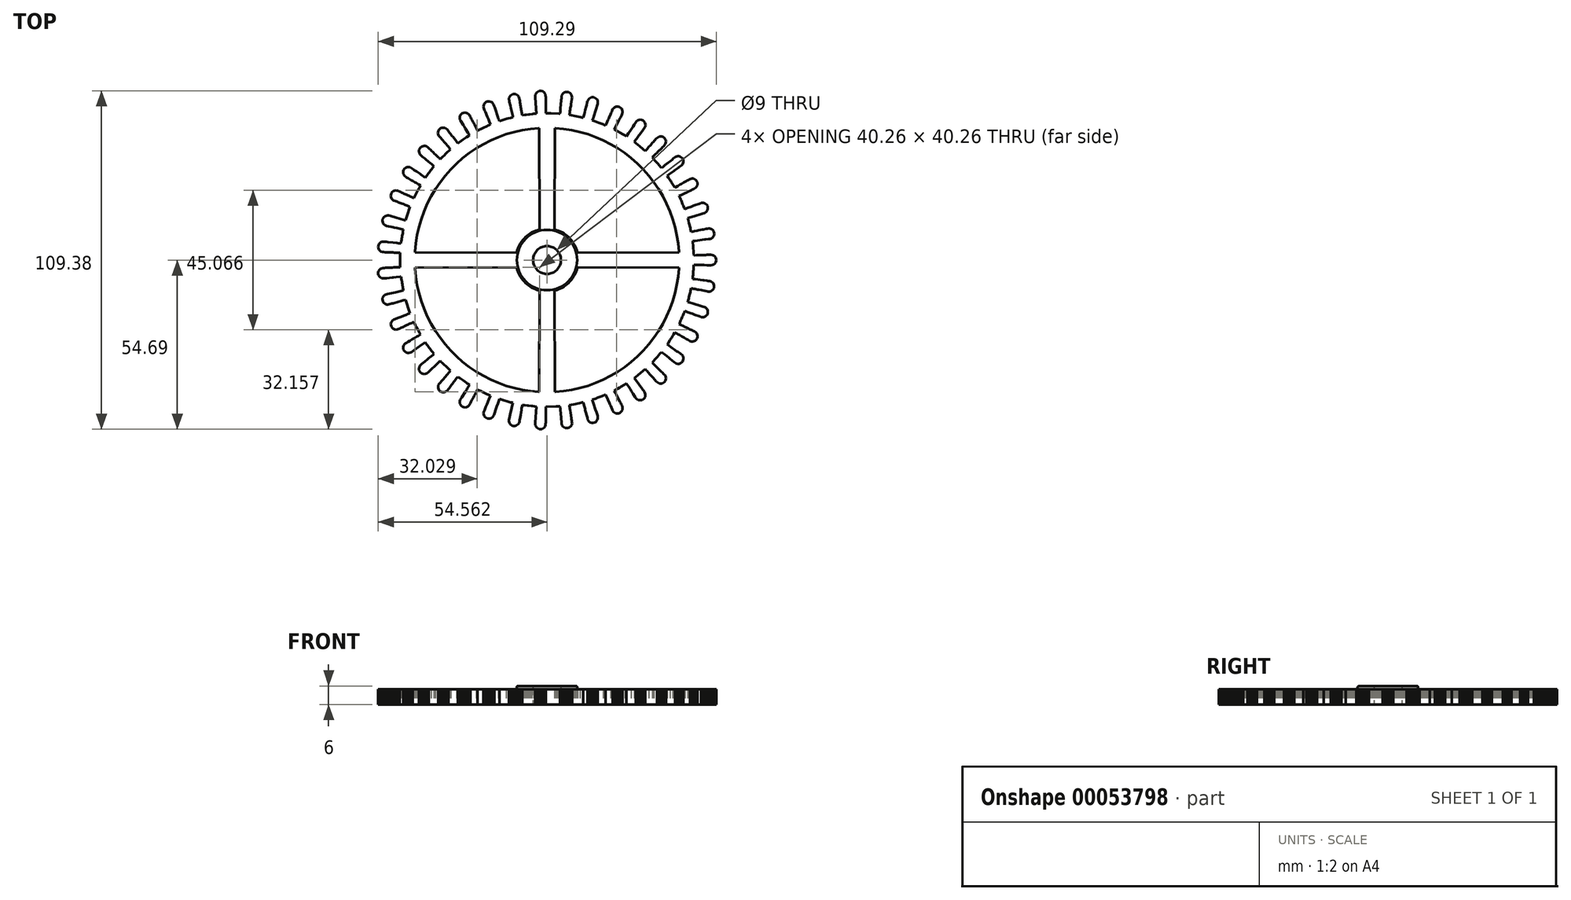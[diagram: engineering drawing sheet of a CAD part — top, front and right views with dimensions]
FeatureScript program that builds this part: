
annotation { "Feature Type Name" : "Feature", "Feature Type Description" : "" }
export const myFeature = defineFeature(function(context is Context, id is Id, definition is map)
    precondition{}
    {
        {
            var Q0;
            Q0=qCreatedBy(makeId("Top.planeOp"),FACE);
            var sketch = newSketch(context, id + "F0", { "sketchPlane" : qUnion([Q0])});
            skLineSegment(sketch, "E0", {"start": v(45.27, -1.52) * mm, "end": v(45.64, -1.53) * mm});
            skLineSegment(sketch, "E1", {"start": v(45.64, -1.53) * mm, "end": v(46.06, -1.55) * mm});
            skLineSegment(sketch, "E2", {"start": v(46.06, -1.55) * mm, "end": v(46.48, -1.56) * mm});
            skLineSegment(sketch, "E3", {"start": v(46.48, -1.56) * mm, "end": v(46.93, -1.58) * mm});
            skLineSegment(sketch, "E4", {"start": v(46.93, -1.58) * mm, "end": v(47.35, -1.59) * mm});
            skLineSegment(sketch, "E5", {"start": v(47.35, -1.59) * mm, "end": v(47.77, -1.6) * mm});
            skLineSegment(sketch, "E6", {"start": v(47.77, -1.6) * mm, "end": v(48.22, -1.62) * mm});
            skLineSegment(sketch, "E7", {"start": v(48.22, -1.62) * mm, "end": v(48.64, -1.63) * mm});
            skLineSegment(sketch, "E8", {"start": v(48.64, -1.63) * mm, "end": v(49.07, -1.64) * mm});
            skLineSegment(sketch, "E9", {"start": v(49.07, -1.64) * mm, "end": v(49.52, -1.66) * mm});
            skLineSegment(sketch, "E10", {"start": v(49.52, -1.66) * mm, "end": v(49.94, -1.67) * mm});
            skLineSegment(sketch, "E11", {"start": v(49.94, -1.67) * mm, "end": v(50.36, -1.69) * mm});
            skLineSegment(sketch, "E12", {"start": v(50.36, -1.69) * mm, "end": v(50.8, -1.7) * mm});
            skLineSegment(sketch, "E13", {"start": v(50.8, -1.7) * mm, "end": v(51.25, -1.65) * mm});
            skLineSegment(sketch, "E14", {"start": v(51.25, -1.65) * mm, "end": v(51.67, -1.48) * mm});
            skLineSegment(sketch, "E15", {"start": v(51.67, -1.48) * mm, "end": v(52.03, -1.21) * mm});
            skLineSegment(sketch, "E16", {"start": v(52.03, -1.21) * mm, "end": v(52.3, -0.86) * mm});
            skLineSegment(sketch, "E17", {"start": v(52.3, -0.86) * mm, "end": v(52.48, -0.44) * mm});
            skLineSegment(sketch, "E18", {"start": v(52.48, -0.44) * mm, "end": v(52.53, 0) * mm});
            skLineSegment(sketch, "E19", {"start": v(52.53, 0) * mm, "end": v(52.48, 0.44) * mm});
            skLineSegment(sketch, "E20", {"start": v(52.48, 0.44) * mm, "end": v(52.3, 0.86) * mm});
            skLineSegment(sketch, "E21", {"start": v(52.3, 0.86) * mm, "end": v(52.03, 1.21) * mm});
            skLineSegment(sketch, "E22", {"start": v(52.03, 1.21) * mm, "end": v(51.67, 1.48) * mm});
            skLineSegment(sketch, "E23", {"start": v(51.67, 1.48) * mm, "end": v(51.25, 1.65) * mm});
            skLineSegment(sketch, "E24", {"start": v(51.25, 1.65) * mm, "end": v(50.8, 1.7) * mm});
            skLineSegment(sketch, "E25", {"start": v(50.8, 1.7) * mm, "end": v(50.39, 1.69) * mm});
            skLineSegment(sketch, "E26", {"start": v(50.39, 1.69) * mm, "end": v(49.96, 1.67) * mm});
            skLineSegment(sketch, "E27", {"start": v(49.96, 1.67) * mm, "end": v(49.52, 1.66) * mm});
            skLineSegment(sketch, "E28", {"start": v(49.52, 1.66) * mm, "end": v(49.1, 1.65) * mm});
            skLineSegment(sketch, "E29", {"start": v(49.1, 1.65) * mm, "end": v(48.67, 1.63) * mm});
            skLineSegment(sketch, "E30", {"start": v(48.67, 1.63) * mm, "end": v(48.22, 1.62) * mm});
            skLineSegment(sketch, "E31", {"start": v(48.22, 1.62) * mm, "end": v(47.8, 1.6) * mm});
            skLineSegment(sketch, "E32", {"start": v(47.8, 1.6) * mm, "end": v(47.38, 1.6) * mm});
            skLineSegment(sketch, "E33", {"start": v(47.38, 1.6) * mm, "end": v(46.93, 1.58) * mm});
            skLineSegment(sketch, "E34", {"start": v(46.93, 1.58) * mm, "end": v(46.51, 1.56) * mm});
            skLineSegment(sketch, "E35", {"start": v(46.51, 1.56) * mm, "end": v(46.09, 1.55) * mm});
            skLineSegment(sketch, "E36", {"start": v(46.09, 1.55) * mm, "end": v(45.64, 1.53) * mm});
            skLineSegment(sketch, "E37", {"start": v(45.64, 1.53) * mm, "end": v(45.27, 1.52) * mm});
            skLineSegment(sketch, "E38", {"start": v(45.27, 1.52) * mm, "end": v(45.24, 1.94) * mm});
            skLineSegment(sketch, "E39", {"start": v(45.24, 1.94) * mm, "end": v(45.2, 2.36) * mm});
            skLineSegment(sketch, "E40", {"start": v(45.2, 2.36) * mm, "end": v(45.17, 2.78) * mm});
            skLineSegment(sketch, "E41", {"start": v(45.17, 2.78) * mm, "end": v(45.13, 3.2) * mm});
            skLineSegment(sketch, "E42", {"start": v(45.13, 3.2) * mm, "end": v(45.1, 3.62) * mm});
            skLineSegment(sketch, "E43", {"start": v(45.1, 3.62) * mm, "end": v(45.07, 4.04) * mm});
            skLineSegment(sketch, "E44", {"start": v(45.07, 4.04) * mm, "end": v(45.03, 4.46) * mm});
            skLineSegment(sketch, "E45", {"start": v(45.03, 4.46) * mm, "end": v(45, 4.88) * mm});
            skLineSegment(sketch, "E46", {"start": v(45, 4.88) * mm, "end": v(44.97, 5.3) * mm});
            skLineSegment(sketch, "E47", {"start": v(44.97, 5.3) * mm, "end": v(44.93, 5.72) * mm});
            skLineSegment(sketch, "E48", {"start": v(44.93, 5.72) * mm, "end": v(44.9, 6.11) * mm});
            skLineSegment(sketch, "E49", {"start": v(44.9, 6.11) * mm, "end": v(45.32, 6.17) * mm});
            skLineSegment(sketch, "E50", {"start": v(45.32, 6.17) * mm, "end": v(45.74, 6.22) * mm});
            skLineSegment(sketch, "E51", {"start": v(45.74, 6.22) * mm, "end": v(46.18, 6.28) * mm});
            skLineSegment(sketch, "E52", {"start": v(46.18, 6.28) * mm, "end": v(46.6, 6.33) * mm});
            skLineSegment(sketch, "E53", {"start": v(46.6, 6.33) * mm, "end": v(47.02, 6.39) * mm});
            skLineSegment(sketch, "E54", {"start": v(47.02, 6.39) * mm, "end": v(47.46, 6.44) * mm});
            skLineSegment(sketch, "E55", {"start": v(47.46, 6.44) * mm, "end": v(47.88, 6.5) * mm});
            skLineSegment(sketch, "E56", {"start": v(47.88, 6.5) * mm, "end": v(48.3, 6.55) * mm});
            skLineSegment(sketch, "E57", {"start": v(48.3, 6.55) * mm, "end": v(48.75, 6.61) * mm});
            skLineSegment(sketch, "E58", {"start": v(48.75, 6.61) * mm, "end": v(49.16, 6.66) * mm});
            skLineSegment(sketch, "E59", {"start": v(49.16, 6.66) * mm, "end": v(49.58, 6.72) * mm});
            skLineSegment(sketch, "E60", {"start": v(49.58, 6.72) * mm, "end": v(50.03, 6.78) * mm});
            skLineSegment(sketch, "E61", {"start": v(50.03, 6.78) * mm, "end": v(50.48, 6.84) * mm});
            skLineSegment(sketch, "E62", {"start": v(50.48, 6.84) * mm, "end": v(50.9, 6.99) * mm});
            skLineSegment(sketch, "E63", {"start": v(50.9, 6.99) * mm, "end": v(51.28, 7.24) * mm});
            skLineSegment(sketch, "E64", {"start": v(51.28, 7.24) * mm, "end": v(51.57, 7.58) * mm});
            skLineSegment(sketch, "E65", {"start": v(51.57, 7.58) * mm, "end": v(51.76, 7.98) * mm});
            skLineSegment(sketch, "E66", {"start": v(51.76, 7.98) * mm, "end": v(51.85, 8.42) * mm});
            skLineSegment(sketch, "E67", {"start": v(51.85, 8.42) * mm, "end": v(51.8, 8.87) * mm});
            skLineSegment(sketch, "E68", {"start": v(51.8, 8.87) * mm, "end": v(51.66, 9.29) * mm});
            skLineSegment(sketch, "E69", {"start": v(51.66, 9.29) * mm, "end": v(51.4, 9.66) * mm});
            skLineSegment(sketch, "E70", {"start": v(51.4, 9.66) * mm, "end": v(51.06, 9.94) * mm});
            skLineSegment(sketch, "E71", {"start": v(51.06, 9.94) * mm, "end": v(50.65, 10.13) * mm});
            skLineSegment(sketch, "E72", {"start": v(50.65, 10.13) * mm, "end": v(50.2, 10.2) * mm});
            skLineSegment(sketch, "E73", {"start": v(50.2, 10.2) * mm, "end": v(50.12, 10.2) * mm});
            skLineSegment(sketch, "E74", {"start": v(50.12, 10.2) * mm, "end": v(49.67, 10.15) * mm});
            skLineSegment(sketch, "E75", {"start": v(49.67, 10.15) * mm, "end": v(49.25, 10.06) * mm});
            skLineSegment(sketch, "E76", {"start": v(49.25, 10.06) * mm, "end": v(48.84, 9.98) * mm});
            skLineSegment(sketch, "E77", {"start": v(48.84, 9.98) * mm, "end": v(48.4, 9.9) * mm});
            skLineSegment(sketch, "E78", {"start": v(48.4, 9.9) * mm, "end": v(47.98, 9.82) * mm});
            skLineSegment(sketch, "E79", {"start": v(47.98, 9.82) * mm, "end": v(47.57, 9.74) * mm});
            skLineSegment(sketch, "E80", {"start": v(47.57, 9.74) * mm, "end": v(47.13, 9.65) * mm});
            skLineSegment(sketch, "E81", {"start": v(47.13, 9.65) * mm, "end": v(46.72, 9.57) * mm});
            skLineSegment(sketch, "E82", {"start": v(46.72, 9.57) * mm, "end": v(46.3, 9.49) * mm});
            skLineSegment(sketch, "E83", {"start": v(46.3, 9.49) * mm, "end": v(45.86, 9.4) * mm});
            skLineSegment(sketch, "E84", {"start": v(45.86, 9.4) * mm, "end": v(45.45, 9.32) * mm});
            skLineSegment(sketch, "E85", {"start": v(45.45, 9.32) * mm, "end": v(45.03, 9.24) * mm});
            skLineSegment(sketch, "E86", {"start": v(45.03, 9.24) * mm, "end": v(44.6, 9.15) * mm});
            skLineSegment(sketch, "E87", {"start": v(44.6, 9.15) * mm, "end": v(44.41, 9.12) * mm});
            skLineSegment(sketch, "E88", {"start": v(44.41, 9.12) * mm, "end": v(44.31, 9.53) * mm});
            skLineSegment(sketch, "E89", {"start": v(44.31, 9.53) * mm, "end": v(44.2, 9.94) * mm});
            skLineSegment(sketch, "E90", {"start": v(44.2, 9.94) * mm, "end": v(44.1, 10.35) * mm});
            skLineSegment(sketch, "E91", {"start": v(44.1, 10.35) * mm, "end": v(44, 10.75) * mm});
            skLineSegment(sketch, "E92", {"start": v(44, 10.75) * mm, "end": v(43.9, 11.16) * mm});
            skLineSegment(sketch, "E93", {"start": v(43.9, 11.16) * mm, "end": v(43.8, 11.57) * mm});
            skLineSegment(sketch, "E94", {"start": v(43.8, 11.57) * mm, "end": v(43.7, 11.98) * mm});
            skLineSegment(sketch, "E95", {"start": v(43.7, 11.98) * mm, "end": v(43.6, 12.4) * mm});
            skLineSegment(sketch, "E96", {"start": v(43.6, 12.4) * mm, "end": v(43.5, 12.8) * mm});
            skLineSegment(sketch, "E97", {"start": v(43.5, 12.8) * mm, "end": v(43.4, 13.21) * mm});
            skLineSegment(sketch, "E98", {"start": v(43.4, 13.21) * mm, "end": v(43.3, 13.59) * mm});
            skLineSegment(sketch, "E99", {"start": v(43.3, 13.59) * mm, "end": v(43.71, 13.7) * mm});
            skLineSegment(sketch, "E100", {"start": v(43.71, 13.7) * mm, "end": v(44.12, 13.83) * mm});
            skLineSegment(sketch, "E101", {"start": v(44.12, 13.83) * mm, "end": v(44.55, 13.96) * mm});
            skLineSegment(sketch, "E102", {"start": v(44.55, 13.96) * mm, "end": v(44.95, 14.08) * mm});
            skLineSegment(sketch, "E103", {"start": v(44.95, 14.08) * mm, "end": v(45.36, 14.2) * mm});
            skLineSegment(sketch, "E104", {"start": v(45.36, 14.2) * mm, "end": v(45.79, 14.33) * mm});
            skLineSegment(sketch, "E105", {"start": v(45.79, 14.33) * mm, "end": v(46.2, 14.45) * mm});
            skLineSegment(sketch, "E106", {"start": v(46.2, 14.45) * mm, "end": v(46.6, 14.57) * mm});
            skLineSegment(sketch, "E107", {"start": v(46.6, 14.57) * mm, "end": v(47.03, 14.7) * mm});
            skLineSegment(sketch, "E108", {"start": v(47.03, 14.7) * mm, "end": v(47.43, 14.82) * mm});
            skLineSegment(sketch, "E109", {"start": v(47.43, 14.82) * mm, "end": v(47.83, 14.94) * mm});
            skLineSegment(sketch, "E110", {"start": v(47.83, 14.94) * mm, "end": v(48.26, 15.07) * mm});
            skLineSegment(sketch, "E111", {"start": v(48.26, 15.07) * mm, "end": v(48.7, 15.2) * mm});
            skLineSegment(sketch, "E112", {"start": v(48.7, 15.2) * mm, "end": v(49.1, 15.41) * mm});
            skLineSegment(sketch, "E113", {"start": v(49.1, 15.41) * mm, "end": v(49.42, 15.72) * mm});
            skLineSegment(sketch, "E114", {"start": v(49.42, 15.72) * mm, "end": v(49.66, 16.1) * mm});
            skLineSegment(sketch, "E115", {"start": v(49.66, 16.1) * mm, "end": v(49.79, 16.53) * mm});
            skLineSegment(sketch, "E116", {"start": v(49.79, 16.53) * mm, "end": v(49.8, 16.98) * mm});
            skLineSegment(sketch, "E117", {"start": v(49.8, 16.98) * mm, "end": v(49.69, 17.42) * mm});
            skLineSegment(sketch, "E118", {"start": v(49.69, 17.42) * mm, "end": v(49.47, 17.8) * mm});
            skLineSegment(sketch, "E119", {"start": v(49.47, 17.8) * mm, "end": v(49.16, 18.13) * mm});
            skLineSegment(sketch, "E120", {"start": v(49.16, 18.13) * mm, "end": v(48.77, 18.36) * mm});
            skLineSegment(sketch, "E121", {"start": v(48.77, 18.36) * mm, "end": v(48.34, 18.48) * mm});
            skLineSegment(sketch, "E122", {"start": v(48.34, 18.48) * mm, "end": v(48.07, 18.5) * mm});
            skLineSegment(sketch, "E123", {"start": v(48.07, 18.5) * mm, "end": v(47.63, 18.43) * mm});
            skLineSegment(sketch, "E124", {"start": v(47.63, 18.43) * mm, "end": v(47.2, 18.27) * mm});
            skLineSegment(sketch, "E125", {"start": v(47.2, 18.27) * mm, "end": v(46.8, 18.12) * mm});
            skLineSegment(sketch, "E126", {"start": v(46.8, 18.12) * mm, "end": v(46.4, 17.98) * mm});
            skLineSegment(sketch, "E127", {"start": v(46.4, 17.98) * mm, "end": v(45.98, 17.82) * mm});
            skLineSegment(sketch, "E128", {"start": v(45.98, 17.82) * mm, "end": v(45.59, 17.68) * mm});
            skLineSegment(sketch, "E129", {"start": v(45.59, 17.68) * mm, "end": v(45.2, 17.53) * mm});
            skLineSegment(sketch, "E130", {"start": v(45.2, 17.53) * mm, "end": v(44.77, 17.37) * mm});
            skLineSegment(sketch, "E131", {"start": v(44.77, 17.37) * mm, "end": v(44.37, 17.23) * mm});
            skLineSegment(sketch, "E132", {"start": v(44.37, 17.23) * mm, "end": v(43.98, 17.08) * mm});
            skLineSegment(sketch, "E133", {"start": v(43.98, 17.08) * mm, "end": v(43.56, 16.92) * mm});
            skLineSegment(sketch, "E134", {"start": v(43.56, 16.92) * mm, "end": v(43.16, 16.78) * mm});
            skLineSegment(sketch, "E135", {"start": v(43.16, 16.78) * mm, "end": v(42.77, 16.63) * mm});
            skLineSegment(sketch, "E136", {"start": v(42.77, 16.63) * mm, "end": v(42.35, 16.48) * mm});
            skLineSegment(sketch, "E137", {"start": v(42.35, 16.48) * mm, "end": v(42.18, 16.86) * mm});
            skLineSegment(sketch, "E138", {"start": v(42.18, 16.86) * mm, "end": v(42.01, 17.25) * mm});
            skLineSegment(sketch, "E139", {"start": v(42.01, 17.25) * mm, "end": v(41.85, 17.64) * mm});
            skLineSegment(sketch, "E140", {"start": v(41.85, 17.64) * mm, "end": v(41.68, 18.03) * mm});
            skLineSegment(sketch, "E141", {"start": v(41.68, 18.03) * mm, "end": v(41.52, 18.42) * mm});
            skLineSegment(sketch, "E142", {"start": v(41.52, 18.42) * mm, "end": v(41.35, 18.8) * mm});
            skLineSegment(sketch, "E143", {"start": v(41.35, 18.8) * mm, "end": v(41.19, 19.2) * mm});
            skLineSegment(sketch, "E144", {"start": v(41.19, 19.2) * mm, "end": v(41.02, 19.58) * mm});
            skLineSegment(sketch, "E145", {"start": v(41.02, 19.58) * mm, "end": v(40.86, 19.97) * mm});
            skLineSegment(sketch, "E146", {"start": v(40.86, 19.97) * mm, "end": v(40.7, 20.35) * mm});
            skLineSegment(sketch, "E147", {"start": v(40.7, 20.35) * mm, "end": v(40.54, 20.71) * mm});
            skLineSegment(sketch, "E148", {"start": v(40.54, 20.71) * mm, "end": v(40.92, 20.9) * mm});
            skLineSegment(sketch, "E149", {"start": v(40.92, 20.9) * mm, "end": v(41.3, 21.08) * mm});
            skLineSegment(sketch, "E150", {"start": v(41.3, 21.08) * mm, "end": v(41.7, 21.28) * mm});
            skLineSegment(sketch, "E151", {"start": v(41.7, 21.28) * mm, "end": v(42.08, 21.46) * mm});
            skLineSegment(sketch, "E152", {"start": v(42.08, 21.46) * mm, "end": v(42.46, 21.64) * mm});
            skLineSegment(sketch, "E153", {"start": v(42.46, 21.64) * mm, "end": v(42.87, 21.84) * mm});
            skLineSegment(sketch, "E154", {"start": v(42.87, 21.84) * mm, "end": v(43.25, 22.02) * mm});
            skLineSegment(sketch, "E155", {"start": v(43.25, 22.02) * mm, "end": v(43.63, 22.2) * mm});
            skLineSegment(sketch, "E156", {"start": v(43.63, 22.2) * mm, "end": v(44.03, 22.4) * mm});
            skLineSegment(sketch, "E157", {"start": v(44.03, 22.4) * mm, "end": v(44.4, 22.59) * mm});
            skLineSegment(sketch, "E158", {"start": v(44.4, 22.59) * mm, "end": v(44.79, 22.77) * mm});
            skLineSegment(sketch, "E159", {"start": v(44.79, 22.77) * mm, "end": v(45.2, 22.97) * mm});
            skLineSegment(sketch, "E160", {"start": v(45.2, 22.97) * mm, "end": v(45.6, 23.17) * mm});
            skLineSegment(sketch, "E161", {"start": v(45.6, 23.17) * mm, "end": v(45.96, 23.44) * mm});
            skLineSegment(sketch, "E162", {"start": v(45.96, 23.44) * mm, "end": v(46.23, 23.8) * mm});
            skLineSegment(sketch, "E163", {"start": v(46.23, 23.8) * mm, "end": v(46.4, 24.21) * mm});
            skLineSegment(sketch, "E164", {"start": v(46.4, 24.21) * mm, "end": v(46.46, 24.66) * mm});
            skLineSegment(sketch, "E165", {"start": v(46.46, 24.66) * mm, "end": v(46.4, 25.1) * mm});
            skLineSegment(sketch, "E166", {"start": v(46.4, 25.1) * mm, "end": v(46.22, 25.51) * mm});
            skLineSegment(sketch, "E167", {"start": v(46.22, 25.51) * mm, "end": v(45.94, 25.87) * mm});
            skLineSegment(sketch, "E168", {"start": v(45.94, 25.87) * mm, "end": v(45.58, 26.13) * mm});
            skLineSegment(sketch, "E169", {"start": v(45.58, 26.13) * mm, "end": v(45.17, 26.3) * mm});
            skLineSegment(sketch, "E170", {"start": v(45.17, 26.3) * mm, "end": v(44.72, 26.35) * mm});
            skLineSegment(sketch, "E171", {"start": v(44.72, 26.35) * mm, "end": v(44.28, 26.28) * mm});
            skLineSegment(sketch, "E172", {"start": v(44.28, 26.28) * mm, "end": v(43.9, 26.1) * mm});
            skLineSegment(sketch, "E173", {"start": v(43.9, 26.1) * mm, "end": v(43.52, 25.9) * mm});
            skLineSegment(sketch, "E174", {"start": v(43.52, 25.9) * mm, "end": v(43.14, 25.68) * mm});
            skLineSegment(sketch, "E175", {"start": v(43.14, 25.68) * mm, "end": v(42.78, 25.48) * mm});
            skLineSegment(sketch, "E176", {"start": v(42.78, 25.48) * mm, "end": v(42.4, 25.27) * mm});
            skLineSegment(sketch, "E177", {"start": v(42.4, 25.27) * mm, "end": v(42.02, 25.05) * mm});
            skLineSegment(sketch, "E178", {"start": v(42.02, 25.05) * mm, "end": v(41.65, 24.84) * mm});
            skLineSegment(sketch, "E179", {"start": v(41.65, 24.84) * mm, "end": v(41.28, 24.63) * mm});
            skLineSegment(sketch, "E180", {"start": v(41.28, 24.63) * mm, "end": v(40.9, 24.4) * mm});
            skLineSegment(sketch, "E181", {"start": v(40.9, 24.4) * mm, "end": v(40.53, 24.2) * mm});
            skLineSegment(sketch, "E182", {"start": v(40.53, 24.2) * mm, "end": v(40.16, 24) * mm});
            skLineSegment(sketch, "E183", {"start": v(40.16, 24) * mm, "end": v(39.77, 23.77) * mm});
            skLineSegment(sketch, "E184", {"start": v(39.77, 23.77) * mm, "end": v(39.4, 23.56) * mm});
            skLineSegment(sketch, "E185", {"start": v(39.4, 23.56) * mm, "end": v(39.13, 23.4) * mm});
            skLineSegment(sketch, "E186", {"start": v(39.13, 23.4) * mm, "end": v(38.9, 23.76) * mm});
            skLineSegment(sketch, "E187", {"start": v(38.9, 23.76) * mm, "end": v(38.67, 24.12) * mm});
            skLineSegment(sketch, "E188", {"start": v(38.67, 24.12) * mm, "end": v(38.45, 24.48) * mm});
            skLineSegment(sketch, "E189", {"start": v(38.45, 24.48) * mm, "end": v(38.22, 24.83) * mm});
            skLineSegment(sketch, "E190", {"start": v(38.22, 24.83) * mm, "end": v(38, 25.19) * mm});
            skLineSegment(sketch, "E191", {"start": v(38, 25.19) * mm, "end": v(37.77, 25.55) * mm});
            skLineSegment(sketch, "E192", {"start": v(37.77, 25.55) * mm, "end": v(37.55, 25.9) * mm});
            skLineSegment(sketch, "E193", {"start": v(37.55, 25.9) * mm, "end": v(37.32, 26.26) * mm});
            skLineSegment(sketch, "E194", {"start": v(37.32, 26.26) * mm, "end": v(37.1, 26.61) * mm});
            skLineSegment(sketch, "E195", {"start": v(37.1, 26.61) * mm, "end": v(36.87, 26.97) * mm});
            skLineSegment(sketch, "E196", {"start": v(36.87, 26.97) * mm, "end": v(36.66, 27.3) * mm});
            skLineSegment(sketch, "E197", {"start": v(36.66, 27.3) * mm, "end": v(37, 27.54) * mm});
            skLineSegment(sketch, "E198", {"start": v(37, 27.54) * mm, "end": v(37.35, 27.78) * mm});
            skLineSegment(sketch, "E199", {"start": v(37.35, 27.78) * mm, "end": v(37.72, 28.04) * mm});
            skLineSegment(sketch, "E200", {"start": v(37.72, 28.04) * mm, "end": v(38.07, 28.28) * mm});
            skLineSegment(sketch, "E201", {"start": v(38.07, 28.28) * mm, "end": v(38.41, 28.53) * mm});
            skLineSegment(sketch, "E202", {"start": v(38.41, 28.53) * mm, "end": v(38.78, 28.79) * mm});
            skLineSegment(sketch, "E203", {"start": v(38.78, 28.79) * mm, "end": v(39.13, 29.03) * mm});
            skLineSegment(sketch, "E204", {"start": v(39.13, 29.03) * mm, "end": v(39.47, 29.27) * mm});
            skLineSegment(sketch, "E205", {"start": v(39.47, 29.27) * mm, "end": v(39.84, 29.53) * mm});
            skLineSegment(sketch, "E206", {"start": v(39.84, 29.53) * mm, "end": v(40.18, 29.77) * mm});
            skLineSegment(sketch, "E207", {"start": v(40.18, 29.77) * mm, "end": v(40.53, 30.01) * mm});
            skLineSegment(sketch, "E208", {"start": v(40.53, 30.01) * mm, "end": v(40.9, 30.27) * mm});
            skLineSegment(sketch, "E209", {"start": v(40.9, 30.27) * mm, "end": v(41.27, 30.54) * mm});
            skLineSegment(sketch, "E210", {"start": v(41.27, 30.54) * mm, "end": v(41.58, 30.86) * mm});
            skLineSegment(sketch, "E211", {"start": v(41.58, 30.86) * mm, "end": v(41.79, 31.26) * mm});
            skLineSegment(sketch, "E212", {"start": v(41.79, 31.26) * mm, "end": v(41.9, 31.7) * mm});
            skLineSegment(sketch, "E213", {"start": v(41.9, 31.7) * mm, "end": v(41.87, 32.14) * mm});
            skLineSegment(sketch, "E214", {"start": v(41.87, 32.14) * mm, "end": v(41.74, 32.57) * mm});
            skLineSegment(sketch, "E215", {"start": v(41.74, 32.57) * mm, "end": v(41.5, 32.95) * mm});
            skLineSegment(sketch, "E216", {"start": v(41.5, 32.95) * mm, "end": v(41.17, 33.25) * mm});
            skLineSegment(sketch, "E217", {"start": v(41.17, 33.25) * mm, "end": v(40.77, 33.46) * mm});
            skLineSegment(sketch, "E218", {"start": v(40.77, 33.46) * mm, "end": v(40.33, 33.55) * mm});
            skLineSegment(sketch, "E219", {"start": v(40.33, 33.55) * mm, "end": v(40.15, 33.56) * mm});
            skLineSegment(sketch, "E220", {"start": v(40.15, 33.56) * mm, "end": v(39.71, 33.49) * mm});
            skLineSegment(sketch, "E221", {"start": v(39.71, 33.49) * mm, "end": v(39.3, 33.3) * mm});
            skLineSegment(sketch, "E222", {"start": v(39.3, 33.3) * mm, "end": v(38.97, 33.05) * mm});
            skLineSegment(sketch, "E223", {"start": v(38.97, 33.05) * mm, "end": v(38.64, 32.79) * mm});
            skLineSegment(sketch, "E224", {"start": v(38.64, 32.79) * mm, "end": v(38.3, 32.5) * mm});
            skLineSegment(sketch, "E225", {"start": v(38.3, 32.5) * mm, "end": v(37.96, 32.24) * mm});
            skLineSegment(sketch, "E226", {"start": v(37.96, 32.24) * mm, "end": v(37.63, 31.98) * mm});
            skLineSegment(sketch, "E227", {"start": v(37.63, 31.98) * mm, "end": v(37.28, 31.7) * mm});
            skLineSegment(sketch, "E228", {"start": v(37.28, 31.7) * mm, "end": v(36.95, 31.44) * mm});
            skLineSegment(sketch, "E229", {"start": v(36.95, 31.44) * mm, "end": v(36.63, 31.17) * mm});
            skLineSegment(sketch, "E230", {"start": v(36.63, 31.17) * mm, "end": v(36.28, 30.89) * mm});
            skLineSegment(sketch, "E231", {"start": v(36.28, 30.89) * mm, "end": v(35.95, 30.63) * mm});
            skLineSegment(sketch, "E232", {"start": v(35.95, 30.63) * mm, "end": v(35.62, 30.36) * mm});
            skLineSegment(sketch, "E233", {"start": v(35.62, 30.36) * mm, "end": v(35.27, 30.08) * mm});
            skLineSegment(sketch, "E234", {"start": v(35.27, 30.08) * mm, "end": v(34.94, 29.82) * mm});
            skLineSegment(sketch, "E235", {"start": v(34.94, 29.82) * mm, "end": v(34.84, 29.73) * mm});
            skLineSegment(sketch, "E236", {"start": v(34.84, 29.73) * mm, "end": v(34.56, 30.05) * mm});
            skLineSegment(sketch, "E237", {"start": v(34.56, 30.05) * mm, "end": v(34.28, 30.36) * mm});
            skLineSegment(sketch, "E238", {"start": v(34.28, 30.36) * mm, "end": v(34, 30.68) * mm});
            skLineSegment(sketch, "E239", {"start": v(34, 30.68) * mm, "end": v(33.72, 31) * mm});
            skLineSegment(sketch, "E240", {"start": v(33.72, 31) * mm, "end": v(33.44, 31.31) * mm});
            skLineSegment(sketch, "E241", {"start": v(33.44, 31.31) * mm, "end": v(33.16, 31.63) * mm});
            skLineSegment(sketch, "E242", {"start": v(33.16, 31.63) * mm, "end": v(32.88, 31.94) * mm});
            skLineSegment(sketch, "E243", {"start": v(32.88, 31.94) * mm, "end": v(32.6, 32.26) * mm});
            skLineSegment(sketch, "E244", {"start": v(32.6, 32.26) * mm, "end": v(32.32, 32.57) * mm});
            skLineSegment(sketch, "E245", {"start": v(32.32, 32.57) * mm, "end": v(32.04, 32.89) * mm});
            skLineSegment(sketch, "E246", {"start": v(32.04, 32.89) * mm, "end": v(31.78, 33.18) * mm});
            skLineSegment(sketch, "E247", {"start": v(31.78, 33.18) * mm, "end": v(32.08, 33.47) * mm});
            skLineSegment(sketch, "E248", {"start": v(32.08, 33.47) * mm, "end": v(32.39, 33.77) * mm});
            skLineSegment(sketch, "E249", {"start": v(32.39, 33.77) * mm, "end": v(32.7, 34.08) * mm});
            skLineSegment(sketch, "E250", {"start": v(32.7, 34.08) * mm, "end": v(33, 34.38) * mm});
            skLineSegment(sketch, "E251", {"start": v(33, 34.38) * mm, "end": v(33.31, 34.67) * mm});
            skLineSegment(sketch, "E252", {"start": v(33.31, 34.67) * mm, "end": v(33.63, 34.99) * mm});
            skLineSegment(sketch, "E253", {"start": v(33.63, 34.99) * mm, "end": v(33.93, 35.28) * mm});
            skLineSegment(sketch, "E254", {"start": v(33.93, 35.28) * mm, "end": v(34.24, 35.57) * mm});
            skLineSegment(sketch, "E255", {"start": v(34.24, 35.57) * mm, "end": v(34.56, 35.89) * mm});
            skLineSegment(sketch, "E256", {"start": v(34.56, 35.89) * mm, "end": v(34.86, 36.18) * mm});
            skLineSegment(sketch, "E257", {"start": v(34.86, 36.18) * mm, "end": v(35.16, 36.48) * mm});
            skLineSegment(sketch, "E258", {"start": v(35.16, 36.48) * mm, "end": v(35.48, 36.8) * mm});
            skLineSegment(sketch, "E259", {"start": v(35.48, 36.8) * mm, "end": v(35.8, 37.12) * mm});
            skLineSegment(sketch, "E260", {"start": v(35.8, 37.12) * mm, "end": v(36.06, 37.49) * mm});
            skLineSegment(sketch, "E261", {"start": v(36.06, 37.49) * mm, "end": v(36.2, 37.91) * mm});
            skLineSegment(sketch, "E262", {"start": v(36.2, 37.91) * mm, "end": v(36.24, 38.36) * mm});
            skLineSegment(sketch, "E263", {"start": v(36.24, 38.36) * mm, "end": v(36.15, 38.8) * mm});
            skLineSegment(sketch, "E264", {"start": v(36.15, 38.8) * mm, "end": v(35.95, 39.2) * mm});
            skLineSegment(sketch, "E265", {"start": v(35.95, 39.2) * mm, "end": v(35.65, 39.53) * mm});
            skLineSegment(sketch, "E266", {"start": v(35.65, 39.53) * mm, "end": v(35.27, 39.78) * mm});
            skLineSegment(sketch, "E267", {"start": v(35.27, 39.78) * mm, "end": v(34.85, 39.92) * mm});
            skLineSegment(sketch, "E268", {"start": v(34.85, 39.92) * mm, "end": v(34.58, 39.95) * mm});
            skLineSegment(sketch, "E269", {"start": v(34.58, 39.95) * mm, "end": v(34.13, 39.9) * mm});
            skLineSegment(sketch, "E270", {"start": v(34.13, 39.9) * mm, "end": v(33.72, 39.74) * mm});
            skLineSegment(sketch, "E271", {"start": v(33.72, 39.74) * mm, "end": v(33.36, 39.47) * mm});
            skLineSegment(sketch, "E272", {"start": v(33.36, 39.47) * mm, "end": v(33.05, 39.13) * mm});
            skLineSegment(sketch, "E273", {"start": v(33.05, 39.13) * mm, "end": v(32.76, 38.82) * mm});
            skLineSegment(sketch, "E274", {"start": v(32.76, 38.82) * mm, "end": v(32.48, 38.5) * mm});
            skLineSegment(sketch, "E275", {"start": v(32.48, 38.5) * mm, "end": v(32.18, 38.17) * mm});
            skLineSegment(sketch, "E276", {"start": v(32.18, 38.17) * mm, "end": v(31.9, 37.86) * mm});
            skLineSegment(sketch, "E277", {"start": v(31.9, 37.86) * mm, "end": v(31.62, 37.54) * mm});
            skLineSegment(sketch, "E278", {"start": v(31.62, 37.54) * mm, "end": v(31.32, 37.21) * mm});
            skLineSegment(sketch, "E279", {"start": v(31.32, 37.21) * mm, "end": v(31.03, 36.9) * mm});
            skLineSegment(sketch, "E280", {"start": v(31.03, 36.9) * mm, "end": v(30.75, 36.58) * mm});
            skLineSegment(sketch, "E281", {"start": v(30.75, 36.58) * mm, "end": v(30.45, 36.25) * mm});
            skLineSegment(sketch, "E282", {"start": v(30.45, 36.25) * mm, "end": v(30.17, 35.94) * mm});
            skLineSegment(sketch, "E283", {"start": v(30.17, 35.94) * mm, "end": v(29.89, 35.62) * mm});
            skLineSegment(sketch, "E284", {"start": v(29.89, 35.62) * mm, "end": v(29.59, 35.29) * mm});
            skLineSegment(sketch, "E285", {"start": v(29.59, 35.29) * mm, "end": v(29.26, 35.56) * mm});
            skLineSegment(sketch, "E286", {"start": v(29.26, 35.56) * mm, "end": v(28.93, 35.82) * mm});
            skLineSegment(sketch, "E287", {"start": v(28.93, 35.82) * mm, "end": v(28.6, 36.09) * mm});
            skLineSegment(sketch, "E288", {"start": v(28.6, 36.09) * mm, "end": v(28.28, 36.36) * mm});
            skLineSegment(sketch, "E289", {"start": v(28.28, 36.36) * mm, "end": v(27.95, 36.62) * mm});
            skLineSegment(sketch, "E290", {"start": v(27.95, 36.62) * mm, "end": v(27.63, 36.89) * mm});
            skLineSegment(sketch, "E291", {"start": v(27.63, 36.89) * mm, "end": v(27.3, 37.16) * mm});
            skLineSegment(sketch, "E292", {"start": v(27.3, 37.16) * mm, "end": v(26.97, 37.42) * mm});
            skLineSegment(sketch, "E293", {"start": v(26.97, 37.42) * mm, "end": v(26.65, 37.69) * mm});
            skLineSegment(sketch, "E294", {"start": v(26.65, 37.69) * mm, "end": v(26.32, 37.96) * mm});
            skLineSegment(sketch, "E295", {"start": v(26.32, 37.96) * mm, "end": v(26.02, 38.2) * mm});
            skLineSegment(sketch, "E296", {"start": v(26.02, 38.2) * mm, "end": v(26.27, 38.54) * mm});
            skLineSegment(sketch, "E297", {"start": v(26.27, 38.54) * mm, "end": v(26.52, 38.88) * mm});
            skLineSegment(sketch, "E298", {"start": v(26.52, 38.88) * mm, "end": v(26.79, 39.24) * mm});
            skLineSegment(sketch, "E299", {"start": v(26.79, 39.24) * mm, "end": v(27.04, 39.58) * mm});
            skLineSegment(sketch, "E300", {"start": v(27.04, 39.58) * mm, "end": v(27.29, 39.92) * mm});
            skLineSegment(sketch, "E301", {"start": v(27.29, 39.92) * mm, "end": v(27.56, 40.28) * mm});
            skLineSegment(sketch, "E302", {"start": v(27.56, 40.28) * mm, "end": v(27.8, 40.62) * mm});
            skLineSegment(sketch, "E303", {"start": v(27.8, 40.62) * mm, "end": v(28.06, 40.96) * mm});
            skLineSegment(sketch, "E304", {"start": v(28.06, 40.96) * mm, "end": v(28.32, 41.32) * mm});
            skLineSegment(sketch, "E305", {"start": v(28.32, 41.32) * mm, "end": v(28.57, 41.66) * mm});
            skLineSegment(sketch, "E306", {"start": v(28.57, 41.66) * mm, "end": v(28.83, 42) * mm});
            skLineSegment(sketch, "E307", {"start": v(28.83, 42) * mm, "end": v(29.1, 42.36) * mm});
            skLineSegment(sketch, "E308", {"start": v(29.1, 42.36) * mm, "end": v(29.36, 42.73) * mm});
            skLineSegment(sketch, "E309", {"start": v(29.36, 42.73) * mm, "end": v(29.55, 43.14) * mm});
            skLineSegment(sketch, "E310", {"start": v(29.55, 43.14) * mm, "end": v(29.63, 43.58) * mm});
            skLineSegment(sketch, "E311", {"start": v(29.63, 43.58) * mm, "end": v(29.58, 44.03) * mm});
            skLineSegment(sketch, "E312", {"start": v(29.58, 44.03) * mm, "end": v(29.43, 44.45) * mm});
            skLineSegment(sketch, "E313", {"start": v(29.43, 44.45) * mm, "end": v(29.17, 44.81) * mm});
            skLineSegment(sketch, "E314", {"start": v(29.17, 44.81) * mm, "end": v(28.82, 45.1) * mm});
            skLineSegment(sketch, "E315", {"start": v(28.82, 45.1) * mm, "end": v(28.4, 45.28) * mm});
            skLineSegment(sketch, "E316", {"start": v(28.4, 45.28) * mm, "end": v(27.97, 45.35) * mm});
            skLineSegment(sketch, "E317", {"start": v(27.97, 45.35) * mm, "end": v(27.52, 45.3) * mm});
            skLineSegment(sketch, "E318", {"start": v(27.52, 45.3) * mm, "end": v(27.1, 45.13) * mm});
            skLineSegment(sketch, "E319", {"start": v(27.1, 45.13) * mm, "end": v(26.74, 44.86) * mm});
            skLineSegment(sketch, "E320", {"start": v(26.74, 44.86) * mm, "end": v(26.49, 44.53) * mm});
            skLineSegment(sketch, "E321", {"start": v(26.49, 44.53) * mm, "end": v(26.25, 44.18) * mm});
            skLineSegment(sketch, "E322", {"start": v(26.25, 44.18) * mm, "end": v(26.01, 43.81) * mm});
            skLineSegment(sketch, "E323", {"start": v(26.01, 43.81) * mm, "end": v(25.78, 43.46) * mm});
            skLineSegment(sketch, "E324", {"start": v(25.78, 43.46) * mm, "end": v(25.56, 43.1) * mm});
            skLineSegment(sketch, "E325", {"start": v(25.56, 43.1) * mm, "end": v(25.31, 42.73) * mm});
            skLineSegment(sketch, "E326", {"start": v(25.31, 42.73) * mm, "end": v(25.08, 42.37) * mm});
            skLineSegment(sketch, "E327", {"start": v(25.08, 42.37) * mm, "end": v(24.86, 42.02) * mm});
            skLineSegment(sketch, "E328", {"start": v(24.86, 42.02) * mm, "end": v(24.61, 41.64) * mm});
            skLineSegment(sketch, "E329", {"start": v(24.61, 41.64) * mm, "end": v(24.39, 41.28) * mm});
            skLineSegment(sketch, "E330", {"start": v(24.39, 41.28) * mm, "end": v(24.16, 40.93) * mm});
            skLineSegment(sketch, "E331", {"start": v(24.16, 40.93) * mm, "end": v(23.91, 40.55) * mm});
            skLineSegment(sketch, "E332", {"start": v(23.91, 40.55) * mm, "end": v(23.69, 40.2) * mm});
            skLineSegment(sketch, "E333", {"start": v(23.69, 40.2) * mm, "end": v(23.51, 39.93) * mm});
            skLineSegment(sketch, "E334", {"start": v(23.51, 39.93) * mm, "end": v(23.15, 40.14) * mm});
            skLineSegment(sketch, "E335", {"start": v(23.15, 40.14) * mm, "end": v(22.78, 40.35) * mm});
            skLineSegment(sketch, "E336", {"start": v(22.78, 40.35) * mm, "end": v(22.42, 40.56) * mm});
            skLineSegment(sketch, "E337", {"start": v(22.42, 40.56) * mm, "end": v(22.05, 40.77) * mm});
            skLineSegment(sketch, "E338", {"start": v(22.05, 40.77) * mm, "end": v(21.69, 40.99) * mm});
            skLineSegment(sketch, "E339", {"start": v(21.69, 40.99) * mm, "end": v(21.32, 41.2) * mm});
            skLineSegment(sketch, "E340", {"start": v(21.32, 41.2) * mm, "end": v(20.96, 41.4) * mm});
            skLineSegment(sketch, "E341", {"start": v(20.96, 41.4) * mm, "end": v(20.6, 41.62) * mm});
            skLineSegment(sketch, "E342", {"start": v(20.6, 41.62) * mm, "end": v(20.23, 41.83) * mm});
            skLineSegment(sketch, "E343", {"start": v(20.23, 41.83) * mm, "end": v(19.86, 42.04) * mm});
            skLineSegment(sketch, "E344", {"start": v(19.86, 42.04) * mm, "end": v(19.53, 42.23) * mm});
            skLineSegment(sketch, "E345", {"start": v(19.53, 42.23) * mm, "end": v(19.72, 42.6) * mm});
            skLineSegment(sketch, "E346", {"start": v(19.72, 42.6) * mm, "end": v(19.91, 42.98) * mm});
            skLineSegment(sketch, "E347", {"start": v(19.91, 42.98) * mm, "end": v(20.12, 43.38) * mm});
            skLineSegment(sketch, "E348", {"start": v(20.12, 43.38) * mm, "end": v(20.31, 43.76) * mm});
            skLineSegment(sketch, "E349", {"start": v(20.31, 43.76) * mm, "end": v(20.5, 44.13) * mm});
            skLineSegment(sketch, "E350", {"start": v(20.5, 44.13) * mm, "end": v(20.7, 44.53) * mm});
            skLineSegment(sketch, "E351", {"start": v(20.7, 44.53) * mm, "end": v(20.9, 44.9) * mm});
            skLineSegment(sketch, "E352", {"start": v(20.9, 44.9) * mm, "end": v(21.1, 45.28) * mm});
            skLineSegment(sketch, "E353", {"start": v(21.1, 45.28) * mm, "end": v(21.3, 45.68) * mm});
            skLineSegment(sketch, "E354", {"start": v(21.3, 45.68) * mm, "end": v(21.5, 46.06) * mm});
            skLineSegment(sketch, "E355", {"start": v(21.5, 46.06) * mm, "end": v(21.69, 46.43) * mm});
            skLineSegment(sketch, "E356", {"start": v(21.69, 46.43) * mm, "end": v(21.9, 46.83) * mm});
            skLineSegment(sketch, "E357", {"start": v(21.9, 46.83) * mm, "end": v(22.1, 47.24) * mm});
            skLineSegment(sketch, "E358", {"start": v(22.1, 47.24) * mm, "end": v(22.22, 47.67) * mm});
            skLineSegment(sketch, "E359", {"start": v(22.22, 47.67) * mm, "end": v(22.22, 48.12) * mm});
            skLineSegment(sketch, "E360", {"start": v(22.22, 48.12) * mm, "end": v(22.11, 48.55) * mm});
            skLineSegment(sketch, "E361", {"start": v(22.11, 48.55) * mm, "end": v(21.89, 48.94) * mm});
            skLineSegment(sketch, "E362", {"start": v(21.89, 48.94) * mm, "end": v(21.57, 49.26) * mm});
            skLineSegment(sketch, "E363", {"start": v(21.57, 49.26) * mm, "end": v(21.18, 49.48) * mm});
            skLineSegment(sketch, "E364", {"start": v(21.18, 49.48) * mm, "end": v(20.75, 49.6) * mm});
            skLineSegment(sketch, "E365", {"start": v(20.75, 49.6) * mm, "end": v(20.57, 49.61) * mm});
            skLineSegment(sketch, "E366", {"start": v(20.57, 49.61) * mm, "end": v(20.12, 49.56) * mm});
            skLineSegment(sketch, "E367", {"start": v(20.12, 49.56) * mm, "end": v(19.7, 49.4) * mm});
            skLineSegment(sketch, "E368", {"start": v(19.7, 49.4) * mm, "end": v(19.35, 49.13) * mm});
            skLineSegment(sketch, "E369", {"start": v(19.35, 49.13) * mm, "end": v(19.07, 48.78) * mm});
            skLineSegment(sketch, "E370", {"start": v(19.07, 48.78) * mm, "end": v(18.9, 48.4) * mm});
            skLineSegment(sketch, "E371", {"start": v(18.9, 48.4) * mm, "end": v(18.72, 48) * mm});
            skLineSegment(sketch, "E372", {"start": v(18.72, 48) * mm, "end": v(18.55, 47.6) * mm});
            skLineSegment(sketch, "E373", {"start": v(18.55, 47.6) * mm, "end": v(18.38, 47.21) * mm});
            skLineSegment(sketch, "E374", {"start": v(18.38, 47.21) * mm, "end": v(18.2, 46.83) * mm});
            skLineSegment(sketch, "E375", {"start": v(18.2, 46.83) * mm, "end": v(18.03, 46.42) * mm});
            skLineSegment(sketch, "E376", {"start": v(18.03, 46.42) * mm, "end": v(17.86, 46.03) * mm});
            skLineSegment(sketch, "E377", {"start": v(17.86, 46.03) * mm, "end": v(17.7, 45.64) * mm});
            skLineSegment(sketch, "E378", {"start": v(17.7, 45.64) * mm, "end": v(17.51, 45.23) * mm});
            skLineSegment(sketch, "E379", {"start": v(17.51, 45.23) * mm, "end": v(17.34, 44.84) * mm});
            skLineSegment(sketch, "E380", {"start": v(17.34, 44.84) * mm, "end": v(17.18, 44.46) * mm});
            skLineSegment(sketch, "E381", {"start": v(17.18, 44.46) * mm, "end": v(17, 44.05) * mm});
            skLineSegment(sketch, "E382", {"start": v(17, 44.05) * mm, "end": v(16.83, 43.66) * mm});
            skLineSegment(sketch, "E383", {"start": v(16.83, 43.66) * mm, "end": v(16.78, 43.54) * mm});
            skLineSegment(sketch, "E384", {"start": v(16.78, 43.54) * mm, "end": v(16.38, 43.69) * mm});
            skLineSegment(sketch, "E385", {"start": v(16.38, 43.69) * mm, "end": v(15.99, 43.84) * mm});
            skLineSegment(sketch, "E386", {"start": v(15.99, 43.84) * mm, "end": v(15.6, 43.99) * mm});
            skLineSegment(sketch, "E387", {"start": v(15.6, 43.99) * mm, "end": v(15.2, 44.14) * mm});
            skLineSegment(sketch, "E388", {"start": v(15.2, 44.14) * mm, "end": v(14.8, 44.29) * mm});
            skLineSegment(sketch, "E389", {"start": v(14.8, 44.29) * mm, "end": v(14.41, 44.44) * mm});
            skLineSegment(sketch, "E390", {"start": v(14.41, 44.44) * mm, "end": v(14.02, 44.58) * mm});
            skLineSegment(sketch, "E391", {"start": v(14.02, 44.58) * mm, "end": v(13.62, 44.73) * mm});
            skLineSegment(sketch, "E392", {"start": v(13.62, 44.73) * mm, "end": v(13.23, 44.88) * mm});
            skLineSegment(sketch, "E393", {"start": v(13.23, 44.88) * mm, "end": v(12.83, 45.03) * mm});
            skLineSegment(sketch, "E394", {"start": v(12.83, 45.03) * mm, "end": v(12.47, 45.17) * mm});
            skLineSegment(sketch, "E395", {"start": v(12.47, 45.17) * mm, "end": v(12.6, 45.57) * mm});
            skLineSegment(sketch, "E396", {"start": v(12.6, 45.57) * mm, "end": v(12.73, 45.97) * mm});
            skLineSegment(sketch, "E397", {"start": v(12.73, 45.97) * mm, "end": v(12.87, 46.4) * mm});
            skLineSegment(sketch, "E398", {"start": v(12.87, 46.4) * mm, "end": v(13, 46.8) * mm});
            skLineSegment(sketch, "E399", {"start": v(13, 46.8) * mm, "end": v(13.13, 47.2) * mm});
            skLineSegment(sketch, "E400", {"start": v(13.13, 47.2) * mm, "end": v(13.27, 47.63) * mm});
            skLineSegment(sketch, "E401", {"start": v(13.27, 47.63) * mm, "end": v(13.4, 48.03) * mm});
            skLineSegment(sketch, "E402", {"start": v(13.4, 48.03) * mm, "end": v(13.53, 48.43) * mm});
            skLineSegment(sketch, "E403", {"start": v(13.53, 48.43) * mm, "end": v(13.67, 48.86) * mm});
            skLineSegment(sketch, "E404", {"start": v(13.67, 48.86) * mm, "end": v(13.8, 49.26) * mm});
            skLineSegment(sketch, "E405", {"start": v(13.8, 49.26) * mm, "end": v(13.93, 49.66) * mm});
            skLineSegment(sketch, "E406", {"start": v(13.93, 49.66) * mm, "end": v(14.07, 50.09) * mm});
            skLineSegment(sketch, "E407", {"start": v(14.07, 50.09) * mm, "end": v(14.2, 50.53) * mm});
            skLineSegment(sketch, "E408", {"start": v(14.2, 50.53) * mm, "end": v(14.26, 50.97) * mm});
            skLineSegment(sketch, "E409", {"start": v(14.26, 50.97) * mm, "end": v(14.19, 51.42) * mm});
            skLineSegment(sketch, "E410", {"start": v(14.19, 51.42) * mm, "end": v(14, 51.83) * mm});
            skLineSegment(sketch, "E411", {"start": v(14, 51.83) * mm, "end": v(13.73, 52.17) * mm});
            skLineSegment(sketch, "E412", {"start": v(13.73, 52.17) * mm, "end": v(13.36, 52.44) * mm});
            skLineSegment(sketch, "E413", {"start": v(13.36, 52.44) * mm, "end": v(12.94, 52.6) * mm});
            skLineSegment(sketch, "E414", {"start": v(12.94, 52.6) * mm, "end": v(12.59, 52.64) * mm});
            skLineSegment(sketch, "E415", {"start": v(12.59, 52.64) * mm, "end": v(12.14, 52.59) * mm});
            skLineSegment(sketch, "E416", {"start": v(12.14, 52.59) * mm, "end": v(11.72, 52.42) * mm});
            skLineSegment(sketch, "E417", {"start": v(11.72, 52.42) * mm, "end": v(11.37, 52.15) * mm});
            skLineSegment(sketch, "E418", {"start": v(11.37, 52.15) * mm, "end": v(11.09, 51.8) * mm});
            skLineSegment(sketch, "E419", {"start": v(11.09, 51.8) * mm, "end": v(10.92, 51.39) * mm});
            skLineSegment(sketch, "E420", {"start": v(10.92, 51.39) * mm, "end": v(10.81, 50.98) * mm});
            skLineSegment(sketch, "E421", {"start": v(10.81, 50.98) * mm, "end": v(10.7, 50.57) * mm});
            skLineSegment(sketch, "E422", {"start": v(10.7, 50.57) * mm, "end": v(10.6, 50.13) * mm});
            skLineSegment(sketch, "E423", {"start": v(10.6, 50.13) * mm, "end": v(10.5, 49.73) * mm});
            skLineSegment(sketch, "E424", {"start": v(10.5, 49.73) * mm, "end": v(10.39, 49.32) * mm});
            skLineSegment(sketch, "E425", {"start": v(10.39, 49.32) * mm, "end": v(10.28, 48.88) * mm});
            skLineSegment(sketch, "E426", {"start": v(10.28, 48.88) * mm, "end": v(10.17, 48.47) * mm});
            skLineSegment(sketch, "E427", {"start": v(10.17, 48.47) * mm, "end": v(10.07, 48.06) * mm});
            skLineSegment(sketch, "E428", {"start": v(10.07, 48.06) * mm, "end": v(9.96, 47.63) * mm});
            skLineSegment(sketch, "E429", {"start": v(9.96, 47.63) * mm, "end": v(9.85, 47.22) * mm});
            skLineSegment(sketch, "E430", {"start": v(9.85, 47.22) * mm, "end": v(9.75, 46.81) * mm});
            skLineSegment(sketch, "E431", {"start": v(9.75, 46.81) * mm, "end": v(9.64, 46.38) * mm});
            skLineSegment(sketch, "E432", {"start": v(9.64, 46.38) * mm, "end": v(9.55, 46.02) * mm});
            skLineSegment(sketch, "E433", {"start": v(9.55, 46.02) * mm, "end": v(9.13, 46.1) * mm});
            skLineSegment(sketch, "E434", {"start": v(9.13, 46.1) * mm, "end": v(8.72, 46.19) * mm});
            skLineSegment(sketch, "E435", {"start": v(8.72, 46.19) * mm, "end": v(8.3, 46.27) * mm});
            skLineSegment(sketch, "E436", {"start": v(8.3, 46.27) * mm, "end": v(7.9, 46.36) * mm});
            skLineSegment(sketch, "E437", {"start": v(7.9, 46.36) * mm, "end": v(7.48, 46.44) * mm});
            skLineSegment(sketch, "E438", {"start": v(7.48, 46.44) * mm, "end": v(7.07, 46.52) * mm});
            skLineSegment(sketch, "E439", {"start": v(7.07, 46.52) * mm, "end": v(6.65, 46.6) * mm});
            skLineSegment(sketch, "E440", {"start": v(6.65, 46.6) * mm, "end": v(6.24, 46.7) * mm});
            skLineSegment(sketch, "E441", {"start": v(6.24, 46.7) * mm, "end": v(5.83, 46.78) * mm});
            skLineSegment(sketch, "E442", {"start": v(5.83, 46.78) * mm, "end": v(5.42, 46.86) * mm});
            skLineSegment(sketch, "E443", {"start": v(5.42, 46.86) * mm, "end": v(5.03, 46.94) * mm});
            skLineSegment(sketch, "E444", {"start": v(5.03, 46.94) * mm, "end": v(5.1, 47.36) * mm});
            skLineSegment(sketch, "E445", {"start": v(5.1, 47.36) * mm, "end": v(5.16, 47.77) * mm});
            skLineSegment(sketch, "E446", {"start": v(5.16, 47.77) * mm, "end": v(5.23, 48.22) * mm});
            skLineSegment(sketch, "E447", {"start": v(5.23, 48.22) * mm, "end": v(5.3, 48.63) * mm});
            skLineSegment(sketch, "E448", {"start": v(5.3, 48.63) * mm, "end": v(5.36, 49.05) * mm});
            skLineSegment(sketch, "E449", {"start": v(5.36, 49.05) * mm, "end": v(5.43, 49.5) * mm});
            skLineSegment(sketch, "E450", {"start": v(5.43, 49.5) * mm, "end": v(5.5, 49.91) * mm});
            skLineSegment(sketch, "E451", {"start": v(5.5, 49.91) * mm, "end": v(5.56, 50.33) * mm});
            skLineSegment(sketch, "E452", {"start": v(5.56, 50.33) * mm, "end": v(5.63, 50.77) * mm});
            skLineSegment(sketch, "E453", {"start": v(5.63, 50.77) * mm, "end": v(5.69, 51.19) * mm});
            skLineSegment(sketch, "E454", {"start": v(5.69, 51.19) * mm, "end": v(5.75, 51.6) * mm});
            skLineSegment(sketch, "E455", {"start": v(5.75, 51.6) * mm, "end": v(5.82, 52.05) * mm});
            skLineSegment(sketch, "E456", {"start": v(5.82, 52.05) * mm, "end": v(5.89, 52.5) * mm});
            skLineSegment(sketch, "E457", {"start": v(5.89, 52.5) * mm, "end": v(5.87, 52.95) * mm});
            skLineSegment(sketch, "E458", {"start": v(5.87, 52.95) * mm, "end": v(5.73, 53.38) * mm});
            skLineSegment(sketch, "E459", {"start": v(5.73, 53.38) * mm, "end": v(5.48, 53.75) * mm});
            skLineSegment(sketch, "E460", {"start": v(5.48, 53.75) * mm, "end": v(5.15, 54.05) * mm});
            skLineSegment(sketch, "E461", {"start": v(5.15, 54.05) * mm, "end": v(4.75, 54.25) * mm});
            skLineSegment(sketch, "E462", {"start": v(4.75, 54.25) * mm, "end": v(4.3, 54.34) * mm});
            skLineSegment(sketch, "E463", {"start": v(4.3, 54.34) * mm, "end": v(4.22, 54.35) * mm});
            skLineSegment(sketch, "E464", {"start": v(4.22, 54.35) * mm, "end": v(3.77, 54.3) * mm});
            skLineSegment(sketch, "E465", {"start": v(3.77, 54.3) * mm, "end": v(3.36, 54.13) * mm});
            skLineSegment(sketch, "E466", {"start": v(3.36, 54.13) * mm, "end": v(3, 53.86) * mm});
            skLineSegment(sketch, "E467", {"start": v(3, 53.86) * mm, "end": v(2.72, 53.5) * mm});
            skLineSegment(sketch, "E468", {"start": v(2.72, 53.5) * mm, "end": v(2.55, 53.09) * mm});
            skLineSegment(sketch, "E469", {"start": v(2.55, 53.09) * mm, "end": v(2.49, 52.64) * mm});
            skLineSegment(sketch, "E470", {"start": v(2.49, 52.64) * mm, "end": v(2.45, 52.22) * mm});
            skLineSegment(sketch, "E471", {"start": v(2.45, 52.22) * mm, "end": v(2.41, 51.8) * mm});
            skLineSegment(sketch, "E472", {"start": v(2.41, 51.8) * mm, "end": v(2.37, 51.35) * mm});
            skLineSegment(sketch, "E473", {"start": v(2.37, 51.35) * mm, "end": v(2.33, 50.93) * mm});
            skLineSegment(sketch, "E474", {"start": v(2.33, 50.93) * mm, "end": v(2.3, 50.51) * mm});
            skLineSegment(sketch, "E475", {"start": v(2.3, 50.51) * mm, "end": v(2.26, 50.07) * mm});
            skLineSegment(sketch, "E476", {"start": v(2.26, 50.07) * mm, "end": v(2.22, 49.65) * mm});
            skLineSegment(sketch, "E477", {"start": v(2.22, 49.65) * mm, "end": v(2.18, 49.23) * mm});
            skLineSegment(sketch, "E478", {"start": v(2.18, 49.23) * mm, "end": v(2.14, 48.78) * mm});
            skLineSegment(sketch, "E479", {"start": v(2.14, 48.78) * mm, "end": v(2.1, 48.36) * mm});
            skLineSegment(sketch, "E480", {"start": v(2.1, 48.36) * mm, "end": v(2.07, 47.94) * mm});
            skLineSegment(sketch, "E481", {"start": v(2.07, 47.94) * mm, "end": v(2.03, 47.5) * mm});
            skLineSegment(sketch, "E482", {"start": v(2.03, 47.5) * mm, "end": v(2.01, 47.3) * mm});
            skLineSegment(sketch, "E483", {"start": v(2.01, 47.3) * mm, "end": v(1.6, 47.32) * mm});
            skLineSegment(sketch, "E484", {"start": v(1.6, 47.32) * mm, "end": v(1.17, 47.34) * mm});
            skLineSegment(sketch, "E485", {"start": v(1.17, 47.34) * mm, "end": v(0.75, 47.36) * mm});
            skLineSegment(sketch, "E486", {"start": v(0.75, 47.36) * mm, "end": v(0.33, 47.37) * mm});
            skLineSegment(sketch, "E487", {"start": v(0.33, 47.37) * mm, "end": v(-0.1, 47.4) * mm});
            skLineSegment(sketch, "E488", {"start": v(-0.1, 47.4) * mm, "end": v(-0.52, 47.4) * mm});
            skLineSegment(sketch, "E489", {"start": v(-0.52, 47.4) * mm, "end": v(-0.94, 47.43) * mm});
            skLineSegment(sketch, "E490", {"start": v(-0.94, 47.43) * mm, "end": v(-1.36, 47.44) * mm});
            skLineSegment(sketch, "E491", {"start": v(-1.36, 47.44) * mm, "end": v(-1.78, 47.46) * mm});
            skLineSegment(sketch, "E492", {"start": v(-1.78, 47.46) * mm, "end": v(-2.2, 47.48) * mm});
            skLineSegment(sketch, "E493", {"start": v(-2.2, 47.48) * mm, "end": v(-2.59, 47.5) * mm});
            skLineSegment(sketch, "E494", {"start": v(-2.59, 47.5) * mm, "end": v(-2.6, 47.91) * mm});
            skLineSegment(sketch, "E495", {"start": v(-2.6, 47.91) * mm, "end": v(-2.6, 48.33) * mm});
            skLineSegment(sketch, "E496", {"start": v(-2.6, 48.33) * mm, "end": v(-2.6, 48.78) * mm});
            skLineSegment(sketch, "E497", {"start": v(-2.6, 48.78) * mm, "end": v(-2.6, 49.2) * mm});
            skLineSegment(sketch, "E498", {"start": v(-2.6, 49.2) * mm, "end": v(-2.6, 49.63) * mm});
            skLineSegment(sketch, "E499", {"start": v(-2.6, 49.63) * mm, "end": v(-2.6, 50.08) * mm});
            skLineSegment(sketch, "E500", {"start": v(-2.6, 50.08) * mm, "end": v(-2.61, 50.5) * mm});
            skLineSegment(sketch, "E501", {"start": v(-2.61, 50.5) * mm, "end": v(-2.62, 50.92) * mm});
            skLineSegment(sketch, "E502", {"start": v(-2.62, 50.92) * mm, "end": v(-2.62, 51.37) * mm});
            skLineSegment(sketch, "E503", {"start": v(-2.62, 51.37) * mm, "end": v(-2.62, 51.8) * mm});
            skLineSegment(sketch, "E504", {"start": v(-2.62, 51.8) * mm, "end": v(-2.63, 52.21) * mm});
            skLineSegment(sketch, "E505", {"start": v(-2.63, 52.21) * mm, "end": v(-2.63, 52.66) * mm});
            skLineSegment(sketch, "E506", {"start": v(-2.63, 52.66) * mm, "end": v(-2.64, 53.12) * mm});
            skLineSegment(sketch, "E507", {"start": v(-2.64, 53.12) * mm, "end": v(-2.73, 53.56) * mm});
            skLineSegment(sketch, "E508", {"start": v(-2.73, 53.56) * mm, "end": v(-2.94, 53.96) * mm});
            skLineSegment(sketch, "E509", {"start": v(-2.94, 53.96) * mm, "end": v(-3.24, 54.3) * mm});
            skLineSegment(sketch, "E510", {"start": v(-3.24, 54.3) * mm, "end": v(-3.62, 54.53) * mm});
            skLineSegment(sketch, "E511", {"start": v(-3.62, 54.53) * mm, "end": v(-4.04, 54.67) * mm});
            skLineSegment(sketch, "E512", {"start": v(-4.04, 54.67) * mm, "end": v(-4.31, 54.69) * mm});
            skLineSegment(sketch, "E513", {"start": v(-4.31, 54.69) * mm, "end": v(-4.76, 54.64) * mm});
            skLineSegment(sketch, "E514", {"start": v(-4.76, 54.64) * mm, "end": v(-5.17, 54.47) * mm});
            skLineSegment(sketch, "E515", {"start": v(-5.17, 54.47) * mm, "end": v(-5.53, 54.2) * mm});
            skLineSegment(sketch, "E516", {"start": v(-5.53, 54.2) * mm, "end": v(-5.8, 53.84) * mm});
            skLineSegment(sketch, "E517", {"start": v(-5.8, 53.84) * mm, "end": v(-5.98, 53.43) * mm});
            skLineSegment(sketch, "E518", {"start": v(-5.98, 53.43) * mm, "end": v(-6.03, 52.98) * mm});
            skLineSegment(sketch, "E519", {"start": v(-6.03, 52.98) * mm, "end": v(-6, 52.53) * mm});
            skLineSegment(sketch, "E520", {"start": v(-6, 52.53) * mm, "end": v(-5.97, 52.1) * mm});
            skLineSegment(sketch, "E521", {"start": v(-5.97, 52.1) * mm, "end": v(-5.94, 51.68) * mm});
            skLineSegment(sketch, "E522", {"start": v(-5.94, 51.68) * mm, "end": v(-5.91, 51.24) * mm});
            skLineSegment(sketch, "E523", {"start": v(-5.91, 51.24) * mm, "end": v(-5.88, 50.82) * mm});
            skLineSegment(sketch, "E524", {"start": v(-5.88, 50.82) * mm, "end": v(-5.85, 50.4) * mm});
            skLineSegment(sketch, "E525", {"start": v(-5.85, 50.4) * mm, "end": v(-5.82, 49.95) * mm});
            skLineSegment(sketch, "E526", {"start": v(-5.82, 49.95) * mm, "end": v(-5.79, 49.53) * mm});
            skLineSegment(sketch, "E527", {"start": v(-5.79, 49.53) * mm, "end": v(-5.76, 49.1) * mm});
            skLineSegment(sketch, "E528", {"start": v(-5.76, 49.1) * mm, "end": v(-5.72, 48.66) * mm});
            skLineSegment(sketch, "E529", {"start": v(-5.72, 48.66) * mm, "end": v(-5.7, 48.24) * mm});
            skLineSegment(sketch, "E530", {"start": v(-5.7, 48.24) * mm, "end": v(-5.66, 47.82) * mm});
            skLineSegment(sketch, "E531", {"start": v(-5.66, 47.82) * mm, "end": v(-5.63, 47.37) * mm});
            skLineSegment(sketch, "E532", {"start": v(-5.63, 47.37) * mm, "end": v(-6.05, 47.32) * mm});
            skLineSegment(sketch, "E533", {"start": v(-6.05, 47.32) * mm, "end": v(-6.47, 47.27) * mm});
            skLineSegment(sketch, "E534", {"start": v(-6.47, 47.27) * mm, "end": v(-6.89, 47.22) * mm});
            skLineSegment(sketch, "E535", {"start": v(-6.89, 47.22) * mm, "end": v(-7.3, 47.17) * mm});
            skLineSegment(sketch, "E536", {"start": v(-7.3, 47.17) * mm, "end": v(-7.72, 47.11) * mm});
            skLineSegment(sketch, "E537", {"start": v(-7.72, 47.11) * mm, "end": v(-8.14, 47.06) * mm});
            skLineSegment(sketch, "E538", {"start": v(-8.14, 47.06) * mm, "end": v(-8.56, 47.01) * mm});
            skLineSegment(sketch, "E539", {"start": v(-8.56, 47.01) * mm, "end": v(-8.98, 46.96) * mm});
            skLineSegment(sketch, "E540", {"start": v(-8.98, 46.96) * mm, "end": v(-9.4, 46.91) * mm});
            skLineSegment(sketch, "E541", {"start": v(-9.4, 46.91) * mm, "end": v(-9.82, 46.86) * mm});
            skLineSegment(sketch, "E542", {"start": v(-9.82, 46.86) * mm, "end": v(-10.2, 46.81) * mm});
            skLineSegment(sketch, "E543", {"start": v(-10.2, 46.81) * mm, "end": v(-10.27, 47.23) * mm});
            skLineSegment(sketch, "E544", {"start": v(-10.27, 47.23) * mm, "end": v(-10.34, 47.65) * mm});
            skLineSegment(sketch, "E545", {"start": v(-10.34, 47.65) * mm, "end": v(-10.42, 48.09) * mm});
            skLineSegment(sketch, "E546", {"start": v(-10.42, 48.09) * mm, "end": v(-10.5, 48.5) * mm});
            skLineSegment(sketch, "E547", {"start": v(-10.5, 48.5) * mm, "end": v(-10.56, 48.92) * mm});
            skLineSegment(sketch, "E548", {"start": v(-10.56, 48.92) * mm, "end": v(-10.64, 49.36) * mm});
            skLineSegment(sketch, "E549", {"start": v(-10.64, 49.36) * mm, "end": v(-10.7, 49.78) * mm});
            skLineSegment(sketch, "E550", {"start": v(-10.7, 49.78) * mm, "end": v(-10.78, 50.2) * mm});
            skLineSegment(sketch, "E551", {"start": v(-10.78, 50.2) * mm, "end": v(-10.85, 50.64) * mm});
            skLineSegment(sketch, "E552", {"start": v(-10.85, 50.64) * mm, "end": v(-10.93, 51.05) * mm});
            skLineSegment(sketch, "E553", {"start": v(-10.93, 51.05) * mm, "end": v(-11, 51.47) * mm});
            skLineSegment(sketch, "E554", {"start": v(-11, 51.47) * mm, "end": v(-11.07, 51.91) * mm});
            skLineSegment(sketch, "E555", {"start": v(-11.07, 51.91) * mm, "end": v(-11.15, 52.36) * mm});
            skLineSegment(sketch, "E556", {"start": v(-11.15, 52.36) * mm, "end": v(-11.32, 52.78) * mm});
            skLineSegment(sketch, "E557", {"start": v(-11.32, 52.78) * mm, "end": v(-11.58, 53.14) * mm});
            skLineSegment(sketch, "E558", {"start": v(-11.58, 53.14) * mm, "end": v(-11.93, 53.42) * mm});
            skLineSegment(sketch, "E559", {"start": v(-11.93, 53.42) * mm, "end": v(-12.35, 53.6) * mm});
            skLineSegment(sketch, "E560", {"start": v(-12.35, 53.6) * mm, "end": v(-12.79, 53.66) * mm});
            skLineSegment(sketch, "E561", {"start": v(-12.79, 53.66) * mm, "end": v(-13.23, 53.6) * mm});
            skLineSegment(sketch, "E562", {"start": v(-13.23, 53.6) * mm, "end": v(-13.65, 53.44) * mm});
            skLineSegment(sketch, "E563", {"start": v(-13.65, 53.44) * mm, "end": v(-14, 53.17) * mm});
            skLineSegment(sketch, "E564", {"start": v(-14, 53.17) * mm, "end": v(-14.28, 52.81) * mm});
            skLineSegment(sketch, "E565", {"start": v(-14.28, 52.81) * mm, "end": v(-14.45, 52.4) * mm});
            skLineSegment(sketch, "E566", {"start": v(-14.45, 52.4) * mm, "end": v(-14.5, 51.95) * mm});
            skLineSegment(sketch, "E567", {"start": v(-14.5, 51.95) * mm, "end": v(-14.44, 51.53) * mm});
            skLineSegment(sketch, "E568", {"start": v(-14.44, 51.53) * mm, "end": v(-14.35, 51.12) * mm});
            skLineSegment(sketch, "E569", {"start": v(-14.35, 51.12) * mm, "end": v(-14.25, 50.7) * mm});
            skLineSegment(sketch, "E570", {"start": v(-14.25, 50.7) * mm, "end": v(-14.16, 50.29) * mm});
            skLineSegment(sketch, "E571", {"start": v(-14.16, 50.29) * mm, "end": v(-14.06, 49.88) * mm});
            skLineSegment(sketch, "E572", {"start": v(-14.06, 49.88) * mm, "end": v(-13.95, 49.44) * mm});
            skLineSegment(sketch, "E573", {"start": v(-13.95, 49.44) * mm, "end": v(-13.86, 49.03) * mm});
            skLineSegment(sketch, "E574", {"start": v(-13.86, 49.03) * mm, "end": v(-13.76, 48.62) * mm});
            skLineSegment(sketch, "E575", {"start": v(-13.76, 48.62) * mm, "end": v(-13.66, 48.18) * mm});
            skLineSegment(sketch, "E576", {"start": v(-13.66, 48.18) * mm, "end": v(-13.56, 47.77) * mm});
            skLineSegment(sketch, "E577", {"start": v(-13.56, 47.77) * mm, "end": v(-13.46, 47.36) * mm});
            skLineSegment(sketch, "E578", {"start": v(-13.46, 47.36) * mm, "end": v(-13.36, 46.92) * mm});
            skLineSegment(sketch, "E579", {"start": v(-13.36, 46.92) * mm, "end": v(-13.26, 46.51) * mm});
            skLineSegment(sketch, "E580", {"start": v(-13.26, 46.51) * mm, "end": v(-13.19, 46.2) * mm});
            skLineSegment(sketch, "E581", {"start": v(-13.19, 46.2) * mm, "end": v(-13.6, 46.09) * mm});
            skLineSegment(sketch, "E582", {"start": v(-13.6, 46.09) * mm, "end": v(-14, 45.97) * mm});
            skLineSegment(sketch, "E583", {"start": v(-14, 45.97) * mm, "end": v(-14.4, 45.85) * mm});
            skLineSegment(sketch, "E584", {"start": v(-14.4, 45.85) * mm, "end": v(-14.8, 45.74) * mm});
            skLineSegment(sketch, "E585", {"start": v(-14.8, 45.74) * mm, "end": v(-15.21, 45.62) * mm});
            skLineSegment(sketch, "E586", {"start": v(-15.21, 45.62) * mm, "end": v(-15.61, 45.5) * mm});
            skLineSegment(sketch, "E587", {"start": v(-15.61, 45.5) * mm, "end": v(-16.02, 45.38) * mm});
            skLineSegment(sketch, "E588", {"start": v(-16.02, 45.38) * mm, "end": v(-16.42, 45.27) * mm});
            skLineSegment(sketch, "E589", {"start": v(-16.42, 45.27) * mm, "end": v(-16.83, 45.15) * mm});
            skLineSegment(sketch, "E590", {"start": v(-16.83, 45.15) * mm, "end": v(-17.23, 45.03) * mm});
            skLineSegment(sketch, "E591", {"start": v(-17.23, 45.03) * mm, "end": v(-17.6, 44.92) * mm});
            skLineSegment(sketch, "E592", {"start": v(-17.6, 44.92) * mm, "end": v(-17.74, 45.32) * mm});
            skLineSegment(sketch, "E593", {"start": v(-17.74, 45.32) * mm, "end": v(-17.88, 45.72) * mm});
            skLineSegment(sketch, "E594", {"start": v(-17.88, 45.72) * mm, "end": v(-18.03, 46.15) * mm});
            skLineSegment(sketch, "E595", {"start": v(-18.03, 46.15) * mm, "end": v(-18.16, 46.55) * mm});
            skLineSegment(sketch, "E596", {"start": v(-18.16, 46.55) * mm, "end": v(-18.3, 46.94) * mm});
            skLineSegment(sketch, "E597", {"start": v(-18.3, 46.94) * mm, "end": v(-18.45, 47.37) * mm});
            skLineSegment(sketch, "E598", {"start": v(-18.45, 47.37) * mm, "end": v(-18.58, 47.77) * mm});
            skLineSegment(sketch, "E599", {"start": v(-18.58, 47.77) * mm, "end": v(-18.72, 48.17) * mm});
            skLineSegment(sketch, "E600", {"start": v(-18.72, 48.17) * mm, "end": v(-18.87, 48.6) * mm});
            skLineSegment(sketch, "E601", {"start": v(-18.87, 48.6) * mm, "end": v(-19, 49) * mm});
            skLineSegment(sketch, "E602", {"start": v(-19, 49) * mm, "end": v(-19.14, 49.39) * mm});
            skLineSegment(sketch, "E603", {"start": v(-19.14, 49.39) * mm, "end": v(-19.28, 49.81) * mm});
            skLineSegment(sketch, "E604", {"start": v(-19.28, 49.81) * mm, "end": v(-19.44, 50.25) * mm});
            skLineSegment(sketch, "E605", {"start": v(-19.44, 50.25) * mm, "end": v(-19.66, 50.63) * mm});
            skLineSegment(sketch, "E606", {"start": v(-19.66, 50.63) * mm, "end": v(-19.99, 50.95) * mm});
            skLineSegment(sketch, "E607", {"start": v(-19.99, 50.95) * mm, "end": v(-20.38, 51.17) * mm});
            skLineSegment(sketch, "E608", {"start": v(-20.38, 51.17) * mm, "end": v(-20.81, 51.28) * mm});
            skLineSegment(sketch, "E609", {"start": v(-20.81, 51.28) * mm, "end": v(-21, 51.29) * mm});
            skLineSegment(sketch, "E610", {"start": v(-21, 51.29) * mm, "end": v(-21.44, 51.23) * mm});
            skLineSegment(sketch, "E611", {"start": v(-21.44, 51.23) * mm, "end": v(-21.85, 51.06) * mm});
            skLineSegment(sketch, "E612", {"start": v(-21.85, 51.06) * mm, "end": v(-22.2, 50.79) * mm});
            skLineSegment(sketch, "E613", {"start": v(-22.2, 50.79) * mm, "end": v(-22.48, 50.43) * mm});
            skLineSegment(sketch, "E614", {"start": v(-22.48, 50.43) * mm, "end": v(-22.65, 50.02) * mm});
            skLineSegment(sketch, "E615", {"start": v(-22.65, 50.02) * mm, "end": v(-22.7, 49.57) * mm});
            skLineSegment(sketch, "E616", {"start": v(-22.7, 49.57) * mm, "end": v(-22.64, 49.13) * mm});
            skLineSegment(sketch, "E617", {"start": v(-22.64, 49.13) * mm, "end": v(-22.49, 48.74) * mm});
            skLineSegment(sketch, "E618", {"start": v(-22.49, 48.74) * mm, "end": v(-22.33, 48.35) * mm});
            skLineSegment(sketch, "E619", {"start": v(-22.33, 48.35) * mm, "end": v(-22.16, 47.94) * mm});
            skLineSegment(sketch, "E620", {"start": v(-22.16, 47.94) * mm, "end": v(-22, 47.55) * mm});
            skLineSegment(sketch, "E621", {"start": v(-22, 47.55) * mm, "end": v(-21.83, 47.16) * mm});
            skLineSegment(sketch, "E622", {"start": v(-21.83, 47.16) * mm, "end": v(-21.66, 46.74) * mm});
            skLineSegment(sketch, "E623", {"start": v(-21.66, 46.74) * mm, "end": v(-21.5, 46.35) * mm});
            skLineSegment(sketch, "E624", {"start": v(-21.5, 46.35) * mm, "end": v(-21.34, 45.96) * mm});
            skLineSegment(sketch, "E625", {"start": v(-21.34, 45.96) * mm, "end": v(-21.16, 45.55) * mm});
            skLineSegment(sketch, "E626", {"start": v(-21.16, 45.55) * mm, "end": v(-21, 45.16) * mm});
            skLineSegment(sketch, "E627", {"start": v(-21, 45.16) * mm, "end": v(-20.84, 44.77) * mm});
            skLineSegment(sketch, "E628", {"start": v(-20.84, 44.77) * mm, "end": v(-20.67, 44.36) * mm});
            skLineSegment(sketch, "E629", {"start": v(-20.67, 44.36) * mm, "end": v(-20.5, 43.97) * mm});
            skLineSegment(sketch, "E630", {"start": v(-20.5, 43.97) * mm, "end": v(-20.45, 43.84) * mm});
            skLineSegment(sketch, "E631", {"start": v(-20.45, 43.84) * mm, "end": v(-20.84, 43.66) * mm});
            skLineSegment(sketch, "E632", {"start": v(-20.84, 43.66) * mm, "end": v(-21.22, 43.48) * mm});
            skLineSegment(sketch, "E633", {"start": v(-21.22, 43.48) * mm, "end": v(-21.6, 43.3) * mm});
            skLineSegment(sketch, "E634", {"start": v(-21.6, 43.3) * mm, "end": v(-21.98, 43.12) * mm});
            skLineSegment(sketch, "E635", {"start": v(-21.98, 43.12) * mm, "end": v(-22.36, 42.94) * mm});
            skLineSegment(sketch, "E636", {"start": v(-22.36, 42.94) * mm, "end": v(-22.74, 42.76) * mm});
            skLineSegment(sketch, "E637", {"start": v(-22.74, 42.76) * mm, "end": v(-23.12, 42.58) * mm});
            skLineSegment(sketch, "E638", {"start": v(-23.12, 42.58) * mm, "end": v(-23.5, 42.4) * mm});
            skLineSegment(sketch, "E639", {"start": v(-23.5, 42.4) * mm, "end": v(-23.88, 42.22) * mm});
            skLineSegment(sketch, "E640", {"start": v(-23.88, 42.22) * mm, "end": v(-24.26, 42.04) * mm});
            skLineSegment(sketch, "E641", {"start": v(-24.26, 42.04) * mm, "end": v(-24.61, 41.87) * mm});
            skLineSegment(sketch, "E642", {"start": v(-24.61, 41.87) * mm, "end": v(-24.81, 42.24) * mm});
            skLineSegment(sketch, "E643", {"start": v(-24.81, 42.24) * mm, "end": v(-25.01, 42.61) * mm});
            skLineSegment(sketch, "E644", {"start": v(-25.01, 42.61) * mm, "end": v(-25.22, 43.01) * mm});
            skLineSegment(sketch, "E645", {"start": v(-25.22, 43.01) * mm, "end": v(-25.42, 43.38) * mm});
            skLineSegment(sketch, "E646", {"start": v(-25.42, 43.38) * mm, "end": v(-25.62, 43.75) * mm});
            skLineSegment(sketch, "E647", {"start": v(-25.62, 43.75) * mm, "end": v(-25.83, 44.15) * mm});
            skLineSegment(sketch, "E648", {"start": v(-25.83, 44.15) * mm, "end": v(-26.03, 44.52) * mm});
            skLineSegment(sketch, "E649", {"start": v(-26.03, 44.52) * mm, "end": v(-26.23, 44.9) * mm});
            skLineSegment(sketch, "E650", {"start": v(-26.23, 44.9) * mm, "end": v(-26.44, 45.29) * mm});
            skLineSegment(sketch, "E651", {"start": v(-26.44, 45.29) * mm, "end": v(-26.64, 45.66) * mm});
            skLineSegment(sketch, "E652", {"start": v(-26.64, 45.66) * mm, "end": v(-26.84, 46.03) * mm});
            skLineSegment(sketch, "E653", {"start": v(-26.84, 46.03) * mm, "end": v(-27.05, 46.43) * mm});
            skLineSegment(sketch, "E654", {"start": v(-27.05, 46.43) * mm, "end": v(-27.27, 46.83) * mm});
            skLineSegment(sketch, "E655", {"start": v(-27.27, 46.83) * mm, "end": v(-27.56, 47.18) * mm});
            skLineSegment(sketch, "E656", {"start": v(-27.56, 47.18) * mm, "end": v(-27.93, 47.44) * mm});
            skLineSegment(sketch, "E657", {"start": v(-27.93, 47.44) * mm, "end": v(-28.35, 47.59) * mm});
            skLineSegment(sketch, "E658", {"start": v(-28.35, 47.59) * mm, "end": v(-28.7, 47.63) * mm});
            skLineSegment(sketch, "E659", {"start": v(-28.7, 47.63) * mm, "end": v(-29.15, 47.57) * mm});
            skLineSegment(sketch, "E660", {"start": v(-29.15, 47.57) * mm, "end": v(-29.56, 47.4) * mm});
            skLineSegment(sketch, "E661", {"start": v(-29.56, 47.4) * mm, "end": v(-29.92, 47.13) * mm});
            skLineSegment(sketch, "E662", {"start": v(-29.92, 47.13) * mm, "end": v(-30.2, 46.77) * mm});
            skLineSegment(sketch, "E663", {"start": v(-30.2, 46.77) * mm, "end": v(-30.36, 46.35) * mm});
            skLineSegment(sketch, "E664", {"start": v(-30.36, 46.35) * mm, "end": v(-30.42, 45.9) * mm});
            skLineSegment(sketch, "E665", {"start": v(-30.42, 45.9) * mm, "end": v(-30.35, 45.47) * mm});
            skLineSegment(sketch, "E666", {"start": v(-30.35, 45.47) * mm, "end": v(-30.17, 45.05) * mm});
            skLineSegment(sketch, "E667", {"start": v(-30.17, 45.05) * mm, "end": v(-29.95, 44.7) * mm});
            skLineSegment(sketch, "E668", {"start": v(-29.95, 44.7) * mm, "end": v(-29.73, 44.34) * mm});
            skLineSegment(sketch, "E669", {"start": v(-29.73, 44.34) * mm, "end": v(-29.5, 43.96) * mm});
            skLineSegment(sketch, "E670", {"start": v(-29.5, 43.96) * mm, "end": v(-29.27, 43.6) * mm});
            skLineSegment(sketch, "E671", {"start": v(-29.27, 43.6) * mm, "end": v(-29.05, 43.24) * mm});
            skLineSegment(sketch, "E672", {"start": v(-29.05, 43.24) * mm, "end": v(-28.81, 42.86) * mm});
            skLineSegment(sketch, "E673", {"start": v(-28.81, 42.86) * mm, "end": v(-28.59, 42.5) * mm});
            skLineSegment(sketch, "E674", {"start": v(-28.59, 42.5) * mm, "end": v(-28.37, 42.14) * mm});
            skLineSegment(sketch, "E675", {"start": v(-28.37, 42.14) * mm, "end": v(-28.13, 41.76) * mm});
            skLineSegment(sketch, "E676", {"start": v(-28.13, 41.76) * mm, "end": v(-27.9, 41.4) * mm});
            skLineSegment(sketch, "E677", {"start": v(-27.9, 41.4) * mm, "end": v(-27.68, 41.04) * mm});
            skLineSegment(sketch, "E678", {"start": v(-27.68, 41.04) * mm, "end": v(-27.45, 40.66) * mm});
            skLineSegment(sketch, "E679", {"start": v(-27.45, 40.66) * mm, "end": v(-27.25, 40.35) * mm});
            skLineSegment(sketch, "E680", {"start": v(-27.25, 40.35) * mm, "end": v(-27.6, 40.1) * mm});
            skLineSegment(sketch, "E681", {"start": v(-27.6, 40.1) * mm, "end": v(-27.95, 39.87) * mm});
            skLineSegment(sketch, "E682", {"start": v(-27.95, 39.87) * mm, "end": v(-28.3, 39.63) * mm});
            skLineSegment(sketch, "E683", {"start": v(-28.3, 39.63) * mm, "end": v(-28.64, 39.39) * mm});
            skLineSegment(sketch, "E684", {"start": v(-28.64, 39.39) * mm, "end": v(-28.99, 39.15) * mm});
            skLineSegment(sketch, "E685", {"start": v(-28.99, 39.15) * mm, "end": v(-29.33, 38.91) * mm});
            skLineSegment(sketch, "E686", {"start": v(-29.33, 38.91) * mm, "end": v(-29.68, 38.67) * mm});
            skLineSegment(sketch, "E687", {"start": v(-29.68, 38.67) * mm, "end": v(-30.03, 38.43) * mm});
            skLineSegment(sketch, "E688", {"start": v(-30.03, 38.43) * mm, "end": v(-30.37, 38.2) * mm});
            skLineSegment(sketch, "E689", {"start": v(-30.37, 38.2) * mm, "end": v(-30.72, 37.95) * mm});
            skLineSegment(sketch, "E690", {"start": v(-30.72, 37.95) * mm, "end": v(-31.04, 37.73) * mm});
            skLineSegment(sketch, "E691", {"start": v(-31.04, 37.73) * mm, "end": v(-31.3, 38.07) * mm});
            skLineSegment(sketch, "E692", {"start": v(-31.3, 38.07) * mm, "end": v(-31.55, 38.4) * mm});
            skLineSegment(sketch, "E693", {"start": v(-31.55, 38.4) * mm, "end": v(-31.83, 38.76) * mm});
            skLineSegment(sketch, "E694", {"start": v(-31.83, 38.76) * mm, "end": v(-32.08, 39.1) * mm});
            skLineSegment(sketch, "E695", {"start": v(-32.08, 39.1) * mm, "end": v(-32.34, 39.43) * mm});
            skLineSegment(sketch, "E696", {"start": v(-32.34, 39.43) * mm, "end": v(-32.61, 39.79) * mm});
            skLineSegment(sketch, "E697", {"start": v(-32.61, 39.79) * mm, "end": v(-32.87, 40.12) * mm});
            skLineSegment(sketch, "E698", {"start": v(-32.87, 40.12) * mm, "end": v(-33.12, 40.46) * mm});
            skLineSegment(sketch, "E699", {"start": v(-33.12, 40.46) * mm, "end": v(-33.4, 40.81) * mm});
            skLineSegment(sketch, "E700", {"start": v(-33.4, 40.81) * mm, "end": v(-33.65, 41.15) * mm});
            skLineSegment(sketch, "E701", {"start": v(-33.65, 41.15) * mm, "end": v(-33.9, 41.48) * mm});
            skLineSegment(sketch, "E702", {"start": v(-33.9, 41.48) * mm, "end": v(-34.18, 41.84) * mm});
            skLineSegment(sketch, "E703", {"start": v(-34.18, 41.84) * mm, "end": v(-34.46, 42.2) * mm});
            skLineSegment(sketch, "E704", {"start": v(-34.46, 42.2) * mm, "end": v(-34.8, 42.5) * mm});
            skLineSegment(sketch, "E705", {"start": v(-34.8, 42.5) * mm, "end": v(-35.2, 42.7) * mm});
            skLineSegment(sketch, "E706", {"start": v(-35.2, 42.7) * mm, "end": v(-35.64, 42.78) * mm});
            skLineSegment(sketch, "E707", {"start": v(-35.64, 42.78) * mm, "end": v(-35.73, 42.78) * mm});
            skLineSegment(sketch, "E708", {"start": v(-35.73, 42.78) * mm, "end": v(-36.18, 42.72) * mm});
            skLineSegment(sketch, "E709", {"start": v(-36.18, 42.72) * mm, "end": v(-36.6, 42.55) * mm});
            skLineSegment(sketch, "E710", {"start": v(-36.6, 42.55) * mm, "end": v(-36.95, 42.28) * mm});
            skLineSegment(sketch, "E711", {"start": v(-36.95, 42.28) * mm, "end": v(-37.22, 41.92) * mm});
            skLineSegment(sketch, "E712", {"start": v(-37.22, 41.92) * mm, "end": v(-37.39, 41.5) * mm});
            skLineSegment(sketch, "E713", {"start": v(-37.39, 41.5) * mm, "end": v(-37.44, 41.06) * mm});
            skLineSegment(sketch, "E714", {"start": v(-37.44, 41.06) * mm, "end": v(-37.37, 40.61) * mm});
            skLineSegment(sketch, "E715", {"start": v(-37.37, 40.61) * mm, "end": v(-37.2, 40.2) * mm});
            skLineSegment(sketch, "E716", {"start": v(-37.2, 40.2) * mm, "end": v(-36.92, 39.84) * mm});
            skLineSegment(sketch, "E717", {"start": v(-36.92, 39.84) * mm, "end": v(-36.64, 39.53) * mm});
            skLineSegment(sketch, "E718", {"start": v(-36.64, 39.53) * mm, "end": v(-36.36, 39.2) * mm});
            skLineSegment(sketch, "E719", {"start": v(-36.36, 39.2) * mm, "end": v(-36.07, 38.87) * mm});
            skLineSegment(sketch, "E720", {"start": v(-36.07, 38.87) * mm, "end": v(-35.8, 38.55) * mm});
            skLineSegment(sketch, "E721", {"start": v(-35.8, 38.55) * mm, "end": v(-35.51, 38.23) * mm});
            skLineSegment(sketch, "E722", {"start": v(-35.51, 38.23) * mm, "end": v(-35.22, 37.9) * mm});
            skLineSegment(sketch, "E723", {"start": v(-35.22, 37.9) * mm, "end": v(-34.94, 37.58) * mm});
            skLineSegment(sketch, "E724", {"start": v(-34.94, 37.58) * mm, "end": v(-34.67, 37.26) * mm});
            skLineSegment(sketch, "E725", {"start": v(-34.67, 37.26) * mm, "end": v(-34.37, 36.92) * mm});
            skLineSegment(sketch, "E726", {"start": v(-34.37, 36.92) * mm, "end": v(-34.1, 36.6) * mm});
            skLineSegment(sketch, "E727", {"start": v(-34.1, 36.6) * mm, "end": v(-33.82, 36.28) * mm});
            skLineSegment(sketch, "E728", {"start": v(-33.82, 36.28) * mm, "end": v(-33.52, 35.95) * mm});
            skLineSegment(sketch, "E729", {"start": v(-33.52, 35.95) * mm, "end": v(-33.4, 35.8) * mm});
            skLineSegment(sketch, "E730", {"start": v(-33.4, 35.8) * mm, "end": v(-33.7, 35.51) * mm});
            skLineSegment(sketch, "E731", {"start": v(-33.7, 35.51) * mm, "end": v(-34, 35.22) * mm});
            skLineSegment(sketch, "E732", {"start": v(-34, 35.22) * mm, "end": v(-34.31, 34.93) * mm});
            skLineSegment(sketch, "E733", {"start": v(-34.31, 34.93) * mm, "end": v(-34.62, 34.64) * mm});
            skLineSegment(sketch, "E734", {"start": v(-34.62, 34.64) * mm, "end": v(-34.92, 34.35) * mm});
            skLineSegment(sketch, "E735", {"start": v(-34.92, 34.35) * mm, "end": v(-35.22, 34.05) * mm});
            skLineSegment(sketch, "E736", {"start": v(-35.22, 34.05) * mm, "end": v(-35.53, 33.76) * mm});
            skLineSegment(sketch, "E737", {"start": v(-35.53, 33.76) * mm, "end": v(-35.83, 33.47) * mm});
            skLineSegment(sketch, "E738", {"start": v(-35.83, 33.47) * mm, "end": v(-36.14, 33.18) * mm});
            skLineSegment(sketch, "E739", {"start": v(-36.14, 33.18) * mm, "end": v(-36.44, 32.89) * mm});
            skLineSegment(sketch, "E740", {"start": v(-36.44, 32.89) * mm, "end": v(-36.72, 32.62) * mm});
            skLineSegment(sketch, "E741", {"start": v(-36.72, 32.62) * mm, "end": v(-37.03, 32.9) * mm});
            skLineSegment(sketch, "E742", {"start": v(-37.03, 32.9) * mm, "end": v(-37.33, 33.2) * mm});
            skLineSegment(sketch, "E743", {"start": v(-37.33, 33.2) * mm, "end": v(-37.66, 33.5) * mm});
            skLineSegment(sketch, "E744", {"start": v(-37.66, 33.5) * mm, "end": v(-37.97, 33.8) * mm});
            skLineSegment(sketch, "E745", {"start": v(-37.97, 33.8) * mm, "end": v(-38.27, 34.08) * mm});
            skLineSegment(sketch, "E746", {"start": v(-38.27, 34.08) * mm, "end": v(-38.6, 34.4) * mm});
            skLineSegment(sketch, "E747", {"start": v(-38.6, 34.4) * mm, "end": v(-38.9, 34.68) * mm});
            skLineSegment(sketch, "E748", {"start": v(-38.9, 34.68) * mm, "end": v(-39.21, 34.97) * mm});
            skLineSegment(sketch, "E749", {"start": v(-39.21, 34.97) * mm, "end": v(-39.54, 35.28) * mm});
            skLineSegment(sketch, "E750", {"start": v(-39.54, 35.28) * mm, "end": v(-39.84, 35.57) * mm});
            skLineSegment(sketch, "E751", {"start": v(-39.84, 35.57) * mm, "end": v(-40.15, 35.86) * mm});
            skLineSegment(sketch, "E752", {"start": v(-40.15, 35.86) * mm, "end": v(-40.48, 36.17) * mm});
            skLineSegment(sketch, "E753", {"start": v(-40.48, 36.17) * mm, "end": v(-40.81, 36.48) * mm});
            skLineSegment(sketch, "E754", {"start": v(-40.81, 36.48) * mm, "end": v(-41.2, 36.72) * mm});
            skLineSegment(sketch, "E755", {"start": v(-41.2, 36.72) * mm, "end": v(-41.62, 36.85) * mm});
            skLineSegment(sketch, "E756", {"start": v(-41.62, 36.85) * mm, "end": v(-41.9, 36.87) * mm});
            skLineSegment(sketch, "E757", {"start": v(-41.9, 36.87) * mm, "end": v(-42.34, 36.8) * mm});
            skLineSegment(sketch, "E758", {"start": v(-42.34, 36.8) * mm, "end": v(-42.75, 36.64) * mm});
            skLineSegment(sketch, "E759", {"start": v(-42.75, 36.64) * mm, "end": v(-43.1, 36.36) * mm});
            skLineSegment(sketch, "E760", {"start": v(-43.1, 36.36) * mm, "end": v(-43.38, 36) * mm});
            skLineSegment(sketch, "E761", {"start": v(-43.38, 36) * mm, "end": v(-43.54, 35.59) * mm});
            skLineSegment(sketch, "E762", {"start": v(-43.54, 35.59) * mm, "end": v(-43.6, 35.14) * mm});
            skLineSegment(sketch, "E763", {"start": v(-43.6, 35.14) * mm, "end": v(-43.53, 34.7) * mm});
            skLineSegment(sketch, "E764", {"start": v(-43.53, 34.7) * mm, "end": v(-43.35, 34.29) * mm});
            skLineSegment(sketch, "E765", {"start": v(-43.35, 34.29) * mm, "end": v(-43.07, 33.94) * mm});
            skLineSegment(sketch, "E766", {"start": v(-43.07, 33.94) * mm, "end": v(-42.72, 33.64) * mm});
            skLineSegment(sketch, "E767", {"start": v(-42.72, 33.64) * mm, "end": v(-42.4, 33.37) * mm});
            skLineSegment(sketch, "E768", {"start": v(-42.4, 33.37) * mm, "end": v(-42.07, 33.1) * mm});
            skLineSegment(sketch, "E769", {"start": v(-42.07, 33.1) * mm, "end": v(-41.72, 32.81) * mm});
            skLineSegment(sketch, "E770", {"start": v(-41.72, 32.81) * mm, "end": v(-41.4, 32.55) * mm});
            skLineSegment(sketch, "E771", {"start": v(-41.4, 32.55) * mm, "end": v(-41.07, 32.28) * mm});
            skLineSegment(sketch, "E772", {"start": v(-41.07, 32.28) * mm, "end": v(-40.73, 31.99) * mm});
            skLineSegment(sketch, "E773", {"start": v(-40.73, 31.99) * mm, "end": v(-40.4, 31.72) * mm});
            skLineSegment(sketch, "E774", {"start": v(-40.4, 31.72) * mm, "end": v(-40.08, 31.45) * mm});
            skLineSegment(sketch, "E775", {"start": v(-40.08, 31.45) * mm, "end": v(-39.73, 31.16) * mm});
            skLineSegment(sketch, "E776", {"start": v(-39.73, 31.16) * mm, "end": v(-39.4, 30.9) * mm});
            skLineSegment(sketch, "E777", {"start": v(-39.4, 30.9) * mm, "end": v(-39.08, 30.62) * mm});
            skLineSegment(sketch, "E778", {"start": v(-39.08, 30.62) * mm, "end": v(-38.74, 30.34) * mm});
            skLineSegment(sketch, "E779", {"start": v(-38.74, 30.34) * mm, "end": v(-39, 30) * mm});
            skLineSegment(sketch, "E780", {"start": v(-39, 30) * mm, "end": v(-39.25, 29.66) * mm});
            skLineSegment(sketch, "E781", {"start": v(-39.25, 29.66) * mm, "end": v(-39.5, 29.33) * mm});
            skLineSegment(sketch, "E782", {"start": v(-39.5, 29.33) * mm, "end": v(-39.75, 28.99) * mm});
            skLineSegment(sketch, "E783", {"start": v(-39.75, 28.99) * mm, "end": v(-40, 28.65) * mm});
            skLineSegment(sketch, "E784", {"start": v(-40, 28.65) * mm, "end": v(-40.26, 28.32) * mm});
            skLineSegment(sketch, "E785", {"start": v(-40.26, 28.32) * mm, "end": v(-40.51, 27.98) * mm});
            skLineSegment(sketch, "E786", {"start": v(-40.51, 27.98) * mm, "end": v(-40.77, 27.64) * mm});
            skLineSegment(sketch, "E787", {"start": v(-40.77, 27.64) * mm, "end": v(-41.02, 27.3) * mm});
            skLineSegment(sketch, "E788", {"start": v(-41.02, 27.3) * mm, "end": v(-41.27, 26.97) * mm});
            skLineSegment(sketch, "E789", {"start": v(-41.27, 26.97) * mm, "end": v(-41.5, 26.66) * mm});
            skLineSegment(sketch, "E790", {"start": v(-41.5, 26.66) * mm, "end": v(-41.85, 26.9) * mm});
            skLineSegment(sketch, "E791", {"start": v(-41.85, 26.9) * mm, "end": v(-42.2, 27.13) * mm});
            skLineSegment(sketch, "E792", {"start": v(-42.2, 27.13) * mm, "end": v(-42.57, 27.38) * mm});
            skLineSegment(sketch, "E793", {"start": v(-42.57, 27.38) * mm, "end": v(-42.92, 27.62) * mm});
            skLineSegment(sketch, "E794", {"start": v(-42.92, 27.62) * mm, "end": v(-43.27, 27.86) * mm});
            skLineSegment(sketch, "E795", {"start": v(-43.27, 27.86) * mm, "end": v(-43.64, 28.1) * mm});
            skLineSegment(sketch, "E796", {"start": v(-43.64, 28.1) * mm, "end": v(-44, 28.35) * mm});
            skLineSegment(sketch, "E797", {"start": v(-44, 28.35) * mm, "end": v(-44.34, 28.58) * mm});
            skLineSegment(sketch, "E798", {"start": v(-44.34, 28.58) * mm, "end": v(-44.71, 28.83) * mm});
            skLineSegment(sketch, "E799", {"start": v(-44.71, 28.83) * mm, "end": v(-45.06, 29.07) * mm});
            skLineSegment(sketch, "E800", {"start": v(-45.06, 29.07) * mm, "end": v(-45.41, 29.3) * mm});
            skLineSegment(sketch, "E801", {"start": v(-45.41, 29.3) * mm, "end": v(-45.78, 29.56) * mm});
            skLineSegment(sketch, "E802", {"start": v(-45.78, 29.56) * mm, "end": v(-46.17, 29.81) * mm});
            skLineSegment(sketch, "E803", {"start": v(-46.17, 29.81) * mm, "end": v(-46.58, 29.99) * mm});
            skLineSegment(sketch, "E804", {"start": v(-46.58, 29.99) * mm, "end": v(-47.02, 30.04) * mm});
            skLineSegment(sketch, "E805", {"start": v(-47.02, 30.04) * mm, "end": v(-47.47, 29.98) * mm});
            skLineSegment(sketch, "E806", {"start": v(-47.47, 29.98) * mm, "end": v(-47.88, 29.81) * mm});
            skLineSegment(sketch, "E807", {"start": v(-47.88, 29.81) * mm, "end": v(-48.24, 29.53) * mm});
            skLineSegment(sketch, "E808", {"start": v(-48.24, 29.53) * mm, "end": v(-48.5, 29.18) * mm});
            skLineSegment(sketch, "E809", {"start": v(-48.5, 29.18) * mm, "end": v(-48.67, 28.76) * mm});
            skLineSegment(sketch, "E810", {"start": v(-48.67, 28.76) * mm, "end": v(-48.72, 28.31) * mm});
            skLineSegment(sketch, "E811", {"start": v(-48.72, 28.31) * mm, "end": v(-48.65, 27.87) * mm});
            skLineSegment(sketch, "E812", {"start": v(-48.65, 27.87) * mm, "end": v(-48.47, 27.46) * mm});
            skLineSegment(sketch, "E813", {"start": v(-48.47, 27.46) * mm, "end": v(-48.2, 27.11) * mm});
            skLineSegment(sketch, "E814", {"start": v(-48.2, 27.11) * mm, "end": v(-47.85, 26.87) * mm});
            skLineSegment(sketch, "E815", {"start": v(-47.85, 26.87) * mm, "end": v(-47.49, 26.65) * mm});
            skLineSegment(sketch, "E816", {"start": v(-47.49, 26.65) * mm, "end": v(-47.11, 26.42) * mm});
            skLineSegment(sketch, "E817", {"start": v(-47.11, 26.42) * mm, "end": v(-46.75, 26.21) * mm});
            skLineSegment(sketch, "E818", {"start": v(-46.75, 26.21) * mm, "end": v(-46.38, 26) * mm});
            skLineSegment(sketch, "E819", {"start": v(-46.38, 26) * mm, "end": v(-46, 25.77) * mm});
            skLineSegment(sketch, "E820", {"start": v(-46, 25.77) * mm, "end": v(-45.63, 25.56) * mm});
            skLineSegment(sketch, "E821", {"start": v(-45.63, 25.56) * mm, "end": v(-45.27, 25.34) * mm});
            skLineSegment(sketch, "E822", {"start": v(-45.27, 25.34) * mm, "end": v(-44.88, 25.11) * mm});
            skLineSegment(sketch, "E823", {"start": v(-44.88, 25.11) * mm, "end": v(-44.52, 24.9) * mm});
            skLineSegment(sketch, "E824", {"start": v(-44.52, 24.9) * mm, "end": v(-44.16, 24.69) * mm});
            skLineSegment(sketch, "E825", {"start": v(-44.16, 24.69) * mm, "end": v(-43.77, 24.46) * mm});
            skLineSegment(sketch, "E826", {"start": v(-43.77, 24.46) * mm, "end": v(-43.4, 24.24) * mm});
            skLineSegment(sketch, "E827", {"start": v(-43.4, 24.24) * mm, "end": v(-43.13, 24.08) * mm});
            skLineSegment(sketch, "E828", {"start": v(-43.13, 24.08) * mm, "end": v(-43.33, 23.71) * mm});
            skLineSegment(sketch, "E829", {"start": v(-43.33, 23.71) * mm, "end": v(-43.52, 23.34) * mm});
            skLineSegment(sketch, "E830", {"start": v(-43.52, 23.34) * mm, "end": v(-43.72, 22.96) * mm});
            skLineSegment(sketch, "E831", {"start": v(-43.72, 22.96) * mm, "end": v(-43.92, 22.6) * mm});
            skLineSegment(sketch, "E832", {"start": v(-43.92, 22.6) * mm, "end": v(-44.11, 22.22) * mm});
            skLineSegment(sketch, "E833", {"start": v(-44.11, 22.22) * mm, "end": v(-44.3, 21.84) * mm});
            skLineSegment(sketch, "E834", {"start": v(-44.3, 21.84) * mm, "end": v(-44.5, 21.47) * mm});
            skLineSegment(sketch, "E835", {"start": v(-44.5, 21.47) * mm, "end": v(-44.7, 21.1) * mm});
            skLineSegment(sketch, "E836", {"start": v(-44.7, 21.1) * mm, "end": v(-44.9, 20.72) * mm});
            skLineSegment(sketch, "E837", {"start": v(-44.9, 20.72) * mm, "end": v(-45.1, 20.35) * mm});
            skLineSegment(sketch, "E838", {"start": v(-45.1, 20.35) * mm, "end": v(-45.27, 20) * mm});
            skLineSegment(sketch, "E839", {"start": v(-45.27, 20) * mm, "end": v(-45.65, 20.18) * mm});
            skLineSegment(sketch, "E840", {"start": v(-45.65, 20.18) * mm, "end": v(-46.04, 20.36) * mm});
            skLineSegment(sketch, "E841", {"start": v(-46.04, 20.36) * mm, "end": v(-46.44, 20.55) * mm});
            skLineSegment(sketch, "E842", {"start": v(-46.44, 20.55) * mm, "end": v(-46.83, 20.73) * mm});
            skLineSegment(sketch, "E843", {"start": v(-46.83, 20.73) * mm, "end": v(-47.2, 20.9) * mm});
            skLineSegment(sketch, "E844", {"start": v(-47.2, 20.9) * mm, "end": v(-47.62, 21.1) * mm});
            skLineSegment(sketch, "E845", {"start": v(-47.62, 21.1) * mm, "end": v(-48, 21.27) * mm});
            skLineSegment(sketch, "E846", {"start": v(-48, 21.27) * mm, "end": v(-48.38, 21.45) * mm});
            skLineSegment(sketch, "E847", {"start": v(-48.38, 21.45) * mm, "end": v(-48.79, 21.64) * mm});
            skLineSegment(sketch, "E848", {"start": v(-48.79, 21.64) * mm, "end": v(-49.17, 21.82) * mm});
            skLineSegment(sketch, "E849", {"start": v(-49.17, 21.82) * mm, "end": v(-49.55, 22) * mm});
            skLineSegment(sketch, "E850", {"start": v(-49.55, 22) * mm, "end": v(-49.96, 22.19) * mm});
            skLineSegment(sketch, "E851", {"start": v(-49.96, 22.19) * mm, "end": v(-50.38, 22.38) * mm});
            skLineSegment(sketch, "E852", {"start": v(-50.38, 22.38) * mm, "end": v(-50.82, 22.48) * mm});
            skLineSegment(sketch, "E853", {"start": v(-50.82, 22.48) * mm, "end": v(-51, 22.49) * mm});
            skLineSegment(sketch, "E854", {"start": v(-51, 22.49) * mm, "end": v(-51.44, 22.43) * mm});
            skLineSegment(sketch, "E855", {"start": v(-51.44, 22.43) * mm, "end": v(-51.85, 22.25) * mm});
            skLineSegment(sketch, "E856", {"start": v(-51.85, 22.25) * mm, "end": v(-52.2, 21.97) * mm});
            skLineSegment(sketch, "E857", {"start": v(-52.2, 21.97) * mm, "end": v(-52.47, 21.61) * mm});
            skLineSegment(sketch, "E858", {"start": v(-52.47, 21.61) * mm, "end": v(-52.64, 21.2) * mm});
            skLineSegment(sketch, "E859", {"start": v(-52.64, 21.2) * mm, "end": v(-52.69, 20.75) * mm});
            skLineSegment(sketch, "E860", {"start": v(-52.69, 20.75) * mm, "end": v(-52.62, 20.3) * mm});
            skLineSegment(sketch, "E861", {"start": v(-52.62, 20.3) * mm, "end": v(-52.44, 19.9) * mm});
            skLineSegment(sketch, "E862", {"start": v(-52.44, 19.9) * mm, "end": v(-52.16, 19.55) * mm});
            skLineSegment(sketch, "E863", {"start": v(-52.16, 19.55) * mm, "end": v(-51.8, 19.29) * mm});
            skLineSegment(sketch, "E864", {"start": v(-51.8, 19.29) * mm, "end": v(-51.4, 19.13) * mm});
            skLineSegment(sketch, "E865", {"start": v(-51.4, 19.13) * mm, "end": v(-51.01, 18.97) * mm});
            skLineSegment(sketch, "E866", {"start": v(-51.01, 18.97) * mm, "end": v(-50.6, 18.81) * mm});
            skLineSegment(sketch, "E867", {"start": v(-50.6, 18.81) * mm, "end": v(-50.2, 18.66) * mm});
            skLineSegment(sketch, "E868", {"start": v(-50.2, 18.66) * mm, "end": v(-49.81, 18.5) * mm});
            skLineSegment(sketch, "E869", {"start": v(-49.81, 18.5) * mm, "end": v(-49.4, 18.34) * mm});
            skLineSegment(sketch, "E870", {"start": v(-49.4, 18.34) * mm, "end": v(-49, 18.19) * mm});
            skLineSegment(sketch, "E871", {"start": v(-49, 18.19) * mm, "end": v(-48.6, 18.04) * mm});
            skLineSegment(sketch, "E872", {"start": v(-48.6, 18.04) * mm, "end": v(-48.19, 17.87) * mm});
            skLineSegment(sketch, "E873", {"start": v(-48.19, 17.87) * mm, "end": v(-47.8, 17.72) * mm});
            skLineSegment(sketch, "E874", {"start": v(-47.8, 17.72) * mm, "end": v(-47.4, 17.57) * mm});
            skLineSegment(sketch, "E875", {"start": v(-47.4, 17.57) * mm, "end": v(-46.98, 17.4) * mm});
            skLineSegment(sketch, "E876", {"start": v(-46.98, 17.4) * mm, "end": v(-46.59, 17.25) * mm});
            skLineSegment(sketch, "E877", {"start": v(-46.59, 17.25) * mm, "end": v(-46.47, 17.2) * mm});
            skLineSegment(sketch, "E878", {"start": v(-46.47, 17.2) * mm, "end": v(-46.6, 16.8) * mm});
            skLineSegment(sketch, "E879", {"start": v(-46.6, 16.8) * mm, "end": v(-46.73, 16.4) * mm});
            skLineSegment(sketch, "E880", {"start": v(-46.73, 16.4) * mm, "end": v(-46.87, 16) * mm});
            skLineSegment(sketch, "E881", {"start": v(-46.87, 16) * mm, "end": v(-47, 15.6) * mm});
            skLineSegment(sketch, "E882", {"start": v(-47, 15.6) * mm, "end": v(-47.13, 15.2) * mm});
            skLineSegment(sketch, "E883", {"start": v(-47.13, 15.2) * mm, "end": v(-47.27, 14.8) * mm});
            skLineSegment(sketch, "E884", {"start": v(-47.27, 14.8) * mm, "end": v(-47.4, 14.4) * mm});
            skLineSegment(sketch, "E885", {"start": v(-47.4, 14.4) * mm, "end": v(-47.53, 14) * mm});
            skLineSegment(sketch, "E886", {"start": v(-47.53, 14) * mm, "end": v(-47.67, 13.6) * mm});
            skLineSegment(sketch, "E887", {"start": v(-47.67, 13.6) * mm, "end": v(-47.8, 13.2) * mm});
            skLineSegment(sketch, "E888", {"start": v(-47.8, 13.2) * mm, "end": v(-47.92, 12.84) * mm});
            skLineSegment(sketch, "E889", {"start": v(-47.92, 12.84) * mm, "end": v(-48.33, 12.95) * mm});
            skLineSegment(sketch, "E890", {"start": v(-48.33, 12.95) * mm, "end": v(-48.74, 13.07) * mm});
            skLineSegment(sketch, "E891", {"start": v(-48.74, 13.07) * mm, "end": v(-49.17, 13.19) * mm});
            skLineSegment(sketch, "E892", {"start": v(-49.17, 13.19) * mm, "end": v(-49.57, 13.3) * mm});
            skLineSegment(sketch, "E893", {"start": v(-49.57, 13.3) * mm, "end": v(-49.98, 13.42) * mm});
            skLineSegment(sketch, "E894", {"start": v(-49.98, 13.42) * mm, "end": v(-50.41, 13.54) * mm});
            skLineSegment(sketch, "E895", {"start": v(-50.41, 13.54) * mm, "end": v(-50.82, 13.65) * mm});
            skLineSegment(sketch, "E896", {"start": v(-50.82, 13.65) * mm, "end": v(-51.22, 13.77) * mm});
            skLineSegment(sketch, "E897", {"start": v(-51.22, 13.77) * mm, "end": v(-51.66, 13.89) * mm});
            skLineSegment(sketch, "E898", {"start": v(-51.66, 13.89) * mm, "end": v(-52.06, 14) * mm});
            skLineSegment(sketch, "E899", {"start": v(-52.06, 14) * mm, "end": v(-52.47, 14.11) * mm});
            skLineSegment(sketch, "E900", {"start": v(-52.47, 14.11) * mm, "end": v(-52.9, 14.24) * mm});
            skLineSegment(sketch, "E901", {"start": v(-52.9, 14.24) * mm, "end": v(-53.34, 14.36) * mm});
            skLineSegment(sketch, "E902", {"start": v(-53.34, 14.36) * mm, "end": v(-53.7, 14.4) * mm});
            skLineSegment(sketch, "E903", {"start": v(-53.7, 14.4) * mm, "end": v(-54.15, 14.33) * mm});
            skLineSegment(sketch, "E904", {"start": v(-54.15, 14.33) * mm, "end": v(-54.56, 14.15) * mm});
            skLineSegment(sketch, "E905", {"start": v(-54.56, 14.15) * mm, "end": v(-54.91, 13.88) * mm});
            skLineSegment(sketch, "E906", {"start": v(-54.91, 13.88) * mm, "end": v(-55.18, 13.52) * mm});
            skLineSegment(sketch, "E907", {"start": v(-55.18, 13.52) * mm, "end": v(-55.34, 13.1) * mm});
            skLineSegment(sketch, "E908", {"start": v(-55.34, 13.1) * mm, "end": v(-55.39, 12.65) * mm});
            skLineSegment(sketch, "E909", {"start": v(-55.39, 12.65) * mm, "end": v(-55.32, 12.2) * mm});
            skLineSegment(sketch, "E910", {"start": v(-55.32, 12.2) * mm, "end": v(-55.14, 11.8) * mm});
            skLineSegment(sketch, "E911", {"start": v(-55.14, 11.8) * mm, "end": v(-54.86, 11.45) * mm});
            skLineSegment(sketch, "E912", {"start": v(-54.86, 11.45) * mm, "end": v(-54.5, 11.2) * mm});
            skLineSegment(sketch, "E913", {"start": v(-54.5, 11.2) * mm, "end": v(-54.07, 11.03) * mm});
            skLineSegment(sketch, "E914", {"start": v(-54.07, 11.03) * mm, "end": v(-53.66, 10.95) * mm});
            skLineSegment(sketch, "E915", {"start": v(-53.66, 10.95) * mm, "end": v(-53.25, 10.86) * mm});
            skLineSegment(sketch, "E916", {"start": v(-53.25, 10.86) * mm, "end": v(-52.8, 10.77) * mm});
            skLineSegment(sketch, "E917", {"start": v(-52.8, 10.77) * mm, "end": v(-52.4, 10.68) * mm});
            skLineSegment(sketch, "E918", {"start": v(-52.4, 10.68) * mm, "end": v(-51.98, 10.59) * mm});
            skLineSegment(sketch, "E919", {"start": v(-51.98, 10.59) * mm, "end": v(-51.54, 10.5) * mm});
            skLineSegment(sketch, "E920", {"start": v(-51.54, 10.5) * mm, "end": v(-51.13, 10.4) * mm});
            skLineSegment(sketch, "E921", {"start": v(-51.13, 10.4) * mm, "end": v(-50.72, 10.32) * mm});
            skLineSegment(sketch, "E922", {"start": v(-50.72, 10.32) * mm, "end": v(-50.28, 10.23) * mm});
            skLineSegment(sketch, "E923", {"start": v(-50.28, 10.23) * mm, "end": v(-49.87, 10.14) * mm});
            skLineSegment(sketch, "E924", {"start": v(-49.87, 10.14) * mm, "end": v(-49.45, 10.05) * mm});
            skLineSegment(sketch, "E925", {"start": v(-49.45, 10.05) * mm, "end": v(-49.01, 9.96) * mm});
            skLineSegment(sketch, "E926", {"start": v(-49.01, 9.96) * mm, "end": v(-48.65, 9.88) * mm});
            skLineSegment(sketch, "E927", {"start": v(-48.65, 9.88) * mm, "end": v(-48.72, 9.47) * mm});
            skLineSegment(sketch, "E928", {"start": v(-48.72, 9.47) * mm, "end": v(-48.79, 9.05) * mm});
            skLineSegment(sketch, "E929", {"start": v(-48.79, 9.05) * mm, "end": v(-48.86, 8.63) * mm});
            skLineSegment(sketch, "E930", {"start": v(-48.86, 8.63) * mm, "end": v(-48.92, 8.22) * mm});
            skLineSegment(sketch, "E931", {"start": v(-48.92, 8.22) * mm, "end": v(-49, 7.8) * mm});
            skLineSegment(sketch, "E932", {"start": v(-49, 7.8) * mm, "end": v(-49.06, 7.38) * mm});
            skLineSegment(sketch, "E933", {"start": v(-49.06, 7.38) * mm, "end": v(-49.13, 6.97) * mm});
            skLineSegment(sketch, "E934", {"start": v(-49.13, 6.97) * mm, "end": v(-49.2, 6.55) * mm});
            skLineSegment(sketch, "E935", {"start": v(-49.2, 6.55) * mm, "end": v(-49.26, 6.14) * mm});
            skLineSegment(sketch, "E936", {"start": v(-49.26, 6.14) * mm, "end": v(-49.33, 5.72) * mm});
            skLineSegment(sketch, "E937", {"start": v(-49.33, 5.72) * mm, "end": v(-49.4, 5.34) * mm});
            skLineSegment(sketch, "E938", {"start": v(-49.4, 5.34) * mm, "end": v(-49.8, 5.38) * mm});
            skLineSegment(sketch, "E939", {"start": v(-49.8, 5.38) * mm, "end": v(-50.23, 5.43) * mm});
            skLineSegment(sketch, "E940", {"start": v(-50.23, 5.43) * mm, "end": v(-50.68, 5.48) * mm});
            skLineSegment(sketch, "E941", {"start": v(-50.68, 5.48) * mm, "end": v(-51.1, 5.53) * mm});
            skLineSegment(sketch, "E942", {"start": v(-51.1, 5.53) * mm, "end": v(-51.51, 5.58) * mm});
            skLineSegment(sketch, "E943", {"start": v(-51.51, 5.58) * mm, "end": v(-51.96, 5.63) * mm});
            skLineSegment(sketch, "E944", {"start": v(-51.96, 5.63) * mm, "end": v(-52.38, 5.68) * mm});
            skLineSegment(sketch, "E945", {"start": v(-52.38, 5.68) * mm, "end": v(-52.8, 5.72) * mm});
            skLineSegment(sketch, "E946", {"start": v(-52.8, 5.72) * mm, "end": v(-53.24, 5.77) * mm});
            skLineSegment(sketch, "E947", {"start": v(-53.24, 5.77) * mm, "end": v(-53.66, 5.82) * mm});
            skLineSegment(sketch, "E948", {"start": v(-53.66, 5.82) * mm, "end": v(-54.08, 5.87) * mm});
            skLineSegment(sketch, "E949", {"start": v(-54.08, 5.87) * mm, "end": v(-54.53, 5.92) * mm});
            skLineSegment(sketch, "E950", {"start": v(-54.53, 5.92) * mm, "end": v(-54.99, 5.97) * mm});
            skLineSegment(sketch, "E951", {"start": v(-54.99, 5.97) * mm, "end": v(-55.08, 5.97) * mm});
            skLineSegment(sketch, "E952", {"start": v(-55.08, 5.97) * mm, "end": v(-55.52, 5.9) * mm});
            skLineSegment(sketch, "E953", {"start": v(-55.52, 5.9) * mm, "end": v(-55.93, 5.73) * mm});
            skLineSegment(sketch, "E954", {"start": v(-55.93, 5.73) * mm, "end": v(-56.28, 5.45) * mm});
            skLineSegment(sketch, "E955", {"start": v(-56.28, 5.45) * mm, "end": v(-56.55, 5.09) * mm});
            skLineSegment(sketch, "E956", {"start": v(-56.55, 5.09) * mm, "end": v(-56.71, 4.67) * mm});
            skLineSegment(sketch, "E957", {"start": v(-56.71, 4.67) * mm, "end": v(-56.76, 4.22) * mm});
            skLineSegment(sketch, "E958", {"start": v(-56.76, 4.22) * mm, "end": v(-56.69, 3.78) * mm});
            skLineSegment(sketch, "E959", {"start": v(-56.69, 3.78) * mm, "end": v(-56.5, 3.37) * mm});
            skLineSegment(sketch, "E960", {"start": v(-56.5, 3.37) * mm, "end": v(-56.22, 3.03) * mm});
            skLineSegment(sketch, "E961", {"start": v(-56.22, 3.03) * mm, "end": v(-55.86, 2.77) * mm});
            skLineSegment(sketch, "E962", {"start": v(-55.86, 2.77) * mm, "end": v(-55.44, 2.6) * mm});
            skLineSegment(sketch, "E963", {"start": v(-55.44, 2.6) * mm, "end": v(-54.98, 2.56) * mm});
            skLineSegment(sketch, "E964", {"start": v(-54.98, 2.56) * mm, "end": v(-54.56, 2.54) * mm});
            skLineSegment(sketch, "E965", {"start": v(-54.56, 2.54) * mm, "end": v(-54.14, 2.52) * mm});
            skLineSegment(sketch, "E966", {"start": v(-54.14, 2.52) * mm, "end": v(-53.7, 2.5) * mm});
            skLineSegment(sketch, "E967", {"start": v(-53.7, 2.5) * mm, "end": v(-53.27, 2.48) * mm});
            skLineSegment(sketch, "E968", {"start": v(-53.27, 2.48) * mm, "end": v(-52.85, 2.46) * mm});
            skLineSegment(sketch, "E969", {"start": v(-52.85, 2.46) * mm, "end": v(-52.4, 2.44) * mm});
            skLineSegment(sketch, "E970", {"start": v(-52.4, 2.44) * mm, "end": v(-51.98, 2.42) * mm});
            skLineSegment(sketch, "E971", {"start": v(-51.98, 2.42) * mm, "end": v(-51.56, 2.4) * mm});
            skLineSegment(sketch, "E972", {"start": v(-51.56, 2.4) * mm, "end": v(-51.11, 2.37) * mm});
            skLineSegment(sketch, "E973", {"start": v(-51.11, 2.37) * mm, "end": v(-50.7, 2.35) * mm});
            skLineSegment(sketch, "E974", {"start": v(-50.7, 2.35) * mm, "end": v(-50.27, 2.33) * mm});
            skLineSegment(sketch, "E975", {"start": v(-50.27, 2.33) * mm, "end": v(-49.82, 2.31) * mm});
            skLineSegment(sketch, "E976", {"start": v(-49.82, 2.31) * mm, "end": v(-49.64, 2.3) * mm});
            skLineSegment(sketch, "E977", {"start": v(-49.64, 2.3) * mm, "end": v(-49.64, 1.88) * mm});
            skLineSegment(sketch, "E978", {"start": v(-49.64, 1.88) * mm, "end": v(-49.64, 1.46) * mm});
            skLineSegment(sketch, "E979", {"start": v(-49.64, 1.46) * mm, "end": v(-49.64, 1.04) * mm});
            skLineSegment(sketch, "E980", {"start": v(-49.64, 1.04) * mm, "end": v(-49.64, 0.62) * mm});
            skLineSegment(sketch, "E981", {"start": v(-49.64, 0.62) * mm, "end": v(-49.64, 0.2) * mm});
            skLineSegment(sketch, "E982", {"start": v(-49.64, 0.2) * mm, "end": v(-49.64, -0.23) * mm});
            skLineSegment(sketch, "E983", {"start": v(-49.64, -0.23) * mm, "end": v(-49.64, -0.65) * mm});
            skLineSegment(sketch, "E984", {"start": v(-49.64, -0.65) * mm, "end": v(-49.64, -1.07) * mm});
            skLineSegment(sketch, "E985", {"start": v(-49.64, -1.07) * mm, "end": v(-49.64, -1.5) * mm});
            skLineSegment(sketch, "E986", {"start": v(-49.64, -1.5) * mm, "end": v(-49.64, -1.91) * mm});
            skLineSegment(sketch, "E987", {"start": v(-49.64, -1.91) * mm, "end": v(-49.64, -2.3) * mm});
            skLineSegment(sketch, "E988", {"start": v(-49.64, -2.3) * mm, "end": v(-50.06, -2.32) * mm});
            skLineSegment(sketch, "E989", {"start": v(-50.06, -2.32) * mm, "end": v(-50.48, -2.34) * mm});
            skLineSegment(sketch, "E990", {"start": v(-50.48, -2.34) * mm, "end": v(-50.93, -2.36) * mm});
            skLineSegment(sketch, "E991", {"start": v(-50.93, -2.36) * mm, "end": v(-51.35, -2.38) * mm});
            skLineSegment(sketch, "E992", {"start": v(-51.35, -2.38) * mm, "end": v(-51.77, -2.4) * mm});
            skLineSegment(sketch, "E993", {"start": v(-51.77, -2.4) * mm, "end": v(-52.22, -2.43) * mm});
            skLineSegment(sketch, "E994", {"start": v(-52.22, -2.43) * mm, "end": v(-52.64, -2.45) * mm});
            skLineSegment(sketch, "E995", {"start": v(-52.64, -2.45) * mm, "end": v(-53.06, -2.47) * mm});
            skLineSegment(sketch, "E996", {"start": v(-53.06, -2.47) * mm, "end": v(-53.5, -2.49) * mm});
            skLineSegment(sketch, "E997", {"start": v(-53.5, -2.49) * mm, "end": v(-53.93, -2.51) * mm});
            skLineSegment(sketch, "E998", {"start": v(-53.93, -2.51) * mm, "end": v(-54.35, -2.53) * mm});
            skLineSegment(sketch, "E999", {"start": v(-54.35, -2.53) * mm, "end": v(-54.8, -2.55) * mm});
            skLineSegment(sketch, "E1000", {"start": v(-54.8, -2.55) * mm, "end": v(-55.26, -2.58) * mm});
            skLineSegment(sketch, "E1001", {"start": v(-55.26, -2.58) * mm, "end": v(-55.7, -2.69) * mm});
            skLineSegment(sketch, "E1002", {"start": v(-55.7, -2.69) * mm, "end": v(-56.08, -2.9) * mm});
            skLineSegment(sketch, "E1003", {"start": v(-56.08, -2.9) * mm, "end": v(-56.4, -3.22) * mm});
            skLineSegment(sketch, "E1004", {"start": v(-56.4, -3.22) * mm, "end": v(-56.63, -3.61) * mm});
            skLineSegment(sketch, "E1005", {"start": v(-56.63, -3.61) * mm, "end": v(-56.74, -4.05) * mm});
            skLineSegment(sketch, "E1006", {"start": v(-56.74, -4.05) * mm, "end": v(-56.74, -4.5) * mm});
            skLineSegment(sketch, "E1007", {"start": v(-56.74, -4.5) * mm, "end": v(-56.63, -4.93) * mm});
            skLineSegment(sketch, "E1008", {"start": v(-56.63, -4.93) * mm, "end": v(-56.4, -5.31) * mm});
            skLineSegment(sketch, "E1009", {"start": v(-56.4, -5.31) * mm, "end": v(-56.08, -5.63) * mm});
            skLineSegment(sketch, "E1010", {"start": v(-56.08, -5.63) * mm, "end": v(-55.69, -5.85) * mm});
            skLineSegment(sketch, "E1011", {"start": v(-55.69, -5.85) * mm, "end": v(-55.25, -5.96) * mm});
            skLineSegment(sketch, "E1012", {"start": v(-55.25, -5.96) * mm, "end": v(-54.83, -5.94) * mm});
            skLineSegment(sketch, "E1013", {"start": v(-54.83, -5.94) * mm, "end": v(-54.41, -5.9) * mm});
            skLineSegment(sketch, "E1014", {"start": v(-54.41, -5.9) * mm, "end": v(-53.98, -5.86) * mm});
            skLineSegment(sketch, "E1015", {"start": v(-53.98, -5.86) * mm, "end": v(-53.56, -5.8) * mm});
            skLineSegment(sketch, "E1016", {"start": v(-53.56, -5.8) * mm, "end": v(-53.14, -5.76) * mm});
            skLineSegment(sketch, "E1017", {"start": v(-53.14, -5.76) * mm, "end": v(-52.7, -5.71) * mm});
            skLineSegment(sketch, "E1018", {"start": v(-52.7, -5.71) * mm, "end": v(-52.27, -5.66) * mm});
            skLineSegment(sketch, "E1019", {"start": v(-52.27, -5.66) * mm, "end": v(-51.86, -5.62) * mm});
            skLineSegment(sketch, "E1020", {"start": v(-51.86, -5.62) * mm, "end": v(-51.4, -5.57) * mm});
            skLineSegment(sketch, "E1021", {"start": v(-51.4, -5.57) * mm, "end": v(-51, -5.52) * mm});
            skLineSegment(sketch, "E1022", {"start": v(-51, -5.52) * mm, "end": v(-50.57, -5.47) * mm});
            skLineSegment(sketch, "E1023", {"start": v(-50.57, -5.47) * mm, "end": v(-50.12, -5.42) * mm});
            skLineSegment(sketch, "E1024", {"start": v(-50.12, -5.42) * mm, "end": v(-49.7, -5.37) * mm});
            skLineSegment(sketch, "E1025", {"start": v(-49.7, -5.37) * mm, "end": v(-49.4, -5.34) * mm});
            skLineSegment(sketch, "E1026", {"start": v(-49.4, -5.34) * mm, "end": v(-49.32, -5.75) * mm});
            skLineSegment(sketch, "E1027", {"start": v(-49.32, -5.75) * mm, "end": v(-49.26, -6.17) * mm});
            skLineSegment(sketch, "E1028", {"start": v(-49.26, -6.17) * mm, "end": v(-49.19, -6.59) * mm});
            skLineSegment(sketch, "E1029", {"start": v(-49.19, -6.59) * mm, "end": v(-49.12, -7) * mm});
            skLineSegment(sketch, "E1030", {"start": v(-49.12, -7) * mm, "end": v(-49.05, -7.42) * mm});
            skLineSegment(sketch, "E1031", {"start": v(-49.05, -7.42) * mm, "end": v(-48.99, -7.83) * mm});
            skLineSegment(sketch, "E1032", {"start": v(-48.99, -7.83) * mm, "end": v(-48.92, -8.25) * mm});
            skLineSegment(sketch, "E1033", {"start": v(-48.92, -8.25) * mm, "end": v(-48.85, -8.67) * mm});
            skLineSegment(sketch, "E1034", {"start": v(-48.85, -8.67) * mm, "end": v(-48.78, -9.08) * mm});
            skLineSegment(sketch, "E1035", {"start": v(-48.78, -9.08) * mm, "end": v(-48.71, -9.5) * mm});
            skLineSegment(sketch, "E1036", {"start": v(-48.71, -9.5) * mm, "end": v(-48.65, -9.88) * mm});
            skLineSegment(sketch, "E1037", {"start": v(-48.65, -9.88) * mm, "end": v(-49.06, -9.97) * mm});
            skLineSegment(sketch, "E1038", {"start": v(-49.06, -9.97) * mm, "end": v(-49.48, -10.06) * mm});
            skLineSegment(sketch, "E1039", {"start": v(-49.48, -10.06) * mm, "end": v(-49.92, -10.15) * mm});
            skLineSegment(sketch, "E1040", {"start": v(-49.92, -10.15) * mm, "end": v(-50.33, -10.24) * mm});
            skLineSegment(sketch, "E1041", {"start": v(-50.33, -10.24) * mm, "end": v(-50.74, -10.33) * mm});
            skLineSegment(sketch, "E1042", {"start": v(-50.74, -10.33) * mm, "end": v(-51.18, -10.42) * mm});
            skLineSegment(sketch, "E1043", {"start": v(-51.18, -10.42) * mm, "end": v(-51.6, -10.5) * mm});
            skLineSegment(sketch, "E1044", {"start": v(-51.6, -10.5) * mm, "end": v(-52, -10.6) * mm});
            skLineSegment(sketch, "E1045", {"start": v(-52, -10.6) * mm, "end": v(-52.45, -10.69) * mm});
            skLineSegment(sketch, "E1046", {"start": v(-52.45, -10.69) * mm, "end": v(-52.86, -10.78) * mm});
            skLineSegment(sketch, "E1047", {"start": v(-52.86, -10.78) * mm, "end": v(-53.27, -10.86) * mm});
            skLineSegment(sketch, "E1048", {"start": v(-53.27, -10.86) * mm, "end": v(-53.7, -10.96) * mm});
            skLineSegment(sketch, "E1049", {"start": v(-53.7, -10.96) * mm, "end": v(-54.16, -11.06) * mm});
            skLineSegment(sketch, "E1050", {"start": v(-54.16, -11.06) * mm, "end": v(-54.57, -11.24) * mm});
            skLineSegment(sketch, "E1051", {"start": v(-54.57, -11.24) * mm, "end": v(-54.92, -11.52) * mm});
            skLineSegment(sketch, "E1052", {"start": v(-54.92, -11.52) * mm, "end": v(-55.18, -11.88) * mm});
            skLineSegment(sketch, "E1053", {"start": v(-55.18, -11.88) * mm, "end": v(-55.34, -12.3) * mm});
            skLineSegment(sketch, "E1054", {"start": v(-55.34, -12.3) * mm, "end": v(-55.39, -12.74) * mm});
            skLineSegment(sketch, "E1055", {"start": v(-55.39, -12.74) * mm, "end": v(-55.32, -13.19) * mm});
            skLineSegment(sketch, "E1056", {"start": v(-55.32, -13.19) * mm, "end": v(-55.13, -13.6) * mm});
            skLineSegment(sketch, "E1057", {"start": v(-55.13, -13.6) * mm, "end": v(-54.85, -13.94) * mm});
            skLineSegment(sketch, "E1058", {"start": v(-54.85, -13.94) * mm, "end": v(-54.48, -14.2) * mm});
            skLineSegment(sketch, "E1059", {"start": v(-54.48, -14.2) * mm, "end": v(-54.06, -14.35) * mm});
            skLineSegment(sketch, "E1060", {"start": v(-54.06, -14.35) * mm, "end": v(-53.61, -14.4) * mm});
            skLineSegment(sketch, "E1061", {"start": v(-53.61, -14.4) * mm, "end": v(-53.2, -14.3) * mm});
            skLineSegment(sketch, "E1062", {"start": v(-53.2, -14.3) * mm, "end": v(-52.8, -14.2) * mm});
            skLineSegment(sketch, "E1063", {"start": v(-52.8, -14.2) * mm, "end": v(-52.37, -14.09) * mm});
            skLineSegment(sketch, "E1064", {"start": v(-52.37, -14.09) * mm, "end": v(-51.96, -13.97) * mm});
            skLineSegment(sketch, "E1065", {"start": v(-51.96, -13.97) * mm, "end": v(-51.56, -13.86) * mm});
            skLineSegment(sketch, "E1066", {"start": v(-51.56, -13.86) * mm, "end": v(-51.12, -13.74) * mm});
            skLineSegment(sketch, "E1067", {"start": v(-51.12, -13.74) * mm, "end": v(-50.72, -13.62) * mm});
            skLineSegment(sketch, "E1068", {"start": v(-50.72, -13.62) * mm, "end": v(-50.31, -13.5) * mm});
            skLineSegment(sketch, "E1069", {"start": v(-50.31, -13.5) * mm, "end": v(-49.88, -13.39) * mm});
            skLineSegment(sketch, "E1070", {"start": v(-49.88, -13.39) * mm, "end": v(-49.47, -13.27) * mm});
            skLineSegment(sketch, "E1071", {"start": v(-49.47, -13.27) * mm, "end": v(-49.07, -13.16) * mm});
            skLineSegment(sketch, "E1072", {"start": v(-49.07, -13.16) * mm, "end": v(-48.63, -13.04) * mm});
            skLineSegment(sketch, "E1073", {"start": v(-48.63, -13.04) * mm, "end": v(-48.23, -12.92) * mm});
            skLineSegment(sketch, "E1074", {"start": v(-48.23, -12.92) * mm, "end": v(-47.92, -12.84) * mm});
            skLineSegment(sketch, "E1075", {"start": v(-47.92, -12.84) * mm, "end": v(-47.79, -13.24) * mm});
            skLineSegment(sketch, "E1076", {"start": v(-47.79, -13.24) * mm, "end": v(-47.66, -13.64) * mm});
            skLineSegment(sketch, "E1077", {"start": v(-47.66, -13.64) * mm, "end": v(-47.52, -14.04) * mm});
            skLineSegment(sketch, "E1078", {"start": v(-47.52, -14.04) * mm, "end": v(-47.39, -14.44) * mm});
            skLineSegment(sketch, "E1079", {"start": v(-47.39, -14.44) * mm, "end": v(-47.26, -14.84) * mm});
            skLineSegment(sketch, "E1080", {"start": v(-47.26, -14.84) * mm, "end": v(-47.12, -15.24) * mm});
            skLineSegment(sketch, "E1081", {"start": v(-47.12, -15.24) * mm, "end": v(-46.99, -15.64) * mm});
            skLineSegment(sketch, "E1082", {"start": v(-46.99, -15.64) * mm, "end": v(-46.86, -16.04) * mm});
            skLineSegment(sketch, "E1083", {"start": v(-46.86, -16.04) * mm, "end": v(-46.72, -16.44) * mm});
            skLineSegment(sketch, "E1084", {"start": v(-46.72, -16.44) * mm, "end": v(-46.59, -16.84) * mm});
            skLineSegment(sketch, "E1085", {"start": v(-46.59, -16.84) * mm, "end": v(-46.47, -17.2) * mm});
            skLineSegment(sketch, "E1086", {"start": v(-46.47, -17.2) * mm, "end": v(-46.86, -17.36) * mm});
            skLineSegment(sketch, "E1087", {"start": v(-46.86, -17.36) * mm, "end": v(-47.25, -17.51) * mm});
            skLineSegment(sketch, "E1088", {"start": v(-47.25, -17.51) * mm, "end": v(-47.67, -17.67) * mm});
            skLineSegment(sketch, "E1089", {"start": v(-47.67, -17.67) * mm, "end": v(-48.06, -17.83) * mm});
            skLineSegment(sketch, "E1090", {"start": v(-48.06, -17.83) * mm, "end": v(-48.46, -17.98) * mm});
            skLineSegment(sketch, "E1091", {"start": v(-48.46, -17.98) * mm, "end": v(-48.88, -18.14) * mm});
            skLineSegment(sketch, "E1092", {"start": v(-48.88, -18.14) * mm, "end": v(-49.27, -18.3) * mm});
            skLineSegment(sketch, "E1093", {"start": v(-49.27, -18.3) * mm, "end": v(-49.66, -18.45) * mm});
            skLineSegment(sketch, "E1094", {"start": v(-49.66, -18.45) * mm, "end": v(-50.08, -18.61) * mm});
            skLineSegment(sketch, "E1095", {"start": v(-50.08, -18.61) * mm, "end": v(-50.47, -18.76) * mm});
            skLineSegment(sketch, "E1096", {"start": v(-50.47, -18.76) * mm, "end": v(-50.87, -18.92) * mm});
            skLineSegment(sketch, "E1097", {"start": v(-50.87, -18.92) * mm, "end": v(-51.28, -19.08) * mm});
            skLineSegment(sketch, "E1098", {"start": v(-51.28, -19.08) * mm, "end": v(-51.71, -19.25) * mm});
            skLineSegment(sketch, "E1099", {"start": v(-51.71, -19.25) * mm, "end": v(-52.09, -19.5) * mm});
            skLineSegment(sketch, "E1100", {"start": v(-52.09, -19.5) * mm, "end": v(-52.39, -19.82) * mm});
            skLineSegment(sketch, "E1101", {"start": v(-52.39, -19.82) * mm, "end": v(-52.6, -20.22) * mm});
            skLineSegment(sketch, "E1102", {"start": v(-52.6, -20.22) * mm, "end": v(-52.68, -20.66) * mm});
            skLineSegment(sketch, "E1103", {"start": v(-52.68, -20.66) * mm, "end": v(-52.66, -21.11) * mm});
            skLineSegment(sketch, "E1104", {"start": v(-52.66, -21.11) * mm, "end": v(-52.51, -21.54) * mm});
            skLineSegment(sketch, "E1105", {"start": v(-52.51, -21.54) * mm, "end": v(-52.27, -21.9) * mm});
            skLineSegment(sketch, "E1106", {"start": v(-52.27, -21.9) * mm, "end": v(-51.93, -22.2) * mm});
            skLineSegment(sketch, "E1107", {"start": v(-51.93, -22.2) * mm, "end": v(-51.53, -22.4) * mm});
            skLineSegment(sketch, "E1108", {"start": v(-51.53, -22.4) * mm, "end": v(-51.08, -22.48) * mm});
            skLineSegment(sketch, "E1109", {"start": v(-51.08, -22.48) * mm, "end": v(-50.64, -22.45) * mm});
            skLineSegment(sketch, "E1110", {"start": v(-50.64, -22.45) * mm, "end": v(-50.24, -22.3) * mm});
            skLineSegment(sketch, "E1111", {"start": v(-50.24, -22.3) * mm, "end": v(-49.86, -22.14) * mm});
            skLineSegment(sketch, "E1112", {"start": v(-49.86, -22.14) * mm, "end": v(-49.46, -21.95) * mm});
            skLineSegment(sketch, "E1113", {"start": v(-49.46, -21.95) * mm, "end": v(-49.08, -21.77) * mm});
            skLineSegment(sketch, "E1114", {"start": v(-49.08, -21.77) * mm, "end": v(-48.7, -21.6) * mm});
            skLineSegment(sketch, "E1115", {"start": v(-48.7, -21.6) * mm, "end": v(-48.29, -21.4) * mm});
            skLineSegment(sketch, "E1116", {"start": v(-48.29, -21.4) * mm, "end": v(-47.9, -21.23) * mm});
            skLineSegment(sketch, "E1117", {"start": v(-47.9, -21.23) * mm, "end": v(-47.52, -21.05) * mm});
            skLineSegment(sketch, "E1118", {"start": v(-47.52, -21.05) * mm, "end": v(-47.11, -20.86) * mm});
            skLineSegment(sketch, "E1119", {"start": v(-47.11, -20.86) * mm, "end": v(-46.73, -20.69) * mm});
            skLineSegment(sketch, "E1120", {"start": v(-46.73, -20.69) * mm, "end": v(-46.35, -20.5) * mm});
            skLineSegment(sketch, "E1121", {"start": v(-46.35, -20.5) * mm, "end": v(-45.94, -20.32) * mm});
            skLineSegment(sketch, "E1122", {"start": v(-45.94, -20.32) * mm, "end": v(-45.56, -20.14) * mm});
            skLineSegment(sketch, "E1123", {"start": v(-45.56, -20.14) * mm, "end": v(-45.27, -20) * mm});
            skLineSegment(sketch, "E1124", {"start": v(-45.27, -20) * mm, "end": v(-45.08, -20.38) * mm});
            skLineSegment(sketch, "E1125", {"start": v(-45.08, -20.38) * mm, "end": v(-44.88, -20.75) * mm});
            skLineSegment(sketch, "E1126", {"start": v(-44.88, -20.75) * mm, "end": v(-44.68, -21.13) * mm});
            skLineSegment(sketch, "E1127", {"start": v(-44.68, -21.13) * mm, "end": v(-44.49, -21.5) * mm});
            skLineSegment(sketch, "E1128", {"start": v(-44.49, -21.5) * mm, "end": v(-44.3, -21.87) * mm});
            skLineSegment(sketch, "E1129", {"start": v(-44.3, -21.87) * mm, "end": v(-44.1, -22.25) * mm});
            skLineSegment(sketch, "E1130", {"start": v(-44.1, -22.25) * mm, "end": v(-43.9, -22.62) * mm});
            skLineSegment(sketch, "E1131", {"start": v(-43.9, -22.62) * mm, "end": v(-43.7, -23) * mm});
            skLineSegment(sketch, "E1132", {"start": v(-43.7, -23) * mm, "end": v(-43.5, -23.37) * mm});
            skLineSegment(sketch, "E1133", {"start": v(-43.5, -23.37) * mm, "end": v(-43.31, -23.74) * mm});
            skLineSegment(sketch, "E1134", {"start": v(-43.31, -23.74) * mm, "end": v(-43.13, -24.08) * mm});
            skLineSegment(sketch, "E1135", {"start": v(-43.13, -24.08) * mm, "end": v(-43.5, -24.3) * mm});
            skLineSegment(sketch, "E1136", {"start": v(-43.5, -24.3) * mm, "end": v(-43.86, -24.51) * mm});
            skLineSegment(sketch, "E1137", {"start": v(-43.86, -24.51) * mm, "end": v(-44.25, -24.74) * mm});
            skLineSegment(sketch, "E1138", {"start": v(-44.25, -24.74) * mm, "end": v(-44.6, -24.95) * mm});
            skLineSegment(sketch, "E1139", {"start": v(-44.6, -24.95) * mm, "end": v(-44.97, -25.17) * mm});
            skLineSegment(sketch, "E1140", {"start": v(-44.97, -25.17) * mm, "end": v(-45.36, -25.4) * mm});
            skLineSegment(sketch, "E1141", {"start": v(-45.36, -25.4) * mm, "end": v(-45.72, -25.6) * mm});
            skLineSegment(sketch, "E1142", {"start": v(-45.72, -25.6) * mm, "end": v(-46.09, -25.82) * mm});
            skLineSegment(sketch, "E1143", {"start": v(-46.09, -25.82) * mm, "end": v(-46.47, -26.05) * mm});
            skLineSegment(sketch, "E1144", {"start": v(-46.47, -26.05) * mm, "end": v(-46.84, -26.26) * mm});
            skLineSegment(sketch, "E1145", {"start": v(-46.84, -26.26) * mm, "end": v(-47.2, -26.48) * mm});
            skLineSegment(sketch, "E1146", {"start": v(-47.2, -26.48) * mm, "end": v(-47.59, -26.7) * mm});
            skLineSegment(sketch, "E1147", {"start": v(-47.59, -26.7) * mm, "end": v(-47.98, -26.94) * mm});
            skLineSegment(sketch, "E1148", {"start": v(-47.98, -26.94) * mm, "end": v(-48.32, -27.24) * mm});
            skLineSegment(sketch, "E1149", {"start": v(-48.32, -27.24) * mm, "end": v(-48.56, -27.62) * mm});
            skLineSegment(sketch, "E1150", {"start": v(-48.56, -27.62) * mm, "end": v(-48.7, -28.05) * mm});
            skLineSegment(sketch, "E1151", {"start": v(-48.7, -28.05) * mm, "end": v(-48.72, -28.5) * mm});
            skLineSegment(sketch, "E1152", {"start": v(-48.72, -28.5) * mm, "end": v(-48.62, -28.93) * mm});
            skLineSegment(sketch, "E1153", {"start": v(-48.62, -28.93) * mm, "end": v(-48.4, -29.33) * mm});
            skLineSegment(sketch, "E1154", {"start": v(-48.4, -29.33) * mm, "end": v(-48.1, -29.66) * mm});
            skLineSegment(sketch, "E1155", {"start": v(-48.1, -29.66) * mm, "end": v(-47.72, -29.9) * mm});
            skLineSegment(sketch, "E1156", {"start": v(-47.72, -29.9) * mm, "end": v(-47.3, -30.02) * mm});
            skLineSegment(sketch, "E1157", {"start": v(-47.3, -30.02) * mm, "end": v(-46.84, -30.04) * mm});
            skLineSegment(sketch, "E1158", {"start": v(-46.84, -30.04) * mm, "end": v(-46.4, -29.93) * mm});
            skLineSegment(sketch, "E1159", {"start": v(-46.4, -29.93) * mm, "end": v(-46.04, -29.72) * mm});
            skLineSegment(sketch, "E1160", {"start": v(-46.04, -29.72) * mm, "end": v(-45.69, -29.5) * mm});
            skLineSegment(sketch, "E1161", {"start": v(-45.69, -29.5) * mm, "end": v(-45.33, -29.25) * mm});
            skLineSegment(sketch, "E1162", {"start": v(-45.33, -29.25) * mm, "end": v(-44.98, -29.01) * mm});
            skLineSegment(sketch, "E1163", {"start": v(-44.98, -29.01) * mm, "end": v(-44.63, -28.78) * mm});
            skLineSegment(sketch, "E1164", {"start": v(-44.63, -28.78) * mm, "end": v(-44.26, -28.52) * mm});
            skLineSegment(sketch, "E1165", {"start": v(-44.26, -28.52) * mm, "end": v(-43.9, -28.29) * mm});
            skLineSegment(sketch, "E1166", {"start": v(-43.9, -28.29) * mm, "end": v(-43.56, -28.05) * mm});
            skLineSegment(sketch, "E1167", {"start": v(-43.56, -28.05) * mm, "end": v(-43.19, -27.8) * mm});
            skLineSegment(sketch, "E1168", {"start": v(-43.19, -27.8) * mm, "end": v(-42.84, -27.56) * mm});
            skLineSegment(sketch, "E1169", {"start": v(-42.84, -27.56) * mm, "end": v(-42.49, -27.32) * mm});
            skLineSegment(sketch, "E1170", {"start": v(-42.49, -27.32) * mm, "end": v(-42.12, -27.07) * mm});
            skLineSegment(sketch, "E1171", {"start": v(-42.12, -27.07) * mm, "end": v(-41.77, -26.84) * mm});
            skLineSegment(sketch, "E1172", {"start": v(-41.77, -26.84) * mm, "end": v(-41.5, -26.66) * mm});
            skLineSegment(sketch, "E1173", {"start": v(-41.5, -26.66) * mm, "end": v(-41.25, -27) * mm});
            skLineSegment(sketch, "E1174", {"start": v(-41.25, -27) * mm, "end": v(-41, -27.33) * mm});
            skLineSegment(sketch, "E1175", {"start": v(-41, -27.33) * mm, "end": v(-40.74, -27.67) * mm});
            skLineSegment(sketch, "E1176", {"start": v(-40.74, -27.67) * mm, "end": v(-40.5, -28) * mm});
            skLineSegment(sketch, "E1177", {"start": v(-40.5, -28) * mm, "end": v(-40.24, -28.34) * mm});
            skLineSegment(sketch, "E1178", {"start": v(-40.24, -28.34) * mm, "end": v(-39.99, -28.68) * mm});
            skLineSegment(sketch, "E1179", {"start": v(-39.99, -28.68) * mm, "end": v(-39.73, -29.02) * mm});
            skLineSegment(sketch, "E1180", {"start": v(-39.73, -29.02) * mm, "end": v(-39.48, -29.35) * mm});
            skLineSegment(sketch, "E1181", {"start": v(-39.48, -29.35) * mm, "end": v(-39.23, -29.7) * mm});
            skLineSegment(sketch, "E1182", {"start": v(-39.23, -29.7) * mm, "end": v(-38.97, -30.03) * mm});
            skLineSegment(sketch, "E1183", {"start": v(-38.97, -30.03) * mm, "end": v(-38.74, -30.34) * mm});
            skLineSegment(sketch, "E1184", {"start": v(-38.74, -30.34) * mm, "end": v(-39.06, -30.6) * mm});
            skLineSegment(sketch, "E1185", {"start": v(-39.06, -30.6) * mm, "end": v(-39.39, -30.88) * mm});
            skLineSegment(sketch, "E1186", {"start": v(-39.39, -30.88) * mm, "end": v(-39.73, -31.16) * mm});
            skLineSegment(sketch, "E1187", {"start": v(-39.73, -31.16) * mm, "end": v(-40.06, -31.43) * mm});
            skLineSegment(sketch, "E1188", {"start": v(-40.06, -31.43) * mm, "end": v(-40.38, -31.7) * mm});
            skLineSegment(sketch, "E1189", {"start": v(-40.38, -31.7) * mm, "end": v(-40.73, -31.99) * mm});
            skLineSegment(sketch, "E1190", {"start": v(-40.73, -31.99) * mm, "end": v(-41.05, -32.26) * mm});
            skLineSegment(sketch, "E1191", {"start": v(-41.05, -32.26) * mm, "end": v(-41.38, -32.53) * mm});
            skLineSegment(sketch, "E1192", {"start": v(-41.38, -32.53) * mm, "end": v(-41.72, -32.81) * mm});
            skLineSegment(sketch, "E1193", {"start": v(-41.72, -32.81) * mm, "end": v(-42.05, -33.08) * mm});
            skLineSegment(sketch, "E1194", {"start": v(-42.05, -33.08) * mm, "end": v(-42.37, -33.35) * mm});
            skLineSegment(sketch, "E1195", {"start": v(-42.37, -33.35) * mm, "end": v(-42.72, -33.64) * mm});
            skLineSegment(sketch, "E1196", {"start": v(-42.72, -33.64) * mm, "end": v(-43.07, -33.94) * mm});
            skLineSegment(sketch, "E1197", {"start": v(-43.07, -33.94) * mm, "end": v(-43.35, -34.29) * mm});
            skLineSegment(sketch, "E1198", {"start": v(-43.35, -34.29) * mm, "end": v(-43.53, -34.7) * mm});
            skLineSegment(sketch, "E1199", {"start": v(-43.53, -34.7) * mm, "end": v(-43.6, -35.14) * mm});
            skLineSegment(sketch, "E1200", {"start": v(-43.6, -35.14) * mm, "end": v(-43.54, -35.59) * mm});
            skLineSegment(sketch, "E1201", {"start": v(-43.54, -35.59) * mm, "end": v(-43.38, -36) * mm});
            skLineSegment(sketch, "E1202", {"start": v(-43.38, -36) * mm, "end": v(-43.1, -36.36) * mm});
            skLineSegment(sketch, "E1203", {"start": v(-43.1, -36.36) * mm, "end": v(-42.75, -36.64) * mm});
            skLineSegment(sketch, "E1204", {"start": v(-42.75, -36.64) * mm, "end": v(-42.34, -36.8) * mm});
            skLineSegment(sketch, "E1205", {"start": v(-42.34, -36.8) * mm, "end": v(-41.9, -36.87) * mm});
            skLineSegment(sketch, "E1206", {"start": v(-41.9, -36.87) * mm, "end": v(-41.45, -36.8) * mm});
            skLineSegment(sketch, "E1207", {"start": v(-41.45, -36.8) * mm, "end": v(-41.04, -36.64) * mm});
            skLineSegment(sketch, "E1208", {"start": v(-41.04, -36.64) * mm, "end": v(-40.7, -36.37) * mm});
            skLineSegment(sketch, "E1209", {"start": v(-40.7, -36.37) * mm, "end": v(-40.4, -36.09) * mm});
            skLineSegment(sketch, "E1210", {"start": v(-40.4, -36.09) * mm, "end": v(-40.08, -35.79) * mm});
            skLineSegment(sketch, "E1211", {"start": v(-40.08, -35.79) * mm, "end": v(-39.77, -35.5) * mm});
            skLineSegment(sketch, "E1212", {"start": v(-39.77, -35.5) * mm, "end": v(-39.46, -35.2) * mm});
            skLineSegment(sketch, "E1213", {"start": v(-39.46, -35.2) * mm, "end": v(-39.14, -34.9) * mm});
            skLineSegment(sketch, "E1214", {"start": v(-39.14, -34.9) * mm, "end": v(-38.83, -34.61) * mm});
            skLineSegment(sketch, "E1215", {"start": v(-38.83, -34.61) * mm, "end": v(-38.52, -34.32) * mm});
            skLineSegment(sketch, "E1216", {"start": v(-38.52, -34.32) * mm, "end": v(-38.2, -34.01) * mm});
            skLineSegment(sketch, "E1217", {"start": v(-38.2, -34.01) * mm, "end": v(-37.89, -33.72) * mm});
            skLineSegment(sketch, "E1218", {"start": v(-37.89, -33.72) * mm, "end": v(-37.58, -33.43) * mm});
            skLineSegment(sketch, "E1219", {"start": v(-37.58, -33.43) * mm, "end": v(-37.26, -33.12) * mm});
            skLineSegment(sketch, "E1220", {"start": v(-37.26, -33.12) * mm, "end": v(-36.95, -32.84) * mm});
            skLineSegment(sketch, "E1221", {"start": v(-36.95, -32.84) * mm, "end": v(-36.72, -32.62) * mm});
            skLineSegment(sketch, "E1222", {"start": v(-36.72, -32.62) * mm, "end": v(-36.42, -32.9) * mm});
            skLineSegment(sketch, "E1223", {"start": v(-36.42, -32.9) * mm, "end": v(-36.11, -33.2) * mm});
            skLineSegment(sketch, "E1224", {"start": v(-36.11, -33.2) * mm, "end": v(-35.8, -33.5) * mm});
            skLineSegment(sketch, "E1225", {"start": v(-35.8, -33.5) * mm, "end": v(-35.5, -33.79) * mm});
            skLineSegment(sketch, "E1226", {"start": v(-35.5, -33.79) * mm, "end": v(-35.2, -34.08) * mm});
            skLineSegment(sketch, "E1227", {"start": v(-35.2, -34.08) * mm, "end": v(-34.9, -34.37) * mm});
            skLineSegment(sketch, "E1228", {"start": v(-34.9, -34.37) * mm, "end": v(-34.6, -34.66) * mm});
            skLineSegment(sketch, "E1229", {"start": v(-34.6, -34.66) * mm, "end": v(-34.29, -34.95) * mm});
            skLineSegment(sketch, "E1230", {"start": v(-34.29, -34.95) * mm, "end": v(-33.98, -35.25) * mm});
            skLineSegment(sketch, "E1231", {"start": v(-33.98, -35.25) * mm, "end": v(-33.68, -35.54) * mm});
            skLineSegment(sketch, "E1232", {"start": v(-33.68, -35.54) * mm, "end": v(-33.4, -35.8) * mm});
            skLineSegment(sketch, "E1233", {"start": v(-33.4, -35.8) * mm, "end": v(-33.68, -36.12) * mm});
            skLineSegment(sketch, "E1234", {"start": v(-33.68, -36.12) * mm, "end": v(-33.95, -36.44) * mm});
            skLineSegment(sketch, "E1235", {"start": v(-33.95, -36.44) * mm, "end": v(-34.25, -36.78) * mm});
            skLineSegment(sketch, "E1236", {"start": v(-34.25, -36.78) * mm, "end": v(-34.53, -37.1) * mm});
            skLineSegment(sketch, "E1237", {"start": v(-34.53, -37.1) * mm, "end": v(-34.8, -37.42) * mm});
            skLineSegment(sketch, "E1238", {"start": v(-34.8, -37.42) * mm, "end": v(-35.1, -37.76) * mm});
            skLineSegment(sketch, "E1239", {"start": v(-35.1, -37.76) * mm, "end": v(-35.37, -38.07) * mm});
            skLineSegment(sketch, "E1240", {"start": v(-35.37, -38.07) * mm, "end": v(-35.65, -38.4) * mm});
            skLineSegment(sketch, "E1241", {"start": v(-35.65, -38.4) * mm, "end": v(-35.95, -38.73) * mm});
            skLineSegment(sketch, "E1242", {"start": v(-35.95, -38.73) * mm, "end": v(-36.22, -39.05) * mm});
            skLineSegment(sketch, "E1243", {"start": v(-36.22, -39.05) * mm, "end": v(-36.5, -39.37) * mm});
            skLineSegment(sketch, "E1244", {"start": v(-36.5, -39.37) * mm, "end": v(-36.8, -39.7) * mm});
            skLineSegment(sketch, "E1245", {"start": v(-36.8, -39.7) * mm, "end": v(-37.1, -40.05) * mm});
            skLineSegment(sketch, "E1246", {"start": v(-37.1, -40.05) * mm, "end": v(-37.32, -40.44) * mm});
            skLineSegment(sketch, "E1247", {"start": v(-37.32, -40.44) * mm, "end": v(-37.43, -40.88) * mm});
            skLineSegment(sketch, "E1248", {"start": v(-37.43, -40.88) * mm, "end": v(-37.42, -41.33) * mm});
            skLineSegment(sketch, "E1249", {"start": v(-37.42, -41.33) * mm, "end": v(-37.3, -41.76) * mm});
            skLineSegment(sketch, "E1250", {"start": v(-37.3, -41.76) * mm, "end": v(-37.07, -42.14) * mm});
            skLineSegment(sketch, "E1251", {"start": v(-37.07, -42.14) * mm, "end": v(-36.74, -42.45) * mm});
            skLineSegment(sketch, "E1252", {"start": v(-36.74, -42.45) * mm, "end": v(-36.35, -42.67) * mm});
            skLineSegment(sketch, "E1253", {"start": v(-36.35, -42.67) * mm, "end": v(-35.91, -42.77) * mm});
            skLineSegment(sketch, "E1254", {"start": v(-35.91, -42.77) * mm, "end": v(-35.47, -42.76) * mm});
            skLineSegment(sketch, "E1255", {"start": v(-35.47, -42.76) * mm, "end": v(-35.04, -42.63) * mm});
            skLineSegment(sketch, "E1256", {"start": v(-35.04, -42.63) * mm, "end": v(-34.66, -42.4) * mm});
            skLineSegment(sketch, "E1257", {"start": v(-34.66, -42.4) * mm, "end": v(-34.37, -42.08) * mm});
            skLineSegment(sketch, "E1258", {"start": v(-34.37, -42.08) * mm, "end": v(-34.11, -41.75) * mm});
            skLineSegment(sketch, "E1259", {"start": v(-34.11, -41.75) * mm, "end": v(-33.84, -41.4) * mm});
            skLineSegment(sketch, "E1260", {"start": v(-33.84, -41.4) * mm, "end": v(-33.59, -41.07) * mm});
            skLineSegment(sketch, "E1261", {"start": v(-33.59, -41.07) * mm, "end": v(-33.33, -40.73) * mm});
            skLineSegment(sketch, "E1262", {"start": v(-33.33, -40.73) * mm, "end": v(-33.06, -40.37) * mm});
            skLineSegment(sketch, "E1263", {"start": v(-33.06, -40.37) * mm, "end": v(-32.8, -40.04) * mm});
            skLineSegment(sketch, "E1264", {"start": v(-32.8, -40.04) * mm, "end": v(-32.55, -39.7) * mm});
            skLineSegment(sketch, "E1265", {"start": v(-32.55, -39.7) * mm, "end": v(-32.27, -39.35) * mm});
            skLineSegment(sketch, "E1266", {"start": v(-32.27, -39.35) * mm, "end": v(-32.02, -39.01) * mm});
            skLineSegment(sketch, "E1267", {"start": v(-32.02, -39.01) * mm, "end": v(-31.76, -38.68) * mm});
            skLineSegment(sketch, "E1268", {"start": v(-31.76, -38.68) * mm, "end": v(-31.49, -38.32) * mm});
            skLineSegment(sketch, "E1269", {"start": v(-31.49, -38.32) * mm, "end": v(-31.23, -37.98) * mm});
            skLineSegment(sketch, "E1270", {"start": v(-31.23, -37.98) * mm, "end": v(-31.04, -37.73) * mm});
            skLineSegment(sketch, "E1271", {"start": v(-31.04, -37.73) * mm, "end": v(-30.7, -37.97) * mm});
            skLineSegment(sketch, "E1272", {"start": v(-30.7, -37.97) * mm, "end": v(-30.35, -38.21) * mm});
            skLineSegment(sketch, "E1273", {"start": v(-30.35, -38.21) * mm, "end": v(-30, -38.45) * mm});
            skLineSegment(sketch, "E1274", {"start": v(-30, -38.45) * mm, "end": v(-29.65, -38.7) * mm});
            skLineSegment(sketch, "E1275", {"start": v(-29.65, -38.7) * mm, "end": v(-29.3, -38.93) * mm});
            skLineSegment(sketch, "E1276", {"start": v(-29.3, -38.93) * mm, "end": v(-28.96, -39.17) * mm});
            skLineSegment(sketch, "E1277", {"start": v(-28.96, -39.17) * mm, "end": v(-28.61, -39.4) * mm});
            skLineSegment(sketch, "E1278", {"start": v(-28.61, -39.4) * mm, "end": v(-28.26, -39.65) * mm});
            skLineSegment(sketch, "E1279", {"start": v(-28.26, -39.65) * mm, "end": v(-27.92, -39.89) * mm});
            skLineSegment(sketch, "E1280", {"start": v(-27.92, -39.89) * mm, "end": v(-27.57, -40.13) * mm});
            skLineSegment(sketch, "E1281", {"start": v(-27.57, -40.13) * mm, "end": v(-27.25, -40.35) * mm});
            skLineSegment(sketch, "E1282", {"start": v(-27.25, -40.35) * mm, "end": v(-27.47, -40.7) * mm});
            skLineSegment(sketch, "E1283", {"start": v(-27.47, -40.7) * mm, "end": v(-27.7, -41.06) * mm});
            skLineSegment(sketch, "E1284", {"start": v(-27.7, -41.06) * mm, "end": v(-27.93, -41.45) * mm});
            skLineSegment(sketch, "E1285", {"start": v(-27.93, -41.45) * mm, "end": v(-28.16, -41.8) * mm});
            skLineSegment(sketch, "E1286", {"start": v(-28.16, -41.8) * mm, "end": v(-28.38, -42.16) * mm});
            skLineSegment(sketch, "E1287", {"start": v(-28.38, -42.16) * mm, "end": v(-28.62, -42.54) * mm});
            skLineSegment(sketch, "E1288", {"start": v(-28.62, -42.54) * mm, "end": v(-28.84, -42.9) * mm});
            skLineSegment(sketch, "E1289", {"start": v(-28.84, -42.9) * mm, "end": v(-29.06, -43.26) * mm});
            skLineSegment(sketch, "E1290", {"start": v(-29.06, -43.26) * mm, "end": v(-29.3, -43.64) * mm});
            skLineSegment(sketch, "E1291", {"start": v(-29.3, -43.64) * mm, "end": v(-29.52, -44) * mm});
            skLineSegment(sketch, "E1292", {"start": v(-29.52, -44) * mm, "end": v(-29.74, -44.36) * mm});
            skLineSegment(sketch, "E1293", {"start": v(-29.74, -44.36) * mm, "end": v(-29.98, -44.74) * mm});
            skLineSegment(sketch, "E1294", {"start": v(-29.98, -44.74) * mm, "end": v(-30.22, -45.13) * mm});
            skLineSegment(sketch, "E1295", {"start": v(-30.22, -45.13) * mm, "end": v(-30.37, -45.55) * mm});
            skLineSegment(sketch, "E1296", {"start": v(-30.37, -45.55) * mm, "end": v(-30.41, -46) * mm});
            skLineSegment(sketch, "E1297", {"start": v(-30.41, -46) * mm, "end": v(-30.34, -46.44) * mm});
            skLineSegment(sketch, "E1298", {"start": v(-30.34, -46.44) * mm, "end": v(-30.15, -46.85) * mm});
            skLineSegment(sketch, "E1299", {"start": v(-30.15, -46.85) * mm, "end": v(-29.86, -47.19) * mm});
            skLineSegment(sketch, "E1300", {"start": v(-29.86, -47.19) * mm, "end": v(-29.49, -47.44) * mm});
            skLineSegment(sketch, "E1301", {"start": v(-29.49, -47.44) * mm, "end": v(-29.06, -47.6) * mm});
            skLineSegment(sketch, "E1302", {"start": v(-29.06, -47.6) * mm, "end": v(-28.62, -47.63) * mm});
            skLineSegment(sketch, "E1303", {"start": v(-28.62, -47.63) * mm, "end": v(-28.18, -47.54) * mm});
            skLineSegment(sketch, "E1304", {"start": v(-28.18, -47.54) * mm, "end": v(-27.77, -47.34) * mm});
            skLineSegment(sketch, "E1305", {"start": v(-27.77, -47.34) * mm, "end": v(-27.44, -47.05) * mm});
            skLineSegment(sketch, "E1306", {"start": v(-27.44, -47.05) * mm, "end": v(-27.2, -46.7) * mm});
            skLineSegment(sketch, "E1307", {"start": v(-27.2, -46.7) * mm, "end": v(-27, -46.33) * mm});
            skLineSegment(sketch, "E1308", {"start": v(-27, -46.33) * mm, "end": v(-26.8, -45.94) * mm});
            skLineSegment(sketch, "E1309", {"start": v(-26.8, -45.94) * mm, "end": v(-26.6, -45.57) * mm});
            skLineSegment(sketch, "E1310", {"start": v(-26.6, -45.57) * mm, "end": v(-26.4, -45.2) * mm});
            skLineSegment(sketch, "E1311", {"start": v(-26.4, -45.2) * mm, "end": v(-26.18, -44.8) * mm});
            skLineSegment(sketch, "E1312", {"start": v(-26.18, -44.8) * mm, "end": v(-25.98, -44.43) * mm});
            skLineSegment(sketch, "E1313", {"start": v(-25.98, -44.43) * mm, "end": v(-25.78, -44.06) * mm});
            skLineSegment(sketch, "E1314", {"start": v(-25.78, -44.06) * mm, "end": v(-25.57, -43.66) * mm});
            skLineSegment(sketch, "E1315", {"start": v(-25.57, -43.66) * mm, "end": v(-25.37, -43.29) * mm});
            skLineSegment(sketch, "E1316", {"start": v(-25.37, -43.29) * mm, "end": v(-25.17, -42.92) * mm});
            skLineSegment(sketch, "E1317", {"start": v(-25.17, -42.92) * mm, "end": v(-24.96, -42.52) * mm});
            skLineSegment(sketch, "E1318", {"start": v(-24.96, -42.52) * mm, "end": v(-24.76, -42.15) * mm});
            skLineSegment(sketch, "E1319", {"start": v(-24.76, -42.15) * mm, "end": v(-24.61, -41.87) * mm});
            skLineSegment(sketch, "E1320", {"start": v(-24.61, -41.87) * mm, "end": v(-24.23, -42.05) * mm});
            skLineSegment(sketch, "E1321", {"start": v(-24.23, -42.05) * mm, "end": v(-23.85, -42.23) * mm});
            skLineSegment(sketch, "E1322", {"start": v(-23.85, -42.23) * mm, "end": v(-23.47, -42.41) * mm});
            skLineSegment(sketch, "E1323", {"start": v(-23.47, -42.41) * mm, "end": v(-23.1, -42.6) * mm});
            skLineSegment(sketch, "E1324", {"start": v(-23.1, -42.6) * mm, "end": v(-22.7, -42.77) * mm});
            skLineSegment(sketch, "E1325", {"start": v(-22.7, -42.77) * mm, "end": v(-22.33, -42.95) * mm});
            skLineSegment(sketch, "E1326", {"start": v(-22.33, -42.95) * mm, "end": v(-21.95, -43.14) * mm});
            skLineSegment(sketch, "E1327", {"start": v(-21.95, -43.14) * mm, "end": v(-21.57, -43.32) * mm});
            skLineSegment(sketch, "E1328", {"start": v(-21.57, -43.32) * mm, "end": v(-21.19, -43.5) * mm});
            skLineSegment(sketch, "E1329", {"start": v(-21.19, -43.5) * mm, "end": v(-20.8, -43.68) * mm});
            skLineSegment(sketch, "E1330", {"start": v(-20.8, -43.68) * mm, "end": v(-20.45, -43.84) * mm});
            skLineSegment(sketch, "E1331", {"start": v(-20.45, -43.84) * mm, "end": v(-20.62, -44.23) * mm});
            skLineSegment(sketch, "E1332", {"start": v(-20.62, -44.23) * mm, "end": v(-20.78, -44.62) * mm});
            skLineSegment(sketch, "E1333", {"start": v(-20.78, -44.62) * mm, "end": v(-20.95, -45.04) * mm});
            skLineSegment(sketch, "E1334", {"start": v(-20.95, -45.04) * mm, "end": v(-21.11, -45.43) * mm});
            skLineSegment(sketch, "E1335", {"start": v(-21.11, -45.43) * mm, "end": v(-21.28, -45.82) * mm});
            skLineSegment(sketch, "E1336", {"start": v(-21.28, -45.82) * mm, "end": v(-21.45, -46.23) * mm});
            skLineSegment(sketch, "E1337", {"start": v(-21.45, -46.23) * mm, "end": v(-21.61, -46.62) * mm});
            skLineSegment(sketch, "E1338", {"start": v(-21.61, -46.62) * mm, "end": v(-21.77, -47) * mm});
            skLineSegment(sketch, "E1339", {"start": v(-21.77, -47) * mm, "end": v(-21.95, -47.42) * mm});
            skLineSegment(sketch, "E1340", {"start": v(-21.95, -47.42) * mm, "end": v(-22.1, -47.81) * mm});
            skLineSegment(sketch, "E1341", {"start": v(-22.1, -47.81) * mm, "end": v(-22.27, -48.2) * mm});
            skLineSegment(sketch, "E1342", {"start": v(-22.27, -48.2) * mm, "end": v(-22.44, -48.62) * mm});
            skLineSegment(sketch, "E1343", {"start": v(-22.44, -48.62) * mm, "end": v(-22.62, -49.04) * mm});
            skLineSegment(sketch, "E1344", {"start": v(-22.62, -49.04) * mm, "end": v(-22.7, -49.48) * mm});
            skLineSegment(sketch, "E1345", {"start": v(-22.7, -49.48) * mm, "end": v(-22.67, -49.93) * mm});
            skLineSegment(sketch, "E1346", {"start": v(-22.67, -49.93) * mm, "end": v(-22.52, -50.35) * mm});
            skLineSegment(sketch, "E1347", {"start": v(-22.52, -50.35) * mm, "end": v(-22.27, -50.72) * mm});
            skLineSegment(sketch, "E1348", {"start": v(-22.27, -50.72) * mm, "end": v(-21.93, -51.01) * mm});
            skLineSegment(sketch, "E1349", {"start": v(-21.93, -51.01) * mm, "end": v(-21.52, -51.2) * mm});
            skLineSegment(sketch, "E1350", {"start": v(-21.52, -51.2) * mm, "end": v(-21.08, -51.29) * mm});
            skLineSegment(sketch, "E1351", {"start": v(-21.08, -51.29) * mm, "end": v(-20.63, -51.25) * mm});
            skLineSegment(sketch, "E1352", {"start": v(-20.63, -51.25) * mm, "end": v(-20.21, -51.1) * mm});
            skLineSegment(sketch, "E1353", {"start": v(-20.21, -51.1) * mm, "end": v(-19.85, -50.83) * mm});
            skLineSegment(sketch, "E1354", {"start": v(-19.85, -50.83) * mm, "end": v(-19.56, -50.49) * mm});
            skLineSegment(sketch, "E1355", {"start": v(-19.56, -50.49) * mm, "end": v(-19.4, -50.1) * mm});
            skLineSegment(sketch, "E1356", {"start": v(-19.4, -50.1) * mm, "end": v(-19.25, -49.7) * mm});
            skLineSegment(sketch, "E1357", {"start": v(-19.25, -49.7) * mm, "end": v(-19.1, -49.3) * mm});
            skLineSegment(sketch, "E1358", {"start": v(-19.1, -49.3) * mm, "end": v(-18.97, -48.9) * mm});
            skLineSegment(sketch, "E1359", {"start": v(-18.97, -48.9) * mm, "end": v(-18.83, -48.5) * mm});
            skLineSegment(sketch, "E1360", {"start": v(-18.83, -48.5) * mm, "end": v(-18.69, -48.07) * mm});
            skLineSegment(sketch, "E1361", {"start": v(-18.69, -48.07) * mm, "end": v(-18.55, -47.67) * mm});
            skLineSegment(sketch, "E1362", {"start": v(-18.55, -47.67) * mm, "end": v(-18.41, -47.27) * mm});
            skLineSegment(sketch, "E1363", {"start": v(-18.41, -47.27) * mm, "end": v(-18.27, -46.85) * mm});
            skLineSegment(sketch, "E1364", {"start": v(-18.27, -46.85) * mm, "end": v(-18.13, -46.45) * mm});
            skLineSegment(sketch, "E1365", {"start": v(-18.13, -46.45) * mm, "end": v(-18, -46.05) * mm});
            skLineSegment(sketch, "E1366", {"start": v(-18, -46.05) * mm, "end": v(-17.85, -45.62) * mm});
            skLineSegment(sketch, "E1367", {"start": v(-17.85, -45.62) * mm, "end": v(-17.71, -45.22) * mm});
            skLineSegment(sketch, "E1368", {"start": v(-17.71, -45.22) * mm, "end": v(-17.6, -44.92) * mm});
            skLineSegment(sketch, "E1369", {"start": v(-17.6, -44.92) * mm, "end": v(-17.2, -45.04) * mm});
            skLineSegment(sketch, "E1370", {"start": v(-17.2, -45.04) * mm, "end": v(-16.8, -45.16) * mm});
            skLineSegment(sketch, "E1371", {"start": v(-16.8, -45.16) * mm, "end": v(-16.4, -45.28) * mm});
            skLineSegment(sketch, "E1372", {"start": v(-16.4, -45.28) * mm, "end": v(-15.99, -45.4) * mm});
            skLineSegment(sketch, "E1373", {"start": v(-15.99, -45.4) * mm, "end": v(-15.58, -45.51) * mm});
            skLineSegment(sketch, "E1374", {"start": v(-15.58, -45.51) * mm, "end": v(-15.18, -45.63) * mm});
            skLineSegment(sketch, "E1375", {"start": v(-15.18, -45.63) * mm, "end": v(-14.77, -45.75) * mm});
            skLineSegment(sketch, "E1376", {"start": v(-14.77, -45.75) * mm, "end": v(-14.37, -45.86) * mm});
            skLineSegment(sketch, "E1377", {"start": v(-14.37, -45.86) * mm, "end": v(-13.96, -45.98) * mm});
            skLineSegment(sketch, "E1378", {"start": v(-13.96, -45.98) * mm, "end": v(-13.56, -46.1) * mm});
            skLineSegment(sketch, "E1379", {"start": v(-13.56, -46.1) * mm, "end": v(-13.19, -46.2) * mm});
            skLineSegment(sketch, "E1380", {"start": v(-13.19, -46.2) * mm, "end": v(-13.28, -46.62) * mm});
            skLineSegment(sketch, "E1381", {"start": v(-13.28, -46.62) * mm, "end": v(-13.38, -47.03) * mm});
            skLineSegment(sketch, "E1382", {"start": v(-13.38, -47.03) * mm, "end": v(-13.48, -47.46) * mm});
            skLineSegment(sketch, "E1383", {"start": v(-13.48, -47.46) * mm, "end": v(-13.58, -47.87) * mm});
            skLineSegment(sketch, "E1384", {"start": v(-13.58, -47.87) * mm, "end": v(-13.68, -48.28) * mm});
            skLineSegment(sketch, "E1385", {"start": v(-13.68, -48.28) * mm, "end": v(-13.78, -48.72) * mm});
            skLineSegment(sketch, "E1386", {"start": v(-13.78, -48.72) * mm, "end": v(-13.88, -49.13) * mm});
            skLineSegment(sketch, "E1387", {"start": v(-13.88, -49.13) * mm, "end": v(-13.98, -49.54) * mm});
            skLineSegment(sketch, "E1388", {"start": v(-13.98, -49.54) * mm, "end": v(-14.08, -49.98) * mm});
            skLineSegment(sketch, "E1389", {"start": v(-14.08, -49.98) * mm, "end": v(-14.18, -50.39) * mm});
            skLineSegment(sketch, "E1390", {"start": v(-14.18, -50.39) * mm, "end": v(-14.28, -50.8) * mm});
            skLineSegment(sketch, "E1391", {"start": v(-14.28, -50.8) * mm, "end": v(-14.38, -51.24) * mm});
            skLineSegment(sketch, "E1392", {"start": v(-14.38, -51.24) * mm, "end": v(-14.48, -51.68) * mm});
            skLineSegment(sketch, "E1393", {"start": v(-14.48, -51.68) * mm, "end": v(-14.5, -52.13) * mm});
            skLineSegment(sketch, "E1394", {"start": v(-14.5, -52.13) * mm, "end": v(-14.4, -52.57) * mm});
            skLineSegment(sketch, "E1395", {"start": v(-14.4, -52.57) * mm, "end": v(-14.18, -52.96) * mm});
            skLineSegment(sketch, "E1396", {"start": v(-14.18, -52.96) * mm, "end": v(-13.87, -53.29) * mm});
            skLineSegment(sketch, "E1397", {"start": v(-13.87, -53.29) * mm, "end": v(-13.49, -53.52) * mm});
            skLineSegment(sketch, "E1398", {"start": v(-13.49, -53.52) * mm, "end": v(-13.06, -53.64) * mm});
            skLineSegment(sketch, "E1399", {"start": v(-13.06, -53.64) * mm, "end": v(-12.6, -53.65) * mm});
            skLineSegment(sketch, "E1400", {"start": v(-12.6, -53.65) * mm, "end": v(-12.17, -53.54) * mm});
            skLineSegment(sketch, "E1401", {"start": v(-12.17, -53.54) * mm, "end": v(-11.78, -53.32) * mm});
            skLineSegment(sketch, "E1402", {"start": v(-11.78, -53.32) * mm, "end": v(-11.46, -53) * mm});
            skLineSegment(sketch, "E1403", {"start": v(-11.46, -53) * mm, "end": v(-11.24, -52.62) * mm});
            skLineSegment(sketch, "E1404", {"start": v(-11.24, -52.62) * mm, "end": v(-11.13, -52.21) * mm});
            skLineSegment(sketch, "E1405", {"start": v(-11.13, -52.21) * mm, "end": v(-11.05, -51.8) * mm});
            skLineSegment(sketch, "E1406", {"start": v(-11.05, -51.8) * mm, "end": v(-10.98, -51.36) * mm});
            skLineSegment(sketch, "E1407", {"start": v(-10.98, -51.36) * mm, "end": v(-10.9, -50.95) * mm});
            skLineSegment(sketch, "E1408", {"start": v(-10.9, -50.95) * mm, "end": v(-10.84, -50.53) * mm});
            skLineSegment(sketch, "E1409", {"start": v(-10.84, -50.53) * mm, "end": v(-10.76, -50.1) * mm});
            skLineSegment(sketch, "E1410", {"start": v(-10.76, -50.1) * mm, "end": v(-10.7, -49.67) * mm});
            skLineSegment(sketch, "E1411", {"start": v(-10.7, -49.67) * mm, "end": v(-10.62, -49.26) * mm});
            skLineSegment(sketch, "E1412", {"start": v(-10.62, -49.26) * mm, "end": v(-10.54, -48.82) * mm});
            skLineSegment(sketch, "E1413", {"start": v(-10.54, -48.82) * mm, "end": v(-10.47, -48.4) * mm});
            skLineSegment(sketch, "E1414", {"start": v(-10.47, -48.4) * mm, "end": v(-10.4, -47.99) * mm});
            skLineSegment(sketch, "E1415", {"start": v(-10.4, -47.99) * mm, "end": v(-10.33, -47.54) * mm});
            skLineSegment(sketch, "E1416", {"start": v(-10.33, -47.54) * mm, "end": v(-10.25, -47.13) * mm});
            skLineSegment(sketch, "E1417", {"start": v(-10.25, -47.13) * mm, "end": v(-10.2, -46.81) * mm});
            skLineSegment(sketch, "E1418", {"start": v(-10.2, -46.81) * mm, "end": v(-9.78, -46.86) * mm});
            skLineSegment(sketch, "E1419", {"start": v(-9.78, -46.86) * mm, "end": v(-9.36, -46.92) * mm});
            skLineSegment(sketch, "E1420", {"start": v(-9.36, -46.92) * mm, "end": v(-8.95, -46.97) * mm});
            skLineSegment(sketch, "E1421", {"start": v(-8.95, -46.97) * mm, "end": v(-8.53, -47.02) * mm});
            skLineSegment(sketch, "E1422", {"start": v(-8.53, -47.02) * mm, "end": v(-8.1, -47.07) * mm});
            skLineSegment(sketch, "E1423", {"start": v(-8.1, -47.07) * mm, "end": v(-7.7, -47.12) * mm});
            skLineSegment(sketch, "E1424", {"start": v(-7.7, -47.12) * mm, "end": v(-7.27, -47.17) * mm});
            skLineSegment(sketch, "E1425", {"start": v(-7.27, -47.17) * mm, "end": v(-6.85, -47.22) * mm});
            skLineSegment(sketch, "E1426", {"start": v(-6.85, -47.22) * mm, "end": v(-6.43, -47.27) * mm});
            skLineSegment(sketch, "E1427", {"start": v(-6.43, -47.27) * mm, "end": v(-6.02, -47.32) * mm});
            skLineSegment(sketch, "E1428", {"start": v(-6.02, -47.32) * mm, "end": v(-5.63, -47.37) * mm});
            skLineSegment(sketch, "E1429", {"start": v(-5.63, -47.37) * mm, "end": v(-5.66, -47.79) * mm});
            skLineSegment(sketch, "E1430", {"start": v(-5.66, -47.79) * mm, "end": v(-5.7, -48.2) * mm});
            skLineSegment(sketch, "E1431", {"start": v(-5.7, -48.2) * mm, "end": v(-5.72, -48.66) * mm});
            skLineSegment(sketch, "E1432", {"start": v(-5.72, -48.66) * mm, "end": v(-5.76, -49.08) * mm});
            skLineSegment(sketch, "E1433", {"start": v(-5.76, -49.08) * mm, "end": v(-5.79, -49.5) * mm});
            skLineSegment(sketch, "E1434", {"start": v(-5.79, -49.5) * mm, "end": v(-5.82, -49.95) * mm});
            skLineSegment(sketch, "E1435", {"start": v(-5.82, -49.95) * mm, "end": v(-5.85, -50.37) * mm});
            skLineSegment(sketch, "E1436", {"start": v(-5.85, -50.37) * mm, "end": v(-5.88, -50.79) * mm});
            skLineSegment(sketch, "E1437", {"start": v(-5.88, -50.79) * mm, "end": v(-5.91, -51.24) * mm});
            skLineSegment(sketch, "E1438", {"start": v(-5.91, -51.24) * mm, "end": v(-5.94, -51.66) * mm});
            skLineSegment(sketch, "E1439", {"start": v(-5.94, -51.66) * mm, "end": v(-5.97, -52.08) * mm});
            skLineSegment(sketch, "E1440", {"start": v(-5.97, -52.08) * mm, "end": v(-6, -52.53) * mm});
            skLineSegment(sketch, "E1441", {"start": v(-6, -52.53) * mm, "end": v(-6.03, -52.98) * mm});
            skLineSegment(sketch, "E1442", {"start": v(-6.03, -52.98) * mm, "end": v(-5.98, -53.43) * mm});
            skLineSegment(sketch, "E1443", {"start": v(-5.98, -53.43) * mm, "end": v(-5.8, -53.84) * mm});
            skLineSegment(sketch, "E1444", {"start": v(-5.8, -53.84) * mm, "end": v(-5.53, -54.2) * mm});
            skLineSegment(sketch, "E1445", {"start": v(-5.53, -54.2) * mm, "end": v(-5.17, -54.47) * mm});
            skLineSegment(sketch, "E1446", {"start": v(-5.17, -54.47) * mm, "end": v(-4.76, -54.64) * mm});
            skLineSegment(sketch, "E1447", {"start": v(-4.76, -54.64) * mm, "end": v(-4.31, -54.69) * mm});
            skLineSegment(sketch, "E1448", {"start": v(-4.31, -54.69) * mm, "end": v(-3.87, -54.63) * mm});
            skLineSegment(sketch, "E1449", {"start": v(-3.87, -54.63) * mm, "end": v(-3.46, -54.45) * mm});
            skLineSegment(sketch, "E1450", {"start": v(-3.46, -54.45) * mm, "end": v(-3.1, -54.17) * mm});
            skLineSegment(sketch, "E1451", {"start": v(-3.1, -54.17) * mm, "end": v(-2.84, -53.8) * mm});
            skLineSegment(sketch, "E1452", {"start": v(-2.84, -53.8) * mm, "end": v(-2.68, -53.39) * mm});
            skLineSegment(sketch, "E1453", {"start": v(-2.68, -53.39) * mm, "end": v(-2.64, -52.97) * mm});
            skLineSegment(sketch, "E1454", {"start": v(-2.64, -52.97) * mm, "end": v(-2.63, -52.55) * mm});
            skLineSegment(sketch, "E1455", {"start": v(-2.63, -52.55) * mm, "end": v(-2.63, -52.1) * mm});
            skLineSegment(sketch, "E1456", {"start": v(-2.63, -52.1) * mm, "end": v(-2.62, -51.69) * mm});
            skLineSegment(sketch, "E1457", {"start": v(-2.62, -51.69) * mm, "end": v(-2.62, -51.26) * mm});
            skLineSegment(sketch, "E1458", {"start": v(-2.62, -51.26) * mm, "end": v(-2.62, -50.82) * mm});
            skLineSegment(sketch, "E1459", {"start": v(-2.62, -50.82) * mm, "end": v(-2.61, -50.4) * mm});
            skLineSegment(sketch, "E1460", {"start": v(-2.61, -50.4) * mm, "end": v(-2.6, -49.97) * mm});
            skLineSegment(sketch, "E1461", {"start": v(-2.6, -49.97) * mm, "end": v(-2.6, -49.52) * mm});
            skLineSegment(sketch, "E1462", {"start": v(-2.6, -49.52) * mm, "end": v(-2.6, -49.1) * mm});
            skLineSegment(sketch, "E1463", {"start": v(-2.6, -49.1) * mm, "end": v(-2.6, -48.68) * mm});
            skLineSegment(sketch, "E1464", {"start": v(-2.6, -48.68) * mm, "end": v(-2.6, -48.23) * mm});
            skLineSegment(sketch, "E1465", {"start": v(-2.6, -48.23) * mm, "end": v(-2.6, -47.8) * mm});
            skLineSegment(sketch, "E1466", {"start": v(-2.6, -47.8) * mm, "end": v(-2.59, -47.5) * mm});
            skLineSegment(sketch, "E1467", {"start": v(-2.59, -47.5) * mm, "end": v(-2.17, -47.47) * mm});
            skLineSegment(sketch, "E1468", {"start": v(-2.17, -47.47) * mm, "end": v(-1.75, -47.46) * mm});
            skLineSegment(sketch, "E1469", {"start": v(-1.75, -47.46) * mm, "end": v(-1.32, -47.44) * mm});
            skLineSegment(sketch, "E1470", {"start": v(-1.32, -47.44) * mm, "end": v(-0.9, -47.42) * mm});
            skLineSegment(sketch, "E1471", {"start": v(-0.9, -47.42) * mm, "end": v(-0.48, -47.4) * mm});
            skLineSegment(sketch, "E1472", {"start": v(-0.48, -47.4) * mm, "end": v(-0.06, -47.39) * mm});
            skLineSegment(sketch, "E1473", {"start": v(-0.06, -47.39) * mm, "end": v(0.36, -47.37) * mm});
            skLineSegment(sketch, "E1474", {"start": v(0.36, -47.37) * mm, "end": v(0.78, -47.36) * mm});
            skLineSegment(sketch, "E1475", {"start": v(0.78, -47.36) * mm, "end": v(1.2, -47.34) * mm});
            skLineSegment(sketch, "E1476", {"start": v(1.2, -47.34) * mm, "end": v(1.62, -47.32) * mm});
            skLineSegment(sketch, "E1477", {"start": v(1.62, -47.32) * mm, "end": v(2.01, -47.3) * mm});
            skLineSegment(sketch, "E1478", {"start": v(2.01, -47.3) * mm, "end": v(2.05, -47.73) * mm});
            skLineSegment(sketch, "E1479", {"start": v(2.05, -47.73) * mm, "end": v(2.09, -48.15) * mm});
            skLineSegment(sketch, "E1480", {"start": v(2.09, -48.15) * mm, "end": v(2.13, -48.6) * mm});
            skLineSegment(sketch, "E1481", {"start": v(2.13, -48.6) * mm, "end": v(2.16, -49.01) * mm});
            skLineSegment(sketch, "E1482", {"start": v(2.16, -49.01) * mm, "end": v(2.2, -49.43) * mm});
            skLineSegment(sketch, "E1483", {"start": v(2.2, -49.43) * mm, "end": v(2.24, -49.88) * mm});
            skLineSegment(sketch, "E1484", {"start": v(2.24, -49.88) * mm, "end": v(2.28, -50.3) * mm});
            skLineSegment(sketch, "E1485", {"start": v(2.28, -50.3) * mm, "end": v(2.32, -50.72) * mm});
            skLineSegment(sketch, "E1486", {"start": v(2.32, -50.72) * mm, "end": v(2.36, -51.17) * mm});
            skLineSegment(sketch, "E1487", {"start": v(2.36, -51.17) * mm, "end": v(2.4, -51.59) * mm});
            skLineSegment(sketch, "E1488", {"start": v(2.4, -51.59) * mm, "end": v(2.43, -52) * mm});
            skLineSegment(sketch, "E1489", {"start": v(2.43, -52) * mm, "end": v(2.47, -52.46) * mm});
            skLineSegment(sketch, "E1490", {"start": v(2.47, -52.46) * mm, "end": v(2.51, -52.91) * mm});
            skLineSegment(sketch, "E1491", {"start": v(2.51, -52.91) * mm, "end": v(2.64, -53.34) * mm});
            skLineSegment(sketch, "E1492", {"start": v(2.64, -53.34) * mm, "end": v(2.88, -53.72) * mm});
            skLineSegment(sketch, "E1493", {"start": v(2.88, -53.72) * mm, "end": v(3.2, -54.03) * mm});
            skLineSegment(sketch, "E1494", {"start": v(3.2, -54.03) * mm, "end": v(3.6, -54.24) * mm});
            skLineSegment(sketch, "E1495", {"start": v(3.6, -54.24) * mm, "end": v(4.04, -54.34) * mm});
            skLineSegment(sketch, "E1496", {"start": v(4.04, -54.34) * mm, "end": v(4.49, -54.32) * mm});
            skLineSegment(sketch, "E1497", {"start": v(4.49, -54.32) * mm, "end": v(4.92, -54.19) * mm});
            skLineSegment(sketch, "E1498", {"start": v(4.92, -54.19) * mm, "end": v(5.3, -53.94) * mm});
            skLineSegment(sketch, "E1499", {"start": v(5.3, -53.94) * mm, "end": v(5.6, -53.61) * mm});
            skLineSegment(sketch, "E1500", {"start": v(5.6, -53.61) * mm, "end": v(5.8, -53.21) * mm});
            skLineSegment(sketch, "E1501", {"start": v(5.8, -53.21) * mm, "end": v(5.89, -52.77) * mm});
            skLineSegment(sketch, "E1502", {"start": v(5.89, -52.77) * mm, "end": v(5.86, -52.35) * mm});
            skLineSegment(sketch, "E1503", {"start": v(5.86, -52.35) * mm, "end": v(5.8, -51.93) * mm});
            skLineSegment(sketch, "E1504", {"start": v(5.8, -51.93) * mm, "end": v(5.74, -51.5) * mm});
            skLineSegment(sketch, "E1505", {"start": v(5.74, -51.5) * mm, "end": v(5.67, -51.09) * mm});
            skLineSegment(sketch, "E1506", {"start": v(5.67, -51.09) * mm, "end": v(5.6, -50.67) * mm});
            skLineSegment(sketch, "E1507", {"start": v(5.6, -50.67) * mm, "end": v(5.54, -50.22) * mm});
            skLineSegment(sketch, "E1508", {"start": v(5.54, -50.22) * mm, "end": v(5.48, -49.8) * mm});
            skLineSegment(sketch, "E1509", {"start": v(5.48, -49.8) * mm, "end": v(5.41, -49.4) * mm});
            skLineSegment(sketch, "E1510", {"start": v(5.41, -49.4) * mm, "end": v(5.34, -48.95) * mm});
            skLineSegment(sketch, "E1511", {"start": v(5.34, -48.95) * mm, "end": v(5.28, -48.53) * mm});
            skLineSegment(sketch, "E1512", {"start": v(5.28, -48.53) * mm, "end": v(5.22, -48.11) * mm});
            skLineSegment(sketch, "E1513", {"start": v(5.22, -48.11) * mm, "end": v(5.15, -47.67) * mm});
            skLineSegment(sketch, "E1514", {"start": v(5.15, -47.67) * mm, "end": v(5.08, -47.25) * mm});
            skLineSegment(sketch, "E1515", {"start": v(5.08, -47.25) * mm, "end": v(5.03, -46.94) * mm});
            skLineSegment(sketch, "E1516", {"start": v(5.03, -46.94) * mm, "end": v(5.45, -46.85) * mm});
            skLineSegment(sketch, "E1517", {"start": v(5.45, -46.85) * mm, "end": v(5.86, -46.77) * mm});
            skLineSegment(sketch, "E1518", {"start": v(5.86, -46.77) * mm, "end": v(6.27, -46.69) * mm});
            skLineSegment(sketch, "E1519", {"start": v(6.27, -46.69) * mm, "end": v(6.69, -46.6) * mm});
            skLineSegment(sketch, "E1520", {"start": v(6.69, -46.6) * mm, "end": v(7.1, -46.52) * mm});
            skLineSegment(sketch, "E1521", {"start": v(7.1, -46.52) * mm, "end": v(7.51, -46.43) * mm});
            skLineSegment(sketch, "E1522", {"start": v(7.51, -46.43) * mm, "end": v(7.93, -46.35) * mm});
            skLineSegment(sketch, "E1523", {"start": v(7.93, -46.35) * mm, "end": v(8.34, -46.26) * mm});
            skLineSegment(sketch, "E1524", {"start": v(8.34, -46.26) * mm, "end": v(8.75, -46.18) * mm});
            skLineSegment(sketch, "E1525", {"start": v(8.75, -46.18) * mm, "end": v(9.17, -46.1) * mm});
            skLineSegment(sketch, "E1526", {"start": v(9.17, -46.1) * mm, "end": v(9.55, -46.02) * mm});
            skLineSegment(sketch, "E1527", {"start": v(9.55, -46.02) * mm, "end": v(9.65, -46.43) * mm});
            skLineSegment(sketch, "E1528", {"start": v(9.65, -46.43) * mm, "end": v(9.75, -46.84) * mm});
            skLineSegment(sketch, "E1529", {"start": v(9.75, -46.84) * mm, "end": v(9.87, -47.27) * mm});
            skLineSegment(sketch, "E1530", {"start": v(9.87, -47.27) * mm, "end": v(9.97, -47.68) * mm});
            skLineSegment(sketch, "E1531", {"start": v(9.97, -47.68) * mm, "end": v(10.07, -48.09) * mm});
            skLineSegment(sketch, "E1532", {"start": v(10.07, -48.09) * mm, "end": v(10.18, -48.52) * mm});
            skLineSegment(sketch, "E1533", {"start": v(10.18, -48.52) * mm, "end": v(10.29, -48.93) * mm});
            skLineSegment(sketch, "E1534", {"start": v(10.29, -48.93) * mm, "end": v(10.4, -49.34) * mm});
            skLineSegment(sketch, "E1535", {"start": v(10.4, -49.34) * mm, "end": v(10.5, -49.78) * mm});
            skLineSegment(sketch, "E1536", {"start": v(10.5, -49.78) * mm, "end": v(10.6, -50.18) * mm});
            skLineSegment(sketch, "E1537", {"start": v(10.6, -50.18) * mm, "end": v(10.71, -50.6) * mm});
            skLineSegment(sketch, "E1538", {"start": v(10.71, -50.6) * mm, "end": v(10.82, -51.03) * mm});
            skLineSegment(sketch, "E1539", {"start": v(10.82, -51.03) * mm, "end": v(10.94, -51.47) * mm});
            skLineSegment(sketch, "E1540", {"start": v(10.94, -51.47) * mm, "end": v(11.14, -51.88) * mm});
            skLineSegment(sketch, "E1541", {"start": v(11.14, -51.88) * mm, "end": v(11.43, -52.21) * mm});
            skLineSegment(sketch, "E1542", {"start": v(11.43, -52.21) * mm, "end": v(11.8, -52.46) * mm});
            skLineSegment(sketch, "E1543", {"start": v(11.8, -52.46) * mm, "end": v(12.23, -52.6) * mm});
            skLineSegment(sketch, "E1544", {"start": v(12.23, -52.6) * mm, "end": v(12.68, -52.63) * mm});
            skLineSegment(sketch, "E1545", {"start": v(12.68, -52.63) * mm, "end": v(13.11, -52.54) * mm});
            skLineSegment(sketch, "E1546", {"start": v(13.11, -52.54) * mm, "end": v(13.52, -52.34) * mm});
            skLineSegment(sketch, "E1547", {"start": v(13.52, -52.34) * mm, "end": v(13.85, -52.04) * mm});
            skLineSegment(sketch, "E1548", {"start": v(13.85, -52.04) * mm, "end": v(14.1, -51.67) * mm});
            skLineSegment(sketch, "E1549", {"start": v(14.1, -51.67) * mm, "end": v(14.23, -51.24) * mm});
            skLineSegment(sketch, "E1550", {"start": v(14.23, -51.24) * mm, "end": v(14.25, -50.8) * mm});
            skLineSegment(sketch, "E1551", {"start": v(14.25, -50.8) * mm, "end": v(14.15, -50.38) * mm});
            skLineSegment(sketch, "E1552", {"start": v(14.15, -50.38) * mm, "end": v(14.03, -49.98) * mm});
            skLineSegment(sketch, "E1553", {"start": v(14.03, -49.98) * mm, "end": v(13.9, -49.56) * mm});
            skLineSegment(sketch, "E1554", {"start": v(13.9, -49.56) * mm, "end": v(13.77, -49.16) * mm});
            skLineSegment(sketch, "E1555", {"start": v(13.77, -49.16) * mm, "end": v(13.64, -48.76) * mm});
            skLineSegment(sketch, "E1556", {"start": v(13.64, -48.76) * mm, "end": v(13.5, -48.33) * mm});
            skLineSegment(sketch, "E1557", {"start": v(13.5, -48.33) * mm, "end": v(13.37, -47.93) * mm});
            skLineSegment(sketch, "E1558", {"start": v(13.37, -47.93) * mm, "end": v(13.24, -47.53) * mm});
            skLineSegment(sketch, "E1559", {"start": v(13.24, -47.53) * mm, "end": v(13.1, -47.1) * mm});
            skLineSegment(sketch, "E1560", {"start": v(13.1, -47.1) * mm, "end": v(12.97, -46.7) * mm});
            skLineSegment(sketch, "E1561", {"start": v(12.97, -46.7) * mm, "end": v(12.84, -46.3) * mm});
            skLineSegment(sketch, "E1562", {"start": v(12.84, -46.3) * mm, "end": v(12.7, -45.87) * mm});
            skLineSegment(sketch, "E1563", {"start": v(12.7, -45.87) * mm, "end": v(12.57, -45.47) * mm});
            skLineSegment(sketch, "E1564", {"start": v(12.57, -45.47) * mm, "end": v(12.47, -45.17) * mm});
            skLineSegment(sketch, "E1565", {"start": v(12.47, -45.17) * mm, "end": v(12.87, -45.02) * mm});
            skLineSegment(sketch, "E1566", {"start": v(12.87, -45.02) * mm, "end": v(13.26, -44.87) * mm});
            skLineSegment(sketch, "E1567", {"start": v(13.26, -44.87) * mm, "end": v(13.65, -44.72) * mm});
            skLineSegment(sketch, "E1568", {"start": v(13.65, -44.72) * mm, "end": v(14.05, -44.57) * mm});
            skLineSegment(sketch, "E1569", {"start": v(14.05, -44.57) * mm, "end": v(14.44, -44.42) * mm});
            skLineSegment(sketch, "E1570", {"start": v(14.44, -44.42) * mm, "end": v(14.84, -44.27) * mm});
            skLineSegment(sketch, "E1571", {"start": v(14.84, -44.27) * mm, "end": v(15.23, -44.12) * mm});
            skLineSegment(sketch, "E1572", {"start": v(15.23, -44.12) * mm, "end": v(15.62, -43.98) * mm});
            skLineSegment(sketch, "E1573", {"start": v(15.62, -43.98) * mm, "end": v(16.02, -43.83) * mm});
            skLineSegment(sketch, "E1574", {"start": v(16.02, -43.83) * mm, "end": v(16.41, -43.68) * mm});
            skLineSegment(sketch, "E1575", {"start": v(16.41, -43.68) * mm, "end": v(16.78, -43.54) * mm});
            skLineSegment(sketch, "E1576", {"start": v(16.78, -43.54) * mm, "end": v(16.94, -43.92) * mm});
            skLineSegment(sketch, "E1577", {"start": v(16.94, -43.92) * mm, "end": v(17.11, -44.31) * mm});
            skLineSegment(sketch, "E1578", {"start": v(17.11, -44.31) * mm, "end": v(17.3, -44.72) * mm});
            skLineSegment(sketch, "E1579", {"start": v(17.3, -44.72) * mm, "end": v(17.46, -45.1) * mm});
            skLineSegment(sketch, "E1580", {"start": v(17.46, -45.1) * mm, "end": v(17.63, -45.5) * mm});
            skLineSegment(sketch, "E1581", {"start": v(17.63, -45.5) * mm, "end": v(17.8, -45.9) * mm});
            skLineSegment(sketch, "E1582", {"start": v(17.8, -45.9) * mm, "end": v(17.98, -46.3) * mm});
            skLineSegment(sketch, "E1583", {"start": v(17.98, -46.3) * mm, "end": v(18.15, -46.68) * mm});
            skLineSegment(sketch, "E1584", {"start": v(18.15, -46.68) * mm, "end": v(18.32, -47.1) * mm});
            skLineSegment(sketch, "E1585", {"start": v(18.32, -47.1) * mm, "end": v(18.5, -47.48) * mm});
            skLineSegment(sketch, "E1586", {"start": v(18.5, -47.48) * mm, "end": v(18.66, -47.87) * mm});
            skLineSegment(sketch, "E1587", {"start": v(18.66, -47.87) * mm, "end": v(18.84, -48.28) * mm});
            skLineSegment(sketch, "E1588", {"start": v(18.84, -48.28) * mm, "end": v(19.03, -48.7) * mm});
            skLineSegment(sketch, "E1589", {"start": v(19.03, -48.7) * mm, "end": v(19.29, -49.06) * mm});
            skLineSegment(sketch, "E1590", {"start": v(19.29, -49.06) * mm, "end": v(19.63, -49.35) * mm});
            skLineSegment(sketch, "E1591", {"start": v(19.63, -49.35) * mm, "end": v(20.04, -49.54) * mm});
            skLineSegment(sketch, "E1592", {"start": v(20.04, -49.54) * mm, "end": v(20.48, -49.61) * mm});
            skLineSegment(sketch, "E1593", {"start": v(20.48, -49.61) * mm, "end": v(20.93, -49.57) * mm});
            skLineSegment(sketch, "E1594", {"start": v(20.93, -49.57) * mm, "end": v(21.35, -49.4) * mm});
            skLineSegment(sketch, "E1595", {"start": v(21.35, -49.4) * mm, "end": v(21.7, -49.14) * mm});
            skLineSegment(sketch, "E1596", {"start": v(21.7, -49.14) * mm, "end": v(21.99, -48.8) * mm});
            skLineSegment(sketch, "E1597", {"start": v(21.99, -48.8) * mm, "end": v(22.17, -48.38) * mm});
            skLineSegment(sketch, "E1598", {"start": v(22.17, -48.38) * mm, "end": v(22.24, -47.94) * mm});
            skLineSegment(sketch, "E1599", {"start": v(22.24, -47.94) * mm, "end": v(22.19, -47.5) * mm});
            skLineSegment(sketch, "E1600", {"start": v(22.19, -47.5) * mm, "end": v(22.02, -47.1) * mm});
            skLineSegment(sketch, "E1601", {"start": v(22.02, -47.1) * mm, "end": v(21.84, -46.73) * mm});
            skLineSegment(sketch, "E1602", {"start": v(21.84, -46.73) * mm, "end": v(21.64, -46.34) * mm});
            skLineSegment(sketch, "E1603", {"start": v(21.64, -46.34) * mm, "end": v(21.45, -45.96) * mm});
            skLineSegment(sketch, "E1604", {"start": v(21.45, -45.96) * mm, "end": v(21.25, -45.59) * mm});
            skLineSegment(sketch, "E1605", {"start": v(21.25, -45.59) * mm, "end": v(21.05, -45.19) * mm});
            skLineSegment(sketch, "E1606", {"start": v(21.05, -45.19) * mm, "end": v(20.85, -44.81) * mm});
            skLineSegment(sketch, "E1607", {"start": v(20.85, -44.81) * mm, "end": v(20.66, -44.44) * mm});
            skLineSegment(sketch, "E1608", {"start": v(20.66, -44.44) * mm, "end": v(20.46, -44.04) * mm});
            skLineSegment(sketch, "E1609", {"start": v(20.46, -44.04) * mm, "end": v(20.26, -43.66) * mm});
            skLineSegment(sketch, "E1610", {"start": v(20.26, -43.66) * mm, "end": v(20.07, -43.29) * mm});
            skLineSegment(sketch, "E1611", {"start": v(20.07, -43.29) * mm, "end": v(19.86, -42.89) * mm});
            skLineSegment(sketch, "E1612", {"start": v(19.86, -42.89) * mm, "end": v(19.67, -42.51) * mm});
            skLineSegment(sketch, "E1613", {"start": v(19.67, -42.51) * mm, "end": v(19.53, -42.23) * mm});
            skLineSegment(sketch, "E1614", {"start": v(19.53, -42.23) * mm, "end": v(19.9, -42.02) * mm});
            skLineSegment(sketch, "E1615", {"start": v(19.9, -42.02) * mm, "end": v(20.26, -41.81) * mm});
            skLineSegment(sketch, "E1616", {"start": v(20.26, -41.81) * mm, "end": v(20.62, -41.6) * mm});
            skLineSegment(sketch, "E1617", {"start": v(20.62, -41.6) * mm, "end": v(20.99, -41.39) * mm});
            skLineSegment(sketch, "E1618", {"start": v(20.99, -41.39) * mm, "end": v(21.35, -41.18) * mm});
            skLineSegment(sketch, "E1619", {"start": v(21.35, -41.18) * mm, "end": v(21.72, -40.97) * mm});
            skLineSegment(sketch, "E1620", {"start": v(21.72, -40.97) * mm, "end": v(22.08, -40.76) * mm});
            skLineSegment(sketch, "E1621", {"start": v(22.08, -40.76) * mm, "end": v(22.45, -40.55) * mm});
            skLineSegment(sketch, "E1622", {"start": v(22.45, -40.55) * mm, "end": v(22.81, -40.34) * mm});
            skLineSegment(sketch, "E1623", {"start": v(22.81, -40.34) * mm, "end": v(23.18, -40.13) * mm});
            skLineSegment(sketch, "E1624", {"start": v(23.18, -40.13) * mm, "end": v(23.51, -39.93) * mm});
            skLineSegment(sketch, "E1625", {"start": v(23.51, -39.93) * mm, "end": v(23.74, -40.29) * mm});
            skLineSegment(sketch, "E1626", {"start": v(23.74, -40.29) * mm, "end": v(23.97, -40.64) * mm});
            skLineSegment(sketch, "E1627", {"start": v(23.97, -40.64) * mm, "end": v(24.21, -41.02) * mm});
            skLineSegment(sketch, "E1628", {"start": v(24.21, -41.02) * mm, "end": v(24.44, -41.37) * mm});
            skLineSegment(sketch, "E1629", {"start": v(24.44, -41.37) * mm, "end": v(24.67, -41.73) * mm});
            skLineSegment(sketch, "E1630", {"start": v(24.67, -41.73) * mm, "end": v(24.91, -42.1) * mm});
            skLineSegment(sketch, "E1631", {"start": v(24.91, -42.1) * mm, "end": v(25.14, -42.46) * mm});
            skLineSegment(sketch, "E1632", {"start": v(25.14, -42.46) * mm, "end": v(25.37, -42.81) * mm});
            skLineSegment(sketch, "E1633", {"start": v(25.37, -42.81) * mm, "end": v(25.61, -43.2) * mm});
            skLineSegment(sketch, "E1634", {"start": v(25.61, -43.2) * mm, "end": v(25.84, -43.55) * mm});
            skLineSegment(sketch, "E1635", {"start": v(25.84, -43.55) * mm, "end": v(26.07, -43.9) * mm});
            skLineSegment(sketch, "E1636", {"start": v(26.07, -43.9) * mm, "end": v(26.31, -44.28) * mm});
            skLineSegment(sketch, "E1637", {"start": v(26.31, -44.28) * mm, "end": v(26.56, -44.66) * mm});
            skLineSegment(sketch, "E1638", {"start": v(26.56, -44.66) * mm, "end": v(26.88, -44.98) * mm});
            skLineSegment(sketch, "E1639", {"start": v(26.88, -44.98) * mm, "end": v(27.26, -45.21) * mm});
            skLineSegment(sketch, "E1640", {"start": v(27.26, -45.21) * mm, "end": v(27.7, -45.33) * mm});
            skLineSegment(sketch, "E1641", {"start": v(27.7, -45.33) * mm, "end": v(28.14, -45.33) * mm});
            skLineSegment(sketch, "E1642", {"start": v(28.14, -45.33) * mm, "end": v(28.58, -45.22) * mm});
            skLineSegment(sketch, "E1643", {"start": v(28.58, -45.22) * mm, "end": v(28.97, -45) * mm});
            skLineSegment(sketch, "E1644", {"start": v(28.97, -45) * mm, "end": v(29.28, -44.67) * mm});
            skLineSegment(sketch, "E1645", {"start": v(29.28, -44.67) * mm, "end": v(29.5, -44.28) * mm});
            skLineSegment(sketch, "E1646", {"start": v(29.5, -44.28) * mm, "end": v(29.62, -43.85) * mm});
            skLineSegment(sketch, "E1647", {"start": v(29.62, -43.85) * mm, "end": v(29.61, -43.4) * mm});
            skLineSegment(sketch, "E1648", {"start": v(29.61, -43.4) * mm, "end": v(29.49, -42.97) * mm});
            skLineSegment(sketch, "E1649", {"start": v(29.49, -42.97) * mm, "end": v(29.27, -42.61) * mm});
            skLineSegment(sketch, "E1650", {"start": v(29.27, -42.61) * mm, "end": v(29.02, -42.27) * mm});
            skLineSegment(sketch, "E1651", {"start": v(29.02, -42.27) * mm, "end": v(28.76, -41.91) * mm});
            skLineSegment(sketch, "E1652", {"start": v(28.76, -41.91) * mm, "end": v(28.51, -41.58) * mm});
            skLineSegment(sketch, "E1653", {"start": v(28.51, -41.58) * mm, "end": v(28.26, -41.24) * mm});
            skLineSegment(sketch, "E1654", {"start": v(28.26, -41.24) * mm, "end": v(28, -40.87) * mm});
            skLineSegment(sketch, "E1655", {"start": v(28, -40.87) * mm, "end": v(27.74, -40.54) * mm});
            skLineSegment(sketch, "E1656", {"start": v(27.74, -40.54) * mm, "end": v(27.5, -40.2) * mm});
            skLineSegment(sketch, "E1657", {"start": v(27.5, -40.2) * mm, "end": v(27.23, -39.83) * mm});
            skLineSegment(sketch, "E1658", {"start": v(27.23, -39.83) * mm, "end": v(26.98, -39.5) * mm});
            skLineSegment(sketch, "E1659", {"start": v(26.98, -39.5) * mm, "end": v(26.73, -39.16) * mm});
            skLineSegment(sketch, "E1660", {"start": v(26.73, -39.16) * mm, "end": v(26.46, -38.8) * mm});
            skLineSegment(sketch, "E1661", {"start": v(26.46, -38.8) * mm, "end": v(26.2, -38.46) * mm});
            skLineSegment(sketch, "E1662", {"start": v(26.2, -38.46) * mm, "end": v(26.02, -38.2) * mm});
            skLineSegment(sketch, "E1663", {"start": v(26.02, -38.2) * mm, "end": v(26.35, -37.93) * mm});
            skLineSegment(sketch, "E1664", {"start": v(26.35, -37.93) * mm, "end": v(26.67, -37.67) * mm});
            skLineSegment(sketch, "E1665", {"start": v(26.67, -37.67) * mm, "end": v(27, -37.4) * mm});
            skLineSegment(sketch, "E1666", {"start": v(27, -37.4) * mm, "end": v(27.33, -37.13) * mm});
            skLineSegment(sketch, "E1667", {"start": v(27.33, -37.13) * mm, "end": v(27.65, -36.87) * mm});
            skLineSegment(sketch, "E1668", {"start": v(27.65, -36.87) * mm, "end": v(27.98, -36.6) * mm});
            skLineSegment(sketch, "E1669", {"start": v(27.98, -36.6) * mm, "end": v(28.3, -36.33) * mm});
            skLineSegment(sketch, "E1670", {"start": v(28.3, -36.33) * mm, "end": v(28.63, -36.07) * mm});
            skLineSegment(sketch, "E1671", {"start": v(28.63, -36.07) * mm, "end": v(28.96, -35.8) * mm});
            skLineSegment(sketch, "E1672", {"start": v(28.96, -35.8) * mm, "end": v(29.29, -35.53) * mm});
            skLineSegment(sketch, "E1673", {"start": v(29.29, -35.53) * mm, "end": v(29.59, -35.29) * mm});
            skLineSegment(sketch, "E1674", {"start": v(29.59, -35.29) * mm, "end": v(29.87, -35.6) * mm});
            skLineSegment(sketch, "E1675", {"start": v(29.87, -35.6) * mm, "end": v(30.15, -35.92) * mm});
            skLineSegment(sketch, "E1676", {"start": v(30.15, -35.92) * mm, "end": v(30.45, -36.25) * mm});
            skLineSegment(sketch, "E1677", {"start": v(30.45, -36.25) * mm, "end": v(30.73, -36.56) * mm});
            skLineSegment(sketch, "E1678", {"start": v(30.73, -36.56) * mm, "end": v(31.02, -36.88) * mm});
            skLineSegment(sketch, "E1679", {"start": v(31.02, -36.88) * mm, "end": v(31.32, -37.21) * mm});
            skLineSegment(sketch, "E1680", {"start": v(31.32, -37.21) * mm, "end": v(31.6, -37.52) * mm});
            skLineSegment(sketch, "E1681", {"start": v(31.6, -37.52) * mm, "end": v(31.88, -37.84) * mm});
            skLineSegment(sketch, "E1682", {"start": v(31.88, -37.84) * mm, "end": v(32.18, -38.17) * mm});
            skLineSegment(sketch, "E1683", {"start": v(32.18, -38.17) * mm, "end": v(32.46, -38.48) * mm});
            skLineSegment(sketch, "E1684", {"start": v(32.46, -38.48) * mm, "end": v(32.75, -38.8) * mm});
            skLineSegment(sketch, "E1685", {"start": v(32.75, -38.8) * mm, "end": v(33.05, -39.13) * mm});
            skLineSegment(sketch, "E1686", {"start": v(33.05, -39.13) * mm, "end": v(33.36, -39.47) * mm});
            skLineSegment(sketch, "E1687", {"start": v(33.36, -39.47) * mm, "end": v(33.72, -39.74) * mm});
            skLineSegment(sketch, "E1688", {"start": v(33.72, -39.74) * mm, "end": v(34.13, -39.9) * mm});
            skLineSegment(sketch, "E1689", {"start": v(34.13, -39.9) * mm, "end": v(34.58, -39.95) * mm});
            skLineSegment(sketch, "E1690", {"start": v(34.58, -39.95) * mm, "end": v(35.02, -39.88) * mm});
            skLineSegment(sketch, "E1691", {"start": v(35.02, -39.88) * mm, "end": v(35.43, -39.7) * mm});
            skLineSegment(sketch, "E1692", {"start": v(35.43, -39.7) * mm, "end": v(35.78, -39.4) * mm});
            skLineSegment(sketch, "E1693", {"start": v(35.78, -39.4) * mm, "end": v(36.04, -39.04) * mm});
            skLineSegment(sketch, "E1694", {"start": v(36.04, -39.04) * mm, "end": v(36.2, -38.62) * mm});
            skLineSegment(sketch, "E1695", {"start": v(36.2, -38.62) * mm, "end": v(36.24, -38.18) * mm});
            skLineSegment(sketch, "E1696", {"start": v(36.24, -38.18) * mm, "end": v(36.16, -37.74) * mm});
            skLineSegment(sketch, "E1697", {"start": v(36.16, -37.74) * mm, "end": v(35.97, -37.33) * mm});
            skLineSegment(sketch, "E1698", {"start": v(35.97, -37.33) * mm, "end": v(35.7, -37.01) * mm});
            skLineSegment(sketch, "E1699", {"start": v(35.7, -37.01) * mm, "end": v(35.4, -36.71) * mm});
            skLineSegment(sketch, "E1700", {"start": v(35.4, -36.71) * mm, "end": v(35.09, -36.4) * mm});
            skLineSegment(sketch, "E1701", {"start": v(35.09, -36.4) * mm, "end": v(34.78, -36.11) * mm});
            skLineSegment(sketch, "E1702", {"start": v(34.78, -36.11) * mm, "end": v(34.48, -35.82) * mm});
            skLineSegment(sketch, "E1703", {"start": v(34.48, -35.82) * mm, "end": v(34.16, -35.5) * mm});
            skLineSegment(sketch, "E1704", {"start": v(34.16, -35.5) * mm, "end": v(33.86, -35.2) * mm});
            skLineSegment(sketch, "E1705", {"start": v(33.86, -35.2) * mm, "end": v(33.56, -34.91) * mm});
            skLineSegment(sketch, "E1706", {"start": v(33.56, -34.91) * mm, "end": v(33.24, -34.6) * mm});
            skLineSegment(sketch, "E1707", {"start": v(33.24, -34.6) * mm, "end": v(32.93, -34.3) * mm});
            skLineSegment(sketch, "E1708", {"start": v(32.93, -34.3) * mm, "end": v(32.63, -34) * mm});
            skLineSegment(sketch, "E1709", {"start": v(32.63, -34) * mm, "end": v(32.31, -33.7) * mm});
            skLineSegment(sketch, "E1710", {"start": v(32.31, -33.7) * mm, "end": v(32, -33.4) * mm});
            skLineSegment(sketch, "E1711", {"start": v(32, -33.4) * mm, "end": v(31.78, -33.18) * mm});
            skLineSegment(sketch, "E1712", {"start": v(31.78, -33.18) * mm, "end": v(32.06, -32.86) * mm});
            skLineSegment(sketch, "E1713", {"start": v(32.06, -32.86) * mm, "end": v(32.34, -32.55) * mm});
            skLineSegment(sketch, "E1714", {"start": v(32.34, -32.55) * mm, "end": v(32.62, -32.23) * mm});
            skLineSegment(sketch, "E1715", {"start": v(32.62, -32.23) * mm, "end": v(32.9, -31.92) * mm});
            skLineSegment(sketch, "E1716", {"start": v(32.9, -31.92) * mm, "end": v(33.18, -31.6) * mm});
            skLineSegment(sketch, "E1717", {"start": v(33.18, -31.6) * mm, "end": v(33.46, -31.29) * mm});
            skLineSegment(sketch, "E1718", {"start": v(33.46, -31.29) * mm, "end": v(33.74, -30.97) * mm});
            skLineSegment(sketch, "E1719", {"start": v(33.74, -30.97) * mm, "end": v(34.02, -30.66) * mm});
            skLineSegment(sketch, "E1720", {"start": v(34.02, -30.66) * mm, "end": v(34.3, -30.34) * mm});
            skLineSegment(sketch, "E1721", {"start": v(34.3, -30.34) * mm, "end": v(34.58, -30.02) * mm});
            skLineSegment(sketch, "E1722", {"start": v(34.58, -30.02) * mm, "end": v(34.84, -29.73) * mm});
            skLineSegment(sketch, "E1723", {"start": v(34.84, -29.73) * mm, "end": v(35.16, -30) * mm});
            skLineSegment(sketch, "E1724", {"start": v(35.16, -30) * mm, "end": v(35.5, -30.26) * mm});
            skLineSegment(sketch, "E1725", {"start": v(35.5, -30.26) * mm, "end": v(35.84, -30.54) * mm});
            skLineSegment(sketch, "E1726", {"start": v(35.84, -30.54) * mm, "end": v(36.17, -30.8) * mm});
            skLineSegment(sketch, "E1727", {"start": v(36.17, -30.8) * mm, "end": v(36.5, -31.07) * mm});
            skLineSegment(sketch, "E1728", {"start": v(36.5, -31.07) * mm, "end": v(36.85, -31.35) * mm});
            skLineSegment(sketch, "E1729", {"start": v(36.85, -31.35) * mm, "end": v(37.18, -31.62) * mm});
            skLineSegment(sketch, "E1730", {"start": v(37.18, -31.62) * mm, "end": v(37.5, -31.88) * mm});
            skLineSegment(sketch, "E1731", {"start": v(37.5, -31.88) * mm, "end": v(37.86, -32.16) * mm});
            skLineSegment(sketch, "E1732", {"start": v(37.86, -32.16) * mm, "end": v(38.19, -32.43) * mm});
            skLineSegment(sketch, "E1733", {"start": v(38.19, -32.43) * mm, "end": v(38.52, -32.69) * mm});
            skLineSegment(sketch, "E1734", {"start": v(38.52, -32.69) * mm, "end": v(38.87, -32.97) * mm});
            skLineSegment(sketch, "E1735", {"start": v(38.87, -32.97) * mm, "end": v(39.23, -33.26) * mm});
            skLineSegment(sketch, "E1736", {"start": v(39.23, -33.26) * mm, "end": v(39.63, -33.46) * mm});
            skLineSegment(sketch, "E1737", {"start": v(39.63, -33.46) * mm, "end": v(40.06, -33.55) * mm});
            skLineSegment(sketch, "E1738", {"start": v(40.06, -33.55) * mm, "end": v(40.51, -33.53) * mm});
            skLineSegment(sketch, "E1739", {"start": v(40.51, -33.53) * mm, "end": v(40.94, -33.39) * mm});
            skLineSegment(sketch, "E1740", {"start": v(40.94, -33.39) * mm, "end": v(41.31, -33.14) * mm});
            skLineSegment(sketch, "E1741", {"start": v(41.31, -33.14) * mm, "end": v(41.6, -32.8) * mm});
            skLineSegment(sketch, "E1742", {"start": v(41.6, -32.8) * mm, "end": v(41.8, -32.4) * mm});
            skLineSegment(sketch, "E1743", {"start": v(41.8, -32.4) * mm, "end": v(41.9, -31.97) * mm});
            skLineSegment(sketch, "E1744", {"start": v(41.9, -31.97) * mm, "end": v(41.86, -31.52) * mm});
            skLineSegment(sketch, "E1745", {"start": v(41.86, -31.52) * mm, "end": v(41.72, -31.1) * mm});
            skLineSegment(sketch, "E1746", {"start": v(41.72, -31.1) * mm, "end": v(41.46, -30.72) * mm});
            skLineSegment(sketch, "E1747", {"start": v(41.46, -30.72) * mm, "end": v(41.14, -30.45) * mm});
            skLineSegment(sketch, "E1748", {"start": v(41.14, -30.45) * mm, "end": v(40.8, -30.2) * mm});
            skLineSegment(sketch, "E1749", {"start": v(40.8, -30.2) * mm, "end": v(40.44, -29.95) * mm});
            skLineSegment(sketch, "E1750", {"start": v(40.44, -29.95) * mm, "end": v(40.1, -29.71) * mm});
            skLineSegment(sketch, "E1751", {"start": v(40.1, -29.71) * mm, "end": v(39.75, -29.47) * mm});
            skLineSegment(sketch, "E1752", {"start": v(39.75, -29.47) * mm, "end": v(39.38, -29.2) * mm});
            skLineSegment(sketch, "E1753", {"start": v(39.38, -29.2) * mm, "end": v(39.04, -28.97) * mm});
            skLineSegment(sketch, "E1754", {"start": v(39.04, -28.97) * mm, "end": v(38.7, -28.73) * mm});
            skLineSegment(sketch, "E1755", {"start": v(38.7, -28.73) * mm, "end": v(38.33, -28.47) * mm});
            skLineSegment(sketch, "E1756", {"start": v(38.33, -28.47) * mm, "end": v(37.98, -28.22) * mm});
            skLineSegment(sketch, "E1757", {"start": v(37.98, -28.22) * mm, "end": v(37.64, -27.98) * mm});
            skLineSegment(sketch, "E1758", {"start": v(37.64, -27.98) * mm, "end": v(37.27, -27.72) * mm});
            skLineSegment(sketch, "E1759", {"start": v(37.27, -27.72) * mm, "end": v(36.92, -27.48) * mm});
            skLineSegment(sketch, "E1760", {"start": v(36.92, -27.48) * mm, "end": v(36.66, -27.3) * mm});
            skLineSegment(sketch, "E1761", {"start": v(36.66, -27.3) * mm, "end": v(36.9, -26.94) * mm});
            skLineSegment(sketch, "E1762", {"start": v(36.9, -26.94) * mm, "end": v(37.12, -26.59) * mm});
            skLineSegment(sketch, "E1763", {"start": v(37.12, -26.59) * mm, "end": v(37.34, -26.23) * mm});
            skLineSegment(sketch, "E1764", {"start": v(37.34, -26.23) * mm, "end": v(37.57, -25.87) * mm});
            skLineSegment(sketch, "E1765", {"start": v(37.57, -25.87) * mm, "end": v(37.8, -25.52) * mm});
            skLineSegment(sketch, "E1766", {"start": v(37.8, -25.52) * mm, "end": v(38.02, -25.16) * mm});
            skLineSegment(sketch, "E1767", {"start": v(38.02, -25.16) * mm, "end": v(38.24, -24.8) * mm});
            skLineSegment(sketch, "E1768", {"start": v(38.24, -24.8) * mm, "end": v(38.47, -24.45) * mm});
            skLineSegment(sketch, "E1769", {"start": v(38.47, -24.45) * mm, "end": v(38.7, -24.1) * mm});
            skLineSegment(sketch, "E1770", {"start": v(38.7, -24.1) * mm, "end": v(38.92, -23.74) * mm});
            skLineSegment(sketch, "E1771", {"start": v(38.92, -23.74) * mm, "end": v(39.13, -23.4) * mm});
            skLineSegment(sketch, "E1772", {"start": v(39.13, -23.4) * mm, "end": v(39.5, -23.62) * mm});
            skLineSegment(sketch, "E1773", {"start": v(39.5, -23.62) * mm, "end": v(39.86, -23.82) * mm});
            skLineSegment(sketch, "E1774", {"start": v(39.86, -23.82) * mm, "end": v(40.25, -24.05) * mm});
            skLineSegment(sketch, "E1775", {"start": v(40.25, -24.05) * mm, "end": v(40.62, -24.25) * mm});
            skLineSegment(sketch, "E1776", {"start": v(40.62, -24.25) * mm, "end": v(40.98, -24.46) * mm});
            skLineSegment(sketch, "E1777", {"start": v(40.98, -24.46) * mm, "end": v(41.37, -24.68) * mm});
            skLineSegment(sketch, "E1778", {"start": v(41.37, -24.68) * mm, "end": v(41.74, -24.9) * mm});
            skLineSegment(sketch, "E1779", {"start": v(41.74, -24.9) * mm, "end": v(42.1, -25.1) * mm});
            skLineSegment(sketch, "E1780", {"start": v(42.1, -25.1) * mm, "end": v(42.5, -25.32) * mm});
            skLineSegment(sketch, "E1781", {"start": v(42.5, -25.32) * mm, "end": v(42.87, -25.53) * mm});
            skLineSegment(sketch, "E1782", {"start": v(42.87, -25.53) * mm, "end": v(43.23, -25.74) * mm});
            skLineSegment(sketch, "E1783", {"start": v(43.23, -25.74) * mm, "end": v(43.62, -25.96) * mm});
            skLineSegment(sketch, "E1784", {"start": v(43.62, -25.96) * mm, "end": v(44.03, -26.18) * mm});
            skLineSegment(sketch, "E1785", {"start": v(44.03, -26.18) * mm, "end": v(44.45, -26.32) * mm});
            skLineSegment(sketch, "E1786", {"start": v(44.45, -26.32) * mm, "end": v(44.9, -26.34) * mm});
            skLineSegment(sketch, "E1787", {"start": v(44.9, -26.34) * mm, "end": v(45.34, -26.24) * mm});
            skLineSegment(sketch, "E1788", {"start": v(45.34, -26.24) * mm, "end": v(45.74, -26.04) * mm});
            skLineSegment(sketch, "E1789", {"start": v(45.74, -26.04) * mm, "end": v(46.07, -25.73) * mm});
            skLineSegment(sketch, "E1790", {"start": v(46.07, -25.73) * mm, "end": v(46.3, -25.35) * mm});
            skLineSegment(sketch, "E1791", {"start": v(46.3, -25.35) * mm, "end": v(46.44, -24.93) * mm});
            skLineSegment(sketch, "E1792", {"start": v(46.44, -24.93) * mm, "end": v(46.45, -24.48) * mm});
            skLineSegment(sketch, "E1793", {"start": v(46.45, -24.48) * mm, "end": v(46.35, -24.04) * mm});
            skLineSegment(sketch, "E1794", {"start": v(46.35, -24.04) * mm, "end": v(46.14, -23.65) * mm});
            skLineSegment(sketch, "E1795", {"start": v(46.14, -23.65) * mm, "end": v(45.83, -23.32) * mm});
            skLineSegment(sketch, "E1796", {"start": v(45.83, -23.32) * mm, "end": v(45.46, -23.1) * mm});
            skLineSegment(sketch, "E1797", {"start": v(45.46, -23.1) * mm, "end": v(45.09, -22.92) * mm});
            skLineSegment(sketch, "E1798", {"start": v(45.09, -22.92) * mm, "end": v(44.7, -22.72) * mm});
            skLineSegment(sketch, "E1799", {"start": v(44.7, -22.72) * mm, "end": v(44.32, -22.54) * mm});
            skLineSegment(sketch, "E1800", {"start": v(44.32, -22.54) * mm, "end": v(43.94, -22.36) * mm});
            skLineSegment(sketch, "E1801", {"start": v(43.94, -22.36) * mm, "end": v(43.53, -22.16) * mm});
            skLineSegment(sketch, "E1802", {"start": v(43.53, -22.16) * mm, "end": v(43.15, -21.98) * mm});
            skLineSegment(sketch, "E1803", {"start": v(43.15, -21.98) * mm, "end": v(42.77, -21.8) * mm});
            skLineSegment(sketch, "E1804", {"start": v(42.77, -21.8) * mm, "end": v(42.37, -21.6) * mm});
            skLineSegment(sketch, "E1805", {"start": v(42.37, -21.6) * mm, "end": v(41.99, -21.41) * mm});
            skLineSegment(sketch, "E1806", {"start": v(41.99, -21.41) * mm, "end": v(41.6, -21.23) * mm});
            skLineSegment(sketch, "E1807", {"start": v(41.6, -21.23) * mm, "end": v(41.2, -21.03) * mm});
            skLineSegment(sketch, "E1808", {"start": v(41.2, -21.03) * mm, "end": v(40.83, -20.85) * mm});
            skLineSegment(sketch, "E1809", {"start": v(40.83, -20.85) * mm, "end": v(40.54, -20.71) * mm});
            skLineSegment(sketch, "E1810", {"start": v(40.54, -20.71) * mm, "end": v(40.7, -20.32) * mm});
            skLineSegment(sketch, "E1811", {"start": v(40.7, -20.32) * mm, "end": v(40.87, -19.94) * mm});
            skLineSegment(sketch, "E1812", {"start": v(40.87, -19.94) * mm, "end": v(41.04, -19.55) * mm});
            skLineSegment(sketch, "E1813", {"start": v(41.04, -19.55) * mm, "end": v(41.2, -19.16) * mm});
            skLineSegment(sketch, "E1814", {"start": v(41.2, -19.16) * mm, "end": v(41.37, -18.77) * mm});
            skLineSegment(sketch, "E1815", {"start": v(41.37, -18.77) * mm, "end": v(41.53, -18.38) * mm});
            skLineSegment(sketch, "E1816", {"start": v(41.53, -18.38) * mm, "end": v(41.7, -18) * mm});
            skLineSegment(sketch, "E1817", {"start": v(41.7, -18) * mm, "end": v(41.86, -17.6) * mm});
            skLineSegment(sketch, "E1818", {"start": v(41.86, -17.6) * mm, "end": v(42.03, -17.22) * mm});
            skLineSegment(sketch, "E1819", {"start": v(42.03, -17.22) * mm, "end": v(42.2, -16.83) * mm});
            skLineSegment(sketch, "E1820", {"start": v(42.2, -16.83) * mm, "end": v(42.35, -16.48) * mm});
            skLineSegment(sketch, "E1821", {"start": v(42.35, -16.48) * mm, "end": v(42.74, -16.62) * mm});
            skLineSegment(sketch, "E1822", {"start": v(42.74, -16.62) * mm, "end": v(43.14, -16.77) * mm});
            skLineSegment(sketch, "E1823", {"start": v(43.14, -16.77) * mm, "end": v(43.56, -16.92) * mm});
            skLineSegment(sketch, "E1824", {"start": v(43.56, -16.92) * mm, "end": v(43.95, -17.07) * mm});
            skLineSegment(sketch, "E1825", {"start": v(43.95, -17.07) * mm, "end": v(44.35, -17.22) * mm});
            skLineSegment(sketch, "E1826", {"start": v(44.35, -17.22) * mm, "end": v(44.77, -17.37) * mm});
            skLineSegment(sketch, "E1827", {"start": v(44.77, -17.37) * mm, "end": v(45.17, -17.52) * mm});
            skLineSegment(sketch, "E1828", {"start": v(45.17, -17.52) * mm, "end": v(45.56, -17.67) * mm});
            skLineSegment(sketch, "E1829", {"start": v(45.56, -17.67) * mm, "end": v(45.98, -17.82) * mm});
            skLineSegment(sketch, "E1830", {"start": v(45.98, -17.82) * mm, "end": v(46.38, -17.97) * mm});
            skLineSegment(sketch, "E1831", {"start": v(46.38, -17.97) * mm, "end": v(46.77, -18.11) * mm});
            skLineSegment(sketch, "E1832", {"start": v(46.77, -18.11) * mm, "end": v(47.2, -18.27) * mm});
            skLineSegment(sketch, "E1833", {"start": v(47.2, -18.27) * mm, "end": v(47.63, -18.43) * mm});
            skLineSegment(sketch, "E1834", {"start": v(47.63, -18.43) * mm, "end": v(48.07, -18.5) * mm});
            skLineSegment(sketch, "E1835", {"start": v(48.07, -18.5) * mm, "end": v(48.52, -18.44) * mm});
            skLineSegment(sketch, "E1836", {"start": v(48.52, -18.44) * mm, "end": v(48.93, -18.28) * mm});
            skLineSegment(sketch, "E1837", {"start": v(48.93, -18.28) * mm, "end": v(49.3, -18.01) * mm});
            skLineSegment(sketch, "E1838", {"start": v(49.3, -18.01) * mm, "end": v(49.57, -17.66) * mm});
            skLineSegment(sketch, "E1839", {"start": v(49.57, -17.66) * mm, "end": v(49.74, -17.25) * mm});
            skLineSegment(sketch, "E1840", {"start": v(49.74, -17.25) * mm, "end": v(49.8, -16.8) * mm});
            skLineSegment(sketch, "E1841", {"start": v(49.8, -16.8) * mm, "end": v(49.75, -16.36) * mm});
            skLineSegment(sketch, "E1842", {"start": v(49.75, -16.36) * mm, "end": v(49.58, -15.94) * mm});
            skLineSegment(sketch, "E1843", {"start": v(49.58, -15.94) * mm, "end": v(49.3, -15.59) * mm});
            skLineSegment(sketch, "E1844", {"start": v(49.3, -15.59) * mm, "end": v(48.95, -15.32) * mm});
            skLineSegment(sketch, "E1845", {"start": v(48.95, -15.32) * mm, "end": v(48.55, -15.16) * mm});
            skLineSegment(sketch, "E1846", {"start": v(48.55, -15.16) * mm, "end": v(48.15, -15.03) * mm});
            skLineSegment(sketch, "E1847", {"start": v(48.15, -15.03) * mm, "end": v(47.73, -14.9) * mm});
            skLineSegment(sketch, "E1848", {"start": v(47.73, -14.9) * mm, "end": v(47.33, -14.79) * mm});
            skLineSegment(sketch, "E1849", {"start": v(47.33, -14.79) * mm, "end": v(46.93, -14.67) * mm});
            skLineSegment(sketch, "E1850", {"start": v(46.93, -14.67) * mm, "end": v(46.5, -14.54) * mm});
            skLineSegment(sketch, "E1851", {"start": v(46.5, -14.54) * mm, "end": v(46.1, -14.42) * mm});
            skLineSegment(sketch, "E1852", {"start": v(46.1, -14.42) * mm, "end": v(45.69, -14.3) * mm});
            skLineSegment(sketch, "E1853", {"start": v(45.69, -14.3) * mm, "end": v(45.26, -14.17) * mm});
            skLineSegment(sketch, "E1854", {"start": v(45.26, -14.17) * mm, "end": v(44.85, -14.05) * mm});
            skLineSegment(sketch, "E1855", {"start": v(44.85, -14.05) * mm, "end": v(44.45, -13.93) * mm});
            skLineSegment(sketch, "E1856", {"start": v(44.45, -13.93) * mm, "end": v(44.02, -13.8) * mm});
            skLineSegment(sketch, "E1857", {"start": v(44.02, -13.8) * mm, "end": v(43.61, -13.68) * mm});
            skLineSegment(sketch, "E1858", {"start": v(43.61, -13.68) * mm, "end": v(43.3, -13.59) * mm});
            skLineSegment(sketch, "E1859", {"start": v(43.3, -13.59) * mm, "end": v(43.41, -13.18) * mm});
            skLineSegment(sketch, "E1860", {"start": v(43.41, -13.18) * mm, "end": v(43.51, -12.77) * mm});
            skLineSegment(sketch, "E1861", {"start": v(43.51, -12.77) * mm, "end": v(43.61, -12.36) * mm});
            skLineSegment(sketch, "E1862", {"start": v(43.61, -12.36) * mm, "end": v(43.71, -11.95) * mm});
            skLineSegment(sketch, "E1863", {"start": v(43.71, -11.95) * mm, "end": v(43.81, -11.54) * mm});
            skLineSegment(sketch, "E1864", {"start": v(43.81, -11.54) * mm, "end": v(43.91, -11.13) * mm});
            skLineSegment(sketch, "E1865", {"start": v(43.91, -11.13) * mm, "end": v(44.02, -10.72) * mm});
            skLineSegment(sketch, "E1866", {"start": v(44.02, -10.72) * mm, "end": v(44.12, -10.31) * mm});
            skLineSegment(sketch, "E1867", {"start": v(44.12, -10.31) * mm, "end": v(44.22, -9.9) * mm});
            skLineSegment(sketch, "E1868", {"start": v(44.22, -9.9) * mm, "end": v(44.32, -9.5) * mm});
            skLineSegment(sketch, "E1869", {"start": v(44.32, -9.5) * mm, "end": v(44.41, -9.12) * mm});
            skLineSegment(sketch, "E1870", {"start": v(44.41, -9.12) * mm, "end": v(44.83, -9.2) * mm});
            skLineSegment(sketch, "E1871", {"start": v(44.83, -9.2) * mm, "end": v(45.24, -9.28) * mm});
            skLineSegment(sketch, "E1872", {"start": v(45.24, -9.28) * mm, "end": v(45.68, -9.37) * mm});
            skLineSegment(sketch, "E1873", {"start": v(45.68, -9.37) * mm, "end": v(46.1, -9.45) * mm});
            skLineSegment(sketch, "E1874", {"start": v(46.1, -9.45) * mm, "end": v(46.5, -9.53) * mm});
            skLineSegment(sketch, "E1875", {"start": v(46.5, -9.53) * mm, "end": v(46.95, -9.61) * mm});
            skLineSegment(sketch, "E1876", {"start": v(46.95, -9.61) * mm, "end": v(47.36, -9.7) * mm});
            skLineSegment(sketch, "E1877", {"start": v(47.36, -9.7) * mm, "end": v(47.78, -9.78) * mm});
            skLineSegment(sketch, "E1878", {"start": v(47.78, -9.78) * mm, "end": v(48.22, -9.86) * mm});
            skLineSegment(sketch, "E1879", {"start": v(48.22, -9.86) * mm, "end": v(48.63, -9.94) * mm});
            skLineSegment(sketch, "E1880", {"start": v(48.63, -9.94) * mm, "end": v(49.04, -10.02) * mm});
            skLineSegment(sketch, "E1881", {"start": v(49.04, -10.02) * mm, "end": v(49.49, -10.11) * mm});
            skLineSegment(sketch, "E1882", {"start": v(49.49, -10.11) * mm, "end": v(49.94, -10.2) * mm});
            skLineSegment(sketch, "E1883", {"start": v(49.94, -10.2) * mm, "end": v(50.39, -10.2) * mm});
            skLineSegment(sketch, "E1884", {"start": v(50.39, -10.2) * mm, "end": v(50.82, -10.07) * mm});
            skLineSegment(sketch, "E1885", {"start": v(50.82, -10.07) * mm, "end": v(51.2, -9.84) * mm});
            skLineSegment(sketch, "E1886", {"start": v(51.2, -9.84) * mm, "end": v(51.51, -9.52) * mm});
            skLineSegment(sketch, "E1887", {"start": v(51.51, -9.52) * mm, "end": v(51.73, -9.13) * mm});
            skLineSegment(sketch, "E1888", {"start": v(51.73, -9.13) * mm, "end": v(51.84, -8.7) * mm});
            skLineSegment(sketch, "E1889", {"start": v(51.84, -8.7) * mm, "end": v(51.83, -8.24) * mm});
            skLineSegment(sketch, "E1890", {"start": v(51.83, -8.24) * mm, "end": v(51.7, -7.81) * mm});
            skLineSegment(sketch, "E1891", {"start": v(51.7, -7.81) * mm, "end": v(51.46, -7.43) * mm});
            skLineSegment(sketch, "E1892", {"start": v(51.46, -7.43) * mm, "end": v(51.14, -7.12) * mm});
            skLineSegment(sketch, "E1893", {"start": v(51.14, -7.12) * mm, "end": v(50.74, -6.91) * mm});
            skLineSegment(sketch, "E1894", {"start": v(50.74, -6.91) * mm, "end": v(50.33, -6.83) * mm});
            skLineSegment(sketch, "E1895", {"start": v(50.33, -6.83) * mm, "end": v(49.91, -6.76) * mm});
            skLineSegment(sketch, "E1896", {"start": v(49.91, -6.76) * mm, "end": v(49.48, -6.7) * mm});
            skLineSegment(sketch, "E1897", {"start": v(49.48, -6.7) * mm, "end": v(49.06, -6.65) * mm});
            skLineSegment(sketch, "E1898", {"start": v(49.06, -6.65) * mm, "end": v(48.64, -6.6) * mm});
            skLineSegment(sketch, "E1899", {"start": v(48.64, -6.6) * mm, "end": v(48.2, -6.54) * mm});
            skLineSegment(sketch, "E1900", {"start": v(48.2, -6.54) * mm, "end": v(47.78, -6.48) * mm});
            skLineSegment(sketch, "E1901", {"start": v(47.78, -6.48) * mm, "end": v(47.36, -6.43) * mm});
            skLineSegment(sketch, "E1902", {"start": v(47.36, -6.43) * mm, "end": v(46.91, -6.37) * mm});
            skLineSegment(sketch, "E1903", {"start": v(46.91, -6.37) * mm, "end": v(46.5, -6.32) * mm});
            skLineSegment(sketch, "E1904", {"start": v(46.5, -6.32) * mm, "end": v(46.08, -6.26) * mm});
            skLineSegment(sketch, "E1905", {"start": v(46.08, -6.26) * mm, "end": v(45.63, -6.2) * mm});
            skLineSegment(sketch, "E1906", {"start": v(45.63, -6.2) * mm, "end": v(45.21, -6.15) * mm});
            skLineSegment(sketch, "E1907", {"start": v(45.21, -6.15) * mm, "end": v(44.9, -6.11) * mm});
            skLineSegment(sketch, "E1908", {"start": v(44.9, -6.11) * mm, "end": v(44.93, -5.7) * mm});
            skLineSegment(sketch, "E1909", {"start": v(44.93, -5.7) * mm, "end": v(44.97, -5.27) * mm});
            skLineSegment(sketch, "E1910", {"start": v(44.97, -5.27) * mm, "end": v(45, -4.85) * mm});
            skLineSegment(sketch, "E1911", {"start": v(45, -4.85) * mm, "end": v(45.04, -4.43) * mm});
            skLineSegment(sketch, "E1912", {"start": v(45.04, -4.43) * mm, "end": v(45.07, -4.01) * mm});
            skLineSegment(sketch, "E1913", {"start": v(45.07, -4.01) * mm, "end": v(45.1, -3.6) * mm});
            skLineSegment(sketch, "E1914", {"start": v(45.1, -3.6) * mm, "end": v(45.14, -3.17) * mm});
            skLineSegment(sketch, "E1915", {"start": v(45.14, -3.17) * mm, "end": v(45.17, -2.75) * mm});
            skLineSegment(sketch, "E1916", {"start": v(45.17, -2.75) * mm, "end": v(45.2, -2.33) * mm});
            skLineSegment(sketch, "E1917", {"start": v(45.2, -2.33) * mm, "end": v(45.24, -1.9) * mm});
            skLineSegment(sketch, "E1918", {"start": v(45.24, -1.9) * mm, "end": v(45.27, -1.52) * mm});
            skLineSegment(sketch, "E1919", {"start": v(-12.03, 2.52) * mm, "end": v(-11.85, 3.14) * mm});
            skLineSegment(sketch, "E1920", {"start": v(-11.85, 3.14) * mm, "end": v(-11.64, 3.74) * mm});
            skLineSegment(sketch, "E1921", {"start": v(-11.64, 3.74) * mm, "end": v(-11.38, 4.32) * mm});
            skLineSegment(sketch, "E1922", {"start": v(-11.38, 4.32) * mm, "end": v(-11.1, 4.89) * mm});
            skLineSegment(sketch, "E1923", {"start": v(-11.1, 4.89) * mm, "end": v(-10.77, 5.44) * mm});
            skLineSegment(sketch, "E1924", {"start": v(-10.77, 5.44) * mm, "end": v(-10.4, 5.97) * mm});
            skLineSegment(sketch, "E1925", {"start": v(-10.4, 5.97) * mm, "end": v(-10.02, 6.47) * mm});
            skLineSegment(sketch, "E1926", {"start": v(-10.02, 6.47) * mm, "end": v(-9.6, 6.95) * mm});
            skLineSegment(sketch, "E1927", {"start": v(-9.6, 6.95) * mm, "end": v(-9.15, 7.4) * mm});
            skLineSegment(sketch, "E1928", {"start": v(-9.15, 7.4) * mm, "end": v(-8.67, 7.82) * mm});
            skLineSegment(sketch, "E1929", {"start": v(-8.67, 7.82) * mm, "end": v(-8.16, 8.21) * mm});
            skLineSegment(sketch, "E1930", {"start": v(-8.16, 8.21) * mm, "end": v(-7.64, 8.57) * mm});
            skLineSegment(sketch, "E1931", {"start": v(-7.64, 8.57) * mm, "end": v(-7.09, 8.9) * mm});
            skLineSegment(sketch, "E1932", {"start": v(-7.09, 8.9) * mm, "end": v(-6.52, 9.18) * mm});
            skLineSegment(sketch, "E1933", {"start": v(-6.52, 9.18) * mm, "end": v(-5.93, 9.44) * mm});
            skLineSegment(sketch, "E1934", {"start": v(-5.93, 9.44) * mm, "end": v(-5.33, 9.65) * mm});
            skLineSegment(sketch, "E1935", {"start": v(-5.33, 9.65) * mm, "end": v(-4.72, 9.83) * mm});
            skLineSegment(sketch, "E1936", {"start": v(-4.72, 9.83) * mm, "end": v(-4.6, 9.86) * mm});
            skLineSegment(sketch, "E1937", {"start": v(-4.6, 9.86) * mm, "end": v(-4.7, 42.66) * mm});
            skLineSegment(sketch, "E1938", {"start": v(-4.7, 42.66) * mm, "end": v(-4.88, 42.66) * mm});
            skLineSegment(sketch, "E1939", {"start": v(-4.88, 42.66) * mm, "end": v(-7.56, 42.4) * mm});
            skLineSegment(sketch, "E1940", {"start": v(-7.56, 42.4) * mm, "end": v(-10.2, 41.98) * mm});
            skLineSegment(sketch, "E1941", {"start": v(-10.2, 41.98) * mm, "end": v(-12.83, 41.4) * mm});
            skLineSegment(sketch, "E1942", {"start": v(-12.83, 41.4) * mm, "end": v(-15.4, 40.65) * mm});
            skLineSegment(sketch, "E1943", {"start": v(-15.4, 40.65) * mm, "end": v(-17.93, 39.74) * mm});
            skLineSegment(sketch, "E1944", {"start": v(-17.93, 39.74) * mm, "end": v(-20.4, 38.67) * mm});
            skLineSegment(sketch, "E1945", {"start": v(-20.4, 38.67) * mm, "end": v(-22.79, 37.45) * mm});
            skLineSegment(sketch, "E1946", {"start": v(-22.79, 37.45) * mm, "end": v(-25.1, 36.09) * mm});
            skLineSegment(sketch, "E1947", {"start": v(-25.1, 36.09) * mm, "end": v(-27.32, 34.58) * mm});
            skLineSegment(sketch, "E1948", {"start": v(-27.32, 34.58) * mm, "end": v(-29.44, 32.93) * mm});
            skLineSegment(sketch, "E1949", {"start": v(-29.44, 32.93) * mm, "end": v(-31.46, 31.16) * mm});
            skLineSegment(sketch, "E1950", {"start": v(-31.46, 31.16) * mm, "end": v(-33.36, 29.26) * mm});
            skLineSegment(sketch, "E1951", {"start": v(-33.36, 29.26) * mm, "end": v(-35.13, 27.24) * mm});
            skLineSegment(sketch, "E1952", {"start": v(-35.13, 27.24) * mm, "end": v(-36.78, 25.12) * mm});
            skLineSegment(sketch, "E1953", {"start": v(-36.78, 25.12) * mm, "end": v(-38.29, 22.9) * mm});
            skLineSegment(sketch, "E1954", {"start": v(-38.29, 22.9) * mm, "end": v(-39.65, 20.6) * mm});
            skLineSegment(sketch, "E1955", {"start": v(-39.65, 20.6) * mm, "end": v(-40.87, 18.2) * mm});
            skLineSegment(sketch, "E1956", {"start": v(-40.87, 18.2) * mm, "end": v(-41.94, 15.73) * mm});
            skLineSegment(sketch, "E1957", {"start": v(-41.94, 15.73) * mm, "end": v(-42.85, 13.2) * mm});
            skLineSegment(sketch, "E1958", {"start": v(-42.85, 13.2) * mm, "end": v(-43.6, 10.63) * mm});
            skLineSegment(sketch, "E1959", {"start": v(-43.6, 10.63) * mm, "end": v(-44.18, 8) * mm});
            skLineSegment(sketch, "E1960", {"start": v(-44.18, 8) * mm, "end": v(-44.6, 5.36) * mm});
            skLineSegment(sketch, "E1961", {"start": v(-44.6, 5.36) * mm, "end": v(-44.86, 2.68) * mm});
            skLineSegment(sketch, "E1962", {"start": v(-44.86, 2.68) * mm, "end": v(-44.86, 2.5) * mm});
            skLineSegment(sketch, "E1963", {"start": v(-44.86, 2.5) * mm, "end": v(-12.06, 2.4) * mm});
            skLineSegment(sketch, "E1964", {"start": v(-12.06, 2.4) * mm, "end": v(-12.03, 2.52) * mm});
            skLineSegment(sketch, "E1965", {"start": v(40.46, 2.5) * mm, "end": v(40.46, 2.68) * mm});
            skLineSegment(sketch, "E1966", {"start": v(40.46, 2.68) * mm, "end": v(40.2, 5.36) * mm});
            skLineSegment(sketch, "E1967", {"start": v(40.2, 5.36) * mm, "end": v(39.79, 8) * mm});
            skLineSegment(sketch, "E1968", {"start": v(39.79, 8) * mm, "end": v(39.2, 10.63) * mm});
            skLineSegment(sketch, "E1969", {"start": v(39.2, 10.63) * mm, "end": v(38.45, 13.2) * mm});
            skLineSegment(sketch, "E1970", {"start": v(38.45, 13.2) * mm, "end": v(37.54, 15.73) * mm});
            skLineSegment(sketch, "E1971", {"start": v(37.54, 15.73) * mm, "end": v(36.48, 18.2) * mm});
            skLineSegment(sketch, "E1972", {"start": v(36.48, 18.2) * mm, "end": v(35.26, 20.6) * mm});
            skLineSegment(sketch, "E1973", {"start": v(35.26, 20.6) * mm, "end": v(33.89, 22.9) * mm});
            skLineSegment(sketch, "E1974", {"start": v(33.89, 22.9) * mm, "end": v(32.38, 25.12) * mm});
            skLineSegment(sketch, "E1975", {"start": v(32.38, 25.12) * mm, "end": v(30.73, 27.24) * mm});
            skLineSegment(sketch, "E1976", {"start": v(30.73, 27.24) * mm, "end": v(28.96, 29.26) * mm});
            skLineSegment(sketch, "E1977", {"start": v(28.96, 29.26) * mm, "end": v(27.06, 31.16) * mm});
            skLineSegment(sketch, "E1978", {"start": v(27.06, 31.16) * mm, "end": v(25.05, 32.93) * mm});
            skLineSegment(sketch, "E1979", {"start": v(25.05, 32.93) * mm, "end": v(22.92, 34.58) * mm});
            skLineSegment(sketch, "E1980", {"start": v(22.92, 34.58) * mm, "end": v(20.7, 36.09) * mm});
            skLineSegment(sketch, "E1981", {"start": v(20.7, 36.09) * mm, "end": v(18.4, 37.45) * mm});
            skLineSegment(sketch, "E1982", {"start": v(18.4, 37.45) * mm, "end": v(16, 38.67) * mm});
            skLineSegment(sketch, "E1983", {"start": v(16, 38.67) * mm, "end": v(13.54, 39.74) * mm});
            skLineSegment(sketch, "E1984", {"start": v(13.54, 39.74) * mm, "end": v(11, 40.65) * mm});
            skLineSegment(sketch, "E1985", {"start": v(11, 40.65) * mm, "end": v(8.43, 41.4) * mm});
            skLineSegment(sketch, "E1986", {"start": v(8.43, 41.4) * mm, "end": v(5.81, 41.98) * mm});
            skLineSegment(sketch, "E1987", {"start": v(5.81, 41.98) * mm, "end": v(3.16, 42.4) * mm});
            skLineSegment(sketch, "E1988", {"start": v(3.16, 42.4) * mm, "end": v(0.49, 42.66) * mm});
            skLineSegment(sketch, "E1989", {"start": v(0.49, 42.66) * mm, "end": v(0.3, 42.66) * mm});
            skLineSegment(sketch, "E1990", {"start": v(0.3, 42.66) * mm, "end": v(0.2, 9.86) * mm});
            skLineSegment(sketch, "E1991", {"start": v(0.2, 9.86) * mm, "end": v(0.33, 9.83) * mm});
            skLineSegment(sketch, "E1992", {"start": v(0.33, 9.83) * mm, "end": v(0.94, 9.65) * mm});
            skLineSegment(sketch, "E1993", {"start": v(0.94, 9.65) * mm, "end": v(1.54, 9.44) * mm});
            skLineSegment(sketch, "E1994", {"start": v(1.54, 9.44) * mm, "end": v(2.12, 9.18) * mm});
            skLineSegment(sketch, "E1995", {"start": v(2.12, 9.18) * mm, "end": v(2.7, 8.9) * mm});
            skLineSegment(sketch, "E1996", {"start": v(2.7, 8.9) * mm, "end": v(3.24, 8.57) * mm});
            skLineSegment(sketch, "E1997", {"start": v(3.24, 8.57) * mm, "end": v(3.77, 8.21) * mm});
            skLineSegment(sketch, "E1998", {"start": v(3.77, 8.21) * mm, "end": v(4.27, 7.82) * mm});
            skLineSegment(sketch, "E1999", {"start": v(4.27, 7.82) * mm, "end": v(4.75, 7.4) * mm});
            skLineSegment(sketch, "E2000", {"start": v(4.75, 7.4) * mm, "end": v(5.2, 6.95) * mm});
            skLineSegment(sketch, "E2001", {"start": v(5.2, 6.95) * mm, "end": v(5.62, 6.47) * mm});
            skLineSegment(sketch, "E2002", {"start": v(5.62, 6.47) * mm, "end": v(6.01, 5.97) * mm});
            skLineSegment(sketch, "E2003", {"start": v(6.01, 5.97) * mm, "end": v(6.37, 5.44) * mm});
            skLineSegment(sketch, "E2004", {"start": v(6.37, 5.44) * mm, "end": v(6.7, 4.89) * mm});
            skLineSegment(sketch, "E2005", {"start": v(6.7, 4.89) * mm, "end": v(6.98, 4.32) * mm});
            skLineSegment(sketch, "E2006", {"start": v(6.98, 4.32) * mm, "end": v(7.24, 3.74) * mm});
            skLineSegment(sketch, "E2007", {"start": v(7.24, 3.74) * mm, "end": v(7.45, 3.14) * mm});
            skLineSegment(sketch, "E2008", {"start": v(7.45, 3.14) * mm, "end": v(7.63, 2.52) * mm});
            skLineSegment(sketch, "E2009", {"start": v(7.63, 2.52) * mm, "end": v(7.66, 2.4) * mm});
            skLineSegment(sketch, "E2010", {"start": v(7.66, 2.4) * mm, "end": v(40.46, 2.5) * mm});
            skLineSegment(sketch, "E2011", {"start": v(0.49, -42.66) * mm, "end": v(3.16, -42.4) * mm});
            skLineSegment(sketch, "E2012", {"start": v(3.16, -42.4) * mm, "end": v(5.81, -41.98) * mm});
            skLineSegment(sketch, "E2013", {"start": v(5.81, -41.98) * mm, "end": v(8.43, -41.4) * mm});
            skLineSegment(sketch, "E2014", {"start": v(8.43, -41.4) * mm, "end": v(11, -40.65) * mm});
            skLineSegment(sketch, "E2015", {"start": v(11, -40.65) * mm, "end": v(13.54, -39.74) * mm});
            skLineSegment(sketch, "E2016", {"start": v(13.54, -39.74) * mm, "end": v(16, -38.67) * mm});
            skLineSegment(sketch, "E2017", {"start": v(16, -38.67) * mm, "end": v(18.4, -37.45) * mm});
            skLineSegment(sketch, "E2018", {"start": v(18.4, -37.45) * mm, "end": v(20.7, -36.09) * mm});
            skLineSegment(sketch, "E2019", {"start": v(20.7, -36.09) * mm, "end": v(22.92, -34.58) * mm});
            skLineSegment(sketch, "E2020", {"start": v(22.92, -34.58) * mm, "end": v(25.05, -32.93) * mm});
            skLineSegment(sketch, "E2021", {"start": v(25.05, -32.93) * mm, "end": v(27.06, -31.16) * mm});
            skLineSegment(sketch, "E2022", {"start": v(27.06, -31.16) * mm, "end": v(28.96, -29.26) * mm});
            skLineSegment(sketch, "E2023", {"start": v(28.96, -29.26) * mm, "end": v(30.73, -27.24) * mm});
            skLineSegment(sketch, "E2024", {"start": v(30.73, -27.24) * mm, "end": v(32.38, -25.12) * mm});
            skLineSegment(sketch, "E2025", {"start": v(32.38, -25.12) * mm, "end": v(33.89, -22.9) * mm});
            skLineSegment(sketch, "E2026", {"start": v(33.89, -22.9) * mm, "end": v(35.26, -20.6) * mm});
            skLineSegment(sketch, "E2027", {"start": v(35.26, -20.6) * mm, "end": v(36.48, -18.2) * mm});
            skLineSegment(sketch, "E2028", {"start": v(36.48, -18.2) * mm, "end": v(37.54, -15.73) * mm});
            skLineSegment(sketch, "E2029", {"start": v(37.54, -15.73) * mm, "end": v(38.45, -13.2) * mm});
            skLineSegment(sketch, "E2030", {"start": v(38.45, -13.2) * mm, "end": v(39.2, -10.63) * mm});
            skLineSegment(sketch, "E2031", {"start": v(39.2, -10.63) * mm, "end": v(39.79, -8) * mm});
            skLineSegment(sketch, "E2032", {"start": v(39.79, -8) * mm, "end": v(40.2, -5.36) * mm});
            skLineSegment(sketch, "E2033", {"start": v(40.2, -5.36) * mm, "end": v(40.46, -2.68) * mm});
            skLineSegment(sketch, "E2034", {"start": v(40.46, -2.68) * mm, "end": v(40.46, -2.5) * mm});
            skLineSegment(sketch, "E2035", {"start": v(40.46, -2.5) * mm, "end": v(7.66, -2.4) * mm});
            skLineSegment(sketch, "E2036", {"start": v(7.66, -2.4) * mm, "end": v(7.63, -2.52) * mm});
            skLineSegment(sketch, "E2037", {"start": v(7.63, -2.52) * mm, "end": v(7.45, -3.14) * mm});
            skLineSegment(sketch, "E2038", {"start": v(7.45, -3.14) * mm, "end": v(7.24, -3.74) * mm});
            skLineSegment(sketch, "E2039", {"start": v(7.24, -3.74) * mm, "end": v(6.98, -4.32) * mm});
            skLineSegment(sketch, "E2040", {"start": v(6.98, -4.32) * mm, "end": v(6.7, -4.89) * mm});
            skLineSegment(sketch, "E2041", {"start": v(6.7, -4.89) * mm, "end": v(6.37, -5.44) * mm});
            skLineSegment(sketch, "E2042", {"start": v(6.37, -5.44) * mm, "end": v(6.01, -5.97) * mm});
            skLineSegment(sketch, "E2043", {"start": v(6.01, -5.97) * mm, "end": v(5.62, -6.47) * mm});
            skLineSegment(sketch, "E2044", {"start": v(5.62, -6.47) * mm, "end": v(5.2, -6.95) * mm});
            skLineSegment(sketch, "E2045", {"start": v(5.2, -6.95) * mm, "end": v(4.75, -7.4) * mm});
            skLineSegment(sketch, "E2046", {"start": v(4.75, -7.4) * mm, "end": v(4.27, -7.82) * mm});
            skLineSegment(sketch, "E2047", {"start": v(4.27, -7.82) * mm, "end": v(3.77, -8.21) * mm});
            skLineSegment(sketch, "E2048", {"start": v(3.77, -8.21) * mm, "end": v(3.24, -8.57) * mm});
            skLineSegment(sketch, "E2049", {"start": v(3.24, -8.57) * mm, "end": v(2.7, -8.9) * mm});
            skLineSegment(sketch, "E2050", {"start": v(2.7, -8.9) * mm, "end": v(2.12, -9.18) * mm});
            skLineSegment(sketch, "E2051", {"start": v(2.12, -9.18) * mm, "end": v(1.54, -9.44) * mm});
            skLineSegment(sketch, "E2052", {"start": v(1.54, -9.44) * mm, "end": v(0.94, -9.65) * mm});
            skLineSegment(sketch, "E2053", {"start": v(0.94, -9.65) * mm, "end": v(0.33, -9.83) * mm});
            skLineSegment(sketch, "E2054", {"start": v(0.33, -9.83) * mm, "end": v(0.2, -9.86) * mm});
            skLineSegment(sketch, "E2055", {"start": v(0.2, -9.86) * mm, "end": v(0.3, -42.66) * mm});
            skLineSegment(sketch, "E2056", {"start": v(0.3, -42.66) * mm, "end": v(0.49, -42.66) * mm});
            skLineSegment(sketch, "E2057", {"start": v(-4.6, -9.86) * mm, "end": v(-4.72, -9.83) * mm});
            skLineSegment(sketch, "E2058", {"start": v(-4.72, -9.83) * mm, "end": v(-5.33, -9.65) * mm});
            skLineSegment(sketch, "E2059", {"start": v(-5.33, -9.65) * mm, "end": v(-5.93, -9.44) * mm});
            skLineSegment(sketch, "E2060", {"start": v(-5.93, -9.44) * mm, "end": v(-6.52, -9.18) * mm});
            skLineSegment(sketch, "E2061", {"start": v(-6.52, -9.18) * mm, "end": v(-7.09, -8.9) * mm});
            skLineSegment(sketch, "E2062", {"start": v(-7.09, -8.9) * mm, "end": v(-7.64, -8.57) * mm});
            skLineSegment(sketch, "E2063", {"start": v(-7.64, -8.57) * mm, "end": v(-8.16, -8.21) * mm});
            skLineSegment(sketch, "E2064", {"start": v(-8.16, -8.21) * mm, "end": v(-8.67, -7.82) * mm});
            skLineSegment(sketch, "E2065", {"start": v(-8.67, -7.82) * mm, "end": v(-9.15, -7.4) * mm});
            skLineSegment(sketch, "E2066", {"start": v(-9.15, -7.4) * mm, "end": v(-9.6, -6.95) * mm});
            skLineSegment(sketch, "E2067", {"start": v(-9.6, -6.95) * mm, "end": v(-10.02, -6.47) * mm});
            skLineSegment(sketch, "E2068", {"start": v(-10.02, -6.47) * mm, "end": v(-10.4, -5.97) * mm});
            skLineSegment(sketch, "E2069", {"start": v(-10.4, -5.97) * mm, "end": v(-10.77, -5.44) * mm});
            skLineSegment(sketch, "E2070", {"start": v(-10.77, -5.44) * mm, "end": v(-11.1, -4.89) * mm});
            skLineSegment(sketch, "E2071", {"start": v(-11.1, -4.89) * mm, "end": v(-11.38, -4.32) * mm});
            skLineSegment(sketch, "E2072", {"start": v(-11.38, -4.32) * mm, "end": v(-11.64, -3.74) * mm});
            skLineSegment(sketch, "E2073", {"start": v(-11.64, -3.74) * mm, "end": v(-11.85, -3.14) * mm});
            skLineSegment(sketch, "E2074", {"start": v(-11.85, -3.14) * mm, "end": v(-12.03, -2.52) * mm});
            skLineSegment(sketch, "E2075", {"start": v(-12.03, -2.52) * mm, "end": v(-12.06, -2.4) * mm});
            skLineSegment(sketch, "E2076", {"start": v(-12.06, -2.4) * mm, "end": v(-44.86, -2.5) * mm});
            skLineSegment(sketch, "E2077", {"start": v(-44.86, -2.5) * mm, "end": v(-44.86, -2.68) * mm});
            skLineSegment(sketch, "E2078", {"start": v(-44.86, -2.68) * mm, "end": v(-44.6, -5.36) * mm});
            skLineSegment(sketch, "E2079", {"start": v(-44.6, -5.36) * mm, "end": v(-44.18, -8) * mm});
            skLineSegment(sketch, "E2080", {"start": v(-44.18, -8) * mm, "end": v(-43.6, -10.63) * mm});
            skLineSegment(sketch, "E2081", {"start": v(-43.6, -10.63) * mm, "end": v(-42.85, -13.2) * mm});
            skLineSegment(sketch, "E2082", {"start": v(-42.85, -13.2) * mm, "end": v(-41.94, -15.73) * mm});
            skLineSegment(sketch, "E2083", {"start": v(-41.94, -15.73) * mm, "end": v(-40.87, -18.2) * mm});
            skLineSegment(sketch, "E2084", {"start": v(-40.87, -18.2) * mm, "end": v(-39.65, -20.6) * mm});
            skLineSegment(sketch, "E2085", {"start": v(-39.65, -20.6) * mm, "end": v(-38.29, -22.9) * mm});
            skLineSegment(sketch, "E2086", {"start": v(-38.29, -22.9) * mm, "end": v(-36.78, -25.12) * mm});
            skLineSegment(sketch, "E2087", {"start": v(-36.78, -25.12) * mm, "end": v(-35.13, -27.24) * mm});
            skLineSegment(sketch, "E2088", {"start": v(-35.13, -27.24) * mm, "end": v(-33.36, -29.26) * mm});
            skLineSegment(sketch, "E2089", {"start": v(-33.36, -29.26) * mm, "end": v(-31.46, -31.16) * mm});
            skLineSegment(sketch, "E2090", {"start": v(-31.46, -31.16) * mm, "end": v(-29.44, -32.93) * mm});
            skLineSegment(sketch, "E2091", {"start": v(-29.44, -32.93) * mm, "end": v(-27.32, -34.58) * mm});
            skLineSegment(sketch, "E2092", {"start": v(-27.32, -34.58) * mm, "end": v(-25.1, -36.09) * mm});
            skLineSegment(sketch, "E2093", {"start": v(-25.1, -36.09) * mm, "end": v(-22.79, -37.45) * mm});
            skLineSegment(sketch, "E2094", {"start": v(-22.79, -37.45) * mm, "end": v(-20.4, -38.67) * mm});
            skLineSegment(sketch, "E2095", {"start": v(-20.4, -38.67) * mm, "end": v(-17.93, -39.74) * mm});
            skLineSegment(sketch, "E2096", {"start": v(-17.93, -39.74) * mm, "end": v(-15.4, -40.65) * mm});
            skLineSegment(sketch, "E2097", {"start": v(-15.4, -40.65) * mm, "end": v(-12.83, -41.4) * mm});
            skLineSegment(sketch, "E2098", {"start": v(-12.83, -41.4) * mm, "end": v(-10.2, -41.98) * mm});
            skLineSegment(sketch, "E2099", {"start": v(-10.2, -41.98) * mm, "end": v(-7.56, -42.4) * mm});
            skLineSegment(sketch, "E2100", {"start": v(-7.56, -42.4) * mm, "end": v(-4.88, -42.66) * mm});
            skLineSegment(sketch, "E2101", {"start": v(-4.88, -42.66) * mm, "end": v(-4.7, -42.66) * mm});
            skLineSegment(sketch, "E2102", {"start": v(-4.7, -42.66) * mm, "end": v(-4.6, -9.86) * mm});
            skCircle(sketch, "E2103", {"center": v(-2.2, 0) * mm, "radius": 4.5 * mm});
            skSolve(sketch);
        }
        {
            var Q0;
            Q0=makeQuery(id+"F0.imprint","IMPRINT",FACE,{"disambiguationData":[TD([[makeQuery(id+"F0.imprint","IMPRINT",EDGE,{"derivedFrom":sQuery(id+"F0.wireOp",EDGE,"E0")}),1.0]])]});
            extrude(context, id + "F1", {"entities" : qUnion([Q0]), "depth" : 5 * mm});
        }
        {
            var Q0;
            Q0=makeQuery(id+"F1.opExtrude","CAP_FACE",FACE,{"disambiguationData":[OSD([sQuery(id+"F0.wireOp",EDGE,"E0"),sQuery(id+"F0.wireOp",EDGE,"E1"),sQuery(id+"F0.wireOp",EDGE,"E2"),sQuery(id+"F0.wireOp",EDGE,"E3"),sQuery(id+"F0.wireOp",EDGE,"E4"),sQuery(id+"F0.wireOp",EDGE,"E5"),sQuery(id+"F0.wireOp",EDGE,"E6"),sQuery(id+"F0.wireOp",EDGE,"E7"),sQuery(id+"F0.wireOp",EDGE,"E8"),sQuery(id+"F0.wireOp",EDGE,"E9"),sQuery(id+"F0.wireOp",EDGE,"E10"),sQuery(id+"F0.wireOp",EDGE,"E11"),sQuery(id+"F0.wireOp",EDGE,"E12"),sQuery(id+"F0.wireOp",EDGE,"E13"),sQuery(id+"F0.wireOp",EDGE,"E14"),sQuery(id+"F0.wireOp",EDGE,"E15"),sQuery(id+"F0.wireOp",EDGE,"E16"),sQuery(id+"F0.wireOp",EDGE,"E17"),sQuery(id+"F0.wireOp",EDGE,"E18"),sQuery(id+"F0.wireOp",EDGE,"E19"),sQuery(id+"F0.wireOp",EDGE,"E20"),sQuery(id+"F0.wireOp",EDGE,"E21"),sQuery(id+"F0.wireOp",EDGE,"E22"),sQuery(id+"F0.wireOp",EDGE,"E23"),sQuery(id+"F0.wireOp",EDGE,"E24"),sQuery(id+"F0.wireOp",EDGE,"E25"),sQuery(id+"F0.wireOp",EDGE,"E26"),sQuery(id+"F0.wireOp",EDGE,"E27"),sQuery(id+"F0.wireOp",EDGE,"E28"),sQuery(id+"F0.wireOp",EDGE,"E29"),sQuery(id+"F0.wireOp",EDGE,"E30"),sQuery(id+"F0.wireOp",EDGE,"E31"),sQuery(id+"F0.wireOp",EDGE,"E32"),sQuery(id+"F0.wireOp",EDGE,"E33"),sQuery(id+"F0.wireOp",EDGE,"E34"),sQuery(id+"F0.wireOp",EDGE,"E35"),sQuery(id+"F0.wireOp",EDGE,"E36"),sQuery(id+"F0.wireOp",EDGE,"E37"),sQuery(id+"F0.wireOp",EDGE,"E38"),sQuery(id+"F0.wireOp",EDGE,"E39"),sQuery(id+"F0.wireOp",EDGE,"E40"),sQuery(id+"F0.wireOp",EDGE,"E41"),sQuery(id+"F0.wireOp",EDGE,"E42"),sQuery(id+"F0.wireOp",EDGE,"E43"),sQuery(id+"F0.wireOp",EDGE,"E44"),sQuery(id+"F0.wireOp",EDGE,"E45"),sQuery(id+"F0.wireOp",EDGE,"E46"),sQuery(id+"F0.wireOp",EDGE,"E47"),sQuery(id+"F0.wireOp",EDGE,"E48"),sQuery(id+"F0.wireOp",EDGE,"E49"),sQuery(id+"F0.wireOp",EDGE,"E50"),sQuery(id+"F0.wireOp",EDGE,"E51"),sQuery(id+"F0.wireOp",EDGE,"E52"),sQuery(id+"F0.wireOp",EDGE,"E53"),sQuery(id+"F0.wireOp",EDGE,"E54"),sQuery(id+"F0.wireOp",EDGE,"E55"),sQuery(id+"F0.wireOp",EDGE,"E56"),sQuery(id+"F0.wireOp",EDGE,"E57"),sQuery(id+"F0.wireOp",EDGE,"E58"),sQuery(id+"F0.wireOp",EDGE,"E59"),sQuery(id+"F0.wireOp",EDGE,"E60"),sQuery(id+"F0.wireOp",EDGE,"E61"),sQuery(id+"F0.wireOp",EDGE,"E62"),sQuery(id+"F0.wireOp",EDGE,"E63"),sQuery(id+"F0.wireOp",EDGE,"E64"),sQuery(id+"F0.wireOp",EDGE,"E65"),sQuery(id+"F0.wireOp",EDGE,"E66"),sQuery(id+"F0.wireOp",EDGE,"E67"),sQuery(id+"F0.wireOp",EDGE,"E68"),sQuery(id+"F0.wireOp",EDGE,"E69"),sQuery(id+"F0.wireOp",EDGE,"E70"),sQuery(id+"F0.wireOp",EDGE,"E71"),sQuery(id+"F0.wireOp",EDGE,"E72"),sQuery(id+"F0.wireOp",EDGE,"E73"),sQuery(id+"F0.wireOp",EDGE,"E74"),sQuery(id+"F0.wireOp",EDGE,"E75"),sQuery(id+"F0.wireOp",EDGE,"E76"),sQuery(id+"F0.wireOp",EDGE,"E77"),sQuery(id+"F0.wireOp",EDGE,"E78"),sQuery(id+"F0.wireOp",EDGE,"E79"),sQuery(id+"F0.wireOp",EDGE,"E80"),sQuery(id+"F0.wireOp",EDGE,"E81"),sQuery(id+"F0.wireOp",EDGE,"E82"),sQuery(id+"F0.wireOp",EDGE,"E83"),sQuery(id+"F0.wireOp",EDGE,"E84"),sQuery(id+"F0.wireOp",EDGE,"E85"),sQuery(id+"F0.wireOp",EDGE,"E86"),sQuery(id+"F0.wireOp",EDGE,"E87"),sQuery(id+"F0.wireOp",EDGE,"E88"),sQuery(id+"F0.wireOp",EDGE,"E89"),sQuery(id+"F0.wireOp",EDGE,"E90"),sQuery(id+"F0.wireOp",EDGE,"E91"),sQuery(id+"F0.wireOp",EDGE,"E92"),sQuery(id+"F0.wireOp",EDGE,"E93"),sQuery(id+"F0.wireOp",EDGE,"E94"),sQuery(id+"F0.wireOp",EDGE,"E95"),sQuery(id+"F0.wireOp",EDGE,"E96"),sQuery(id+"F0.wireOp",EDGE,"E97"),sQuery(id+"F0.wireOp",EDGE,"E98"),sQuery(id+"F0.wireOp",EDGE,"E99"),sQuery(id+"F0.wireOp",EDGE,"E100"),sQuery(id+"F0.wireOp",EDGE,"E101"),sQuery(id+"F0.wireOp",EDGE,"E102"),sQuery(id+"F0.wireOp",EDGE,"E103"),sQuery(id+"F0.wireOp",EDGE,"E104"),sQuery(id+"F0.wireOp",EDGE,"E105"),sQuery(id+"F0.wireOp",EDGE,"E106"),sQuery(id+"F0.wireOp",EDGE,"E107"),sQuery(id+"F0.wireOp",EDGE,"E108"),sQuery(id+"F0.wireOp",EDGE,"E109"),sQuery(id+"F0.wireOp",EDGE,"E110"),sQuery(id+"F0.wireOp",EDGE,"E111"),sQuery(id+"F0.wireOp",EDGE,"E112"),sQuery(id+"F0.wireOp",EDGE,"E113"),sQuery(id+"F0.wireOp",EDGE,"E114"),sQuery(id+"F0.wireOp",EDGE,"E115"),sQuery(id+"F0.wireOp",EDGE,"E116"),sQuery(id+"F0.wireOp",EDGE,"E117"),sQuery(id+"F0.wireOp",EDGE,"E118"),sQuery(id+"F0.wireOp",EDGE,"E119"),sQuery(id+"F0.wireOp",EDGE,"E120"),sQuery(id+"F0.wireOp",EDGE,"E121"),sQuery(id+"F0.wireOp",EDGE,"E122"),sQuery(id+"F0.wireOp",EDGE,"E123"),sQuery(id+"F0.wireOp",EDGE,"E124"),sQuery(id+"F0.wireOp",EDGE,"E125"),sQuery(id+"F0.wireOp",EDGE,"E126"),sQuery(id+"F0.wireOp",EDGE,"E127"),sQuery(id+"F0.wireOp",EDGE,"E128"),sQuery(id+"F0.wireOp",EDGE,"E129"),sQuery(id+"F0.wireOp",EDGE,"E130"),sQuery(id+"F0.wireOp",EDGE,"E131"),sQuery(id+"F0.wireOp",EDGE,"E132"),sQuery(id+"F0.wireOp",EDGE,"E133"),sQuery(id+"F0.wireOp",EDGE,"E134"),sQuery(id+"F0.wireOp",EDGE,"E135"),sQuery(id+"F0.wireOp",EDGE,"E136"),sQuery(id+"F0.wireOp",EDGE,"E137"),sQuery(id+"F0.wireOp",EDGE,"E138"),sQuery(id+"F0.wireOp",EDGE,"E139"),sQuery(id+"F0.wireOp",EDGE,"E140"),sQuery(id+"F0.wireOp",EDGE,"E141"),sQuery(id+"F0.wireOp",EDGE,"E142"),sQuery(id+"F0.wireOp",EDGE,"E143"),sQuery(id+"F0.wireOp",EDGE,"E144"),sQuery(id+"F0.wireOp",EDGE,"E145"),sQuery(id+"F0.wireOp",EDGE,"E146"),sQuery(id+"F0.wireOp",EDGE,"E147"),sQuery(id+"F0.wireOp",EDGE,"E148"),sQuery(id+"F0.wireOp",EDGE,"E149"),sQuery(id+"F0.wireOp",EDGE,"E150"),sQuery(id+"F0.wireOp",EDGE,"E151"),sQuery(id+"F0.wireOp",EDGE,"E152"),sQuery(id+"F0.wireOp",EDGE,"E153"),sQuery(id+"F0.wireOp",EDGE,"E154"),sQuery(id+"F0.wireOp",EDGE,"E155"),sQuery(id+"F0.wireOp",EDGE,"E156"),sQuery(id+"F0.wireOp",EDGE,"E157"),sQuery(id+"F0.wireOp",EDGE,"E158"),sQuery(id+"F0.wireOp",EDGE,"E159"),sQuery(id+"F0.wireOp",EDGE,"E160"),sQuery(id+"F0.wireOp",EDGE,"E161"),sQuery(id+"F0.wireOp",EDGE,"E162"),sQuery(id+"F0.wireOp",EDGE,"E163"),sQuery(id+"F0.wireOp",EDGE,"E164"),sQuery(id+"F0.wireOp",EDGE,"E165"),sQuery(id+"F0.wireOp",EDGE,"E166"),sQuery(id+"F0.wireOp",EDGE,"E167"),sQuery(id+"F0.wireOp",EDGE,"E168"),sQuery(id+"F0.wireOp",EDGE,"E169"),sQuery(id+"F0.wireOp",EDGE,"E170"),sQuery(id+"F0.wireOp",EDGE,"E171"),sQuery(id+"F0.wireOp",EDGE,"E172"),sQuery(id+"F0.wireOp",EDGE,"E173"),sQuery(id+"F0.wireOp",EDGE,"E174"),sQuery(id+"F0.wireOp",EDGE,"E175"),sQuery(id+"F0.wireOp",EDGE,"E176"),sQuery(id+"F0.wireOp",EDGE,"E177"),sQuery(id+"F0.wireOp",EDGE,"E178"),sQuery(id+"F0.wireOp",EDGE,"E179"),sQuery(id+"F0.wireOp",EDGE,"E180"),sQuery(id+"F0.wireOp",EDGE,"E181"),sQuery(id+"F0.wireOp",EDGE,"E182"),sQuery(id+"F0.wireOp",EDGE,"E183"),sQuery(id+"F0.wireOp",EDGE,"E184"),sQuery(id+"F0.wireOp",EDGE,"E185"),sQuery(id+"F0.wireOp",EDGE,"E186"),sQuery(id+"F0.wireOp",EDGE,"E187"),sQuery(id+"F0.wireOp",EDGE,"E188"),sQuery(id+"F0.wireOp",EDGE,"E189"),sQuery(id+"F0.wireOp",EDGE,"E190"),sQuery(id+"F0.wireOp",EDGE,"E191"),sQuery(id+"F0.wireOp",EDGE,"E192"),sQuery(id+"F0.wireOp",EDGE,"E193"),sQuery(id+"F0.wireOp",EDGE,"E194"),sQuery(id+"F0.wireOp",EDGE,"E195"),sQuery(id+"F0.wireOp",EDGE,"E196"),sQuery(id+"F0.wireOp",EDGE,"E197"),sQuery(id+"F0.wireOp",EDGE,"E198"),sQuery(id+"F0.wireOp",EDGE,"E199"),sQuery(id+"F0.wireOp",EDGE,"E200"),sQuery(id+"F0.wireOp",EDGE,"E201"),sQuery(id+"F0.wireOp",EDGE,"E202"),sQuery(id+"F0.wireOp",EDGE,"E203"),sQuery(id+"F0.wireOp",EDGE,"E204"),sQuery(id+"F0.wireOp",EDGE,"E205"),sQuery(id+"F0.wireOp",EDGE,"E206"),sQuery(id+"F0.wireOp",EDGE,"E207"),sQuery(id+"F0.wireOp",EDGE,"E208"),sQuery(id+"F0.wireOp",EDGE,"E209"),sQuery(id+"F0.wireOp",EDGE,"E210"),sQuery(id+"F0.wireOp",EDGE,"E211"),sQuery(id+"F0.wireOp",EDGE,"E212"),sQuery(id+"F0.wireOp",EDGE,"E213"),sQuery(id+"F0.wireOp",EDGE,"E214"),sQuery(id+"F0.wireOp",EDGE,"E215"),sQuery(id+"F0.wireOp",EDGE,"E216"),sQuery(id+"F0.wireOp",EDGE,"E217"),sQuery(id+"F0.wireOp",EDGE,"E218"),sQuery(id+"F0.wireOp",EDGE,"E219"),sQuery(id+"F0.wireOp",EDGE,"E220"),sQuery(id+"F0.wireOp",EDGE,"E221"),sQuery(id+"F0.wireOp",EDGE,"E222"),sQuery(id+"F0.wireOp",EDGE,"E223"),sQuery(id+"F0.wireOp",EDGE,"E224"),sQuery(id+"F0.wireOp",EDGE,"E225"),sQuery(id+"F0.wireOp",EDGE,"E226"),sQuery(id+"F0.wireOp",EDGE,"E227"),sQuery(id+"F0.wireOp",EDGE,"E228"),sQuery(id+"F0.wireOp",EDGE,"E229"),sQuery(id+"F0.wireOp",EDGE,"E230"),sQuery(id+"F0.wireOp",EDGE,"E231"),sQuery(id+"F0.wireOp",EDGE,"E232"),sQuery(id+"F0.wireOp",EDGE,"E233"),sQuery(id+"F0.wireOp",EDGE,"E234"),sQuery(id+"F0.wireOp",EDGE,"E235"),sQuery(id+"F0.wireOp",EDGE,"E236"),sQuery(id+"F0.wireOp",EDGE,"E237"),sQuery(id+"F0.wireOp",EDGE,"E238"),sQuery(id+"F0.wireOp",EDGE,"E239"),sQuery(id+"F0.wireOp",EDGE,"E240"),sQuery(id+"F0.wireOp",EDGE,"E241"),sQuery(id+"F0.wireOp",EDGE,"E242"),sQuery(id+"F0.wireOp",EDGE,"E243"),sQuery(id+"F0.wireOp",EDGE,"E244"),sQuery(id+"F0.wireOp",EDGE,"E245"),sQuery(id+"F0.wireOp",EDGE,"E246"),sQuery(id+"F0.wireOp",EDGE,"E247"),sQuery(id+"F0.wireOp",EDGE,"E248"),sQuery(id+"F0.wireOp",EDGE,"E249"),sQuery(id+"F0.wireOp",EDGE,"E250"),sQuery(id+"F0.wireOp",EDGE,"E251"),sQuery(id+"F0.wireOp",EDGE,"E252"),sQuery(id+"F0.wireOp",EDGE,"E253"),sQuery(id+"F0.wireOp",EDGE,"E254"),sQuery(id+"F0.wireOp",EDGE,"E255"),sQuery(id+"F0.wireOp",EDGE,"E256"),sQuery(id+"F0.wireOp",EDGE,"E257"),sQuery(id+"F0.wireOp",EDGE,"E258"),sQuery(id+"F0.wireOp",EDGE,"E259"),sQuery(id+"F0.wireOp",EDGE,"E260"),sQuery(id+"F0.wireOp",EDGE,"E261"),sQuery(id+"F0.wireOp",EDGE,"E262"),sQuery(id+"F0.wireOp",EDGE,"E263"),sQuery(id+"F0.wireOp",EDGE,"E264"),sQuery(id+"F0.wireOp",EDGE,"E265"),sQuery(id+"F0.wireOp",EDGE,"E266"),sQuery(id+"F0.wireOp",EDGE,"E267"),sQuery(id+"F0.wireOp",EDGE,"E268"),sQuery(id+"F0.wireOp",EDGE,"E269"),sQuery(id+"F0.wireOp",EDGE,"E270"),sQuery(id+"F0.wireOp",EDGE,"E271"),sQuery(id+"F0.wireOp",EDGE,"E272"),sQuery(id+"F0.wireOp",EDGE,"E273"),sQuery(id+"F0.wireOp",EDGE,"E274"),sQuery(id+"F0.wireOp",EDGE,"E275"),sQuery(id+"F0.wireOp",EDGE,"E276"),sQuery(id+"F0.wireOp",EDGE,"E277"),sQuery(id+"F0.wireOp",EDGE,"E278"),sQuery(id+"F0.wireOp",EDGE,"E279"),sQuery(id+"F0.wireOp",EDGE,"E280"),sQuery(id+"F0.wireOp",EDGE,"E281"),sQuery(id+"F0.wireOp",EDGE,"E282"),sQuery(id+"F0.wireOp",EDGE,"E283"),sQuery(id+"F0.wireOp",EDGE,"E284"),sQuery(id+"F0.wireOp",EDGE,"E285"),sQuery(id+"F0.wireOp",EDGE,"E286"),sQuery(id+"F0.wireOp",EDGE,"E287"),sQuery(id+"F0.wireOp",EDGE,"E288"),sQuery(id+"F0.wireOp",EDGE,"E289"),sQuery(id+"F0.wireOp",EDGE,"E290"),sQuery(id+"F0.wireOp",EDGE,"E291"),sQuery(id+"F0.wireOp",EDGE,"E292"),sQuery(id+"F0.wireOp",EDGE,"E293"),sQuery(id+"F0.wireOp",EDGE,"E294"),sQuery(id+"F0.wireOp",EDGE,"E295"),sQuery(id+"F0.wireOp",EDGE,"E296"),sQuery(id+"F0.wireOp",EDGE,"E297"),sQuery(id+"F0.wireOp",EDGE,"E298"),sQuery(id+"F0.wireOp",EDGE,"E299"),sQuery(id+"F0.wireOp",EDGE,"E300"),sQuery(id+"F0.wireOp",EDGE,"E301"),sQuery(id+"F0.wireOp",EDGE,"E302"),sQuery(id+"F0.wireOp",EDGE,"E303"),sQuery(id+"F0.wireOp",EDGE,"E304"),sQuery(id+"F0.wireOp",EDGE,"E305"),sQuery(id+"F0.wireOp",EDGE,"E306"),sQuery(id+"F0.wireOp",EDGE,"E307"),sQuery(id+"F0.wireOp",EDGE,"E308"),sQuery(id+"F0.wireOp",EDGE,"E309"),sQuery(id+"F0.wireOp",EDGE,"E310"),sQuery(id+"F0.wireOp",EDGE,"E311"),sQuery(id+"F0.wireOp",EDGE,"E312"),sQuery(id+"F0.wireOp",EDGE,"E313"),sQuery(id+"F0.wireOp",EDGE,"E314"),sQuery(id+"F0.wireOp",EDGE,"E315"),sQuery(id+"F0.wireOp",EDGE,"E316"),sQuery(id+"F0.wireOp",EDGE,"E317"),sQuery(id+"F0.wireOp",EDGE,"E318"),sQuery(id+"F0.wireOp",EDGE,"E319"),sQuery(id+"F0.wireOp",EDGE,"E320"),sQuery(id+"F0.wireOp",EDGE,"E321"),sQuery(id+"F0.wireOp",EDGE,"E322"),sQuery(id+"F0.wireOp",EDGE,"E323"),sQuery(id+"F0.wireOp",EDGE,"E324"),sQuery(id+"F0.wireOp",EDGE,"E325"),sQuery(id+"F0.wireOp",EDGE,"E326"),sQuery(id+"F0.wireOp",EDGE,"E327"),sQuery(id+"F0.wireOp",EDGE,"E328"),sQuery(id+"F0.wireOp",EDGE,"E329"),sQuery(id+"F0.wireOp",EDGE,"E330"),sQuery(id+"F0.wireOp",EDGE,"E331"),sQuery(id+"F0.wireOp",EDGE,"E332"),sQuery(id+"F0.wireOp",EDGE,"E333"),sQuery(id+"F0.wireOp",EDGE,"E334"),sQuery(id+"F0.wireOp",EDGE,"E335"),sQuery(id+"F0.wireOp",EDGE,"E336"),sQuery(id+"F0.wireOp",EDGE,"E337"),sQuery(id+"F0.wireOp",EDGE,"E338"),sQuery(id+"F0.wireOp",EDGE,"E339"),sQuery(id+"F0.wireOp",EDGE,"E340"),sQuery(id+"F0.wireOp",EDGE,"E341"),sQuery(id+"F0.wireOp",EDGE,"E342"),sQuery(id+"F0.wireOp",EDGE,"E343"),sQuery(id+"F0.wireOp",EDGE,"E344"),sQuery(id+"F0.wireOp",EDGE,"E345"),sQuery(id+"F0.wireOp",EDGE,"E346"),sQuery(id+"F0.wireOp",EDGE,"E347"),sQuery(id+"F0.wireOp",EDGE,"E348"),sQuery(id+"F0.wireOp",EDGE,"E349"),sQuery(id+"F0.wireOp",EDGE,"E350"),sQuery(id+"F0.wireOp",EDGE,"E351"),sQuery(id+"F0.wireOp",EDGE,"E352"),sQuery(id+"F0.wireOp",EDGE,"E353"),sQuery(id+"F0.wireOp",EDGE,"E354"),sQuery(id+"F0.wireOp",EDGE,"E355"),sQuery(id+"F0.wireOp",EDGE,"E356"),sQuery(id+"F0.wireOp",EDGE,"E357"),sQuery(id+"F0.wireOp",EDGE,"E358"),sQuery(id+"F0.wireOp",EDGE,"E359"),sQuery(id+"F0.wireOp",EDGE,"E360"),sQuery(id+"F0.wireOp",EDGE,"E361"),sQuery(id+"F0.wireOp",EDGE,"E362"),sQuery(id+"F0.wireOp",EDGE,"E363"),sQuery(id+"F0.wireOp",EDGE,"E364"),sQuery(id+"F0.wireOp",EDGE,"E365"),sQuery(id+"F0.wireOp",EDGE,"E366"),sQuery(id+"F0.wireOp",EDGE,"E367"),sQuery(id+"F0.wireOp",EDGE,"E368"),sQuery(id+"F0.wireOp",EDGE,"E369"),sQuery(id+"F0.wireOp",EDGE,"E370"),sQuery(id+"F0.wireOp",EDGE,"E371"),sQuery(id+"F0.wireOp",EDGE,"E372"),sQuery(id+"F0.wireOp",EDGE,"E373"),sQuery(id+"F0.wireOp",EDGE,"E374"),sQuery(id+"F0.wireOp",EDGE,"E375"),sQuery(id+"F0.wireOp",EDGE,"E376"),sQuery(id+"F0.wireOp",EDGE,"E377"),sQuery(id+"F0.wireOp",EDGE,"E378"),sQuery(id+"F0.wireOp",EDGE,"E379"),sQuery(id+"F0.wireOp",EDGE,"E380"),sQuery(id+"F0.wireOp",EDGE,"E381"),sQuery(id+"F0.wireOp",EDGE,"E382"),sQuery(id+"F0.wireOp",EDGE,"E383"),sQuery(id+"F0.wireOp",EDGE,"E384"),sQuery(id+"F0.wireOp",EDGE,"E385"),sQuery(id+"F0.wireOp",EDGE,"E386"),sQuery(id+"F0.wireOp",EDGE,"E387"),sQuery(id+"F0.wireOp",EDGE,"E388"),sQuery(id+"F0.wireOp",EDGE,"E389"),sQuery(id+"F0.wireOp",EDGE,"E390"),sQuery(id+"F0.wireOp",EDGE,"E391"),sQuery(id+"F0.wireOp",EDGE,"E392"),sQuery(id+"F0.wireOp",EDGE,"E393"),sQuery(id+"F0.wireOp",EDGE,"E394"),sQuery(id+"F0.wireOp",EDGE,"E395"),sQuery(id+"F0.wireOp",EDGE,"E396"),sQuery(id+"F0.wireOp",EDGE,"E397"),sQuery(id+"F0.wireOp",EDGE,"E398"),sQuery(id+"F0.wireOp",EDGE,"E399"),sQuery(id+"F0.wireOp",EDGE,"E400"),sQuery(id+"F0.wireOp",EDGE,"E401"),sQuery(id+"F0.wireOp",EDGE,"E402"),sQuery(id+"F0.wireOp",EDGE,"E403"),sQuery(id+"F0.wireOp",EDGE,"E404"),sQuery(id+"F0.wireOp",EDGE,"E405"),sQuery(id+"F0.wireOp",EDGE,"E406"),sQuery(id+"F0.wireOp",EDGE,"E407"),sQuery(id+"F0.wireOp",EDGE,"E408"),sQuery(id+"F0.wireOp",EDGE,"E409"),sQuery(id+"F0.wireOp",EDGE,"E410"),sQuery(id+"F0.wireOp",EDGE,"E411"),sQuery(id+"F0.wireOp",EDGE,"E412"),sQuery(id+"F0.wireOp",EDGE,"E413"),sQuery(id+"F0.wireOp",EDGE,"E414"),sQuery(id+"F0.wireOp",EDGE,"E415"),sQuery(id+"F0.wireOp",EDGE,"E416"),sQuery(id+"F0.wireOp",EDGE,"E417"),sQuery(id+"F0.wireOp",EDGE,"E418"),sQuery(id+"F0.wireOp",EDGE,"E419"),sQuery(id+"F0.wireOp",EDGE,"E420"),sQuery(id+"F0.wireOp",EDGE,"E421"),sQuery(id+"F0.wireOp",EDGE,"E422"),sQuery(id+"F0.wireOp",EDGE,"E423"),sQuery(id+"F0.wireOp",EDGE,"E424"),sQuery(id+"F0.wireOp",EDGE,"E425"),sQuery(id+"F0.wireOp",EDGE,"E426"),sQuery(id+"F0.wireOp",EDGE,"E427"),sQuery(id+"F0.wireOp",EDGE,"E428"),sQuery(id+"F0.wireOp",EDGE,"E429"),sQuery(id+"F0.wireOp",EDGE,"E430"),sQuery(id+"F0.wireOp",EDGE,"E431"),sQuery(id+"F0.wireOp",EDGE,"E432"),sQuery(id+"F0.wireOp",EDGE,"E433"),sQuery(id+"F0.wireOp",EDGE,"E434"),sQuery(id+"F0.wireOp",EDGE,"E435"),sQuery(id+"F0.wireOp",EDGE,"E436"),sQuery(id+"F0.wireOp",EDGE,"E437"),sQuery(id+"F0.wireOp",EDGE,"E438"),sQuery(id+"F0.wireOp",EDGE,"E439"),sQuery(id+"F0.wireOp",EDGE,"E440"),sQuery(id+"F0.wireOp",EDGE,"E441"),sQuery(id+"F0.wireOp",EDGE,"E442"),sQuery(id+"F0.wireOp",EDGE,"E443"),sQuery(id+"F0.wireOp",EDGE,"E444"),sQuery(id+"F0.wireOp",EDGE,"E445"),sQuery(id+"F0.wireOp",EDGE,"E446"),sQuery(id+"F0.wireOp",EDGE,"E447"),sQuery(id+"F0.wireOp",EDGE,"E448"),sQuery(id+"F0.wireOp",EDGE,"E449"),sQuery(id+"F0.wireOp",EDGE,"E450"),sQuery(id+"F0.wireOp",EDGE,"E451"),sQuery(id+"F0.wireOp",EDGE,"E452"),sQuery(id+"F0.wireOp",EDGE,"E453"),sQuery(id+"F0.wireOp",EDGE,"E454"),sQuery(id+"F0.wireOp",EDGE,"E455"),sQuery(id+"F0.wireOp",EDGE,"E456"),sQuery(id+"F0.wireOp",EDGE,"E457"),sQuery(id+"F0.wireOp",EDGE,"E458"),sQuery(id+"F0.wireOp",EDGE,"E459"),sQuery(id+"F0.wireOp",EDGE,"E460"),sQuery(id+"F0.wireOp",EDGE,"E461"),sQuery(id+"F0.wireOp",EDGE,"E462"),sQuery(id+"F0.wireOp",EDGE,"E463"),sQuery(id+"F0.wireOp",EDGE,"E464"),sQuery(id+"F0.wireOp",EDGE,"E465"),sQuery(id+"F0.wireOp",EDGE,"E466"),sQuery(id+"F0.wireOp",EDGE,"E467"),sQuery(id+"F0.wireOp",EDGE,"E468"),sQuery(id+"F0.wireOp",EDGE,"E469"),sQuery(id+"F0.wireOp",EDGE,"E470"),sQuery(id+"F0.wireOp",EDGE,"E471"),sQuery(id+"F0.wireOp",EDGE,"E472"),sQuery(id+"F0.wireOp",EDGE,"E473"),sQuery(id+"F0.wireOp",EDGE,"E474"),sQuery(id+"F0.wireOp",EDGE,"E475"),sQuery(id+"F0.wireOp",EDGE,"E476"),sQuery(id+"F0.wireOp",EDGE,"E477"),sQuery(id+"F0.wireOp",EDGE,"E478"),sQuery(id+"F0.wireOp",EDGE,"E479"),sQuery(id+"F0.wireOp",EDGE,"E480"),sQuery(id+"F0.wireOp",EDGE,"E481"),sQuery(id+"F0.wireOp",EDGE,"E482"),sQuery(id+"F0.wireOp",EDGE,"E483"),sQuery(id+"F0.wireOp",EDGE,"E484"),sQuery(id+"F0.wireOp",EDGE,"E485"),sQuery(id+"F0.wireOp",EDGE,"E486"),sQuery(id+"F0.wireOp",EDGE,"E487"),sQuery(id+"F0.wireOp",EDGE,"E488"),sQuery(id+"F0.wireOp",EDGE,"E489"),sQuery(id+"F0.wireOp",EDGE,"E490"),sQuery(id+"F0.wireOp",EDGE,"E491"),sQuery(id+"F0.wireOp",EDGE,"E492"),sQuery(id+"F0.wireOp",EDGE,"E493"),sQuery(id+"F0.wireOp",EDGE,"E494"),sQuery(id+"F0.wireOp",EDGE,"E495"),sQuery(id+"F0.wireOp",EDGE,"E496"),sQuery(id+"F0.wireOp",EDGE,"E497"),sQuery(id+"F0.wireOp",EDGE,"E498"),sQuery(id+"F0.wireOp",EDGE,"E499"),sQuery(id+"F0.wireOp",EDGE,"E500"),sQuery(id+"F0.wireOp",EDGE,"E501"),sQuery(id+"F0.wireOp",EDGE,"E502"),sQuery(id+"F0.wireOp",EDGE,"E503"),sQuery(id+"F0.wireOp",EDGE,"E504"),sQuery(id+"F0.wireOp",EDGE,"E505"),sQuery(id+"F0.wireOp",EDGE,"E506"),sQuery(id+"F0.wireOp",EDGE,"E507"),sQuery(id+"F0.wireOp",EDGE,"E508"),sQuery(id+"F0.wireOp",EDGE,"E509"),sQuery(id+"F0.wireOp",EDGE,"E510"),sQuery(id+"F0.wireOp",EDGE,"E511"),sQuery(id+"F0.wireOp",EDGE,"E512"),sQuery(id+"F0.wireOp",EDGE,"E513"),sQuery(id+"F0.wireOp",EDGE,"E514"),sQuery(id+"F0.wireOp",EDGE,"E515"),sQuery(id+"F0.wireOp",EDGE,"E516"),sQuery(id+"F0.wireOp",EDGE,"E517"),sQuery(id+"F0.wireOp",EDGE,"E518"),sQuery(id+"F0.wireOp",EDGE,"E519"),sQuery(id+"F0.wireOp",EDGE,"E520"),sQuery(id+"F0.wireOp",EDGE,"E521"),sQuery(id+"F0.wireOp",EDGE,"E522"),sQuery(id+"F0.wireOp",EDGE,"E523"),sQuery(id+"F0.wireOp",EDGE,"E524"),sQuery(id+"F0.wireOp",EDGE,"E525"),sQuery(id+"F0.wireOp",EDGE,"E526"),sQuery(id+"F0.wireOp",EDGE,"E527"),sQuery(id+"F0.wireOp",EDGE,"E528"),sQuery(id+"F0.wireOp",EDGE,"E529"),sQuery(id+"F0.wireOp",EDGE,"E530"),sQuery(id+"F0.wireOp",EDGE,"E531"),sQuery(id+"F0.wireOp",EDGE,"E532"),sQuery(id+"F0.wireOp",EDGE,"E533"),sQuery(id+"F0.wireOp",EDGE,"E534"),sQuery(id+"F0.wireOp",EDGE,"E535"),sQuery(id+"F0.wireOp",EDGE,"E536"),sQuery(id+"F0.wireOp",EDGE,"E537"),sQuery(id+"F0.wireOp",EDGE,"E538"),sQuery(id+"F0.wireOp",EDGE,"E539"),sQuery(id+"F0.wireOp",EDGE,"E540"),sQuery(id+"F0.wireOp",EDGE,"E541"),sQuery(id+"F0.wireOp",EDGE,"E542"),sQuery(id+"F0.wireOp",EDGE,"E543"),sQuery(id+"F0.wireOp",EDGE,"E544"),sQuery(id+"F0.wireOp",EDGE,"E545"),sQuery(id+"F0.wireOp",EDGE,"E546"),sQuery(id+"F0.wireOp",EDGE,"E547"),sQuery(id+"F0.wireOp",EDGE,"E548"),sQuery(id+"F0.wireOp",EDGE,"E549"),sQuery(id+"F0.wireOp",EDGE,"E550"),sQuery(id+"F0.wireOp",EDGE,"E551"),sQuery(id+"F0.wireOp",EDGE,"E552"),sQuery(id+"F0.wireOp",EDGE,"E553"),sQuery(id+"F0.wireOp",EDGE,"E554"),sQuery(id+"F0.wireOp",EDGE,"E555"),sQuery(id+"F0.wireOp",EDGE,"E556"),sQuery(id+"F0.wireOp",EDGE,"E557"),sQuery(id+"F0.wireOp",EDGE,"E558"),sQuery(id+"F0.wireOp",EDGE,"E559"),sQuery(id+"F0.wireOp",EDGE,"E560"),sQuery(id+"F0.wireOp",EDGE,"E561"),sQuery(id+"F0.wireOp",EDGE,"E562"),sQuery(id+"F0.wireOp",EDGE,"E563"),sQuery(id+"F0.wireOp",EDGE,"E564"),sQuery(id+"F0.wireOp",EDGE,"E565"),sQuery(id+"F0.wireOp",EDGE,"E566"),sQuery(id+"F0.wireOp",EDGE,"E567"),sQuery(id+"F0.wireOp",EDGE,"E568"),sQuery(id+"F0.wireOp",EDGE,"E569"),sQuery(id+"F0.wireOp",EDGE,"E570"),sQuery(id+"F0.wireOp",EDGE,"E571"),sQuery(id+"F0.wireOp",EDGE,"E572"),sQuery(id+"F0.wireOp",EDGE,"E573"),sQuery(id+"F0.wireOp",EDGE,"E574"),sQuery(id+"F0.wireOp",EDGE,"E575"),sQuery(id+"F0.wireOp",EDGE,"E576"),sQuery(id+"F0.wireOp",EDGE,"E577"),sQuery(id+"F0.wireOp",EDGE,"E578"),sQuery(id+"F0.wireOp",EDGE,"E579"),sQuery(id+"F0.wireOp",EDGE,"E580"),sQuery(id+"F0.wireOp",EDGE,"E581"),sQuery(id+"F0.wireOp",EDGE,"E582"),sQuery(id+"F0.wireOp",EDGE,"E583"),sQuery(id+"F0.wireOp",EDGE,"E584"),sQuery(id+"F0.wireOp",EDGE,"E585"),sQuery(id+"F0.wireOp",EDGE,"E586"),sQuery(id+"F0.wireOp",EDGE,"E587"),sQuery(id+"F0.wireOp",EDGE,"E588"),sQuery(id+"F0.wireOp",EDGE,"E589"),sQuery(id+"F0.wireOp",EDGE,"E590"),sQuery(id+"F0.wireOp",EDGE,"E591"),sQuery(id+"F0.wireOp",EDGE,"E592"),sQuery(id+"F0.wireOp",EDGE,"E593"),sQuery(id+"F0.wireOp",EDGE,"E594"),sQuery(id+"F0.wireOp",EDGE,"E595"),sQuery(id+"F0.wireOp",EDGE,"E596"),sQuery(id+"F0.wireOp",EDGE,"E597"),sQuery(id+"F0.wireOp",EDGE,"E598"),sQuery(id+"F0.wireOp",EDGE,"E599"),sQuery(id+"F0.wireOp",EDGE,"E600"),sQuery(id+"F0.wireOp",EDGE,"E601"),sQuery(id+"F0.wireOp",EDGE,"E602"),sQuery(id+"F0.wireOp",EDGE,"E603"),sQuery(id+"F0.wireOp",EDGE,"E604"),sQuery(id+"F0.wireOp",EDGE,"E605"),sQuery(id+"F0.wireOp",EDGE,"E606"),sQuery(id+"F0.wireOp",EDGE,"E607"),sQuery(id+"F0.wireOp",EDGE,"E608"),sQuery(id+"F0.wireOp",EDGE,"E609"),sQuery(id+"F0.wireOp",EDGE,"E610"),sQuery(id+"F0.wireOp",EDGE,"E611"),sQuery(id+"F0.wireOp",EDGE,"E612"),sQuery(id+"F0.wireOp",EDGE,"E613"),sQuery(id+"F0.wireOp",EDGE,"E614"),sQuery(id+"F0.wireOp",EDGE,"E615"),sQuery(id+"F0.wireOp",EDGE,"E616"),sQuery(id+"F0.wireOp",EDGE,"E617"),sQuery(id+"F0.wireOp",EDGE,"E618"),sQuery(id+"F0.wireOp",EDGE,"E619"),sQuery(id+"F0.wireOp",EDGE,"E620"),sQuery(id+"F0.wireOp",EDGE,"E621"),sQuery(id+"F0.wireOp",EDGE,"E622"),sQuery(id+"F0.wireOp",EDGE,"E623"),sQuery(id+"F0.wireOp",EDGE,"E624"),sQuery(id+"F0.wireOp",EDGE,"E625"),sQuery(id+"F0.wireOp",EDGE,"E626"),sQuery(id+"F0.wireOp",EDGE,"E627"),sQuery(id+"F0.wireOp",EDGE,"E628"),sQuery(id+"F0.wireOp",EDGE,"E629"),sQuery(id+"F0.wireOp",EDGE,"E630"),sQuery(id+"F0.wireOp",EDGE,"E631"),sQuery(id+"F0.wireOp",EDGE,"E632"),sQuery(id+"F0.wireOp",EDGE,"E633"),sQuery(id+"F0.wireOp",EDGE,"E634"),sQuery(id+"F0.wireOp",EDGE,"E635"),sQuery(id+"F0.wireOp",EDGE,"E636"),sQuery(id+"F0.wireOp",EDGE,"E637"),sQuery(id+"F0.wireOp",EDGE,"E638"),sQuery(id+"F0.wireOp",EDGE,"E639"),sQuery(id+"F0.wireOp",EDGE,"E640"),sQuery(id+"F0.wireOp",EDGE,"E641"),sQuery(id+"F0.wireOp",EDGE,"E642"),sQuery(id+"F0.wireOp",EDGE,"E643"),sQuery(id+"F0.wireOp",EDGE,"E644"),sQuery(id+"F0.wireOp",EDGE,"E645"),sQuery(id+"F0.wireOp",EDGE,"E646"),sQuery(id+"F0.wireOp",EDGE,"E647"),sQuery(id+"F0.wireOp",EDGE,"E648"),sQuery(id+"F0.wireOp",EDGE,"E649"),sQuery(id+"F0.wireOp",EDGE,"E650"),sQuery(id+"F0.wireOp",EDGE,"E651"),sQuery(id+"F0.wireOp",EDGE,"E652"),sQuery(id+"F0.wireOp",EDGE,"E653"),sQuery(id+"F0.wireOp",EDGE,"E654"),sQuery(id+"F0.wireOp",EDGE,"E655"),sQuery(id+"F0.wireOp",EDGE,"E656"),sQuery(id+"F0.wireOp",EDGE,"E657"),sQuery(id+"F0.wireOp",EDGE,"E658"),sQuery(id+"F0.wireOp",EDGE,"E659"),sQuery(id+"F0.wireOp",EDGE,"E660"),sQuery(id+"F0.wireOp",EDGE,"E661"),sQuery(id+"F0.wireOp",EDGE,"E662"),sQuery(id+"F0.wireOp",EDGE,"E663"),sQuery(id+"F0.wireOp",EDGE,"E664"),sQuery(id+"F0.wireOp",EDGE,"E665"),sQuery(id+"F0.wireOp",EDGE,"E666"),sQuery(id+"F0.wireOp",EDGE,"E667"),sQuery(id+"F0.wireOp",EDGE,"E668"),sQuery(id+"F0.wireOp",EDGE,"E669"),sQuery(id+"F0.wireOp",EDGE,"E670"),sQuery(id+"F0.wireOp",EDGE,"E671"),sQuery(id+"F0.wireOp",EDGE,"E672"),sQuery(id+"F0.wireOp",EDGE,"E673"),sQuery(id+"F0.wireOp",EDGE,"E674"),sQuery(id+"F0.wireOp",EDGE,"E675"),sQuery(id+"F0.wireOp",EDGE,"E676"),sQuery(id+"F0.wireOp",EDGE,"E677"),sQuery(id+"F0.wireOp",EDGE,"E678"),sQuery(id+"F0.wireOp",EDGE,"E679"),sQuery(id+"F0.wireOp",EDGE,"E680"),sQuery(id+"F0.wireOp",EDGE,"E681"),sQuery(id+"F0.wireOp",EDGE,"E682"),sQuery(id+"F0.wireOp",EDGE,"E683"),sQuery(id+"F0.wireOp",EDGE,"E684"),sQuery(id+"F0.wireOp",EDGE,"E685"),sQuery(id+"F0.wireOp",EDGE,"E686"),sQuery(id+"F0.wireOp",EDGE,"E687"),sQuery(id+"F0.wireOp",EDGE,"E688"),sQuery(id+"F0.wireOp",EDGE,"E689"),sQuery(id+"F0.wireOp",EDGE,"E690"),sQuery(id+"F0.wireOp",EDGE,"E691"),sQuery(id+"F0.wireOp",EDGE,"E692"),sQuery(id+"F0.wireOp",EDGE,"E693"),sQuery(id+"F0.wireOp",EDGE,"E694"),sQuery(id+"F0.wireOp",EDGE,"E695"),sQuery(id+"F0.wireOp",EDGE,"E696"),sQuery(id+"F0.wireOp",EDGE,"E697"),sQuery(id+"F0.wireOp",EDGE,"E698"),sQuery(id+"F0.wireOp",EDGE,"E699"),sQuery(id+"F0.wireOp",EDGE,"E700"),sQuery(id+"F0.wireOp",EDGE,"E701"),sQuery(id+"F0.wireOp",EDGE,"E702"),sQuery(id+"F0.wireOp",EDGE,"E703"),sQuery(id+"F0.wireOp",EDGE,"E704"),sQuery(id+"F0.wireOp",EDGE,"E705"),sQuery(id+"F0.wireOp",EDGE,"E706"),sQuery(id+"F0.wireOp",EDGE,"E707"),sQuery(id+"F0.wireOp",EDGE,"E708"),sQuery(id+"F0.wireOp",EDGE,"E709"),sQuery(id+"F0.wireOp",EDGE,"E710"),sQuery(id+"F0.wireOp",EDGE,"E711"),sQuery(id+"F0.wireOp",EDGE,"E712"),sQuery(id+"F0.wireOp",EDGE,"E713"),sQuery(id+"F0.wireOp",EDGE,"E714"),sQuery(id+"F0.wireOp",EDGE,"E715"),sQuery(id+"F0.wireOp",EDGE,"E716"),sQuery(id+"F0.wireOp",EDGE,"E717"),sQuery(id+"F0.wireOp",EDGE,"E718"),sQuery(id+"F0.wireOp",EDGE,"E719"),sQuery(id+"F0.wireOp",EDGE,"E720"),sQuery(id+"F0.wireOp",EDGE,"E721"),sQuery(id+"F0.wireOp",EDGE,"E722"),sQuery(id+"F0.wireOp",EDGE,"E723"),sQuery(id+"F0.wireOp",EDGE,"E724"),sQuery(id+"F0.wireOp",EDGE,"E725"),sQuery(id+"F0.wireOp",EDGE,"E726"),sQuery(id+"F0.wireOp",EDGE,"E727"),sQuery(id+"F0.wireOp",EDGE,"E728"),sQuery(id+"F0.wireOp",EDGE,"E729"),sQuery(id+"F0.wireOp",EDGE,"E730"),sQuery(id+"F0.wireOp",EDGE,"E731"),sQuery(id+"F0.wireOp",EDGE,"E732"),sQuery(id+"F0.wireOp",EDGE,"E733"),sQuery(id+"F0.wireOp",EDGE,"E734"),sQuery(id+"F0.wireOp",EDGE,"E735"),sQuery(id+"F0.wireOp",EDGE,"E736"),sQuery(id+"F0.wireOp",EDGE,"E737"),sQuery(id+"F0.wireOp",EDGE,"E738"),sQuery(id+"F0.wireOp",EDGE,"E739"),sQuery(id+"F0.wireOp",EDGE,"E740"),sQuery(id+"F0.wireOp",EDGE,"E741"),sQuery(id+"F0.wireOp",EDGE,"E742"),sQuery(id+"F0.wireOp",EDGE,"E743"),sQuery(id+"F0.wireOp",EDGE,"E744"),sQuery(id+"F0.wireOp",EDGE,"E745"),sQuery(id+"F0.wireOp",EDGE,"E746"),sQuery(id+"F0.wireOp",EDGE,"E747"),sQuery(id+"F0.wireOp",EDGE,"E748"),sQuery(id+"F0.wireOp",EDGE,"E749"),sQuery(id+"F0.wireOp",EDGE,"E750"),sQuery(id+"F0.wireOp",EDGE,"E751"),sQuery(id+"F0.wireOp",EDGE,"E752"),sQuery(id+"F0.wireOp",EDGE,"E753"),sQuery(id+"F0.wireOp",EDGE,"E754"),sQuery(id+"F0.wireOp",EDGE,"E755"),sQuery(id+"F0.wireOp",EDGE,"E756"),sQuery(id+"F0.wireOp",EDGE,"E757"),sQuery(id+"F0.wireOp",EDGE,"E758"),sQuery(id+"F0.wireOp",EDGE,"E759"),sQuery(id+"F0.wireOp",EDGE,"E760"),sQuery(id+"F0.wireOp",EDGE,"E761"),sQuery(id+"F0.wireOp",EDGE,"E762"),sQuery(id+"F0.wireOp",EDGE,"E763"),sQuery(id+"F0.wireOp",EDGE,"E764"),sQuery(id+"F0.wireOp",EDGE,"E765"),sQuery(id+"F0.wireOp",EDGE,"E766"),sQuery(id+"F0.wireOp",EDGE,"E767"),sQuery(id+"F0.wireOp",EDGE,"E768"),sQuery(id+"F0.wireOp",EDGE,"E769"),sQuery(id+"F0.wireOp",EDGE,"E770"),sQuery(id+"F0.wireOp",EDGE,"E771"),sQuery(id+"F0.wireOp",EDGE,"E772"),sQuery(id+"F0.wireOp",EDGE,"E773"),sQuery(id+"F0.wireOp",EDGE,"E774"),sQuery(id+"F0.wireOp",EDGE,"E775"),sQuery(id+"F0.wireOp",EDGE,"E776"),sQuery(id+"F0.wireOp",EDGE,"E777"),sQuery(id+"F0.wireOp",EDGE,"E778"),sQuery(id+"F0.wireOp",EDGE,"E779"),sQuery(id+"F0.wireOp",EDGE,"E780"),sQuery(id+"F0.wireOp",EDGE,"E781"),sQuery(id+"F0.wireOp",EDGE,"E782"),sQuery(id+"F0.wireOp",EDGE,"E783"),sQuery(id+"F0.wireOp",EDGE,"E784"),sQuery(id+"F0.wireOp",EDGE,"E785"),sQuery(id+"F0.wireOp",EDGE,"E786"),sQuery(id+"F0.wireOp",EDGE,"E787"),sQuery(id+"F0.wireOp",EDGE,"E788"),sQuery(id+"F0.wireOp",EDGE,"E789"),sQuery(id+"F0.wireOp",EDGE,"E790"),sQuery(id+"F0.wireOp",EDGE,"E791"),sQuery(id+"F0.wireOp",EDGE,"E792"),sQuery(id+"F0.wireOp",EDGE,"E793"),sQuery(id+"F0.wireOp",EDGE,"E794"),sQuery(id+"F0.wireOp",EDGE,"E795"),sQuery(id+"F0.wireOp",EDGE,"E796"),sQuery(id+"F0.wireOp",EDGE,"E797"),sQuery(id+"F0.wireOp",EDGE,"E798"),sQuery(id+"F0.wireOp",EDGE,"E799"),sQuery(id+"F0.wireOp",EDGE,"E800"),sQuery(id+"F0.wireOp",EDGE,"E801"),sQuery(id+"F0.wireOp",EDGE,"E802"),sQuery(id+"F0.wireOp",EDGE,"E803"),sQuery(id+"F0.wireOp",EDGE,"E804"),sQuery(id+"F0.wireOp",EDGE,"E805"),sQuery(id+"F0.wireOp",EDGE,"E806"),sQuery(id+"F0.wireOp",EDGE,"E807"),sQuery(id+"F0.wireOp",EDGE,"E808"),sQuery(id+"F0.wireOp",EDGE,"E809"),sQuery(id+"F0.wireOp",EDGE,"E810"),sQuery(id+"F0.wireOp",EDGE,"E811"),sQuery(id+"F0.wireOp",EDGE,"E812"),sQuery(id+"F0.wireOp",EDGE,"E813"),sQuery(id+"F0.wireOp",EDGE,"E814"),sQuery(id+"F0.wireOp",EDGE,"E815"),sQuery(id+"F0.wireOp",EDGE,"E816"),sQuery(id+"F0.wireOp",EDGE,"E817"),sQuery(id+"F0.wireOp",EDGE,"E818"),sQuery(id+"F0.wireOp",EDGE,"E819"),sQuery(id+"F0.wireOp",EDGE,"E820"),sQuery(id+"F0.wireOp",EDGE,"E821"),sQuery(id+"F0.wireOp",EDGE,"E822"),sQuery(id+"F0.wireOp",EDGE,"E823"),sQuery(id+"F0.wireOp",EDGE,"E824"),sQuery(id+"F0.wireOp",EDGE,"E825"),sQuery(id+"F0.wireOp",EDGE,"E826"),sQuery(id+"F0.wireOp",EDGE,"E827"),sQuery(id+"F0.wireOp",EDGE,"E828"),sQuery(id+"F0.wireOp",EDGE,"E829"),sQuery(id+"F0.wireOp",EDGE,"E830"),sQuery(id+"F0.wireOp",EDGE,"E831"),sQuery(id+"F0.wireOp",EDGE,"E832"),sQuery(id+"F0.wireOp",EDGE,"E833"),sQuery(id+"F0.wireOp",EDGE,"E834"),sQuery(id+"F0.wireOp",EDGE,"E835"),sQuery(id+"F0.wireOp",EDGE,"E836"),sQuery(id+"F0.wireOp",EDGE,"E837"),sQuery(id+"F0.wireOp",EDGE,"E838"),sQuery(id+"F0.wireOp",EDGE,"E839"),sQuery(id+"F0.wireOp",EDGE,"E840"),sQuery(id+"F0.wireOp",EDGE,"E841"),sQuery(id+"F0.wireOp",EDGE,"E842"),sQuery(id+"F0.wireOp",EDGE,"E843"),sQuery(id+"F0.wireOp",EDGE,"E844"),sQuery(id+"F0.wireOp",EDGE,"E845"),sQuery(id+"F0.wireOp",EDGE,"E846"),sQuery(id+"F0.wireOp",EDGE,"E847"),sQuery(id+"F0.wireOp",EDGE,"E848"),sQuery(id+"F0.wireOp",EDGE,"E849"),sQuery(id+"F0.wireOp",EDGE,"E850"),sQuery(id+"F0.wireOp",EDGE,"E851"),sQuery(id+"F0.wireOp",EDGE,"E852"),sQuery(id+"F0.wireOp",EDGE,"E853"),sQuery(id+"F0.wireOp",EDGE,"E854"),sQuery(id+"F0.wireOp",EDGE,"E855"),sQuery(id+"F0.wireOp",EDGE,"E856"),sQuery(id+"F0.wireOp",EDGE,"E857"),sQuery(id+"F0.wireOp",EDGE,"E858"),sQuery(id+"F0.wireOp",EDGE,"E859"),sQuery(id+"F0.wireOp",EDGE,"E860"),sQuery(id+"F0.wireOp",EDGE,"E861"),sQuery(id+"F0.wireOp",EDGE,"E862"),sQuery(id+"F0.wireOp",EDGE,"E863"),sQuery(id+"F0.wireOp",EDGE,"E864"),sQuery(id+"F0.wireOp",EDGE,"E865"),sQuery(id+"F0.wireOp",EDGE,"E866"),sQuery(id+"F0.wireOp",EDGE,"E867"),sQuery(id+"F0.wireOp",EDGE,"E868"),sQuery(id+"F0.wireOp",EDGE,"E869"),sQuery(id+"F0.wireOp",EDGE,"E870"),sQuery(id+"F0.wireOp",EDGE,"E871"),sQuery(id+"F0.wireOp",EDGE,"E872"),sQuery(id+"F0.wireOp",EDGE,"E873"),sQuery(id+"F0.wireOp",EDGE,"E874"),sQuery(id+"F0.wireOp",EDGE,"E875"),sQuery(id+"F0.wireOp",EDGE,"E876"),sQuery(id+"F0.wireOp",EDGE,"E877"),sQuery(id+"F0.wireOp",EDGE,"E878"),sQuery(id+"F0.wireOp",EDGE,"E879"),sQuery(id+"F0.wireOp",EDGE,"E880"),sQuery(id+"F0.wireOp",EDGE,"E881"),sQuery(id+"F0.wireOp",EDGE,"E882"),sQuery(id+"F0.wireOp",EDGE,"E883"),sQuery(id+"F0.wireOp",EDGE,"E884"),sQuery(id+"F0.wireOp",EDGE,"E885"),sQuery(id+"F0.wireOp",EDGE,"E886"),sQuery(id+"F0.wireOp",EDGE,"E887"),sQuery(id+"F0.wireOp",EDGE,"E888"),sQuery(id+"F0.wireOp",EDGE,"E889"),sQuery(id+"F0.wireOp",EDGE,"E890"),sQuery(id+"F0.wireOp",EDGE,"E891"),sQuery(id+"F0.wireOp",EDGE,"E892"),sQuery(id+"F0.wireOp",EDGE,"E893"),sQuery(id+"F0.wireOp",EDGE,"E894"),sQuery(id+"F0.wireOp",EDGE,"E895"),sQuery(id+"F0.wireOp",EDGE,"E896"),sQuery(id+"F0.wireOp",EDGE,"E897"),sQuery(id+"F0.wireOp",EDGE,"E898"),sQuery(id+"F0.wireOp",EDGE,"E899"),sQuery(id+"F0.wireOp",EDGE,"E900"),sQuery(id+"F0.wireOp",EDGE,"E901"),sQuery(id+"F0.wireOp",EDGE,"E902"),sQuery(id+"F0.wireOp",EDGE,"E903"),sQuery(id+"F0.wireOp",EDGE,"E904"),sQuery(id+"F0.wireOp",EDGE,"E905"),sQuery(id+"F0.wireOp",EDGE,"E906"),sQuery(id+"F0.wireOp",EDGE,"E907"),sQuery(id+"F0.wireOp",EDGE,"E908"),sQuery(id+"F0.wireOp",EDGE,"E909"),sQuery(id+"F0.wireOp",EDGE,"E910"),sQuery(id+"F0.wireOp",EDGE,"E911"),sQuery(id+"F0.wireOp",EDGE,"E912"),sQuery(id+"F0.wireOp",EDGE,"E913"),sQuery(id+"F0.wireOp",EDGE,"E914"),sQuery(id+"F0.wireOp",EDGE,"E915"),sQuery(id+"F0.wireOp",EDGE,"E916"),sQuery(id+"F0.wireOp",EDGE,"E917"),sQuery(id+"F0.wireOp",EDGE,"E918"),sQuery(id+"F0.wireOp",EDGE,"E919"),sQuery(id+"F0.wireOp",EDGE,"E920"),sQuery(id+"F0.wireOp",EDGE,"E921"),sQuery(id+"F0.wireOp",EDGE,"E922"),sQuery(id+"F0.wireOp",EDGE,"E923"),sQuery(id+"F0.wireOp",EDGE,"E924"),sQuery(id+"F0.wireOp",EDGE,"E925"),sQuery(id+"F0.wireOp",EDGE,"E926"),sQuery(id+"F0.wireOp",EDGE,"E927"),sQuery(id+"F0.wireOp",EDGE,"E928"),sQuery(id+"F0.wireOp",EDGE,"E929"),sQuery(id+"F0.wireOp",EDGE,"E930"),sQuery(id+"F0.wireOp",EDGE,"E931"),sQuery(id+"F0.wireOp",EDGE,"E932"),sQuery(id+"F0.wireOp",EDGE,"E933"),sQuery(id+"F0.wireOp",EDGE,"E934"),sQuery(id+"F0.wireOp",EDGE,"E935"),sQuery(id+"F0.wireOp",EDGE,"E936"),sQuery(id+"F0.wireOp",EDGE,"E937"),sQuery(id+"F0.wireOp",EDGE,"E938"),sQuery(id+"F0.wireOp",EDGE,"E939"),sQuery(id+"F0.wireOp",EDGE,"E940"),sQuery(id+"F0.wireOp",EDGE,"E941"),sQuery(id+"F0.wireOp",EDGE,"E942"),sQuery(id+"F0.wireOp",EDGE,"E943"),sQuery(id+"F0.wireOp",EDGE,"E944"),sQuery(id+"F0.wireOp",EDGE,"E945"),sQuery(id+"F0.wireOp",EDGE,"E946"),sQuery(id+"F0.wireOp",EDGE,"E947"),sQuery(id+"F0.wireOp",EDGE,"E948"),sQuery(id+"F0.wireOp",EDGE,"E949"),sQuery(id+"F0.wireOp",EDGE,"E950"),sQuery(id+"F0.wireOp",EDGE,"E951"),sQuery(id+"F0.wireOp",EDGE,"E952"),sQuery(id+"F0.wireOp",EDGE,"E953"),sQuery(id+"F0.wireOp",EDGE,"E954"),sQuery(id+"F0.wireOp",EDGE,"E955"),sQuery(id+"F0.wireOp",EDGE,"E956"),sQuery(id+"F0.wireOp",EDGE,"E957"),sQuery(id+"F0.wireOp",EDGE,"E958"),sQuery(id+"F0.wireOp",EDGE,"E959"),sQuery(id+"F0.wireOp",EDGE,"E960"),sQuery(id+"F0.wireOp",EDGE,"E961"),sQuery(id+"F0.wireOp",EDGE,"E962"),sQuery(id+"F0.wireOp",EDGE,"E963"),sQuery(id+"F0.wireOp",EDGE,"E964"),sQuery(id+"F0.wireOp",EDGE,"E965"),sQuery(id+"F0.wireOp",EDGE,"E966"),sQuery(id+"F0.wireOp",EDGE,"E967"),sQuery(id+"F0.wireOp",EDGE,"E968"),sQuery(id+"F0.wireOp",EDGE,"E969"),sQuery(id+"F0.wireOp",EDGE,"E970"),sQuery(id+"F0.wireOp",EDGE,"E971"),sQuery(id+"F0.wireOp",EDGE,"E972"),sQuery(id+"F0.wireOp",EDGE,"E973"),sQuery(id+"F0.wireOp",EDGE,"E974"),sQuery(id+"F0.wireOp",EDGE,"E975"),sQuery(id+"F0.wireOp",EDGE,"E976"),sQuery(id+"F0.wireOp",EDGE,"E977"),sQuery(id+"F0.wireOp",EDGE,"E978"),sQuery(id+"F0.wireOp",EDGE,"E979"),sQuery(id+"F0.wireOp",EDGE,"E980"),sQuery(id+"F0.wireOp",EDGE,"E981"),sQuery(id+"F0.wireOp",EDGE,"E982"),sQuery(id+"F0.wireOp",EDGE,"E983"),sQuery(id+"F0.wireOp",EDGE,"E984"),sQuery(id+"F0.wireOp",EDGE,"E985"),sQuery(id+"F0.wireOp",EDGE,"E986"),sQuery(id+"F0.wireOp",EDGE,"E987"),sQuery(id+"F0.wireOp",EDGE,"E988"),sQuery(id+"F0.wireOp",EDGE,"E989"),sQuery(id+"F0.wireOp",EDGE,"E990"),sQuery(id+"F0.wireOp",EDGE,"E991"),sQuery(id+"F0.wireOp",EDGE,"E992"),sQuery(id+"F0.wireOp",EDGE,"E993"),sQuery(id+"F0.wireOp",EDGE,"E994"),sQuery(id+"F0.wireOp",EDGE,"E995"),sQuery(id+"F0.wireOp",EDGE,"E996"),sQuery(id+"F0.wireOp",EDGE,"E997"),sQuery(id+"F0.wireOp",EDGE,"E998"),sQuery(id+"F0.wireOp",EDGE,"E999"),sQuery(id+"F0.wireOp",EDGE,"E1000"),sQuery(id+"F0.wireOp",EDGE,"E1001"),sQuery(id+"F0.wireOp",EDGE,"E1002"),sQuery(id+"F0.wireOp",EDGE,"E1003"),sQuery(id+"F0.wireOp",EDGE,"E1004"),sQuery(id+"F0.wireOp",EDGE,"E1005"),sQuery(id+"F0.wireOp",EDGE,"E1006"),sQuery(id+"F0.wireOp",EDGE,"E1007"),sQuery(id+"F0.wireOp",EDGE,"E1008"),sQuery(id+"F0.wireOp",EDGE,"E1009"),sQuery(id+"F0.wireOp",EDGE,"E1010"),sQuery(id+"F0.wireOp",EDGE,"E1011"),sQuery(id+"F0.wireOp",EDGE,"E1012"),sQuery(id+"F0.wireOp",EDGE,"E1013"),sQuery(id+"F0.wireOp",EDGE,"E1014"),sQuery(id+"F0.wireOp",EDGE,"E1015"),sQuery(id+"F0.wireOp",EDGE,"E1016"),sQuery(id+"F0.wireOp",EDGE,"E1017"),sQuery(id+"F0.wireOp",EDGE,"E1018"),sQuery(id+"F0.wireOp",EDGE,"E1019"),sQuery(id+"F0.wireOp",EDGE,"E1020"),sQuery(id+"F0.wireOp",EDGE,"E1021"),sQuery(id+"F0.wireOp",EDGE,"E1022"),sQuery(id+"F0.wireOp",EDGE,"E1023"),sQuery(id+"F0.wireOp",EDGE,"E1024"),sQuery(id+"F0.wireOp",EDGE,"E1025"),sQuery(id+"F0.wireOp",EDGE,"E1026"),sQuery(id+"F0.wireOp",EDGE,"E1027"),sQuery(id+"F0.wireOp",EDGE,"E1028"),sQuery(id+"F0.wireOp",EDGE,"E1029"),sQuery(id+"F0.wireOp",EDGE,"E1030"),sQuery(id+"F0.wireOp",EDGE,"E1031"),sQuery(id+"F0.wireOp",EDGE,"E1032"),sQuery(id+"F0.wireOp",EDGE,"E1033"),sQuery(id+"F0.wireOp",EDGE,"E1034"),sQuery(id+"F0.wireOp",EDGE,"E1035"),sQuery(id+"F0.wireOp",EDGE,"E1036"),sQuery(id+"F0.wireOp",EDGE,"E1037"),sQuery(id+"F0.wireOp",EDGE,"E1038"),sQuery(id+"F0.wireOp",EDGE,"E1039"),sQuery(id+"F0.wireOp",EDGE,"E1040"),sQuery(id+"F0.wireOp",EDGE,"E1041"),sQuery(id+"F0.wireOp",EDGE,"E1042"),sQuery(id+"F0.wireOp",EDGE,"E1043"),sQuery(id+"F0.wireOp",EDGE,"E1044"),sQuery(id+"F0.wireOp",EDGE,"E1045"),sQuery(id+"F0.wireOp",EDGE,"E1046"),sQuery(id+"F0.wireOp",EDGE,"E1047"),sQuery(id+"F0.wireOp",EDGE,"E1048"),sQuery(id+"F0.wireOp",EDGE,"E1049"),sQuery(id+"F0.wireOp",EDGE,"E1050"),sQuery(id+"F0.wireOp",EDGE,"E1051"),sQuery(id+"F0.wireOp",EDGE,"E1052"),sQuery(id+"F0.wireOp",EDGE,"E1053"),sQuery(id+"F0.wireOp",EDGE,"E1054"),sQuery(id+"F0.wireOp",EDGE,"E1055"),sQuery(id+"F0.wireOp",EDGE,"E1056"),sQuery(id+"F0.wireOp",EDGE,"E1057"),sQuery(id+"F0.wireOp",EDGE,"E1058"),sQuery(id+"F0.wireOp",EDGE,"E1059"),sQuery(id+"F0.wireOp",EDGE,"E1060"),sQuery(id+"F0.wireOp",EDGE,"E1061"),sQuery(id+"F0.wireOp",EDGE,"E1062"),sQuery(id+"F0.wireOp",EDGE,"E1063"),sQuery(id+"F0.wireOp",EDGE,"E1064"),sQuery(id+"F0.wireOp",EDGE,"E1065"),sQuery(id+"F0.wireOp",EDGE,"E1066"),sQuery(id+"F0.wireOp",EDGE,"E1067"),sQuery(id+"F0.wireOp",EDGE,"E1068"),sQuery(id+"F0.wireOp",EDGE,"E1069"),sQuery(id+"F0.wireOp",EDGE,"E1070"),sQuery(id+"F0.wireOp",EDGE,"E1071"),sQuery(id+"F0.wireOp",EDGE,"E1072"),sQuery(id+"F0.wireOp",EDGE,"E1073"),sQuery(id+"F0.wireOp",EDGE,"E1074"),sQuery(id+"F0.wireOp",EDGE,"E1075"),sQuery(id+"F0.wireOp",EDGE,"E1076"),sQuery(id+"F0.wireOp",EDGE,"E1077"),sQuery(id+"F0.wireOp",EDGE,"E1078"),sQuery(id+"F0.wireOp",EDGE,"E1079"),sQuery(id+"F0.wireOp",EDGE,"E1080"),sQuery(id+"F0.wireOp",EDGE,"E1081"),sQuery(id+"F0.wireOp",EDGE,"E1082"),sQuery(id+"F0.wireOp",EDGE,"E1083"),sQuery(id+"F0.wireOp",EDGE,"E1084"),sQuery(id+"F0.wireOp",EDGE,"E1085"),sQuery(id+"F0.wireOp",EDGE,"E1086"),sQuery(id+"F0.wireOp",EDGE,"E1087"),sQuery(id+"F0.wireOp",EDGE,"E1088"),sQuery(id+"F0.wireOp",EDGE,"E1089"),sQuery(id+"F0.wireOp",EDGE,"E1090"),sQuery(id+"F0.wireOp",EDGE,"E1091"),sQuery(id+"F0.wireOp",EDGE,"E1092"),sQuery(id+"F0.wireOp",EDGE,"E1093"),sQuery(id+"F0.wireOp",EDGE,"E1094"),sQuery(id+"F0.wireOp",EDGE,"E1095"),sQuery(id+"F0.wireOp",EDGE,"E1096"),sQuery(id+"F0.wireOp",EDGE,"E1097"),sQuery(id+"F0.wireOp",EDGE,"E1098"),sQuery(id+"F0.wireOp",EDGE,"E1099"),sQuery(id+"F0.wireOp",EDGE,"E1100"),sQuery(id+"F0.wireOp",EDGE,"E1101"),sQuery(id+"F0.wireOp",EDGE,"E1102"),sQuery(id+"F0.wireOp",EDGE,"E1103"),sQuery(id+"F0.wireOp",EDGE,"E1104"),sQuery(id+"F0.wireOp",EDGE,"E1105"),sQuery(id+"F0.wireOp",EDGE,"E1106"),sQuery(id+"F0.wireOp",EDGE,"E1107"),sQuery(id+"F0.wireOp",EDGE,"E1108"),sQuery(id+"F0.wireOp",EDGE,"E1109"),sQuery(id+"F0.wireOp",EDGE,"E1110"),sQuery(id+"F0.wireOp",EDGE,"E1111"),sQuery(id+"F0.wireOp",EDGE,"E1112"),sQuery(id+"F0.wireOp",EDGE,"E1113"),sQuery(id+"F0.wireOp",EDGE,"E1114"),sQuery(id+"F0.wireOp",EDGE,"E1115"),sQuery(id+"F0.wireOp",EDGE,"E1116"),sQuery(id+"F0.wireOp",EDGE,"E1117"),sQuery(id+"F0.wireOp",EDGE,"E1118"),sQuery(id+"F0.wireOp",EDGE,"E1119"),sQuery(id+"F0.wireOp",EDGE,"E1120"),sQuery(id+"F0.wireOp",EDGE,"E1121"),sQuery(id+"F0.wireOp",EDGE,"E1122"),sQuery(id+"F0.wireOp",EDGE,"E1123"),sQuery(id+"F0.wireOp",EDGE,"E1124"),sQuery(id+"F0.wireOp",EDGE,"E1125"),sQuery(id+"F0.wireOp",EDGE,"E1126"),sQuery(id+"F0.wireOp",EDGE,"E1127"),sQuery(id+"F0.wireOp",EDGE,"E1128"),sQuery(id+"F0.wireOp",EDGE,"E1129"),sQuery(id+"F0.wireOp",EDGE,"E1130"),sQuery(id+"F0.wireOp",EDGE,"E1131"),sQuery(id+"F0.wireOp",EDGE,"E1132"),sQuery(id+"F0.wireOp",EDGE,"E1133"),sQuery(id+"F0.wireOp",EDGE,"E1134"),sQuery(id+"F0.wireOp",EDGE,"E1135"),sQuery(id+"F0.wireOp",EDGE,"E1136"),sQuery(id+"F0.wireOp",EDGE,"E1137"),sQuery(id+"F0.wireOp",EDGE,"E1138"),sQuery(id+"F0.wireOp",EDGE,"E1139"),sQuery(id+"F0.wireOp",EDGE,"E1140"),sQuery(id+"F0.wireOp",EDGE,"E1141"),sQuery(id+"F0.wireOp",EDGE,"E1142"),sQuery(id+"F0.wireOp",EDGE,"E1143"),sQuery(id+"F0.wireOp",EDGE,"E1144"),sQuery(id+"F0.wireOp",EDGE,"E1145"),sQuery(id+"F0.wireOp",EDGE,"E1146"),sQuery(id+"F0.wireOp",EDGE,"E1147"),sQuery(id+"F0.wireOp",EDGE,"E1148"),sQuery(id+"F0.wireOp",EDGE,"E1149"),sQuery(id+"F0.wireOp",EDGE,"E1150"),sQuery(id+"F0.wireOp",EDGE,"E1151"),sQuery(id+"F0.wireOp",EDGE,"E1152"),sQuery(id+"F0.wireOp",EDGE,"E1153"),sQuery(id+"F0.wireOp",EDGE,"E1154"),sQuery(id+"F0.wireOp",EDGE,"E1155"),sQuery(id+"F0.wireOp",EDGE,"E1156"),sQuery(id+"F0.wireOp",EDGE,"E1157"),sQuery(id+"F0.wireOp",EDGE,"E1158"),sQuery(id+"F0.wireOp",EDGE,"E1159"),sQuery(id+"F0.wireOp",EDGE,"E1160"),sQuery(id+"F0.wireOp",EDGE,"E1161"),sQuery(id+"F0.wireOp",EDGE,"E1162"),sQuery(id+"F0.wireOp",EDGE,"E1163"),sQuery(id+"F0.wireOp",EDGE,"E1164"),sQuery(id+"F0.wireOp",EDGE,"E1165"),sQuery(id+"F0.wireOp",EDGE,"E1166"),sQuery(id+"F0.wireOp",EDGE,"E1167"),sQuery(id+"F0.wireOp",EDGE,"E1168"),sQuery(id+"F0.wireOp",EDGE,"E1169"),sQuery(id+"F0.wireOp",EDGE,"E1170"),sQuery(id+"F0.wireOp",EDGE,"E1171"),sQuery(id+"F0.wireOp",EDGE,"E1172"),sQuery(id+"F0.wireOp",EDGE,"E1173"),sQuery(id+"F0.wireOp",EDGE,"E1174"),sQuery(id+"F0.wireOp",EDGE,"E1175"),sQuery(id+"F0.wireOp",EDGE,"E1176"),sQuery(id+"F0.wireOp",EDGE,"E1177"),sQuery(id+"F0.wireOp",EDGE,"E1178"),sQuery(id+"F0.wireOp",EDGE,"E1179"),sQuery(id+"F0.wireOp",EDGE,"E1180"),sQuery(id+"F0.wireOp",EDGE,"E1181"),sQuery(id+"F0.wireOp",EDGE,"E1182"),sQuery(id+"F0.wireOp",EDGE,"E1183"),sQuery(id+"F0.wireOp",EDGE,"E1184"),sQuery(id+"F0.wireOp",EDGE,"E1185"),sQuery(id+"F0.wireOp",EDGE,"E1186"),sQuery(id+"F0.wireOp",EDGE,"E1187"),sQuery(id+"F0.wireOp",EDGE,"E1188"),sQuery(id+"F0.wireOp",EDGE,"E1189"),sQuery(id+"F0.wireOp",EDGE,"E1190"),sQuery(id+"F0.wireOp",EDGE,"E1191"),sQuery(id+"F0.wireOp",EDGE,"E1192"),sQuery(id+"F0.wireOp",EDGE,"E1193"),sQuery(id+"F0.wireOp",EDGE,"E1194"),sQuery(id+"F0.wireOp",EDGE,"E1195"),sQuery(id+"F0.wireOp",EDGE,"E1196"),sQuery(id+"F0.wireOp",EDGE,"E1197"),sQuery(id+"F0.wireOp",EDGE,"E1198"),sQuery(id+"F0.wireOp",EDGE,"E1199"),sQuery(id+"F0.wireOp",EDGE,"E1200"),sQuery(id+"F0.wireOp",EDGE,"E1201"),sQuery(id+"F0.wireOp",EDGE,"E1202"),sQuery(id+"F0.wireOp",EDGE,"E1203"),sQuery(id+"F0.wireOp",EDGE,"E1204"),sQuery(id+"F0.wireOp",EDGE,"E1205"),sQuery(id+"F0.wireOp",EDGE,"E1206"),sQuery(id+"F0.wireOp",EDGE,"E1207"),sQuery(id+"F0.wireOp",EDGE,"E1208"),sQuery(id+"F0.wireOp",EDGE,"E1209"),sQuery(id+"F0.wireOp",EDGE,"E1210"),sQuery(id+"F0.wireOp",EDGE,"E1211"),sQuery(id+"F0.wireOp",EDGE,"E1212"),sQuery(id+"F0.wireOp",EDGE,"E1213"),sQuery(id+"F0.wireOp",EDGE,"E1214"),sQuery(id+"F0.wireOp",EDGE,"E1215"),sQuery(id+"F0.wireOp",EDGE,"E1216"),sQuery(id+"F0.wireOp",EDGE,"E1217"),sQuery(id+"F0.wireOp",EDGE,"E1218"),sQuery(id+"F0.wireOp",EDGE,"E1219"),sQuery(id+"F0.wireOp",EDGE,"E1220"),sQuery(id+"F0.wireOp",EDGE,"E1221"),sQuery(id+"F0.wireOp",EDGE,"E1222"),sQuery(id+"F0.wireOp",EDGE,"E1223"),sQuery(id+"F0.wireOp",EDGE,"E1224"),sQuery(id+"F0.wireOp",EDGE,"E1225"),sQuery(id+"F0.wireOp",EDGE,"E1226"),sQuery(id+"F0.wireOp",EDGE,"E1227"),sQuery(id+"F0.wireOp",EDGE,"E1228"),sQuery(id+"F0.wireOp",EDGE,"E1229"),sQuery(id+"F0.wireOp",EDGE,"E1230"),sQuery(id+"F0.wireOp",EDGE,"E1231"),sQuery(id+"F0.wireOp",EDGE,"E1232"),sQuery(id+"F0.wireOp",EDGE,"E1233"),sQuery(id+"F0.wireOp",EDGE,"E1234"),sQuery(id+"F0.wireOp",EDGE,"E1235"),sQuery(id+"F0.wireOp",EDGE,"E1236"),sQuery(id+"F0.wireOp",EDGE,"E1237"),sQuery(id+"F0.wireOp",EDGE,"E1238"),sQuery(id+"F0.wireOp",EDGE,"E1239"),sQuery(id+"F0.wireOp",EDGE,"E1240"),sQuery(id+"F0.wireOp",EDGE,"E1241"),sQuery(id+"F0.wireOp",EDGE,"E1242"),sQuery(id+"F0.wireOp",EDGE,"E1243"),sQuery(id+"F0.wireOp",EDGE,"E1244"),sQuery(id+"F0.wireOp",EDGE,"E1245"),sQuery(id+"F0.wireOp",EDGE,"E1246"),sQuery(id+"F0.wireOp",EDGE,"E1247"),sQuery(id+"F0.wireOp",EDGE,"E1248"),sQuery(id+"F0.wireOp",EDGE,"E1249"),sQuery(id+"F0.wireOp",EDGE,"E1250"),sQuery(id+"F0.wireOp",EDGE,"E1251"),sQuery(id+"F0.wireOp",EDGE,"E1252"),sQuery(id+"F0.wireOp",EDGE,"E1253"),sQuery(id+"F0.wireOp",EDGE,"E1254"),sQuery(id+"F0.wireOp",EDGE,"E1255"),sQuery(id+"F0.wireOp",EDGE,"E1256"),sQuery(id+"F0.wireOp",EDGE,"E1257"),sQuery(id+"F0.wireOp",EDGE,"E1258"),sQuery(id+"F0.wireOp",EDGE,"E1259"),sQuery(id+"F0.wireOp",EDGE,"E1260"),sQuery(id+"F0.wireOp",EDGE,"E1261"),sQuery(id+"F0.wireOp",EDGE,"E1262"),sQuery(id+"F0.wireOp",EDGE,"E1263"),sQuery(id+"F0.wireOp",EDGE,"E1264"),sQuery(id+"F0.wireOp",EDGE,"E1265"),sQuery(id+"F0.wireOp",EDGE,"E1266"),sQuery(id+"F0.wireOp",EDGE,"E1267"),sQuery(id+"F0.wireOp",EDGE,"E1268"),sQuery(id+"F0.wireOp",EDGE,"E1269"),sQuery(id+"F0.wireOp",EDGE,"E1270"),sQuery(id+"F0.wireOp",EDGE,"E1271"),sQuery(id+"F0.wireOp",EDGE,"E1272"),sQuery(id+"F0.wireOp",EDGE,"E1273"),sQuery(id+"F0.wireOp",EDGE,"E1274"),sQuery(id+"F0.wireOp",EDGE,"E1275"),sQuery(id+"F0.wireOp",EDGE,"E1276"),sQuery(id+"F0.wireOp",EDGE,"E1277"),sQuery(id+"F0.wireOp",EDGE,"E1278"),sQuery(id+"F0.wireOp",EDGE,"E1279"),sQuery(id+"F0.wireOp",EDGE,"E1280"),sQuery(id+"F0.wireOp",EDGE,"E1281"),sQuery(id+"F0.wireOp",EDGE,"E1282"),sQuery(id+"F0.wireOp",EDGE,"E1283"),sQuery(id+"F0.wireOp",EDGE,"E1284"),sQuery(id+"F0.wireOp",EDGE,"E1285"),sQuery(id+"F0.wireOp",EDGE,"E1286"),sQuery(id+"F0.wireOp",EDGE,"E1287"),sQuery(id+"F0.wireOp",EDGE,"E1288"),sQuery(id+"F0.wireOp",EDGE,"E1289"),sQuery(id+"F0.wireOp",EDGE,"E1290"),sQuery(id+"F0.wireOp",EDGE,"E1291"),sQuery(id+"F0.wireOp",EDGE,"E1292"),sQuery(id+"F0.wireOp",EDGE,"E1293"),sQuery(id+"F0.wireOp",EDGE,"E1294"),sQuery(id+"F0.wireOp",EDGE,"E1295"),sQuery(id+"F0.wireOp",EDGE,"E1296"),sQuery(id+"F0.wireOp",EDGE,"E1297"),sQuery(id+"F0.wireOp",EDGE,"E1298"),sQuery(id+"F0.wireOp",EDGE,"E1299"),sQuery(id+"F0.wireOp",EDGE,"E1300"),sQuery(id+"F0.wireOp",EDGE,"E1301"),sQuery(id+"F0.wireOp",EDGE,"E1302"),sQuery(id+"F0.wireOp",EDGE,"E1303"),sQuery(id+"F0.wireOp",EDGE,"E1304"),sQuery(id+"F0.wireOp",EDGE,"E1305"),sQuery(id+"F0.wireOp",EDGE,"E1306"),sQuery(id+"F0.wireOp",EDGE,"E1307"),sQuery(id+"F0.wireOp",EDGE,"E1308"),sQuery(id+"F0.wireOp",EDGE,"E1309"),sQuery(id+"F0.wireOp",EDGE,"E1310"),sQuery(id+"F0.wireOp",EDGE,"E1311"),sQuery(id+"F0.wireOp",EDGE,"E1312"),sQuery(id+"F0.wireOp",EDGE,"E1313"),sQuery(id+"F0.wireOp",EDGE,"E1314"),sQuery(id+"F0.wireOp",EDGE,"E1315"),sQuery(id+"F0.wireOp",EDGE,"E1316"),sQuery(id+"F0.wireOp",EDGE,"E1317"),sQuery(id+"F0.wireOp",EDGE,"E1318"),sQuery(id+"F0.wireOp",EDGE,"E1319"),sQuery(id+"F0.wireOp",EDGE,"E1320"),sQuery(id+"F0.wireOp",EDGE,"E1321"),sQuery(id+"F0.wireOp",EDGE,"E1322"),sQuery(id+"F0.wireOp",EDGE,"E1323"),sQuery(id+"F0.wireOp",EDGE,"E1324"),sQuery(id+"F0.wireOp",EDGE,"E1325"),sQuery(id+"F0.wireOp",EDGE,"E1326"),sQuery(id+"F0.wireOp",EDGE,"E1327"),sQuery(id+"F0.wireOp",EDGE,"E1328"),sQuery(id+"F0.wireOp",EDGE,"E1329"),sQuery(id+"F0.wireOp",EDGE,"E1330"),sQuery(id+"F0.wireOp",EDGE,"E1331"),sQuery(id+"F0.wireOp",EDGE,"E1332"),sQuery(id+"F0.wireOp",EDGE,"E1333"),sQuery(id+"F0.wireOp",EDGE,"E1334"),sQuery(id+"F0.wireOp",EDGE,"E1335"),sQuery(id+"F0.wireOp",EDGE,"E1336"),sQuery(id+"F0.wireOp",EDGE,"E1337"),sQuery(id+"F0.wireOp",EDGE,"E1338"),sQuery(id+"F0.wireOp",EDGE,"E1339"),sQuery(id+"F0.wireOp",EDGE,"E1340"),sQuery(id+"F0.wireOp",EDGE,"E1341"),sQuery(id+"F0.wireOp",EDGE,"E1342"),sQuery(id+"F0.wireOp",EDGE,"E1343"),sQuery(id+"F0.wireOp",EDGE,"E1344"),sQuery(id+"F0.wireOp",EDGE,"E1345"),sQuery(id+"F0.wireOp",EDGE,"E1346"),sQuery(id+"F0.wireOp",EDGE,"E1347"),sQuery(id+"F0.wireOp",EDGE,"E1348"),sQuery(id+"F0.wireOp",EDGE,"E1349"),sQuery(id+"F0.wireOp",EDGE,"E1350"),sQuery(id+"F0.wireOp",EDGE,"E1351"),sQuery(id+"F0.wireOp",EDGE,"E1352"),sQuery(id+"F0.wireOp",EDGE,"E1353"),sQuery(id+"F0.wireOp",EDGE,"E1354"),sQuery(id+"F0.wireOp",EDGE,"E1355"),sQuery(id+"F0.wireOp",EDGE,"E1356"),sQuery(id+"F0.wireOp",EDGE,"E1357"),sQuery(id+"F0.wireOp",EDGE,"E1358"),sQuery(id+"F0.wireOp",EDGE,"E1359"),sQuery(id+"F0.wireOp",EDGE,"E1360"),sQuery(id+"F0.wireOp",EDGE,"E1361"),sQuery(id+"F0.wireOp",EDGE,"E1362"),sQuery(id+"F0.wireOp",EDGE,"E1363"),sQuery(id+"F0.wireOp",EDGE,"E1364"),sQuery(id+"F0.wireOp",EDGE,"E1365"),sQuery(id+"F0.wireOp",EDGE,"E1366"),sQuery(id+"F0.wireOp",EDGE,"E1367"),sQuery(id+"F0.wireOp",EDGE,"E1368"),sQuery(id+"F0.wireOp",EDGE,"E1369"),sQuery(id+"F0.wireOp",EDGE,"E1370"),sQuery(id+"F0.wireOp",EDGE,"E1371"),sQuery(id+"F0.wireOp",EDGE,"E1372"),sQuery(id+"F0.wireOp",EDGE,"E1373"),sQuery(id+"F0.wireOp",EDGE,"E1374"),sQuery(id+"F0.wireOp",EDGE,"E1375"),sQuery(id+"F0.wireOp",EDGE,"E1376"),sQuery(id+"F0.wireOp",EDGE,"E1377"),sQuery(id+"F0.wireOp",EDGE,"E1378"),sQuery(id+"F0.wireOp",EDGE,"E1379"),sQuery(id+"F0.wireOp",EDGE,"E1380"),sQuery(id+"F0.wireOp",EDGE,"E1381"),sQuery(id+"F0.wireOp",EDGE,"E1382"),sQuery(id+"F0.wireOp",EDGE,"E1383"),sQuery(id+"F0.wireOp",EDGE,"E1384"),sQuery(id+"F0.wireOp",EDGE,"E1385"),sQuery(id+"F0.wireOp",EDGE,"E1386"),sQuery(id+"F0.wireOp",EDGE,"E1387"),sQuery(id+"F0.wireOp",EDGE,"E1388"),sQuery(id+"F0.wireOp",EDGE,"E1389"),sQuery(id+"F0.wireOp",EDGE,"E1390"),sQuery(id+"F0.wireOp",EDGE,"E1391"),sQuery(id+"F0.wireOp",EDGE,"E1392"),sQuery(id+"F0.wireOp",EDGE,"E1393"),sQuery(id+"F0.wireOp",EDGE,"E1394"),sQuery(id+"F0.wireOp",EDGE,"E1395"),sQuery(id+"F0.wireOp",EDGE,"E1396"),sQuery(id+"F0.wireOp",EDGE,"E1397"),sQuery(id+"F0.wireOp",EDGE,"E1398"),sQuery(id+"F0.wireOp",EDGE,"E1399"),sQuery(id+"F0.wireOp",EDGE,"E1400"),sQuery(id+"F0.wireOp",EDGE,"E1401"),sQuery(id+"F0.wireOp",EDGE,"E1402"),sQuery(id+"F0.wireOp",EDGE,"E1403"),sQuery(id+"F0.wireOp",EDGE,"E1404"),sQuery(id+"F0.wireOp",EDGE,"E1405"),sQuery(id+"F0.wireOp",EDGE,"E1406"),sQuery(id+"F0.wireOp",EDGE,"E1407"),sQuery(id+"F0.wireOp",EDGE,"E1408"),sQuery(id+"F0.wireOp",EDGE,"E1409"),sQuery(id+"F0.wireOp",EDGE,"E1410"),sQuery(id+"F0.wireOp",EDGE,"E1411"),sQuery(id+"F0.wireOp",EDGE,"E1412"),sQuery(id+"F0.wireOp",EDGE,"E1413"),sQuery(id+"F0.wireOp",EDGE,"E1414"),sQuery(id+"F0.wireOp",EDGE,"E1415"),sQuery(id+"F0.wireOp",EDGE,"E1416"),sQuery(id+"F0.wireOp",EDGE,"E1417"),sQuery(id+"F0.wireOp",EDGE,"E1418"),sQuery(id+"F0.wireOp",EDGE,"E1419"),sQuery(id+"F0.wireOp",EDGE,"E1420"),sQuery(id+"F0.wireOp",EDGE,"E1421"),sQuery(id+"F0.wireOp",EDGE,"E1422"),sQuery(id+"F0.wireOp",EDGE,"E1423"),sQuery(id+"F0.wireOp",EDGE,"E1424"),sQuery(id+"F0.wireOp",EDGE,"E1425"),sQuery(id+"F0.wireOp",EDGE,"E1426"),sQuery(id+"F0.wireOp",EDGE,"E1427"),sQuery(id+"F0.wireOp",EDGE,"E1428"),sQuery(id+"F0.wireOp",EDGE,"E1429"),sQuery(id+"F0.wireOp",EDGE,"E1430"),sQuery(id+"F0.wireOp",EDGE,"E1431"),sQuery(id+"F0.wireOp",EDGE,"E1432"),sQuery(id+"F0.wireOp",EDGE,"E1433"),sQuery(id+"F0.wireOp",EDGE,"E1434"),sQuery(id+"F0.wireOp",EDGE,"E1435"),sQuery(id+"F0.wireOp",EDGE,"E1436"),sQuery(id+"F0.wireOp",EDGE,"E1437"),sQuery(id+"F0.wireOp",EDGE,"E1438"),sQuery(id+"F0.wireOp",EDGE,"E1439"),sQuery(id+"F0.wireOp",EDGE,"E1440"),sQuery(id+"F0.wireOp",EDGE,"E1441"),sQuery(id+"F0.wireOp",EDGE,"E1442"),sQuery(id+"F0.wireOp",EDGE,"E1443"),sQuery(id+"F0.wireOp",EDGE,"E1444"),sQuery(id+"F0.wireOp",EDGE,"E1445"),sQuery(id+"F0.wireOp",EDGE,"E1446"),sQuery(id+"F0.wireOp",EDGE,"E1447"),sQuery(id+"F0.wireOp",EDGE,"E1448"),sQuery(id+"F0.wireOp",EDGE,"E1449"),sQuery(id+"F0.wireOp",EDGE,"E1450"),sQuery(id+"F0.wireOp",EDGE,"E1451"),sQuery(id+"F0.wireOp",EDGE,"E1452"),sQuery(id+"F0.wireOp",EDGE,"E1453"),sQuery(id+"F0.wireOp",EDGE,"E1454"),sQuery(id+"F0.wireOp",EDGE,"E1455"),sQuery(id+"F0.wireOp",EDGE,"E1456"),sQuery(id+"F0.wireOp",EDGE,"E1457"),sQuery(id+"F0.wireOp",EDGE,"E1458"),sQuery(id+"F0.wireOp",EDGE,"E1459"),sQuery(id+"F0.wireOp",EDGE,"E1460"),sQuery(id+"F0.wireOp",EDGE,"E1461"),sQuery(id+"F0.wireOp",EDGE,"E1462"),sQuery(id+"F0.wireOp",EDGE,"E1463"),sQuery(id+"F0.wireOp",EDGE,"E1464"),sQuery(id+"F0.wireOp",EDGE,"E1465"),sQuery(id+"F0.wireOp",EDGE,"E1466"),sQuery(id+"F0.wireOp",EDGE,"E1467"),sQuery(id+"F0.wireOp",EDGE,"E1468"),sQuery(id+"F0.wireOp",EDGE,"E1469"),sQuery(id+"F0.wireOp",EDGE,"E1470"),sQuery(id+"F0.wireOp",EDGE,"E1471"),sQuery(id+"F0.wireOp",EDGE,"E1472"),sQuery(id+"F0.wireOp",EDGE,"E1473"),sQuery(id+"F0.wireOp",EDGE,"E1474"),sQuery(id+"F0.wireOp",EDGE,"E1475"),sQuery(id+"F0.wireOp",EDGE,"E1476"),sQuery(id+"F0.wireOp",EDGE,"E1477"),sQuery(id+"F0.wireOp",EDGE,"E1478"),sQuery(id+"F0.wireOp",EDGE,"E1479"),sQuery(id+"F0.wireOp",EDGE,"E1480"),sQuery(id+"F0.wireOp",EDGE,"E1481"),sQuery(id+"F0.wireOp",EDGE,"E1482"),sQuery(id+"F0.wireOp",EDGE,"E1483"),sQuery(id+"F0.wireOp",EDGE,"E1484"),sQuery(id+"F0.wireOp",EDGE,"E1485"),sQuery(id+"F0.wireOp",EDGE,"E1486"),sQuery(id+"F0.wireOp",EDGE,"E1487"),sQuery(id+"F0.wireOp",EDGE,"E1488"),sQuery(id+"F0.wireOp",EDGE,"E1489"),sQuery(id+"F0.wireOp",EDGE,"E1490"),sQuery(id+"F0.wireOp",EDGE,"E1491"),sQuery(id+"F0.wireOp",EDGE,"E1492"),sQuery(id+"F0.wireOp",EDGE,"E1493"),sQuery(id+"F0.wireOp",EDGE,"E1494"),sQuery(id+"F0.wireOp",EDGE,"E1495"),sQuery(id+"F0.wireOp",EDGE,"E1496"),sQuery(id+"F0.wireOp",EDGE,"E1497"),sQuery(id+"F0.wireOp",EDGE,"E1498"),sQuery(id+"F0.wireOp",EDGE,"E1499"),sQuery(id+"F0.wireOp",EDGE,"E1500"),sQuery(id+"F0.wireOp",EDGE,"E1501"),sQuery(id+"F0.wireOp",EDGE,"E1502"),sQuery(id+"F0.wireOp",EDGE,"E1503"),sQuery(id+"F0.wireOp",EDGE,"E1504"),sQuery(id+"F0.wireOp",EDGE,"E1505"),sQuery(id+"F0.wireOp",EDGE,"E1506"),sQuery(id+"F0.wireOp",EDGE,"E1507"),sQuery(id+"F0.wireOp",EDGE,"E1508"),sQuery(id+"F0.wireOp",EDGE,"E1509"),sQuery(id+"F0.wireOp",EDGE,"E1510"),sQuery(id+"F0.wireOp",EDGE,"E1511"),sQuery(id+"F0.wireOp",EDGE,"E1512"),sQuery(id+"F0.wireOp",EDGE,"E1513"),sQuery(id+"F0.wireOp",EDGE,"E1514"),sQuery(id+"F0.wireOp",EDGE,"E1515"),sQuery(id+"F0.wireOp",EDGE,"E1516"),sQuery(id+"F0.wireOp",EDGE,"E1517"),sQuery(id+"F0.wireOp",EDGE,"E1518"),sQuery(id+"F0.wireOp",EDGE,"E1519"),sQuery(id+"F0.wireOp",EDGE,"E1520"),sQuery(id+"F0.wireOp",EDGE,"E1521"),sQuery(id+"F0.wireOp",EDGE,"E1522"),sQuery(id+"F0.wireOp",EDGE,"E1523"),sQuery(id+"F0.wireOp",EDGE,"E1524"),sQuery(id+"F0.wireOp",EDGE,"E1525"),sQuery(id+"F0.wireOp",EDGE,"E1526"),sQuery(id+"F0.wireOp",EDGE,"E1527"),sQuery(id+"F0.wireOp",EDGE,"E1528"),sQuery(id+"F0.wireOp",EDGE,"E1529"),sQuery(id+"F0.wireOp",EDGE,"E1530"),sQuery(id+"F0.wireOp",EDGE,"E1531"),sQuery(id+"F0.wireOp",EDGE,"E1532"),sQuery(id+"F0.wireOp",EDGE,"E1533"),sQuery(id+"F0.wireOp",EDGE,"E1534"),sQuery(id+"F0.wireOp",EDGE,"E1535"),sQuery(id+"F0.wireOp",EDGE,"E1536"),sQuery(id+"F0.wireOp",EDGE,"E1537"),sQuery(id+"F0.wireOp",EDGE,"E1538"),sQuery(id+"F0.wireOp",EDGE,"E1539"),sQuery(id+"F0.wireOp",EDGE,"E1540"),sQuery(id+"F0.wireOp",EDGE,"E1541"),sQuery(id+"F0.wireOp",EDGE,"E1542"),sQuery(id+"F0.wireOp",EDGE,"E1543"),sQuery(id+"F0.wireOp",EDGE,"E1544"),sQuery(id+"F0.wireOp",EDGE,"E1545"),sQuery(id+"F0.wireOp",EDGE,"E1546"),sQuery(id+"F0.wireOp",EDGE,"E1547"),sQuery(id+"F0.wireOp",EDGE,"E1548"),sQuery(id+"F0.wireOp",EDGE,"E1549"),sQuery(id+"F0.wireOp",EDGE,"E1550"),sQuery(id+"F0.wireOp",EDGE,"E1551"),sQuery(id+"F0.wireOp",EDGE,"E1552"),sQuery(id+"F0.wireOp",EDGE,"E1553"),sQuery(id+"F0.wireOp",EDGE,"E1554"),sQuery(id+"F0.wireOp",EDGE,"E1555"),sQuery(id+"F0.wireOp",EDGE,"E1556"),sQuery(id+"F0.wireOp",EDGE,"E1557"),sQuery(id+"F0.wireOp",EDGE,"E1558"),sQuery(id+"F0.wireOp",EDGE,"E1559"),sQuery(id+"F0.wireOp",EDGE,"E1560"),sQuery(id+"F0.wireOp",EDGE,"E1561"),sQuery(id+"F0.wireOp",EDGE,"E1562"),sQuery(id+"F0.wireOp",EDGE,"E1563"),sQuery(id+"F0.wireOp",EDGE,"E1564"),sQuery(id+"F0.wireOp",EDGE,"E1565"),sQuery(id+"F0.wireOp",EDGE,"E1566"),sQuery(id+"F0.wireOp",EDGE,"E1567"),sQuery(id+"F0.wireOp",EDGE,"E1568"),sQuery(id+"F0.wireOp",EDGE,"E1569"),sQuery(id+"F0.wireOp",EDGE,"E1570"),sQuery(id+"F0.wireOp",EDGE,"E1571"),sQuery(id+"F0.wireOp",EDGE,"E1572"),sQuery(id+"F0.wireOp",EDGE,"E1573"),sQuery(id+"F0.wireOp",EDGE,"E1574"),sQuery(id+"F0.wireOp",EDGE,"E1575"),sQuery(id+"F0.wireOp",EDGE,"E1576"),sQuery(id+"F0.wireOp",EDGE,"E1577"),sQuery(id+"F0.wireOp",EDGE,"E1578"),sQuery(id+"F0.wireOp",EDGE,"E1579"),sQuery(id+"F0.wireOp",EDGE,"E1580"),sQuery(id+"F0.wireOp",EDGE,"E1581"),sQuery(id+"F0.wireOp",EDGE,"E1582"),sQuery(id+"F0.wireOp",EDGE,"E1583"),sQuery(id+"F0.wireOp",EDGE,"E1584"),sQuery(id+"F0.wireOp",EDGE,"E1585"),sQuery(id+"F0.wireOp",EDGE,"E1586"),sQuery(id+"F0.wireOp",EDGE,"E1587"),sQuery(id+"F0.wireOp",EDGE,"E1588"),sQuery(id+"F0.wireOp",EDGE,"E1589"),sQuery(id+"F0.wireOp",EDGE,"E1590"),sQuery(id+"F0.wireOp",EDGE,"E1591"),sQuery(id+"F0.wireOp",EDGE,"E1592"),sQuery(id+"F0.wireOp",EDGE,"E1593"),sQuery(id+"F0.wireOp",EDGE,"E1594"),sQuery(id+"F0.wireOp",EDGE,"E1595"),sQuery(id+"F0.wireOp",EDGE,"E1596"),sQuery(id+"F0.wireOp",EDGE,"E1597"),sQuery(id+"F0.wireOp",EDGE,"E1598"),sQuery(id+"F0.wireOp",EDGE,"E1599"),sQuery(id+"F0.wireOp",EDGE,"E1600"),sQuery(id+"F0.wireOp",EDGE,"E1601"),sQuery(id+"F0.wireOp",EDGE,"E1602"),sQuery(id+"F0.wireOp",EDGE,"E1603"),sQuery(id+"F0.wireOp",EDGE,"E1604"),sQuery(id+"F0.wireOp",EDGE,"E1605"),sQuery(id+"F0.wireOp",EDGE,"E1606"),sQuery(id+"F0.wireOp",EDGE,"E1607"),sQuery(id+"F0.wireOp",EDGE,"E1608"),sQuery(id+"F0.wireOp",EDGE,"E1609"),sQuery(id+"F0.wireOp",EDGE,"E1610"),sQuery(id+"F0.wireOp",EDGE,"E1611"),sQuery(id+"F0.wireOp",EDGE,"E1612"),sQuery(id+"F0.wireOp",EDGE,"E1613"),sQuery(id+"F0.wireOp",EDGE,"E1614"),sQuery(id+"F0.wireOp",EDGE,"E1615"),sQuery(id+"F0.wireOp",EDGE,"E1616"),sQuery(id+"F0.wireOp",EDGE,"E1617"),sQuery(id+"F0.wireOp",EDGE,"E1618"),sQuery(id+"F0.wireOp",EDGE,"E1619"),sQuery(id+"F0.wireOp",EDGE,"E1620"),sQuery(id+"F0.wireOp",EDGE,"E1621"),sQuery(id+"F0.wireOp",EDGE,"E1622"),sQuery(id+"F0.wireOp",EDGE,"E1623"),sQuery(id+"F0.wireOp",EDGE,"E1624"),sQuery(id+"F0.wireOp",EDGE,"E1625"),sQuery(id+"F0.wireOp",EDGE,"E1626"),sQuery(id+"F0.wireOp",EDGE,"E1627"),sQuery(id+"F0.wireOp",EDGE,"E1628"),sQuery(id+"F0.wireOp",EDGE,"E1629"),sQuery(id+"F0.wireOp",EDGE,"E1630"),sQuery(id+"F0.wireOp",EDGE,"E1631"),sQuery(id+"F0.wireOp",EDGE,"E1632"),sQuery(id+"F0.wireOp",EDGE,"E1633"),sQuery(id+"F0.wireOp",EDGE,"E1634"),sQuery(id+"F0.wireOp",EDGE,"E1635"),sQuery(id+"F0.wireOp",EDGE,"E1636"),sQuery(id+"F0.wireOp",EDGE,"E1637"),sQuery(id+"F0.wireOp",EDGE,"E1638"),sQuery(id+"F0.wireOp",EDGE,"E1639"),sQuery(id+"F0.wireOp",EDGE,"E1640"),sQuery(id+"F0.wireOp",EDGE,"E1641"),sQuery(id+"F0.wireOp",EDGE,"E1642"),sQuery(id+"F0.wireOp",EDGE,"E1643"),sQuery(id+"F0.wireOp",EDGE,"E1644"),sQuery(id+"F0.wireOp",EDGE,"E1645"),sQuery(id+"F0.wireOp",EDGE,"E1646"),sQuery(id+"F0.wireOp",EDGE,"E1647"),sQuery(id+"F0.wireOp",EDGE,"E1648"),sQuery(id+"F0.wireOp",EDGE,"E1649"),sQuery(id+"F0.wireOp",EDGE,"E1650"),sQuery(id+"F0.wireOp",EDGE,"E1651"),sQuery(id+"F0.wireOp",EDGE,"E1652"),sQuery(id+"F0.wireOp",EDGE,"E1653"),sQuery(id+"F0.wireOp",EDGE,"E1654"),sQuery(id+"F0.wireOp",EDGE,"E1655"),sQuery(id+"F0.wireOp",EDGE,"E1656"),sQuery(id+"F0.wireOp",EDGE,"E1657"),sQuery(id+"F0.wireOp",EDGE,"E1658"),sQuery(id+"F0.wireOp",EDGE,"E1659"),sQuery(id+"F0.wireOp",EDGE,"E1660"),sQuery(id+"F0.wireOp",EDGE,"E1661"),sQuery(id+"F0.wireOp",EDGE,"E1662"),sQuery(id+"F0.wireOp",EDGE,"E1663"),sQuery(id+"F0.wireOp",EDGE,"E1664"),sQuery(id+"F0.wireOp",EDGE,"E1665"),sQuery(id+"F0.wireOp",EDGE,"E1666"),sQuery(id+"F0.wireOp",EDGE,"E1667"),sQuery(id+"F0.wireOp",EDGE,"E1668"),sQuery(id+"F0.wireOp",EDGE,"E1669"),sQuery(id+"F0.wireOp",EDGE,"E1670"),sQuery(id+"F0.wireOp",EDGE,"E1671"),sQuery(id+"F0.wireOp",EDGE,"E1672"),sQuery(id+"F0.wireOp",EDGE,"E1673"),sQuery(id+"F0.wireOp",EDGE,"E1674"),sQuery(id+"F0.wireOp",EDGE,"E1675"),sQuery(id+"F0.wireOp",EDGE,"E1676"),sQuery(id+"F0.wireOp",EDGE,"E1677"),sQuery(id+"F0.wireOp",EDGE,"E1678"),sQuery(id+"F0.wireOp",EDGE,"E1679"),sQuery(id+"F0.wireOp",EDGE,"E1680"),sQuery(id+"F0.wireOp",EDGE,"E1681"),sQuery(id+"F0.wireOp",EDGE,"E1682"),sQuery(id+"F0.wireOp",EDGE,"E1683"),sQuery(id+"F0.wireOp",EDGE,"E1684"),sQuery(id+"F0.wireOp",EDGE,"E1685"),sQuery(id+"F0.wireOp",EDGE,"E1686"),sQuery(id+"F0.wireOp",EDGE,"E1687"),sQuery(id+"F0.wireOp",EDGE,"E1688"),sQuery(id+"F0.wireOp",EDGE,"E1689"),sQuery(id+"F0.wireOp",EDGE,"E1690"),sQuery(id+"F0.wireOp",EDGE,"E1691"),sQuery(id+"F0.wireOp",EDGE,"E1692"),sQuery(id+"F0.wireOp",EDGE,"E1693"),sQuery(id+"F0.wireOp",EDGE,"E1694"),sQuery(id+"F0.wireOp",EDGE,"E1695"),sQuery(id+"F0.wireOp",EDGE,"E1696"),sQuery(id+"F0.wireOp",EDGE,"E1697"),sQuery(id+"F0.wireOp",EDGE,"E1698"),sQuery(id+"F0.wireOp",EDGE,"E1699"),sQuery(id+"F0.wireOp",EDGE,"E1700"),sQuery(id+"F0.wireOp",EDGE,"E1701"),sQuery(id+"F0.wireOp",EDGE,"E1702"),sQuery(id+"F0.wireOp",EDGE,"E1703"),sQuery(id+"F0.wireOp",EDGE,"E1704"),sQuery(id+"F0.wireOp",EDGE,"E1705"),sQuery(id+"F0.wireOp",EDGE,"E1706"),sQuery(id+"F0.wireOp",EDGE,"E1707"),sQuery(id+"F0.wireOp",EDGE,"E1708"),sQuery(id+"F0.wireOp",EDGE,"E1709"),sQuery(id+"F0.wireOp",EDGE,"E1710"),sQuery(id+"F0.wireOp",EDGE,"E1711"),sQuery(id+"F0.wireOp",EDGE,"E1712"),sQuery(id+"F0.wireOp",EDGE,"E1713"),sQuery(id+"F0.wireOp",EDGE,"E1714"),sQuery(id+"F0.wireOp",EDGE,"E1715"),sQuery(id+"F0.wireOp",EDGE,"E1716"),sQuery(id+"F0.wireOp",EDGE,"E1717"),sQuery(id+"F0.wireOp",EDGE,"E1718"),sQuery(id+"F0.wireOp",EDGE,"E1719"),sQuery(id+"F0.wireOp",EDGE,"E1720"),sQuery(id+"F0.wireOp",EDGE,"E1721"),sQuery(id+"F0.wireOp",EDGE,"E1722"),sQuery(id+"F0.wireOp",EDGE,"E1723"),sQuery(id+"F0.wireOp",EDGE,"E1724"),sQuery(id+"F0.wireOp",EDGE,"E1725"),sQuery(id+"F0.wireOp",EDGE,"E1726"),sQuery(id+"F0.wireOp",EDGE,"E1727"),sQuery(id+"F0.wireOp",EDGE,"E1728"),sQuery(id+"F0.wireOp",EDGE,"E1729"),sQuery(id+"F0.wireOp",EDGE,"E1730"),sQuery(id+"F0.wireOp",EDGE,"E1731"),sQuery(id+"F0.wireOp",EDGE,"E1732"),sQuery(id+"F0.wireOp",EDGE,"E1733"),sQuery(id+"F0.wireOp",EDGE,"E1734"),sQuery(id+"F0.wireOp",EDGE,"E1735"),sQuery(id+"F0.wireOp",EDGE,"E1736"),sQuery(id+"F0.wireOp",EDGE,"E1737"),sQuery(id+"F0.wireOp",EDGE,"E1738"),sQuery(id+"F0.wireOp",EDGE,"E1739"),sQuery(id+"F0.wireOp",EDGE,"E1740"),sQuery(id+"F0.wireOp",EDGE,"E1741"),sQuery(id+"F0.wireOp",EDGE,"E1742"),sQuery(id+"F0.wireOp",EDGE,"E1743"),sQuery(id+"F0.wireOp",EDGE,"E1744"),sQuery(id+"F0.wireOp",EDGE,"E1745"),sQuery(id+"F0.wireOp",EDGE,"E1746"),sQuery(id+"F0.wireOp",EDGE,"E1747"),sQuery(id+"F0.wireOp",EDGE,"E1748"),sQuery(id+"F0.wireOp",EDGE,"E1749"),sQuery(id+"F0.wireOp",EDGE,"E1750"),sQuery(id+"F0.wireOp",EDGE,"E1751"),sQuery(id+"F0.wireOp",EDGE,"E1752"),sQuery(id+"F0.wireOp",EDGE,"E1753"),sQuery(id+"F0.wireOp",EDGE,"E1754"),sQuery(id+"F0.wireOp",EDGE,"E1755"),sQuery(id+"F0.wireOp",EDGE,"E1756"),sQuery(id+"F0.wireOp",EDGE,"E1757"),sQuery(id+"F0.wireOp",EDGE,"E1758"),sQuery(id+"F0.wireOp",EDGE,"E1759"),sQuery(id+"F0.wireOp",EDGE,"E1760"),sQuery(id+"F0.wireOp",EDGE,"E1761"),sQuery(id+"F0.wireOp",EDGE,"E1762"),sQuery(id+"F0.wireOp",EDGE,"E1763"),sQuery(id+"F0.wireOp",EDGE,"E1764"),sQuery(id+"F0.wireOp",EDGE,"E1765"),sQuery(id+"F0.wireOp",EDGE,"E1766"),sQuery(id+"F0.wireOp",EDGE,"E1767"),sQuery(id+"F0.wireOp",EDGE,"E1768"),sQuery(id+"F0.wireOp",EDGE,"E1769"),sQuery(id+"F0.wireOp",EDGE,"E1770"),sQuery(id+"F0.wireOp",EDGE,"E1771"),sQuery(id+"F0.wireOp",EDGE,"E1772"),sQuery(id+"F0.wireOp",EDGE,"E1773"),sQuery(id+"F0.wireOp",EDGE,"E1774"),sQuery(id+"F0.wireOp",EDGE,"E1775"),sQuery(id+"F0.wireOp",EDGE,"E1776"),sQuery(id+"F0.wireOp",EDGE,"E1777"),sQuery(id+"F0.wireOp",EDGE,"E1778"),sQuery(id+"F0.wireOp",EDGE,"E1779"),sQuery(id+"F0.wireOp",EDGE,"E1780"),sQuery(id+"F0.wireOp",EDGE,"E1781"),sQuery(id+"F0.wireOp",EDGE,"E1782"),sQuery(id+"F0.wireOp",EDGE,"E1783"),sQuery(id+"F0.wireOp",EDGE,"E1784"),sQuery(id+"F0.wireOp",EDGE,"E1785"),sQuery(id+"F0.wireOp",EDGE,"E1786"),sQuery(id+"F0.wireOp",EDGE,"E1787"),sQuery(id+"F0.wireOp",EDGE,"E1788"),sQuery(id+"F0.wireOp",EDGE,"E1789"),sQuery(id+"F0.wireOp",EDGE,"E1790"),sQuery(id+"F0.wireOp",EDGE,"E1791"),sQuery(id+"F0.wireOp",EDGE,"E1792"),sQuery(id+"F0.wireOp",EDGE,"E1793"),sQuery(id+"F0.wireOp",EDGE,"E1794"),sQuery(id+"F0.wireOp",EDGE,"E1795"),sQuery(id+"F0.wireOp",EDGE,"E1796"),sQuery(id+"F0.wireOp",EDGE,"E1797"),sQuery(id+"F0.wireOp",EDGE,"E1798"),sQuery(id+"F0.wireOp",EDGE,"E1799"),sQuery(id+"F0.wireOp",EDGE,"E1800"),sQuery(id+"F0.wireOp",EDGE,"E1801"),sQuery(id+"F0.wireOp",EDGE,"E1802"),sQuery(id+"F0.wireOp",EDGE,"E1803"),sQuery(id+"F0.wireOp",EDGE,"E1804"),sQuery(id+"F0.wireOp",EDGE,"E1805"),sQuery(id+"F0.wireOp",EDGE,"E1806"),sQuery(id+"F0.wireOp",EDGE,"E1807"),sQuery(id+"F0.wireOp",EDGE,"E1808"),sQuery(id+"F0.wireOp",EDGE,"E1809"),sQuery(id+"F0.wireOp",EDGE,"E1810"),sQuery(id+"F0.wireOp",EDGE,"E1811"),sQuery(id+"F0.wireOp",EDGE,"E1812"),sQuery(id+"F0.wireOp",EDGE,"E1813"),sQuery(id+"F0.wireOp",EDGE,"E1814"),sQuery(id+"F0.wireOp",EDGE,"E1815"),sQuery(id+"F0.wireOp",EDGE,"E1816"),sQuery(id+"F0.wireOp",EDGE,"E1817"),sQuery(id+"F0.wireOp",EDGE,"E1818"),sQuery(id+"F0.wireOp",EDGE,"E1819"),sQuery(id+"F0.wireOp",EDGE,"E1820"),sQuery(id+"F0.wireOp",EDGE,"E1821"),sQuery(id+"F0.wireOp",EDGE,"E1822"),sQuery(id+"F0.wireOp",EDGE,"E1823"),sQuery(id+"F0.wireOp",EDGE,"E1824"),sQuery(id+"F0.wireOp",EDGE,"E1825"),sQuery(id+"F0.wireOp",EDGE,"E1826"),sQuery(id+"F0.wireOp",EDGE,"E1827"),sQuery(id+"F0.wireOp",EDGE,"E1828"),sQuery(id+"F0.wireOp",EDGE,"E1829"),sQuery(id+"F0.wireOp",EDGE,"E1830"),sQuery(id+"F0.wireOp",EDGE,"E1831"),sQuery(id+"F0.wireOp",EDGE,"E1832"),sQuery(id+"F0.wireOp",EDGE,"E1833"),sQuery(id+"F0.wireOp",EDGE,"E1834"),sQuery(id+"F0.wireOp",EDGE,"E1835"),sQuery(id+"F0.wireOp",EDGE,"E1836"),sQuery(id+"F0.wireOp",EDGE,"E1837"),sQuery(id+"F0.wireOp",EDGE,"E1838"),sQuery(id+"F0.wireOp",EDGE,"E1839"),sQuery(id+"F0.wireOp",EDGE,"E1840"),sQuery(id+"F0.wireOp",EDGE,"E1841"),sQuery(id+"F0.wireOp",EDGE,"E1842"),sQuery(id+"F0.wireOp",EDGE,"E1843"),sQuery(id+"F0.wireOp",EDGE,"E1844"),sQuery(id+"F0.wireOp",EDGE,"E1845"),sQuery(id+"F0.wireOp",EDGE,"E1846"),sQuery(id+"F0.wireOp",EDGE,"E1847"),sQuery(id+"F0.wireOp",EDGE,"E1848"),sQuery(id+"F0.wireOp",EDGE,"E1849"),sQuery(id+"F0.wireOp",EDGE,"E1850"),sQuery(id+"F0.wireOp",EDGE,"E1851"),sQuery(id+"F0.wireOp",EDGE,"E1852"),sQuery(id+"F0.wireOp",EDGE,"E1853"),sQuery(id+"F0.wireOp",EDGE,"E1854"),sQuery(id+"F0.wireOp",EDGE,"E1855"),sQuery(id+"F0.wireOp",EDGE,"E1856"),sQuery(id+"F0.wireOp",EDGE,"E1857"),sQuery(id+"F0.wireOp",EDGE,"E1858"),sQuery(id+"F0.wireOp",EDGE,"E1859"),sQuery(id+"F0.wireOp",EDGE,"E1860"),sQuery(id+"F0.wireOp",EDGE,"E1861"),sQuery(id+"F0.wireOp",EDGE,"E1862"),sQuery(id+"F0.wireOp",EDGE,"E1863"),sQuery(id+"F0.wireOp",EDGE,"E1864"),sQuery(id+"F0.wireOp",EDGE,"E1865"),sQuery(id+"F0.wireOp",EDGE,"E1866"),sQuery(id+"F0.wireOp",EDGE,"E1867"),sQuery(id+"F0.wireOp",EDGE,"E1868"),sQuery(id+"F0.wireOp",EDGE,"E1869"),sQuery(id+"F0.wireOp",EDGE,"E1870"),sQuery(id+"F0.wireOp",EDGE,"E1871"),sQuery(id+"F0.wireOp",EDGE,"E1872"),sQuery(id+"F0.wireOp",EDGE,"E1873"),sQuery(id+"F0.wireOp",EDGE,"E1874"),sQuery(id+"F0.wireOp",EDGE,"E1875"),sQuery(id+"F0.wireOp",EDGE,"E1876"),sQuery(id+"F0.wireOp",EDGE,"E1877"),sQuery(id+"F0.wireOp",EDGE,"E1878"),sQuery(id+"F0.wireOp",EDGE,"E1879"),sQuery(id+"F0.wireOp",EDGE,"E1880"),sQuery(id+"F0.wireOp",EDGE,"E1881"),sQuery(id+"F0.wireOp",EDGE,"E1882"),sQuery(id+"F0.wireOp",EDGE,"E1883"),sQuery(id+"F0.wireOp",EDGE,"E1884"),sQuery(id+"F0.wireOp",EDGE,"E1885"),sQuery(id+"F0.wireOp",EDGE,"E1886"),sQuery(id+"F0.wireOp",EDGE,"E1887"),sQuery(id+"F0.wireOp",EDGE,"E1888"),sQuery(id+"F0.wireOp",EDGE,"E1889"),sQuery(id+"F0.wireOp",EDGE,"E1890"),sQuery(id+"F0.wireOp",EDGE,"E1891"),sQuery(id+"F0.wireOp",EDGE,"E1892"),sQuery(id+"F0.wireOp",EDGE,"E1893"),sQuery(id+"F0.wireOp",EDGE,"E1894"),sQuery(id+"F0.wireOp",EDGE,"E1895"),sQuery(id+"F0.wireOp",EDGE,"E1896"),sQuery(id+"F0.wireOp",EDGE,"E1897"),sQuery(id+"F0.wireOp",EDGE,"E1898"),sQuery(id+"F0.wireOp",EDGE,"E1899"),sQuery(id+"F0.wireOp",EDGE,"E1900"),sQuery(id+"F0.wireOp",EDGE,"E1901"),sQuery(id+"F0.wireOp",EDGE,"E1902"),sQuery(id+"F0.wireOp",EDGE,"E1903"),sQuery(id+"F0.wireOp",EDGE,"E1904"),sQuery(id+"F0.wireOp",EDGE,"E1905"),sQuery(id+"F0.wireOp",EDGE,"E1906"),sQuery(id+"F0.wireOp",EDGE,"E1907"),sQuery(id+"F0.wireOp",EDGE,"E1908"),sQuery(id+"F0.wireOp",EDGE,"E1909"),sQuery(id+"F0.wireOp",EDGE,"E1910"),sQuery(id+"F0.wireOp",EDGE,"E1911"),sQuery(id+"F0.wireOp",EDGE,"E1912"),sQuery(id+"F0.wireOp",EDGE,"E1913"),sQuery(id+"F0.wireOp",EDGE,"E1914"),sQuery(id+"F0.wireOp",EDGE,"E1915"),sQuery(id+"F0.wireOp",EDGE,"E1916"),sQuery(id+"F0.wireOp",EDGE,"E1917"),sQuery(id+"F0.wireOp",EDGE,"E1918"),sQuery(id+"F0.wireOp",EDGE,"E1919"),sQuery(id+"F0.wireOp",EDGE,"E1920"),sQuery(id+"F0.wireOp",EDGE,"E1921"),sQuery(id+"F0.wireOp",EDGE,"E1922"),sQuery(id+"F0.wireOp",EDGE,"E1923"),sQuery(id+"F0.wireOp",EDGE,"E1924"),sQuery(id+"F0.wireOp",EDGE,"E1925"),sQuery(id+"F0.wireOp",EDGE,"E1926"),sQuery(id+"F0.wireOp",EDGE,"E1927"),sQuery(id+"F0.wireOp",EDGE,"E1928"),sQuery(id+"F0.wireOp",EDGE,"E1929"),sQuery(id+"F0.wireOp",EDGE,"E1930"),sQuery(id+"F0.wireOp",EDGE,"E1931"),sQuery(id+"F0.wireOp",EDGE,"E1932"),sQuery(id+"F0.wireOp",EDGE,"E1933"),sQuery(id+"F0.wireOp",EDGE,"E1934"),sQuery(id+"F0.wireOp",EDGE,"E1935"),sQuery(id+"F0.wireOp",EDGE,"E1936"),sQuery(id+"F0.wireOp",EDGE,"E1937"),sQuery(id+"F0.wireOp",EDGE,"E1938"),sQuery(id+"F0.wireOp",EDGE,"E1939"),sQuery(id+"F0.wireOp",EDGE,"E1940"),sQuery(id+"F0.wireOp",EDGE,"E1941"),sQuery(id+"F0.wireOp",EDGE,"E1942"),sQuery(id+"F0.wireOp",EDGE,"E1943"),sQuery(id+"F0.wireOp",EDGE,"E1944"),sQuery(id+"F0.wireOp",EDGE,"E1945"),sQuery(id+"F0.wireOp",EDGE,"E1946"),sQuery(id+"F0.wireOp",EDGE,"E1947"),sQuery(id+"F0.wireOp",EDGE,"E1948"),sQuery(id+"F0.wireOp",EDGE,"E1949"),sQuery(id+"F0.wireOp",EDGE,"E1950"),sQuery(id+"F0.wireOp",EDGE,"E1951"),sQuery(id+"F0.wireOp",EDGE,"E1952"),sQuery(id+"F0.wireOp",EDGE,"E1953"),sQuery(id+"F0.wireOp",EDGE,"E1954"),sQuery(id+"F0.wireOp",EDGE,"E1955"),sQuery(id+"F0.wireOp",EDGE,"E1956"),sQuery(id+"F0.wireOp",EDGE,"E1957"),sQuery(id+"F0.wireOp",EDGE,"E1958"),sQuery(id+"F0.wireOp",EDGE,"E1959"),sQuery(id+"F0.wireOp",EDGE,"E1960"),sQuery(id+"F0.wireOp",EDGE,"E1961"),sQuery(id+"F0.wireOp",EDGE,"E1962"),sQuery(id+"F0.wireOp",EDGE,"E1963"),sQuery(id+"F0.wireOp",EDGE,"E1964"),sQuery(id+"F0.wireOp",EDGE,"E1965"),sQuery(id+"F0.wireOp",EDGE,"E1966"),sQuery(id+"F0.wireOp",EDGE,"E1967"),sQuery(id+"F0.wireOp",EDGE,"E1968"),sQuery(id+"F0.wireOp",EDGE,"E1969"),sQuery(id+"F0.wireOp",EDGE,"E1970"),sQuery(id+"F0.wireOp",EDGE,"E1971"),sQuery(id+"F0.wireOp",EDGE,"E1972"),sQuery(id+"F0.wireOp",EDGE,"E1973"),sQuery(id+"F0.wireOp",EDGE,"E1974"),sQuery(id+"F0.wireOp",EDGE,"E1975"),sQuery(id+"F0.wireOp",EDGE,"E1976"),sQuery(id+"F0.wireOp",EDGE,"E1977"),sQuery(id+"F0.wireOp",EDGE,"E1978"),sQuery(id+"F0.wireOp",EDGE,"E1979"),sQuery(id+"F0.wireOp",EDGE,"E1980"),sQuery(id+"F0.wireOp",EDGE,"E1981"),sQuery(id+"F0.wireOp",EDGE,"E1982"),sQuery(id+"F0.wireOp",EDGE,"E1983"),sQuery(id+"F0.wireOp",EDGE,"E1984"),sQuery(id+"F0.wireOp",EDGE,"E1985"),sQuery(id+"F0.wireOp",EDGE,"E1986"),sQuery(id+"F0.wireOp",EDGE,"E1987"),sQuery(id+"F0.wireOp",EDGE,"E1988"),sQuery(id+"F0.wireOp",EDGE,"E1989"),sQuery(id+"F0.wireOp",EDGE,"E1990"),sQuery(id+"F0.wireOp",EDGE,"E1991"),sQuery(id+"F0.wireOp",EDGE,"E1992"),sQuery(id+"F0.wireOp",EDGE,"E1993"),sQuery(id+"F0.wireOp",EDGE,"E1994"),sQuery(id+"F0.wireOp",EDGE,"E1995"),sQuery(id+"F0.wireOp",EDGE,"E1996"),sQuery(id+"F0.wireOp",EDGE,"E1997"),sQuery(id+"F0.wireOp",EDGE,"E1998"),sQuery(id+"F0.wireOp",EDGE,"E1999"),sQuery(id+"F0.wireOp",EDGE,"E2000"),sQuery(id+"F0.wireOp",EDGE,"E2001"),sQuery(id+"F0.wireOp",EDGE,"E2002"),sQuery(id+"F0.wireOp",EDGE,"E2003"),sQuery(id+"F0.wireOp",EDGE,"E2004"),sQuery(id+"F0.wireOp",EDGE,"E2005"),sQuery(id+"F0.wireOp",EDGE,"E2006"),sQuery(id+"F0.wireOp",EDGE,"E2007"),sQuery(id+"F0.wireOp",EDGE,"E2008"),sQuery(id+"F0.wireOp",EDGE,"E2009"),sQuery(id+"F0.wireOp",EDGE,"E2010"),sQuery(id+"F0.wireOp",EDGE,"E2011"),sQuery(id+"F0.wireOp",EDGE,"E2012"),sQuery(id+"F0.wireOp",EDGE,"E2013"),sQuery(id+"F0.wireOp",EDGE,"E2014"),sQuery(id+"F0.wireOp",EDGE,"E2015"),sQuery(id+"F0.wireOp",EDGE,"E2016"),sQuery(id+"F0.wireOp",EDGE,"E2017"),sQuery(id+"F0.wireOp",EDGE,"E2018"),sQuery(id+"F0.wireOp",EDGE,"E2019"),sQuery(id+"F0.wireOp",EDGE,"E2020"),sQuery(id+"F0.wireOp",EDGE,"E2021"),sQuery(id+"F0.wireOp",EDGE,"E2022"),sQuery(id+"F0.wireOp",EDGE,"E2023"),sQuery(id+"F0.wireOp",EDGE,"E2024"),sQuery(id+"F0.wireOp",EDGE,"E2025"),sQuery(id+"F0.wireOp",EDGE,"E2026"),sQuery(id+"F0.wireOp",EDGE,"E2027"),sQuery(id+"F0.wireOp",EDGE,"E2028"),sQuery(id+"F0.wireOp",EDGE,"E2029"),sQuery(id+"F0.wireOp",EDGE,"E2030"),sQuery(id+"F0.wireOp",EDGE,"E2031"),sQuery(id+"F0.wireOp",EDGE,"E2032"),sQuery(id+"F0.wireOp",EDGE,"E2033"),sQuery(id+"F0.wireOp",EDGE,"E2034"),sQuery(id+"F0.wireOp",EDGE,"E2035"),sQuery(id+"F0.wireOp",EDGE,"E2036"),sQuery(id+"F0.wireOp",EDGE,"E2037"),sQuery(id+"F0.wireOp",EDGE,"E2038"),sQuery(id+"F0.wireOp",EDGE,"E2039"),sQuery(id+"F0.wireOp",EDGE,"E2040"),sQuery(id+"F0.wireOp",EDGE,"E2041"),sQuery(id+"F0.wireOp",EDGE,"E2042"),sQuery(id+"F0.wireOp",EDGE,"E2043"),sQuery(id+"F0.wireOp",EDGE,"E2044"),sQuery(id+"F0.wireOp",EDGE,"E2045"),sQuery(id+"F0.wireOp",EDGE,"E2046"),sQuery(id+"F0.wireOp",EDGE,"E2047"),sQuery(id+"F0.wireOp",EDGE,"E2048"),sQuery(id+"F0.wireOp",EDGE,"E2049"),sQuery(id+"F0.wireOp",EDGE,"E2050"),sQuery(id+"F0.wireOp",EDGE,"E2051"),sQuery(id+"F0.wireOp",EDGE,"E2052"),sQuery(id+"F0.wireOp",EDGE,"E2053"),sQuery(id+"F0.wireOp",EDGE,"E2054"),sQuery(id+"F0.wireOp",EDGE,"E2055"),sQuery(id+"F0.wireOp",EDGE,"E2056"),sQuery(id+"F0.wireOp",EDGE,"E2057"),sQuery(id+"F0.wireOp",EDGE,"E2058"),sQuery(id+"F0.wireOp",EDGE,"E2059"),sQuery(id+"F0.wireOp",EDGE,"E2060"),sQuery(id+"F0.wireOp",EDGE,"E2061"),sQuery(id+"F0.wireOp",EDGE,"E2062"),sQuery(id+"F0.wireOp",EDGE,"E2063"),sQuery(id+"F0.wireOp",EDGE,"E2064"),sQuery(id+"F0.wireOp",EDGE,"E2065"),sQuery(id+"F0.wireOp",EDGE,"E2066"),sQuery(id+"F0.wireOp",EDGE,"E2067"),sQuery(id+"F0.wireOp",EDGE,"E2068"),sQuery(id+"F0.wireOp",EDGE,"E2069"),sQuery(id+"F0.wireOp",EDGE,"E2070"),sQuery(id+"F0.wireOp",EDGE,"E2071"),sQuery(id+"F0.wireOp",EDGE,"E2072"),sQuery(id+"F0.wireOp",EDGE,"E2073"),sQuery(id+"F0.wireOp",EDGE,"E2074"),sQuery(id+"F0.wireOp",EDGE,"E2075"),sQuery(id+"F0.wireOp",EDGE,"E2076"),sQuery(id+"F0.wireOp",EDGE,"E2077"),sQuery(id+"F0.wireOp",EDGE,"E2078"),sQuery(id+"F0.wireOp",EDGE,"E2079"),sQuery(id+"F0.wireOp",EDGE,"E2080"),sQuery(id+"F0.wireOp",EDGE,"E2081"),sQuery(id+"F0.wireOp",EDGE,"E2082"),sQuery(id+"F0.wireOp",EDGE,"E2083"),sQuery(id+"F0.wireOp",EDGE,"E2084"),sQuery(id+"F0.wireOp",EDGE,"E2085"),sQuery(id+"F0.wireOp",EDGE,"E2086"),sQuery(id+"F0.wireOp",EDGE,"E2087"),sQuery(id+"F0.wireOp",EDGE,"E2088"),sQuery(id+"F0.wireOp",EDGE,"E2089"),sQuery(id+"F0.wireOp",EDGE,"E2090"),sQuery(id+"F0.wireOp",EDGE,"E2091"),sQuery(id+"F0.wireOp",EDGE,"E2092"),sQuery(id+"F0.wireOp",EDGE,"E2093"),sQuery(id+"F0.wireOp",EDGE,"E2094"),sQuery(id+"F0.wireOp",EDGE,"E2095"),sQuery(id+"F0.wireOp",EDGE,"E2096"),sQuery(id+"F0.wireOp",EDGE,"E2097"),sQuery(id+"F0.wireOp",EDGE,"E2098"),sQuery(id+"F0.wireOp",EDGE,"E2099"),sQuery(id+"F0.wireOp",EDGE,"E2100"),sQuery(id+"F0.wireOp",EDGE,"E2101"),sQuery(id+"F0.wireOp",EDGE,"E2102"),sQuery(id+"F0.wireOp",EDGE,"E2103")])],"isStart":false});
            var sketch = newSketch(context, id + "F2", { "sketchPlane" : qUnion([Q0])});
            skCircle(sketch, "E2104", {"center": v(-2.2, 0) * mm, "radius": 9.75 * mm});
            skCircle(sketch, "E2105", {"center": v(-2.2, 0) * mm, "radius": 4.5 * mm});
            skSolve(sketch);
        }
        {
            var Q0;
            Q0=makeQuery(id+"F2.imprint","IMPRINT",FACE,{"disambiguationData":[TD([[makeQuery(id+"F2.imprint","IMPRINT",EDGE,{"derivedFrom":sQuery(id+"F2.wireOp",EDGE,"E2104")}),1.0]])]});
            extrude(context, id + "F3", {"entities" : qUnion([Q0]), "operationType" : NewBodyOperationType.ADD, "depth" : 1 * mm});
        }
        {
            var Q0;
            Q0=makeQuery(id+"F3.opExtrude","CAP_EDGE",EDGE,{"disambiguationData":[OSD([sQuery(id+"F2.wireOp",EDGE,"E2104")])],"isStart":false});
            fillet(context, id + "F4", {"entities" : qUnion([Q0]), "radius" : 0.4 * mm, "tangentPropagation" : true, "allowEdgeOverflow" : false});
        }
    });
